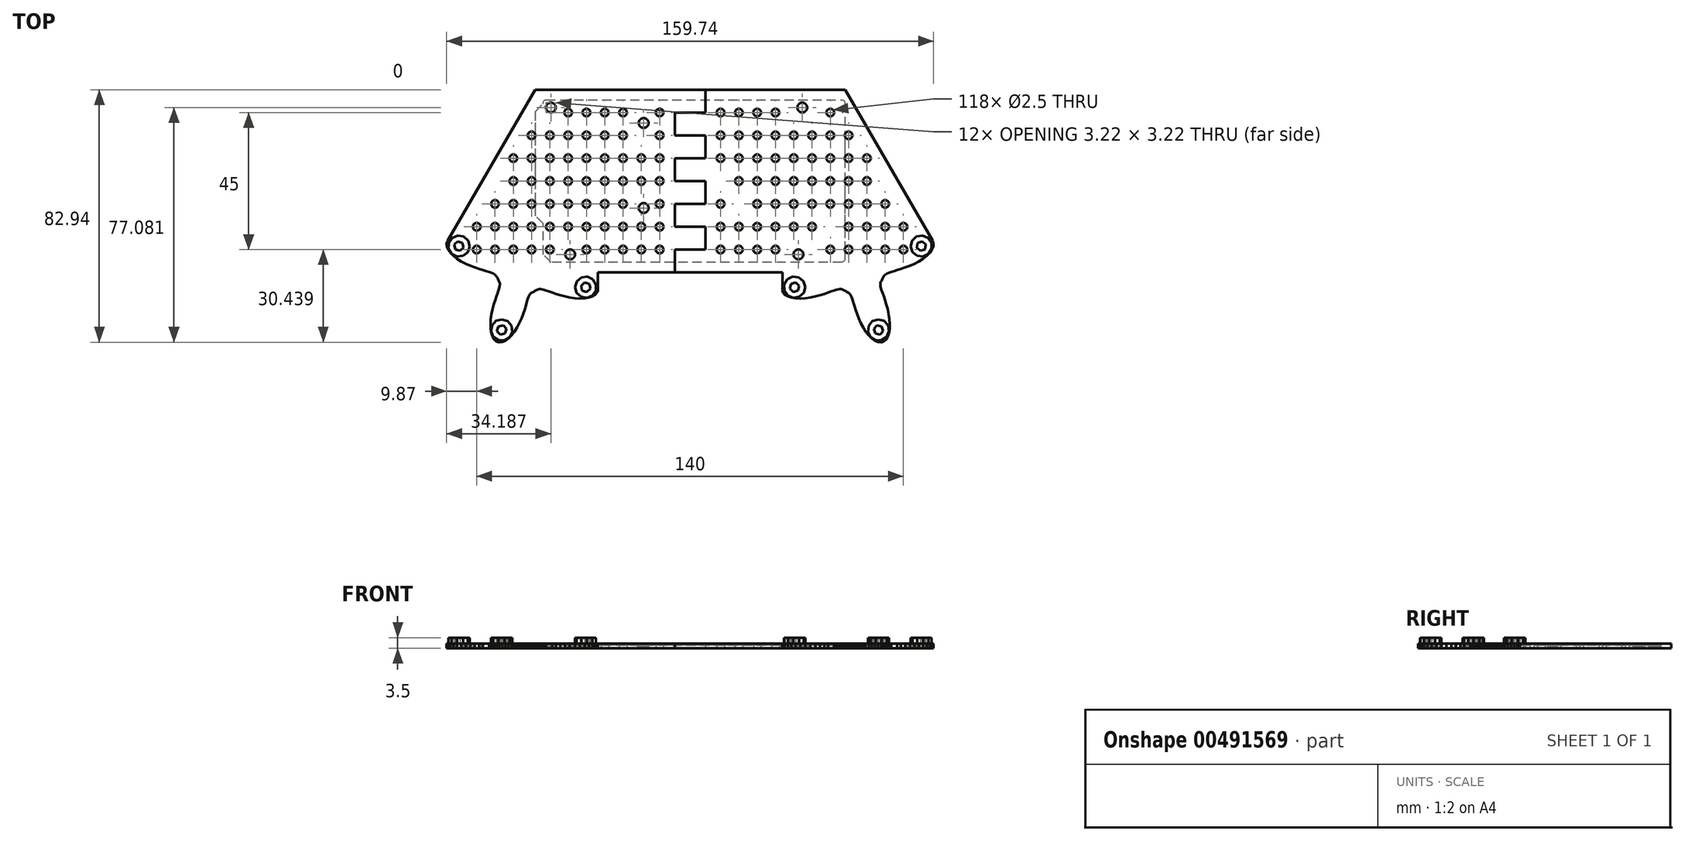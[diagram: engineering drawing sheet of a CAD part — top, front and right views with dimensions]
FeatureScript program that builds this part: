
annotation { "Feature Type Name" : "Feature", "Feature Type Description" : "" }
export const myFeature = defineFeature(function(context is Context, id is Id, definition is map)
    precondition{}
    {
        {
            var Q0;
            Q0=qCreatedBy(makeId("Top.planeOp"),FACE);
            var sketch = newSketch(context, id + "F0", { "sketchPlane" : qUnion([Q0])});
            skLineSegment(sketch, "E0", {"start": v(78.21, 11.15) * mm, "end": v(79.23, 12.84) * mm});
            skLineSegment(sketch, "E1", {"start": v(79.23, 12.84) * mm, "end": v(79.17, 14.81) * mm});
            skLineSegment(sketch, "E2", {"start": v(79.17, 14.81) * mm, "end": v(78.06, 16.44) * mm});
            skLineSegment(sketch, "E3", {"start": v(78.06, 16.44) * mm, "end": v(76.24, 17.2) * mm});
            skLineSegment(sketch, "E4", {"start": v(76.24, 17.2) * mm, "end": v(74.3, 16.87) * mm});
            skLineSegment(sketch, "E5", {"start": v(74.3, 16.87) * mm, "end": v(72.85, 15.54) * mm});
            skLineSegment(sketch, "E6", {"start": v(72.85, 15.54) * mm, "end": v(72.35, 13.63) * mm});
            skLineSegment(sketch, "E7", {"start": v(72.35, 13.63) * mm, "end": v(72.96, 11.76) * mm});
            skLineSegment(sketch, "E8", {"start": v(72.96, 11.76) * mm, "end": v(74.48, 10.5) * mm});
            skLineSegment(sketch, "E9", {"start": v(74.48, 10.5) * mm, "end": v(76.44, 10.28) * mm});
            skLineSegment(sketch, "E10", {"start": v(76.44, 10.28) * mm, "end": v(78.21, 11.15) * mm});
            skLineSegment(sketch, "E11", {"start": v(74.32, 13.24) * mm, "end": v(74.66, 14.8) * mm});
            skLineSegment(sketch, "E12", {"start": v(74.66, 14.8) * mm, "end": v(76.18, 15.3) * mm});
            skLineSegment(sketch, "E13", {"start": v(76.18, 15.3) * mm, "end": v(77.37, 14.23) * mm});
            skLineSegment(sketch, "E14", {"start": v(77.37, 14.23) * mm, "end": v(77.03, 12.66) * mm});
            skLineSegment(sketch, "E15", {"start": v(77.03, 12.66) * mm, "end": v(75.51, 12.17) * mm});
            skLineSegment(sketch, "E16", {"start": v(75.51, 12.17) * mm, "end": v(74.32, 13.24) * mm});
            skLineSegment(sketch, "E17", {"start": v(-74.48, 10.5) * mm, "end": v(-72.96, 11.76) * mm});
            skLineSegment(sketch, "E18", {"start": v(-72.96, 11.76) * mm, "end": v(-72.35, 13.63) * mm});
            skLineSegment(sketch, "E19", {"start": v(-72.35, 13.63) * mm, "end": v(-72.85, 15.54) * mm});
            skLineSegment(sketch, "E20", {"start": v(-72.85, 15.54) * mm, "end": v(-74.3, 16.87) * mm});
            skLineSegment(sketch, "E21", {"start": v(-74.3, 16.87) * mm, "end": v(-76.24, 17.2) * mm});
            skLineSegment(sketch, "E22", {"start": v(-76.24, 17.2) * mm, "end": v(-78.06, 16.44) * mm});
            skLineSegment(sketch, "E23", {"start": v(-78.06, 16.44) * mm, "end": v(-79.17, 14.81) * mm});
            skLineSegment(sketch, "E24", {"start": v(-79.17, 14.81) * mm, "end": v(-79.23, 12.84) * mm});
            skLineSegment(sketch, "E25", {"start": v(-79.23, 12.84) * mm, "end": v(-78.21, 11.15) * mm});
            skLineSegment(sketch, "E26", {"start": v(-78.21, 11.15) * mm, "end": v(-76.44, 10.28) * mm});
            skLineSegment(sketch, "E27", {"start": v(-76.44, 10.28) * mm, "end": v(-74.48, 10.5) * mm});
            skLineSegment(sketch, "E28", {"start": v(-77.03, 12.66) * mm, "end": v(-77.37, 14.23) * mm});
            skLineSegment(sketch, "E29", {"start": v(-77.37, 14.23) * mm, "end": v(-76.18, 15.3) * mm});
            skLineSegment(sketch, "E30", {"start": v(-76.18, 15.3) * mm, "end": v(-74.66, 14.8) * mm});
            skLineSegment(sketch, "E31", {"start": v(-74.66, 14.8) * mm, "end": v(-74.32, 13.24) * mm});
            skLineSegment(sketch, "E32", {"start": v(-74.32, 13.24) * mm, "end": v(-75.51, 12.17) * mm});
            skLineSegment(sketch, "E33", {"start": v(-75.51, 12.17) * mm, "end": v(-77.03, 12.66) * mm});
            skLineSegment(sketch, "E34", {"start": v(-32.03, -2.5) * mm, "end": v(-30.92, -0.87) * mm});
            skLineSegment(sketch, "E35", {"start": v(-30.92, -0.87) * mm, "end": v(-30.86, 1.1) * mm});
            skLineSegment(sketch, "E36", {"start": v(-30.86, 1.1) * mm, "end": v(-31.88, 2.8) * mm});
            skLineSegment(sketch, "E37", {"start": v(-31.88, 2.8) * mm, "end": v(-33.65, 3.67) * mm});
            skLineSegment(sketch, "E38", {"start": v(-33.65, 3.67) * mm, "end": v(-35.6, 3.44) * mm});
            skLineSegment(sketch, "E39", {"start": v(-35.6, 3.44) * mm, "end": v(-37.13, 2.2) * mm});
            skLineSegment(sketch, "E40", {"start": v(-37.13, 2.2) * mm, "end": v(-37.74, 0.32) * mm});
            skLineSegment(sketch, "E41", {"start": v(-37.74, 0.32) * mm, "end": v(-37.24, -1.6) * mm});
            skLineSegment(sketch, "E42", {"start": v(-37.24, -1.6) * mm, "end": v(-35.79, -2.92) * mm});
            skLineSegment(sketch, "E43", {"start": v(-35.79, -2.92) * mm, "end": v(-33.85, -3.26) * mm});
            skLineSegment(sketch, "E44", {"start": v(-33.85, -3.26) * mm, "end": v(-32.03, -2.5) * mm});
            skLineSegment(sketch, "E45", {"start": v(-35.43, -0.85) * mm, "end": v(-35.77, 0.71) * mm});
            skLineSegment(sketch, "E46", {"start": v(-35.77, 0.71) * mm, "end": v(-34.58, 1.78) * mm});
            skLineSegment(sketch, "E47", {"start": v(-34.58, 1.78) * mm, "end": v(-33.06, 1.29) * mm});
            skLineSegment(sketch, "E48", {"start": v(-33.06, 1.29) * mm, "end": v(-32.72, -0.28) * mm});
            skLineSegment(sketch, "E49", {"start": v(-32.72, -0.28) * mm, "end": v(-33.91, -1.35) * mm});
            skLineSegment(sketch, "E50", {"start": v(-33.91, -1.35) * mm, "end": v(-35.43, -0.85) * mm});
            skLineSegment(sketch, "E51", {"start": v(35.79, -2.92) * mm, "end": v(37.24, -1.6) * mm});
            skLineSegment(sketch, "E52", {"start": v(37.24, -1.6) * mm, "end": v(37.74, 0.32) * mm});
            skLineSegment(sketch, "E53", {"start": v(37.74, 0.32) * mm, "end": v(37.13, 2.2) * mm});
            skLineSegment(sketch, "E54", {"start": v(37.13, 2.2) * mm, "end": v(35.6, 3.44) * mm});
            skLineSegment(sketch, "E55", {"start": v(35.6, 3.44) * mm, "end": v(33.65, 3.67) * mm});
            skLineSegment(sketch, "E56", {"start": v(33.65, 3.67) * mm, "end": v(31.88, 2.8) * mm});
            skLineSegment(sketch, "E57", {"start": v(31.88, 2.8) * mm, "end": v(30.86, 1.1) * mm});
            skLineSegment(sketch, "E58", {"start": v(30.86, 1.1) * mm, "end": v(30.92, -0.87) * mm});
            skLineSegment(sketch, "E59", {"start": v(30.92, -0.87) * mm, "end": v(32.03, -2.5) * mm});
            skLineSegment(sketch, "E60", {"start": v(32.03, -2.5) * mm, "end": v(33.85, -3.26) * mm});
            skLineSegment(sketch, "E61", {"start": v(33.85, -3.26) * mm, "end": v(35.79, -2.92) * mm});
            skLineSegment(sketch, "E62", {"start": v(32.72, -0.28) * mm, "end": v(33.06, 1.29) * mm});
            skLineSegment(sketch, "E63", {"start": v(33.06, 1.29) * mm, "end": v(34.58, 1.78) * mm});
            skLineSegment(sketch, "E64", {"start": v(34.58, 1.78) * mm, "end": v(35.77, 0.71) * mm});
            skLineSegment(sketch, "E65", {"start": v(35.77, 0.71) * mm, "end": v(35.43, -0.85) * mm});
            skLineSegment(sketch, "E66", {"start": v(35.43, -0.85) * mm, "end": v(33.91, -1.35) * mm});
            skLineSegment(sketch, "E67", {"start": v(33.91, -1.35) * mm, "end": v(32.72, -0.28) * mm});
            skLineSegment(sketch, "E68", {"start": v(62.88, -17.15) * mm, "end": v(64.51, -16.04) * mm});
            skLineSegment(sketch, "E69", {"start": v(64.51, -16.04) * mm, "end": v(65.28, -14.22) * mm});
            skLineSegment(sketch, "E70", {"start": v(65.28, -14.22) * mm, "end": v(64.94, -12.28) * mm});
            skLineSegment(sketch, "E71", {"start": v(64.94, -12.28) * mm, "end": v(63.61, -10.83) * mm});
            skLineSegment(sketch, "E72", {"start": v(63.61, -10.83) * mm, "end": v(61.7, -10.33) * mm});
            skLineSegment(sketch, "E73", {"start": v(61.7, -10.33) * mm, "end": v(59.83, -10.94) * mm});
            skLineSegment(sketch, "E74", {"start": v(59.83, -10.94) * mm, "end": v(58.58, -12.46) * mm});
            skLineSegment(sketch, "E75", {"start": v(58.58, -12.46) * mm, "end": v(58.35, -14.42) * mm});
            skLineSegment(sketch, "E76", {"start": v(58.35, -14.42) * mm, "end": v(59.22, -16.2) * mm});
            skLineSegment(sketch, "E77", {"start": v(59.22, -16.2) * mm, "end": v(60.91, -17.2) * mm});
            skLineSegment(sketch, "E78", {"start": v(60.91, -17.2) * mm, "end": v(62.88, -17.15) * mm});
            skLineSegment(sketch, "E79", {"start": v(60.73, -15.01) * mm, "end": v(60.24, -13.5) * mm});
            skLineSegment(sketch, "E80", {"start": v(60.24, -13.5) * mm, "end": v(61.3, -12.3) * mm});
            skLineSegment(sketch, "E81", {"start": v(61.3, -12.3) * mm, "end": v(62.87, -12.64) * mm});
            skLineSegment(sketch, "E82", {"start": v(62.87, -12.64) * mm, "end": v(63.37, -14.16) * mm});
            skLineSegment(sketch, "E83", {"start": v(63.37, -14.16) * mm, "end": v(62.3, -15.35) * mm});
            skLineSegment(sketch, "E84", {"start": v(62.3, -15.35) * mm, "end": v(60.73, -15.01) * mm});
            skLineSegment(sketch, "E85", {"start": v(-59.22, -16.2) * mm, "end": v(-58.35, -14.42) * mm});
            skLineSegment(sketch, "E86", {"start": v(-58.35, -14.42) * mm, "end": v(-58.58, -12.46) * mm});
            skLineSegment(sketch, "E87", {"start": v(-58.58, -12.46) * mm, "end": v(-59.83, -10.94) * mm});
            skLineSegment(sketch, "E88", {"start": v(-59.83, -10.94) * mm, "end": v(-61.7, -10.33) * mm});
            skLineSegment(sketch, "E89", {"start": v(-61.7, -10.33) * mm, "end": v(-63.61, -10.83) * mm});
            skLineSegment(sketch, "E90", {"start": v(-63.61, -10.83) * mm, "end": v(-64.94, -12.28) * mm});
            skLineSegment(sketch, "E91", {"start": v(-64.94, -12.28) * mm, "end": v(-65.28, -14.22) * mm});
            skLineSegment(sketch, "E92", {"start": v(-65.28, -14.22) * mm, "end": v(-64.51, -16.04) * mm});
            skLineSegment(sketch, "E93", {"start": v(-64.51, -16.04) * mm, "end": v(-62.88, -17.15) * mm});
            skLineSegment(sketch, "E94", {"start": v(-62.88, -17.15) * mm, "end": v(-60.91, -17.2) * mm});
            skLineSegment(sketch, "E95", {"start": v(-60.91, -17.2) * mm, "end": v(-59.22, -16.2) * mm});
            skLineSegment(sketch, "E96", {"start": v(-63.37, -14.16) * mm, "end": v(-62.87, -12.64) * mm});
            skLineSegment(sketch, "E97", {"start": v(-62.87, -12.64) * mm, "end": v(-61.3, -12.3) * mm});
            skLineSegment(sketch, "E98", {"start": v(-61.3, -12.3) * mm, "end": v(-60.24, -13.5) * mm});
            skLineSegment(sketch, "E99", {"start": v(-60.24, -13.5) * mm, "end": v(-60.73, -15.01) * mm});
            skLineSegment(sketch, "E100", {"start": v(-60.73, -15.01) * mm, "end": v(-62.3, -15.35) * mm});
            skLineSegment(sketch, "E101", {"start": v(-62.3, -15.35) * mm, "end": v(-63.37, -14.16) * mm});
            skSolve(sketch);
        }
        {
            var Q0;
            Q0=qCreatedBy(makeId("Top.planeOp"),FACE);
            var sketch = newSketch(context, id + "F1", { "sketchPlane" : qUnion([Q0])});
            skLineSegment(sketch, "E102", {"start": v(63.5, -41.19) * mm, "end": v(64.23, -40.57) * mm});
            skLineSegment(sketch, "E103", {"start": v(64.23, -40.57) * mm, "end": v(64.8, -39.65) * mm});
            skLineSegment(sketch, "E104", {"start": v(64.8, -39.65) * mm, "end": v(65.22, -38.46) * mm});
            skLineSegment(sketch, "E105", {"start": v(65.22, -38.46) * mm, "end": v(65.45, -37.06) * mm});
            skLineSegment(sketch, "E106", {"start": v(65.45, -37.06) * mm, "end": v(65.5, -35.5) * mm});
            skLineSegment(sketch, "E107", {"start": v(65.5, -35.5) * mm, "end": v(65.4, -33.87) * mm});
            skLineSegment(sketch, "E108", {"start": v(65.4, -33.87) * mm, "end": v(65.15, -32.21) * mm});
            skLineSegment(sketch, "E109", {"start": v(65.15, -32.21) * mm, "end": v(64.81, -30.6) * mm});
            skLineSegment(sketch, "E110", {"start": v(64.81, -30.6) * mm, "end": v(64.4, -29.07) * mm});
            skLineSegment(sketch, "E111", {"start": v(64.4, -29.07) * mm, "end": v(63.97, -27.67) * mm});
            skLineSegment(sketch, "E112", {"start": v(63.97, -27.67) * mm, "end": v(63.55, -26.43) * mm});
            skLineSegment(sketch, "E113", {"start": v(63.55, -26.43) * mm, "end": v(63.16, -25.35) * mm});
            skLineSegment(sketch, "E114", {"start": v(63.16, -25.35) * mm, "end": v(62.84, -24.44) * mm});
            skLineSegment(sketch, "E115", {"start": v(62.84, -24.44) * mm, "end": v(62.6, -23.7) * mm});
            skLineSegment(sketch, "E116", {"start": v(62.6, -23.7) * mm, "end": v(62.46, -23.1) * mm});
            skLineSegment(sketch, "E117", {"start": v(62.46, -23.1) * mm, "end": v(62.4, -22.6) * mm});
            skLineSegment(sketch, "E118", {"start": v(62.4, -22.6) * mm, "end": v(62.42, -22.2) * mm});
            skLineSegment(sketch, "E119", {"start": v(62.42, -22.2) * mm, "end": v(62.5, -21.86) * mm});
            skLineSegment(sketch, "E120", {"start": v(62.5, -21.86) * mm, "end": v(62.62, -21.56) * mm});
            skLineSegment(sketch, "E121", {"start": v(62.62, -21.56) * mm, "end": v(62.77, -21.28) * mm});
            skLineSegment(sketch, "E122", {"start": v(62.77, -21.28) * mm, "end": v(62.92, -21) * mm});
            skLineSegment(sketch, "E123", {"start": v(62.92, -21) * mm, "end": v(63.06, -20.73) * mm});
            skLineSegment(sketch, "E124", {"start": v(63.06, -20.73) * mm, "end": v(63.2, -20.45) * mm});
            skLineSegment(sketch, "E125", {"start": v(63.2, -20.45) * mm, "end": v(63.34, -20.16) * mm});
            skLineSegment(sketch, "E126", {"start": v(63.34, -20.16) * mm, "end": v(63.48, -19.88) * mm});
            skLineSegment(sketch, "E127", {"start": v(63.48, -19.88) * mm, "end": v(63.65, -19.6) * mm});
            skLineSegment(sketch, "E128", {"start": v(63.65, -19.6) * mm, "end": v(63.87, -19.34) * mm});
            skLineSegment(sketch, "E129", {"start": v(63.87, -19.34) * mm, "end": v(64.19, -19.1) * mm});
            skLineSegment(sketch, "E130", {"start": v(64.19, -19.1) * mm, "end": v(64.62, -18.86) * mm});
            skLineSegment(sketch, "E131", {"start": v(64.62, -18.86) * mm, "end": v(65.2, -18.62) * mm});
            skLineSegment(sketch, "E132", {"start": v(65.2, -18.62) * mm, "end": v(65.94, -18.37) * mm});
            skLineSegment(sketch, "E133", {"start": v(65.94, -18.37) * mm, "end": v(66.86, -18.1) * mm});
            skLineSegment(sketch, "E134", {"start": v(66.86, -18.1) * mm, "end": v(67.95, -17.77) * mm});
            skLineSegment(sketch, "E135", {"start": v(67.95, -17.77) * mm, "end": v(69.21, -17.39) * mm});
            skLineSegment(sketch, "E136", {"start": v(69.21, -17.39) * mm, "end": v(70.6, -16.92) * mm});
            skLineSegment(sketch, "E137", {"start": v(70.6, -16.92) * mm, "end": v(72.07, -16.35) * mm});
            skLineSegment(sketch, "E138", {"start": v(72.07, -16.35) * mm, "end": v(73.58, -15.67) * mm});
            skLineSegment(sketch, "E139", {"start": v(73.58, -15.67) * mm, "end": v(75.06, -14.9) * mm});
            skLineSegment(sketch, "E140", {"start": v(75.06, -14.9) * mm, "end": v(76.45, -14.02) * mm});
            skLineSegment(sketch, "E141", {"start": v(76.45, -14.02) * mm, "end": v(77.67, -13.06) * mm});
            skLineSegment(sketch, "E142", {"start": v(77.67, -13.06) * mm, "end": v(78.67, -12.05) * mm});
            skLineSegment(sketch, "E143", {"start": v(78.67, -12.05) * mm, "end": v(79.4, -11.02) * mm});
            skLineSegment(sketch, "E144", {"start": v(79.4, -11.02) * mm, "end": v(79.8, -10.01) * mm});
            skLineSegment(sketch, "E145", {"start": v(79.8, -10.01) * mm, "end": v(79.87, -9.06) * mm});
            skLineSegment(sketch, "E146", {"start": v(79.87, -9.06) * mm, "end": v(79.59, -8.2) * mm});
            skLineSegment(sketch, "E147", {"start": v(79.59, -8.2) * mm, "end": v(79.56, -8.15) * mm});
            skLineSegment(sketch, "E148", {"start": v(79.56, -8.15) * mm, "end": v(50.85, 41.47) * mm});
            skLineSegment(sketch, "E149", {"start": v(50.85, 41.47) * mm, "end": v(-50.85, 41.47) * mm});
            skLineSegment(sketch, "E150", {"start": v(-50.85, 41.47) * mm, "end": v(-79.56, -8.15) * mm});
            skLineSegment(sketch, "E151", {"start": v(-79.56, -8.15) * mm, "end": v(-79.59, -8.2) * mm});
            skLineSegment(sketch, "E152", {"start": v(-79.59, -8.2) * mm, "end": v(-79.87, -9.06) * mm});
            skLineSegment(sketch, "E153", {"start": v(-79.87, -9.06) * mm, "end": v(-79.8, -10.01) * mm});
            skLineSegment(sketch, "E154", {"start": v(-79.8, -10.01) * mm, "end": v(-79.4, -11.02) * mm});
            skLineSegment(sketch, "E155", {"start": v(-79.4, -11.02) * mm, "end": v(-78.67, -12.05) * mm});
            skLineSegment(sketch, "E156", {"start": v(-78.67, -12.05) * mm, "end": v(-77.67, -13.06) * mm});
            skLineSegment(sketch, "E157", {"start": v(-77.67, -13.06) * mm, "end": v(-76.45, -14.02) * mm});
            skLineSegment(sketch, "E158", {"start": v(-76.45, -14.02) * mm, "end": v(-75.06, -14.9) * mm});
            skLineSegment(sketch, "E159", {"start": v(-75.06, -14.9) * mm, "end": v(-73.58, -15.67) * mm});
            skLineSegment(sketch, "E160", {"start": v(-73.58, -15.67) * mm, "end": v(-72.07, -16.35) * mm});
            skLineSegment(sketch, "E161", {"start": v(-72.07, -16.35) * mm, "end": v(-70.6, -16.92) * mm});
            skLineSegment(sketch, "E162", {"start": v(-70.6, -16.92) * mm, "end": v(-69.21, -17.39) * mm});
            skLineSegment(sketch, "E163", {"start": v(-69.21, -17.39) * mm, "end": v(-67.95, -17.77) * mm});
            skLineSegment(sketch, "E164", {"start": v(-67.95, -17.77) * mm, "end": v(-66.86, -18.1) * mm});
            skLineSegment(sketch, "E165", {"start": v(-66.86, -18.1) * mm, "end": v(-65.94, -18.37) * mm});
            skLineSegment(sketch, "E166", {"start": v(-65.94, -18.37) * mm, "end": v(-65.2, -18.62) * mm});
            skLineSegment(sketch, "E167", {"start": v(-65.2, -18.62) * mm, "end": v(-64.62, -18.86) * mm});
            skLineSegment(sketch, "E168", {"start": v(-64.62, -18.86) * mm, "end": v(-64.19, -19.1) * mm});
            skLineSegment(sketch, "E169", {"start": v(-64.19, -19.1) * mm, "end": v(-63.87, -19.34) * mm});
            skLineSegment(sketch, "E170", {"start": v(-63.87, -19.34) * mm, "end": v(-63.65, -19.6) * mm});
            skLineSegment(sketch, "E171", {"start": v(-63.65, -19.6) * mm, "end": v(-63.48, -19.88) * mm});
            skLineSegment(sketch, "E172", {"start": v(-63.48, -19.88) * mm, "end": v(-63.34, -20.16) * mm});
            skLineSegment(sketch, "E173", {"start": v(-63.34, -20.16) * mm, "end": v(-63.2, -20.45) * mm});
            skLineSegment(sketch, "E174", {"start": v(-63.2, -20.45) * mm, "end": v(-63.06, -20.73) * mm});
            skLineSegment(sketch, "E175", {"start": v(-63.06, -20.73) * mm, "end": v(-62.92, -21) * mm});
            skLineSegment(sketch, "E176", {"start": v(-62.92, -21) * mm, "end": v(-62.77, -21.28) * mm});
            skLineSegment(sketch, "E177", {"start": v(-62.77, -21.28) * mm, "end": v(-62.62, -21.56) * mm});
            skLineSegment(sketch, "E178", {"start": v(-62.62, -21.56) * mm, "end": v(-62.5, -21.86) * mm});
            skLineSegment(sketch, "E179", {"start": v(-62.5, -21.86) * mm, "end": v(-62.42, -22.2) * mm});
            skLineSegment(sketch, "E180", {"start": v(-62.42, -22.2) * mm, "end": v(-62.4, -22.6) * mm});
            skLineSegment(sketch, "E181", {"start": v(-62.4, -22.6) * mm, "end": v(-62.46, -23.1) * mm});
            skLineSegment(sketch, "E182", {"start": v(-62.46, -23.1) * mm, "end": v(-62.6, -23.7) * mm});
            skLineSegment(sketch, "E183", {"start": v(-62.6, -23.7) * mm, "end": v(-62.84, -24.44) * mm});
            skLineSegment(sketch, "E184", {"start": v(-62.84, -24.44) * mm, "end": v(-63.16, -25.35) * mm});
            skLineSegment(sketch, "E185", {"start": v(-63.16, -25.35) * mm, "end": v(-63.55, -26.43) * mm});
            skLineSegment(sketch, "E186", {"start": v(-63.55, -26.43) * mm, "end": v(-63.97, -27.67) * mm});
            skLineSegment(sketch, "E187", {"start": v(-63.97, -27.67) * mm, "end": v(-64.4, -29.07) * mm});
            skLineSegment(sketch, "E188", {"start": v(-64.4, -29.07) * mm, "end": v(-64.81, -30.6) * mm});
            skLineSegment(sketch, "E189", {"start": v(-64.81, -30.6) * mm, "end": v(-65.15, -32.21) * mm});
            skLineSegment(sketch, "E190", {"start": v(-65.15, -32.21) * mm, "end": v(-65.4, -33.87) * mm});
            skLineSegment(sketch, "E191", {"start": v(-65.4, -33.87) * mm, "end": v(-65.5, -35.5) * mm});
            skLineSegment(sketch, "E192", {"start": v(-65.5, -35.5) * mm, "end": v(-65.45, -37.06) * mm});
            skLineSegment(sketch, "E193", {"start": v(-65.45, -37.06) * mm, "end": v(-65.22, -38.46) * mm});
            skLineSegment(sketch, "E194", {"start": v(-65.22, -38.46) * mm, "end": v(-64.8, -39.65) * mm});
            skLineSegment(sketch, "E195", {"start": v(-64.8, -39.65) * mm, "end": v(-64.23, -40.57) * mm});
            skLineSegment(sketch, "E196", {"start": v(-64.23, -40.57) * mm, "end": v(-63.5, -41.19) * mm});
            skLineSegment(sketch, "E197", {"start": v(-63.5, -41.19) * mm, "end": v(-62.63, -41.47) * mm});
            skLineSegment(sketch, "E198", {"start": v(-62.63, -41.47) * mm, "end": v(-61.68, -41.4) * mm});
            skLineSegment(sketch, "E199", {"start": v(-61.68, -41.4) * mm, "end": v(-60.67, -41) * mm});
            skLineSegment(sketch, "E200", {"start": v(-60.67, -41) * mm, "end": v(-59.64, -40.27) * mm});
            skLineSegment(sketch, "E201", {"start": v(-59.64, -40.27) * mm, "end": v(-58.63, -39.27) * mm});
            skLineSegment(sketch, "E202", {"start": v(-58.63, -39.27) * mm, "end": v(-57.67, -38.05) * mm});
            skLineSegment(sketch, "E203", {"start": v(-57.67, -38.05) * mm, "end": v(-56.8, -36.66) * mm});
            skLineSegment(sketch, "E204", {"start": v(-56.8, -36.66) * mm, "end": v(-56.02, -35.18) * mm});
            skLineSegment(sketch, "E205", {"start": v(-56.02, -35.18) * mm, "end": v(-55.34, -33.67) * mm});
            skLineSegment(sketch, "E206", {"start": v(-55.34, -33.67) * mm, "end": v(-54.77, -32.2) * mm});
            skLineSegment(sketch, "E207", {"start": v(-54.77, -32.2) * mm, "end": v(-54.3, -30.81) * mm});
            skLineSegment(sketch, "E208", {"start": v(-54.3, -30.81) * mm, "end": v(-53.92, -29.55) * mm});
            skLineSegment(sketch, "E209", {"start": v(-53.92, -29.55) * mm, "end": v(-53.6, -28.46) * mm});
            skLineSegment(sketch, "E210", {"start": v(-53.6, -28.46) * mm, "end": v(-53.32, -27.54) * mm});
            skLineSegment(sketch, "E211", {"start": v(-53.32, -27.54) * mm, "end": v(-53.07, -26.8) * mm});
            skLineSegment(sketch, "E212", {"start": v(-53.07, -26.8) * mm, "end": v(-52.83, -26.22) * mm});
            skLineSegment(sketch, "E213", {"start": v(-52.83, -26.22) * mm, "end": v(-52.6, -25.79) * mm});
            skLineSegment(sketch, "E214", {"start": v(-52.6, -25.79) * mm, "end": v(-52.35, -25.47) * mm});
            skLineSegment(sketch, "E215", {"start": v(-52.35, -25.47) * mm, "end": v(-52.08, -25.25) * mm});
            skLineSegment(sketch, "E216", {"start": v(-52.08, -25.25) * mm, "end": v(-51.8, -25.08) * mm});
            skLineSegment(sketch, "E217", {"start": v(-51.8, -25.08) * mm, "end": v(-51.53, -24.94) * mm});
            skLineSegment(sketch, "E218", {"start": v(-51.53, -24.94) * mm, "end": v(-51.24, -24.8) * mm});
            skLineSegment(sketch, "E219", {"start": v(-51.24, -24.8) * mm, "end": v(-50.96, -24.66) * mm});
            skLineSegment(sketch, "E220", {"start": v(-50.96, -24.66) * mm, "end": v(-50.68, -24.52) * mm});
            skLineSegment(sketch, "E221", {"start": v(-50.68, -24.52) * mm, "end": v(-50.4, -24.37) * mm});
            skLineSegment(sketch, "E222", {"start": v(-50.4, -24.37) * mm, "end": v(-50.13, -24.22) * mm});
            skLineSegment(sketch, "E223", {"start": v(-50.13, -24.22) * mm, "end": v(-49.83, -24.1) * mm});
            skLineSegment(sketch, "E224", {"start": v(-49.83, -24.1) * mm, "end": v(-49.49, -24.02) * mm});
            skLineSegment(sketch, "E225", {"start": v(-49.49, -24.02) * mm, "end": v(-49.09, -24) * mm});
            skLineSegment(sketch, "E226", {"start": v(-49.09, -24) * mm, "end": v(-48.6, -24.06) * mm});
            skLineSegment(sketch, "E227", {"start": v(-48.6, -24.06) * mm, "end": v(-48, -24.2) * mm});
            skLineSegment(sketch, "E228", {"start": v(-48, -24.2) * mm, "end": v(-47.25, -24.44) * mm});
            skLineSegment(sketch, "E229", {"start": v(-47.25, -24.44) * mm, "end": v(-46.34, -24.76) * mm});
            skLineSegment(sketch, "E230", {"start": v(-46.34, -24.76) * mm, "end": v(-45.27, -25.15) * mm});
            skLineSegment(sketch, "E231", {"start": v(-45.27, -25.15) * mm, "end": v(-44.02, -25.57) * mm});
            skLineSegment(sketch, "E232", {"start": v(-44.02, -25.57) * mm, "end": v(-42.62, -26) * mm});
            skLineSegment(sketch, "E233", {"start": v(-42.62, -26) * mm, "end": v(-41.1, -26.41) * mm});
            skLineSegment(sketch, "E234", {"start": v(-41.1, -26.41) * mm, "end": v(-39.48, -26.76) * mm});
            skLineSegment(sketch, "E235", {"start": v(-39.48, -26.76) * mm, "end": v(-37.82, -27) * mm});
            skLineSegment(sketch, "E236", {"start": v(-37.82, -27) * mm, "end": v(-36.19, -27.1) * mm});
            skLineSegment(sketch, "E237", {"start": v(-36.19, -27.1) * mm, "end": v(-34.63, -27.05) * mm});
            skLineSegment(sketch, "E238", {"start": v(-34.63, -27.05) * mm, "end": v(-33.23, -26.82) * mm});
            skLineSegment(sketch, "E239", {"start": v(-33.23, -26.82) * mm, "end": v(-32.04, -26.4) * mm});
            skLineSegment(sketch, "E240", {"start": v(-32.04, -26.4) * mm, "end": v(-31.12, -25.83) * mm});
            skLineSegment(sketch, "E241", {"start": v(-31.12, -25.83) * mm, "end": v(-30.5, -25.1) * mm});
            skLineSegment(sketch, "E242", {"start": v(-30.5, -25.1) * mm, "end": v(-30.31, -24.51) * mm});
            skLineSegment(sketch, "E243", {"start": v(-30.31, -24.51) * mm, "end": v(-30.25, -24.53) * mm});
            skLineSegment(sketch, "E244", {"start": v(-30.25, -24.53) * mm, "end": v(-30.25, -24.32) * mm});
            skLineSegment(sketch, "E245", {"start": v(-30.25, -24.32) * mm, "end": v(-30.22, -24.23) * mm});
            skLineSegment(sketch, "E246", {"start": v(-30.22, -24.23) * mm, "end": v(-30.25, -23.82) * mm});
            skLineSegment(sketch, "E247", {"start": v(-30.25, -23.82) * mm, "end": v(-30.25, -18.53) * mm});
            skLineSegment(sketch, "E248", {"start": v(-30.25, -18.53) * mm, "end": v(30.25, -18.53) * mm});
            skLineSegment(sketch, "E249", {"start": v(30.25, -18.53) * mm, "end": v(30.25, -23.82) * mm});
            skLineSegment(sketch, "E250", {"start": v(30.25, -23.82) * mm, "end": v(30.22, -24.23) * mm});
            skLineSegment(sketch, "E251", {"start": v(30.22, -24.23) * mm, "end": v(30.25, -24.32) * mm});
            skLineSegment(sketch, "E252", {"start": v(30.25, -24.32) * mm, "end": v(30.25, -24.53) * mm});
            skLineSegment(sketch, "E253", {"start": v(30.25, -24.53) * mm, "end": v(30.31, -24.51) * mm});
            skLineSegment(sketch, "E254", {"start": v(30.31, -24.51) * mm, "end": v(30.5, -25.1) * mm});
            skLineSegment(sketch, "E255", {"start": v(30.5, -25.1) * mm, "end": v(31.12, -25.83) * mm});
            skLineSegment(sketch, "E256", {"start": v(31.12, -25.83) * mm, "end": v(32.04, -26.4) * mm});
            skLineSegment(sketch, "E257", {"start": v(32.04, -26.4) * mm, "end": v(33.23, -26.82) * mm});
            skLineSegment(sketch, "E258", {"start": v(33.23, -26.82) * mm, "end": v(34.63, -27.05) * mm});
            skLineSegment(sketch, "E259", {"start": v(34.63, -27.05) * mm, "end": v(36.19, -27.1) * mm});
            skLineSegment(sketch, "E260", {"start": v(36.19, -27.1) * mm, "end": v(37.82, -27) * mm});
            skLineSegment(sketch, "E261", {"start": v(37.82, -27) * mm, "end": v(39.48, -26.76) * mm});
            skLineSegment(sketch, "E262", {"start": v(39.48, -26.76) * mm, "end": v(41.1, -26.41) * mm});
            skLineSegment(sketch, "E263", {"start": v(41.1, -26.41) * mm, "end": v(42.62, -26) * mm});
            skLineSegment(sketch, "E264", {"start": v(42.62, -26) * mm, "end": v(44.02, -25.57) * mm});
            skLineSegment(sketch, "E265", {"start": v(44.02, -25.57) * mm, "end": v(45.27, -25.15) * mm});
            skLineSegment(sketch, "E266", {"start": v(45.27, -25.15) * mm, "end": v(46.34, -24.76) * mm});
            skLineSegment(sketch, "E267", {"start": v(46.34, -24.76) * mm, "end": v(47.25, -24.44) * mm});
            skLineSegment(sketch, "E268", {"start": v(47.25, -24.44) * mm, "end": v(48, -24.2) * mm});
            skLineSegment(sketch, "E269", {"start": v(48, -24.2) * mm, "end": v(48.6, -24.06) * mm});
            skLineSegment(sketch, "E270", {"start": v(48.6, -24.06) * mm, "end": v(49.09, -24) * mm});
            skLineSegment(sketch, "E271", {"start": v(49.09, -24) * mm, "end": v(49.49, -24.02) * mm});
            skLineSegment(sketch, "E272", {"start": v(49.49, -24.02) * mm, "end": v(49.83, -24.1) * mm});
            skLineSegment(sketch, "E273", {"start": v(49.83, -24.1) * mm, "end": v(50.13, -24.22) * mm});
            skLineSegment(sketch, "E274", {"start": v(50.13, -24.22) * mm, "end": v(50.4, -24.37) * mm});
            skLineSegment(sketch, "E275", {"start": v(50.4, -24.37) * mm, "end": v(50.68, -24.52) * mm});
            skLineSegment(sketch, "E276", {"start": v(50.68, -24.52) * mm, "end": v(50.96, -24.66) * mm});
            skLineSegment(sketch, "E277", {"start": v(50.96, -24.66) * mm, "end": v(51.24, -24.8) * mm});
            skLineSegment(sketch, "E278", {"start": v(51.24, -24.8) * mm, "end": v(51.53, -24.94) * mm});
            skLineSegment(sketch, "E279", {"start": v(51.53, -24.94) * mm, "end": v(51.8, -25.08) * mm});
            skLineSegment(sketch, "E280", {"start": v(51.8, -25.08) * mm, "end": v(52.08, -25.25) * mm});
            skLineSegment(sketch, "E281", {"start": v(52.08, -25.25) * mm, "end": v(52.35, -25.47) * mm});
            skLineSegment(sketch, "E282", {"start": v(52.35, -25.47) * mm, "end": v(52.6, -25.79) * mm});
            skLineSegment(sketch, "E283", {"start": v(52.6, -25.79) * mm, "end": v(52.83, -26.22) * mm});
            skLineSegment(sketch, "E284", {"start": v(52.83, -26.22) * mm, "end": v(53.07, -26.8) * mm});
            skLineSegment(sketch, "E285", {"start": v(53.07, -26.8) * mm, "end": v(53.32, -27.54) * mm});
            skLineSegment(sketch, "E286", {"start": v(53.32, -27.54) * mm, "end": v(53.6, -28.46) * mm});
            skLineSegment(sketch, "E287", {"start": v(53.6, -28.46) * mm, "end": v(53.92, -29.55) * mm});
            skLineSegment(sketch, "E288", {"start": v(53.92, -29.55) * mm, "end": v(54.3, -30.81) * mm});
            skLineSegment(sketch, "E289", {"start": v(54.3, -30.81) * mm, "end": v(54.77, -32.2) * mm});
            skLineSegment(sketch, "E290", {"start": v(54.77, -32.2) * mm, "end": v(55.34, -33.67) * mm});
            skLineSegment(sketch, "E291", {"start": v(55.34, -33.67) * mm, "end": v(56.02, -35.18) * mm});
            skLineSegment(sketch, "E292", {"start": v(56.02, -35.18) * mm, "end": v(56.8, -36.66) * mm});
            skLineSegment(sketch, "E293", {"start": v(56.8, -36.66) * mm, "end": v(57.67, -38.05) * mm});
            skLineSegment(sketch, "E294", {"start": v(57.67, -38.05) * mm, "end": v(58.63, -39.27) * mm});
            skLineSegment(sketch, "E295", {"start": v(58.63, -39.27) * mm, "end": v(59.64, -40.27) * mm});
            skLineSegment(sketch, "E296", {"start": v(59.64, -40.27) * mm, "end": v(60.67, -41) * mm});
            skLineSegment(sketch, "E297", {"start": v(60.67, -41) * mm, "end": v(61.68, -41.4) * mm});
            skLineSegment(sketch, "E298", {"start": v(61.68, -41.4) * mm, "end": v(62.63, -41.47) * mm});
            skLineSegment(sketch, "E299", {"start": v(62.63, -41.47) * mm, "end": v(63.5, -41.19) * mm});
            skLineSegment(sketch, "E300", {"start": v(74.32, -10.38) * mm, "end": v(74.66, -8.82) * mm});
            skLineSegment(sketch, "E301", {"start": v(74.66, -8.82) * mm, "end": v(76.18, -8.32) * mm});
            skLineSegment(sketch, "E302", {"start": v(76.18, -8.32) * mm, "end": v(77.37, -9.4) * mm});
            skLineSegment(sketch, "E303", {"start": v(77.37, -9.4) * mm, "end": v(77.03, -10.96) * mm});
            skLineSegment(sketch, "E304", {"start": v(77.03, -10.96) * mm, "end": v(75.51, -11.45) * mm});
            skLineSegment(sketch, "E305", {"start": v(75.51, -11.45) * mm, "end": v(74.32, -10.38) * mm});
            skLineSegment(sketch, "E306", {"start": v(-77.03, -10.96) * mm, "end": v(-77.37, -9.4) * mm});
            skLineSegment(sketch, "E307", {"start": v(-77.37, -9.4) * mm, "end": v(-76.18, -8.32) * mm});
            skLineSegment(sketch, "E308", {"start": v(-76.18, -8.32) * mm, "end": v(-74.66, -8.82) * mm});
            skLineSegment(sketch, "E309", {"start": v(-74.66, -8.82) * mm, "end": v(-74.32, -10.38) * mm});
            skLineSegment(sketch, "E310", {"start": v(-74.32, -10.38) * mm, "end": v(-75.51, -11.45) * mm});
            skLineSegment(sketch, "E311", {"start": v(-75.51, -11.45) * mm, "end": v(-77.03, -10.96) * mm});
            skLineSegment(sketch, "E312", {"start": v(32.72, -23.9) * mm, "end": v(33.06, -22.33) * mm});
            skLineSegment(sketch, "E313", {"start": v(33.06, -22.33) * mm, "end": v(34.58, -21.84) * mm});
            skLineSegment(sketch, "E314", {"start": v(34.58, -21.84) * mm, "end": v(35.77, -22.9) * mm});
            skLineSegment(sketch, "E315", {"start": v(35.77, -22.9) * mm, "end": v(35.43, -24.47) * mm});
            skLineSegment(sketch, "E316", {"start": v(35.43, -24.47) * mm, "end": v(33.91, -24.97) * mm});
            skLineSegment(sketch, "E317", {"start": v(33.91, -24.97) * mm, "end": v(32.72, -23.9) * mm});
            skLineSegment(sketch, "E318", {"start": v(-35.43, -24.47) * mm, "end": v(-35.77, -22.9) * mm});
            skLineSegment(sketch, "E319", {"start": v(-34.58, -21.84) * mm, "end": v(-33.06, -22.33) * mm});
            skLineSegment(sketch, "E320", {"start": v(-33.06, -22.33) * mm, "end": v(-32.72, -23.9) * mm});
            skLineSegment(sketch, "E321", {"start": v(-32.72, -23.9) * mm, "end": v(-33.91, -24.97) * mm});
            skLineSegment(sketch, "E322", {"start": v(-33.91, -24.97) * mm, "end": v(-35.43, -24.47) * mm});
            skLineSegment(sketch, "E323", {"start": v(-63.37, -37.78) * mm, "end": v(-62.87, -36.26) * mm});
            skLineSegment(sketch, "E324", {"start": v(-62.87, -36.26) * mm, "end": v(-61.3, -35.92) * mm});
            skLineSegment(sketch, "E325", {"start": v(-61.3, -35.92) * mm, "end": v(-60.24, -37.11) * mm});
            skLineSegment(sketch, "E326", {"start": v(-60.24, -37.11) * mm, "end": v(-60.73, -38.63) * mm});
            skLineSegment(sketch, "E327", {"start": v(-60.73, -38.63) * mm, "end": v(-62.3, -38.97) * mm});
            skLineSegment(sketch, "E328", {"start": v(-62.3, -38.97) * mm, "end": v(-63.37, -37.78) * mm});
            skLineSegment(sketch, "E329", {"start": v(60.73, -38.63) * mm, "end": v(60.24, -37.11) * mm});
            skLineSegment(sketch, "E330", {"start": v(60.24, -37.11) * mm, "end": v(61.3, -35.92) * mm});
            skLineSegment(sketch, "E331", {"start": v(61.3, -35.92) * mm, "end": v(62.87, -36.26) * mm});
            skLineSegment(sketch, "E332", {"start": v(62.87, -36.26) * mm, "end": v(63.37, -37.78) * mm});
            skLineSegment(sketch, "E333", {"start": v(63.37, -37.78) * mm, "end": v(62.3, -38.97) * mm});
            skLineSegment(sketch, "E334", {"start": v(62.3, -38.97) * mm, "end": v(60.73, -38.63) * mm});
            skLineSegment(sketch, "E335", {"start": v(0, 41.47) * mm, "end": v(10, 41.47) * mm, "construction": true});
            skPoint(sketch, "E336.orphan", {"position": v(-10, 41.47) * mm});
            skLineSegment(sketch, "E337", {"start": v(-35.77, -22.9) * mm, "end": v(-34.58, -21.84) * mm});
            skLineSegment(sketch, "E338", {"start": v(0, 41.47) * mm, "end": v(0, -18.53) * mm});
            skLineSegment(sketch, "E339", {"start": v(-10, 11.47) * mm, "end": v(-10, -3.53) * mm, "construction": true});
            skLineSegment(sketch, "E340", {"start": v(10, 11.47) * mm, "end": v(10, -3.53) * mm, "construction": true});
            skLineSegment(sketch, "E341", {"start": v(-10, 11.47) * mm, "end": v(0, 11.47) * mm, "construction": true});
            skLineSegment(sketch, "E342", {"start": v(-10, -3.53) * mm, "end": v(0, -3.53) * mm, "construction": true});
            skLineSegment(sketch, "E343", {"start": v(-10, 11.47) * mm, "end": v(-10, 26.47) * mm, "construction": true});
            skLineSegment(sketch, "E344", {"start": v(10, 11.47) * mm, "end": v(10, 26.47) * mm, "construction": true});
            skLineSegment(sketch, "E345", {"start": v(-10, 26.47) * mm, "end": v(0, 26.47) * mm, "construction": true});
            skPoint(sketch, "E346.orphan", {"position": v(-10, -18.53) * mm});
            skPoint(sketch, "E347.orphan", {"position": v(10, -18.53) * mm});
            skLineSegment(sketch, "E348", {"start": v(-10, 26.47) * mm, "end": v(-10, 41.47) * mm, "construction": true});
            skLineSegment(sketch, "E349", {"start": v(10, 26.47) * mm, "end": v(10, 41.47) * mm, "construction": true});
            skLineSegment(sketch, "E350", {"start": v(-10, -3.53) * mm, "end": v(-10, -18.53) * mm, "construction": true});
            skLineSegment(sketch, "E351", {"start": v(10, -3.53) * mm, "end": v(10, -18.53) * mm, "construction": true});
            skLineSegment(sketch, "E352", {"start": v(-10, 33.97) * mm, "end": v(0, 33.97) * mm, "construction": true});
            skLineSegment(sketch, "E353", {"start": v(-10, -11.03) * mm, "end": v(0, -11.03) * mm, "construction": true});
            skLineSegment(sketch, "E354", {"start": v(-10, 18.97) * mm, "end": v(0, 18.97) * mm, "construction": true});
            skLineSegment(sketch, "E355", {"start": v(-10, 3.97) * mm, "end": v(0, 3.97) * mm, "construction": true});
            skPoint(sketch, "E356.orphan", {"position": v(10, 33.97) * mm});
            skPoint(sketch, "E357.orphan", {"position": v(10, 18.97) * mm});
            skPoint(sketch, "E358.orphan", {"position": v(10, 3.97) * mm});
            skPoint(sketch, "E359.orphan", {"position": v(10, -11.03) * mm});
            skLineSegment(sketch, "E360.MirrorCS", {"start": v(10, 33.97) * mm, "end": v(0, 33.97) * mm, "construction": true});
            skLineSegment(sketch, "E361.MirrorCS", {"start": v(10, 26.47) * mm, "end": v(0, 26.47) * mm, "construction": true});
            skLineSegment(sketch, "E362.MirrorCS", {"start": v(10, 18.97) * mm, "end": v(0, 18.97) * mm, "construction": true});
            skLineSegment(sketch, "E363.MirrorCS", {"start": v(10, 11.47) * mm, "end": v(0, 11.47) * mm, "construction": true});
            skLineSegment(sketch, "E364.MirrorCS", {"start": v(10, 3.97) * mm, "end": v(0, 3.97) * mm, "construction": true});
            skLineSegment(sketch, "E365.MirrorCS", {"start": v(10, -3.53) * mm, "end": v(0, -3.53) * mm, "construction": true});
            skLineSegment(sketch, "E366.MirrorCS", {"start": v(10, -11.03) * mm, "end": v(0, -11.03) * mm, "construction": true});
            skLineSegment(sketch, "E367", {"start": v(-5, 33.97) * mm, "end": v(-5, 26.47) * mm});
            skLineSegment(sketch, "E368", {"start": v(5, 26.47) * mm, "end": v(5, 18.97) * mm});
            skLineSegment(sketch, "E369", {"start": v(-5, 18.97) * mm, "end": v(-5, 11.47) * mm});
            skLineSegment(sketch, "E370", {"start": v(5, 11.47) * mm, "end": v(5, 3.97) * mm});
            skLineSegment(sketch, "E371", {"start": v(-5, 3.97) * mm, "end": v(-5, -3.53) * mm});
            skLineSegment(sketch, "E372", {"start": v(5, -3.53) * mm, "end": v(5, -11.03) * mm});
            skLineSegment(sketch, "E373", {"start": v(-5, -11.03) * mm, "end": v(-5, -18.53) * mm});
            skLineSegment(sketch, "E374", {"start": v(5, 33.97) * mm, "end": v(5, 41.47) * mm});
            skLineSegment(sketch, "E375", {"start": v(5, 33.97) * mm, "end": v(-5, 33.97) * mm});
            skLineSegment(sketch, "E376", {"start": v(-5, 26.47) * mm, "end": v(5, 26.47) * mm});
            skLineSegment(sketch, "E377", {"start": v(5, 18.97) * mm, "end": v(-5, 18.97) * mm});
            skLineSegment(sketch, "E378", {"start": v(-5, 11.47) * mm, "end": v(5, 11.47) * mm});
            skLineSegment(sketch, "E379", {"start": v(5, 3.97) * mm, "end": v(-5, 3.97) * mm});
            skLineSegment(sketch, "E380", {"start": v(-5, -3.53) * mm, "end": v(5, -3.53) * mm});
            skLineSegment(sketch, "E381", {"start": v(5, -11.03) * mm, "end": v(-5, -11.03) * mm});
            skCircle(sketch, "E382", {"center": v(-10, -11.03) * mm, "radius": 1.25 * mm});
            skCircle(sketch, "E383", {"center": v(-10, -3.53) * mm, "radius": 1.25 * mm});
            skCircle(sketch, "E384", {"center": v(-10, 3.97) * mm, "radius": 1.25 * mm});
            skCircle(sketch, "E385", {"center": v(-10, 11.47) * mm, "radius": 1.25 * mm});
            skCircle(sketch, "E386", {"center": v(-10, 18.97) * mm, "radius": 1.25 * mm});
            skCircle(sketch, "E387", {"center": v(-10, 26.47) * mm, "radius": 1.25 * mm});
            skCircle(sketch, "E388", {"center": v(-10, 33.97) * mm, "radius": 1.25 * mm});
            skCircle(sketch, "E389.1.0.0", {"center": v(-16, -11.03) * mm, "radius": 1.25 * mm});
            skCircle(sketch, "E389.1.0.1", {"center": v(-16, -3.53) * mm, "radius": 1.25 * mm});
            skCircle(sketch, "E389.1.0.3", {"center": v(-16, 11.47) * mm, "radius": 1.25 * mm});
            skCircle(sketch, "E389.1.0.4", {"center": v(-16, 18.97) * mm, "radius": 1.25 * mm});
            skCircle(sketch, "E389.2.0.0", {"center": v(-22, -11.03) * mm, "radius": 1.25 * mm});
            skCircle(sketch, "E389.2.0.1", {"center": v(-22, -3.53) * mm, "radius": 1.25 * mm});
            skCircle(sketch, "E389.2.0.2", {"center": v(-22, 3.97) * mm, "radius": 1.25 * mm});
            skCircle(sketch, "E389.2.0.3", {"center": v(-22, 11.47) * mm, "radius": 1.25 * mm});
            skCircle(sketch, "E389.2.0.4", {"center": v(-22, 18.97) * mm, "radius": 1.25 * mm});
            skCircle(sketch, "E389.2.0.5", {"center": v(-22, 26.47) * mm, "radius": 1.25 * mm});
            skCircle(sketch, "E389.2.0.6", {"center": v(-22, 33.97) * mm, "radius": 1.25 * mm});
            skCircle(sketch, "E389.3.0.0", {"center": v(-28, -11.03) * mm, "radius": 1.25 * mm});
            skCircle(sketch, "E389.3.0.1", {"center": v(-28, -3.53) * mm, "radius": 1.25 * mm});
            skCircle(sketch, "E389.3.0.2", {"center": v(-28, 3.97) * mm, "radius": 1.25 * mm});
            skCircle(sketch, "E389.3.0.3", {"center": v(-28, 11.47) * mm, "radius": 1.25 * mm});
            skCircle(sketch, "E389.3.0.4", {"center": v(-28, 18.97) * mm, "radius": 1.25 * mm});
            skCircle(sketch, "E389.3.0.5", {"center": v(-28, 26.47) * mm, "radius": 1.25 * mm});
            skCircle(sketch, "E389.3.0.6", {"center": v(-28, 33.97) * mm, "radius": 1.25 * mm});
            skCircle(sketch, "E389.4.0.0", {"center": v(-34, -11.03) * mm, "radius": 1.25 * mm});
            skCircle(sketch, "E389.4.0.1", {"center": v(-34, -3.53) * mm, "radius": 1.25 * mm});
            skCircle(sketch, "E389.4.0.2", {"center": v(-34, 3.97) * mm, "radius": 1.25 * mm});
            skCircle(sketch, "E389.4.0.3", {"center": v(-34, 11.47) * mm, "radius": 1.25 * mm});
            skCircle(sketch, "E389.4.0.4", {"center": v(-34, 18.97) * mm, "radius": 1.25 * mm});
            skCircle(sketch, "E389.4.0.5", {"center": v(-34, 26.47) * mm, "radius": 1.25 * mm});
            skCircle(sketch, "E389.4.0.6", {"center": v(-34, 33.97) * mm, "radius": 1.25 * mm});
            skCircle(sketch, "E389.5.0.1", {"center": v(-40, -3.53) * mm, "radius": 1.25 * mm});
            skCircle(sketch, "E389.5.0.2", {"center": v(-40, 3.97) * mm, "radius": 1.25 * mm});
            skCircle(sketch, "E389.5.0.3", {"center": v(-40, 11.47) * mm, "radius": 1.25 * mm});
            skCircle(sketch, "E389.5.0.4", {"center": v(-40, 18.97) * mm, "radius": 1.25 * mm});
            skCircle(sketch, "E389.5.0.5", {"center": v(-40, 26.47) * mm, "radius": 1.25 * mm});
            skCircle(sketch, "E389.5.0.6", {"center": v(-40, 33.97) * mm, "radius": 1.25 * mm});
            skCircle(sketch, "E389.6.0.0", {"center": v(-46, -11.03) * mm, "radius": 1.25 * mm});
            skCircle(sketch, "E389.6.0.1", {"center": v(-46, -3.53) * mm, "radius": 1.25 * mm});
            skCircle(sketch, "E389.6.0.2", {"center": v(-46, 3.97) * mm, "radius": 1.25 * mm});
            skCircle(sketch, "E389.6.0.3", {"center": v(-46, 11.47) * mm, "radius": 1.25 * mm});
            skCircle(sketch, "E389.6.0.4", {"center": v(-46, 18.97) * mm, "radius": 1.25 * mm});
            skCircle(sketch, "E389.6.0.5", {"center": v(-46, 26.47) * mm, "radius": 1.25 * mm});
            skCircle(sketch, "E389.7.0.0", {"center": v(-52, -11.03) * mm, "radius": 1.25 * mm});
            skCircle(sketch, "E389.7.0.1", {"center": v(-52, -3.53) * mm, "radius": 1.25 * mm});
            skCircle(sketch, "E389.7.0.2", {"center": v(-52, 3.97) * mm, "radius": 1.25 * mm});
            skCircle(sketch, "E389.7.0.3", {"center": v(-52, 11.47) * mm, "radius": 1.25 * mm});
            skCircle(sketch, "E389.7.0.4", {"center": v(-52, 18.97) * mm, "radius": 1.25 * mm});
            skCircle(sketch, "E389.7.0.5", {"center": v(-52, 26.47) * mm, "radius": 1.25 * mm});
            skLineSegment(sketch, "E389.direction1", {"start": v(-10, -11.03) * mm, "end": v(-16, -11.03) * mm, "construction": true});
            skCircle(sketch, "E390.0.8.0", {"center": v(-58, -11.03) * mm, "radius": 1.25 * mm});
            skCircle(sketch, "E390.2.8.0", {"center": v(-58, -3.53) * mm, "radius": 1.25 * mm});
            skCircle(sketch, "E390.4.8.0", {"center": v(-58, 3.97) * mm, "radius": 1.25 * mm});
            skCircle(sketch, "E390.6.8.0", {"center": v(-58, 11.47) * mm, "radius": 1.25 * mm});
            skCircle(sketch, "E390.8.8.0", {"center": v(-58, 18.97) * mm, "radius": 1.25 * mm});
            skCircle(sketch, "E390.0.9.0", {"center": v(-64, -11.03) * mm, "radius": 1.25 * mm});
            skCircle(sketch, "E390.2.9.0", {"center": v(-64, -3.53) * mm, "radius": 1.25 * mm});
            skCircle(sketch, "E390.4.9.0", {"center": v(-64, 3.97) * mm, "radius": 1.25 * mm});
            skCircle(sketch, "E390.0.10.0", {"center": v(-70, -11.03) * mm, "radius": 1.25 * mm});
            skCircle(sketch, "E390.2.10.0", {"center": v(-70, -3.53) * mm, "radius": 1.25 * mm});
            skCircle(sketch, "E391.MirrorC", {"center": v(46, 33.97) * mm, "radius": 1.25 * mm});
            skCircle(sketch, "E392.MirrorC", {"center": v(28, 33.97) * mm, "radius": 1.25 * mm});
            skCircle(sketch, "E393.MirrorC", {"center": v(22, 33.97) * mm, "radius": 1.25 * mm});
            skCircle(sketch, "E394.MirrorC", {"center": v(16, 33.97) * mm, "radius": 1.25 * mm});
            skCircle(sketch, "E395.MirrorC", {"center": v(10, 33.97) * mm, "radius": 1.25 * mm});
            skCircle(sketch, "E396.MirrorC", {"center": v(52, 26.47) * mm, "radius": 1.25 * mm});
            skCircle(sketch, "E397.MirrorC", {"center": v(46, 26.47) * mm, "radius": 1.25 * mm});
            skCircle(sketch, "E398.MirrorC", {"center": v(40, 26.47) * mm, "radius": 1.25 * mm});
            skCircle(sketch, "E399.MirrorC", {"center": v(34, 26.47) * mm, "radius": 1.25 * mm});
            skCircle(sketch, "E400.MirrorC", {"center": v(28, 26.47) * mm, "radius": 1.25 * mm});
            skCircle(sketch, "E401.MirrorC", {"center": v(22, 26.47) * mm, "radius": 1.25 * mm});
            skCircle(sketch, "E402.MirrorC", {"center": v(16, 26.47) * mm, "radius": 1.25 * mm});
            skCircle(sketch, "E403.MirrorC", {"center": v(10, 26.47) * mm, "radius": 1.25 * mm});
            skCircle(sketch, "E404.MirrorC", {"center": v(58, 18.97) * mm, "radius": 1.25 * mm});
            skCircle(sketch, "E405.MirrorC", {"center": v(52, 18.97) * mm, "radius": 1.25 * mm});
            skCircle(sketch, "E406.MirrorC", {"center": v(46, 18.97) * mm, "radius": 1.25 * mm});
            skCircle(sketch, "E407.MirrorC", {"center": v(40, 18.97) * mm, "radius": 1.25 * mm});
            skCircle(sketch, "E408.MirrorC", {"center": v(34, 18.97) * mm, "radius": 1.25 * mm});
            skCircle(sketch, "E409.MirrorC", {"center": v(28, 18.97) * mm, "radius": 1.25 * mm});
            skCircle(sketch, "E410.MirrorC", {"center": v(22, 18.97) * mm, "radius": 1.25 * mm});
            skCircle(sketch, "E411.MirrorC", {"center": v(16, 18.97) * mm, "radius": 1.25 * mm});
            skCircle(sketch, "E412.MirrorC", {"center": v(10, 18.97) * mm, "radius": 1.25 * mm});
            skCircle(sketch, "E413.MirrorC", {"center": v(58, 11.47) * mm, "radius": 1.25 * mm});
            skCircle(sketch, "E414.MirrorC", {"center": v(52, 11.47) * mm, "radius": 1.25 * mm});
            skCircle(sketch, "E415.MirrorC", {"center": v(46, 11.47) * mm, "radius": 1.25 * mm});
            skCircle(sketch, "E416.MirrorC", {"center": v(40, 11.47) * mm, "radius": 1.25 * mm});
            skCircle(sketch, "E417.MirrorC", {"center": v(34, 11.47) * mm, "radius": 1.25 * mm});
            skCircle(sketch, "E418.MirrorC", {"center": v(28, 11.47) * mm, "radius": 1.25 * mm});
            skCircle(sketch, "E419.MirrorC", {"center": v(22, 11.47) * mm, "radius": 1.25 * mm});
            skCircle(sketch, "E420.MirrorC", {"center": v(16, 11.47) * mm, "radius": 1.25 * mm});
            skCircle(sketch, "E421.MirrorC", {"center": v(64, 3.97) * mm, "radius": 1.25 * mm});
            skCircle(sketch, "E422.MirrorC", {"center": v(58, 3.97) * mm, "radius": 1.25 * mm});
            skCircle(sketch, "E423.MirrorC", {"center": v(52, 3.97) * mm, "radius": 1.25 * mm});
            skCircle(sketch, "E424.MirrorC", {"center": v(46, 3.97) * mm, "radius": 1.25 * mm});
            skCircle(sketch, "E425.MirrorC", {"center": v(40, 3.97) * mm, "radius": 1.25 * mm});
            skCircle(sketch, "E426.MirrorC", {"center": v(34, 3.97) * mm, "radius": 1.25 * mm});
            skCircle(sketch, "E427.MirrorC", {"center": v(28, 3.97) * mm, "radius": 1.25 * mm});
            skCircle(sketch, "E428.MirrorC", {"center": v(22, 3.97) * mm, "radius": 1.25 * mm});
            skCircle(sketch, "E429.MirrorC", {"center": v(10, 3.97) * mm, "radius": 1.25 * mm});
            skCircle(sketch, "E430.MirrorC", {"center": v(70, -3.53) * mm, "radius": 1.25 * mm});
            skCircle(sketch, "E431.MirrorC", {"center": v(64, -3.53) * mm, "radius": 1.25 * mm});
            skCircle(sketch, "E432.MirrorC", {"center": v(58, -3.53) * mm, "radius": 1.25 * mm});
            skCircle(sketch, "E433.MirrorC", {"center": v(52, -3.53) * mm, "radius": 1.25 * mm});
            skCircle(sketch, "E434.MirrorC", {"center": v(40, -3.53) * mm, "radius": 1.25 * mm});
            skCircle(sketch, "E435.MirrorC", {"center": v(34, -3.53) * mm, "radius": 1.25 * mm});
            skCircle(sketch, "E436.MirrorC", {"center": v(28, -3.53) * mm, "radius": 1.25 * mm});
            skCircle(sketch, "E437.MirrorC", {"center": v(22, -3.53) * mm, "radius": 1.25 * mm});
            skCircle(sketch, "E438.MirrorC", {"center": v(16, -3.53) * mm, "radius": 1.25 * mm});
            skCircle(sketch, "E439.MirrorC", {"center": v(10, -3.53) * mm, "radius": 1.25 * mm});
            skCircle(sketch, "E440.MirrorC", {"center": v(70, -11.03) * mm, "radius": 1.25 * mm});
            skCircle(sketch, "E441.MirrorC", {"center": v(64, -11.03) * mm, "radius": 1.25 * mm});
            skCircle(sketch, "E442.MirrorC", {"center": v(58, -11.03) * mm, "radius": 1.25 * mm});
            skCircle(sketch, "E443.MirrorC", {"center": v(52, -11.03) * mm, "radius": 1.25 * mm});
            skCircle(sketch, "E444.MirrorC", {"center": v(46, -11.03) * mm, "radius": 1.25 * mm});
            skCircle(sketch, "E445.MirrorC", {"center": v(28, -11.03) * mm, "radius": 1.25 * mm});
            skCircle(sketch, "E446.MirrorC", {"center": v(22, -11.03) * mm, "radius": 1.25 * mm});
            skCircle(sketch, "E447.MirrorC", {"center": v(16, -11.03) * mm, "radius": 1.25 * mm});
            skCircle(sketch, "E448.MirrorC", {"center": v(10, -11.03) * mm, "radius": 1.25 * mm});
            skSolve(sketch);
        }
        {
            assignVariable(context, id + "F2", {"name" : "mainThickness", "anyValue" : 1.5});
        }
        {
            assignVariable(context, id + "F3", {"name" : "bossThickness", "anyValue" : 2});
        }
        {
            var Q0;
            Q0=makeQuery(id+"F1.imprint","IMPRINT",FACE,{"disambiguationData":[TD([[makeQuery(id+"F1.imprint","IMPRINT",EDGE,{"derivedFrom":sQuery(id+"F1.wireOp",EDGE,"E102")}),1.0]])]});
            var Q1;
            {var subQ5=sQuery(id+"F1.wireOp",EDGE,"E367");Q1=makeQuery(id+"F1.imprint","IMPRINT",FACE,{"disambiguationData":[TD([[makeQuery(id+"F1.imprint","IMPRINT",EDGE,{"derivedFrom":subQ5}),1.0]])]});}
            var Q2;
            {var subQ5=sQuery(id+"F1.wireOp",EDGE,"E369");Q2=makeQuery(id+"F1.imprint","IMPRINT",FACE,{"disambiguationData":[TD([[makeQuery(id+"F1.imprint","IMPRINT",EDGE,{"derivedFrom":subQ5}),1.0]])]});}
            var Q3;
            {var subQ5=sQuery(id+"F1.wireOp",EDGE,"E371");Q3=makeQuery(id+"F1.imprint","IMPRINT",FACE,{"disambiguationData":[TD([[makeQuery(id+"F1.imprint","IMPRINT",EDGE,{"derivedFrom":subQ5}),1.0]])]});}
            var Q4;
            {var subQ3=sQuery(id+"F1.wireOp",EDGE,"E373");Q4=makeQuery(id+"F1.imprint","IMPRINT",FACE,{"disambiguationData":[TD([[makeQuery(id+"F1.imprint","IMPRINT",EDGE,{"derivedFrom":subQ3}),1.0]])]});}
            extrude(context, id + "F4", {"entities" : qUnion([Q0, Q1, Q2, Q3, Q4]), "depth" : (getVariable(context, 'mainThickness')) * mm, "offsetDistance" : 25 * mm});
        }
        {
            var Q0;
            Q0=makeQuery(id+"F0.imprint","IMPRINT",FACE,{"disambiguationData":[TD([[makeQuery(id+"F0.imprint","IMPRINT",EDGE,{"derivedFrom":sQuery(id+"F0.wireOp",EDGE,"E0")}),1.0]])]});
            var Q1;
            Q1=makeQuery(id+"F0.imprint","IMPRINT",FACE,{"disambiguationData":[TD([[makeQuery(id+"F0.imprint","IMPRINT",EDGE,{"derivedFrom":sQuery(id+"F0.wireOp",EDGE,"E68")}),1.0]])]});
            var Q2;
            Q2=makeQuery(id+"F0.imprint","IMPRINT",FACE,{"disambiguationData":[TD([[makeQuery(id+"F0.imprint","IMPRINT",EDGE,{"derivedFrom":sQuery(id+"F0.wireOp",EDGE,"E51")}),1.0]])]});
            var Q3;
            Q3=makeQuery(id+"F0.imprint","IMPRINT",FACE,{"disambiguationData":[TD([[makeQuery(id+"F0.imprint","IMPRINT",EDGE,{"derivedFrom":sQuery(id+"F0.wireOp",EDGE,"E34")}),1.0]])]});
            var Q4;
            Q4=makeQuery(id+"F0.imprint","IMPRINT",FACE,{"disambiguationData":[TD([[makeQuery(id+"F0.imprint","IMPRINT",EDGE,{"derivedFrom":sQuery(id+"F0.wireOp",EDGE,"E85")}),1.0]])]});
            var Q5;
            Q5=makeQuery(id+"F0.imprint","IMPRINT",FACE,{"disambiguationData":[TD([[makeQuery(id+"F0.imprint","IMPRINT",EDGE,{"derivedFrom":sQuery(id+"F0.wireOp",EDGE,"E17")}),1.0]])]});
            extrude(context, id + "F5", {"entities" : qUnion([Q0, Q1, Q2, Q3, Q4, Q5]), "depth" : (getVariable(context, 'mainThickness') + getVariable(context, 'bossThickness')) * mm, "offsetDistance" : 25 * mm});
        }
        {
            var Q0;
            Q0=makeQuery(id+"F5.opExtrude","SWEPT_BODY",BODY,{"disambiguationData":[OSD([sQuery(id+"F0.wireOp",EDGE,"E17"),sQuery(id+"F0.wireOp",EDGE,"E18"),sQuery(id+"F0.wireOp",EDGE,"E19"),sQuery(id+"F0.wireOp",EDGE,"E20"),sQuery(id+"F0.wireOp",EDGE,"E21"),sQuery(id+"F0.wireOp",EDGE,"E22"),sQuery(id+"F0.wireOp",EDGE,"E23"),sQuery(id+"F0.wireOp",EDGE,"E24"),sQuery(id+"F0.wireOp",EDGE,"E25"),sQuery(id+"F0.wireOp",EDGE,"E26"),sQuery(id+"F0.wireOp",EDGE,"E27"),sQuery(id+"F0.wireOp",EDGE,"E28"),sQuery(id+"F0.wireOp",EDGE,"E29"),sQuery(id+"F0.wireOp",EDGE,"E30"),sQuery(id+"F0.wireOp",EDGE,"E31"),sQuery(id+"F0.wireOp",EDGE,"E32"),sQuery(id+"F0.wireOp",EDGE,"E33")])]});
            var Q1;
            Q1=makeQuery(id+"F5.opExtrude","SWEPT_BODY",BODY,{"disambiguationData":[OSD([sQuery(id+"F0.wireOp",EDGE,"E85"),sQuery(id+"F0.wireOp",EDGE,"E86"),sQuery(id+"F0.wireOp",EDGE,"E87"),sQuery(id+"F0.wireOp",EDGE,"E88"),sQuery(id+"F0.wireOp",EDGE,"E89"),sQuery(id+"F0.wireOp",EDGE,"E90"),sQuery(id+"F0.wireOp",EDGE,"E91"),sQuery(id+"F0.wireOp",EDGE,"E92"),sQuery(id+"F0.wireOp",EDGE,"E93"),sQuery(id+"F0.wireOp",EDGE,"E94"),sQuery(id+"F0.wireOp",EDGE,"E95"),sQuery(id+"F0.wireOp",EDGE,"E96"),sQuery(id+"F0.wireOp",EDGE,"E97"),sQuery(id+"F0.wireOp",EDGE,"E98"),sQuery(id+"F0.wireOp",EDGE,"E99"),sQuery(id+"F0.wireOp",EDGE,"E100"),sQuery(id+"F0.wireOp",EDGE,"E101")])]});
            var Q2;
            Q2=makeQuery(id+"F5.opExtrude","SWEPT_BODY",BODY,{"disambiguationData":[OSD([sQuery(id+"F0.wireOp",EDGE,"E34"),sQuery(id+"F0.wireOp",EDGE,"E35"),sQuery(id+"F0.wireOp",EDGE,"E36"),sQuery(id+"F0.wireOp",EDGE,"E37"),sQuery(id+"F0.wireOp",EDGE,"E38"),sQuery(id+"F0.wireOp",EDGE,"E39"),sQuery(id+"F0.wireOp",EDGE,"E40"),sQuery(id+"F0.wireOp",EDGE,"E41"),sQuery(id+"F0.wireOp",EDGE,"E42"),sQuery(id+"F0.wireOp",EDGE,"E43"),sQuery(id+"F0.wireOp",EDGE,"E44"),sQuery(id+"F0.wireOp",EDGE,"E45"),sQuery(id+"F0.wireOp",EDGE,"E46"),sQuery(id+"F0.wireOp",EDGE,"E47"),sQuery(id+"F0.wireOp",EDGE,"E48"),sQuery(id+"F0.wireOp",EDGE,"E49"),sQuery(id+"F0.wireOp",EDGE,"E50")])]});
            var Q3;
            Q3=makeQuery(id+"F5.opExtrude","SWEPT_BODY",BODY,{"disambiguationData":[OSD([sQuery(id+"F0.wireOp",EDGE,"E51"),sQuery(id+"F0.wireOp",EDGE,"E52"),sQuery(id+"F0.wireOp",EDGE,"E53"),sQuery(id+"F0.wireOp",EDGE,"E54"),sQuery(id+"F0.wireOp",EDGE,"E55"),sQuery(id+"F0.wireOp",EDGE,"E56"),sQuery(id+"F0.wireOp",EDGE,"E57"),sQuery(id+"F0.wireOp",EDGE,"E58"),sQuery(id+"F0.wireOp",EDGE,"E59"),sQuery(id+"F0.wireOp",EDGE,"E60"),sQuery(id+"F0.wireOp",EDGE,"E61"),sQuery(id+"F0.wireOp",EDGE,"E62"),sQuery(id+"F0.wireOp",EDGE,"E63"),sQuery(id+"F0.wireOp",EDGE,"E64"),sQuery(id+"F0.wireOp",EDGE,"E65"),sQuery(id+"F0.wireOp",EDGE,"E66"),sQuery(id+"F0.wireOp",EDGE,"E67")])]});
            var Q4;
            Q4=makeQuery(id+"F5.opExtrude","SWEPT_BODY",BODY,{"disambiguationData":[OSD([sQuery(id+"F0.wireOp",EDGE,"E68"),sQuery(id+"F0.wireOp",EDGE,"E69"),sQuery(id+"F0.wireOp",EDGE,"E70"),sQuery(id+"F0.wireOp",EDGE,"E71"),sQuery(id+"F0.wireOp",EDGE,"E72"),sQuery(id+"F0.wireOp",EDGE,"E73"),sQuery(id+"F0.wireOp",EDGE,"E74"),sQuery(id+"F0.wireOp",EDGE,"E75"),sQuery(id+"F0.wireOp",EDGE,"E76"),sQuery(id+"F0.wireOp",EDGE,"E77"),sQuery(id+"F0.wireOp",EDGE,"E78"),sQuery(id+"F0.wireOp",EDGE,"E79"),sQuery(id+"F0.wireOp",EDGE,"E80"),sQuery(id+"F0.wireOp",EDGE,"E81"),sQuery(id+"F0.wireOp",EDGE,"E82"),sQuery(id+"F0.wireOp",EDGE,"E83"),sQuery(id+"F0.wireOp",EDGE,"E84")])]});
            var Q5;
            Q5=makeQuery(id+"F5.opExtrude","SWEPT_BODY",BODY,{"disambiguationData":[OSD([sQuery(id+"F0.wireOp",EDGE,"E0"),sQuery(id+"F0.wireOp",EDGE,"E1"),sQuery(id+"F0.wireOp",EDGE,"E2"),sQuery(id+"F0.wireOp",EDGE,"E3"),sQuery(id+"F0.wireOp",EDGE,"E4"),sQuery(id+"F0.wireOp",EDGE,"E5"),sQuery(id+"F0.wireOp",EDGE,"E6"),sQuery(id+"F0.wireOp",EDGE,"E7"),sQuery(id+"F0.wireOp",EDGE,"E8"),sQuery(id+"F0.wireOp",EDGE,"E9"),sQuery(id+"F0.wireOp",EDGE,"E10"),sQuery(id+"F0.wireOp",EDGE,"E11"),sQuery(id+"F0.wireOp",EDGE,"E12"),sQuery(id+"F0.wireOp",EDGE,"E13"),sQuery(id+"F0.wireOp",EDGE,"E14"),sQuery(id+"F0.wireOp",EDGE,"E15"),sQuery(id+"F0.wireOp",EDGE,"E16")])]});
            transform(context, id + "F6", {"entities" : qUnion([Q0, Q1, Q2, Q3, Q4, Q5]), "transformType" : TransformType.TRANSLATION_3D, "dx" : 0 * mm, "dy" : -23.62 * mm, "dz" : 0 * mm, "makeCopy" : false});
        }
        {
            var Q0;
            Q0=qCreatedBy(makeId("Top.planeOp"),FACE);
            var sketch = newSketch(context, id + "F7", { "sketchPlane" : qUnion([Q0])});
            skLineSegment(sketch, "E449", {"start": v(-8.88, 16.84) * mm, "end": v(-8.93, 16.84) * mm});
            skLineSegment(sketch, "E450", {"start": v(-8.93, 16.84) * mm, "end": v(-8.99, 16.84) * mm});
            skLineSegment(sketch, "E451", {"start": v(-8.99, 16.84) * mm, "end": v(-9.04, 16.83) * mm});
            skLineSegment(sketch, "E452", {"start": v(-9.04, 16.83) * mm, "end": v(-9.1, 16.83) * mm});
            skLineSegment(sketch, "E453", {"start": v(-9.1, 16.83) * mm, "end": v(-9.15, 16.82) * mm});
            skLineSegment(sketch, "E454", {"start": v(-9.15, 16.82) * mm, "end": v(-9.2, 16.8) * mm});
            skLineSegment(sketch, "E455", {"start": v(-9.2, 16.8) * mm, "end": v(-9.26, 16.8) * mm});
            skLineSegment(sketch, "E456", {"start": v(-9.26, 16.8) * mm, "end": v(-9.32, 16.78) * mm});
            skLineSegment(sketch, "E457", {"start": v(-9.32, 16.78) * mm, "end": v(-9.37, 16.77) * mm});
            skLineSegment(sketch, "E458", {"start": v(-9.37, 16.77) * mm, "end": v(-9.42, 16.75) * mm});
            skLineSegment(sketch, "E459", {"start": v(-9.42, 16.75) * mm, "end": v(-9.47, 16.73) * mm});
            skLineSegment(sketch, "E460", {"start": v(-9.47, 16.73) * mm, "end": v(-9.53, 16.7) * mm});
            skLineSegment(sketch, "E461", {"start": v(-9.53, 16.7) * mm, "end": v(-9.58, 16.68) * mm});
            skLineSegment(sketch, "E462", {"start": v(-9.58, 16.68) * mm, "end": v(-9.63, 16.66) * mm});
            skLineSegment(sketch, "E463", {"start": v(-9.63, 16.66) * mm, "end": v(-9.67, 16.63) * mm});
            skLineSegment(sketch, "E464", {"start": v(-9.67, 16.63) * mm, "end": v(-9.72, 16.6) * mm});
            skLineSegment(sketch, "E465", {"start": v(-9.72, 16.6) * mm, "end": v(-9.77, 16.57) * mm});
            skLineSegment(sketch, "E466", {"start": v(-9.77, 16.57) * mm, "end": v(-9.82, 16.54) * mm});
            skLineSegment(sketch, "E467", {"start": v(-9.82, 16.54) * mm, "end": v(-9.86, 16.5) * mm});
            skLineSegment(sketch, "E468", {"start": v(-9.86, 16.5) * mm, "end": v(-9.9, 16.47) * mm});
            skLineSegment(sketch, "E469", {"start": v(-9.9, 16.47) * mm, "end": v(-9.95, 16.44) * mm});
            skLineSegment(sketch, "E470", {"start": v(-9.95, 16.44) * mm, "end": v(-9.99, 16.4) * mm});
            skLineSegment(sketch, "E471", {"start": v(-9.99, 16.4) * mm, "end": v(-10.03, 16.36) * mm});
            skLineSegment(sketch, "E472", {"start": v(-10.03, 16.36) * mm, "end": v(-10.06, 16.32) * mm});
            skLineSegment(sketch, "E473", {"start": v(-10.06, 16.32) * mm, "end": v(-10.1, 16.28) * mm});
            skLineSegment(sketch, "E474", {"start": v(-10.1, 16.28) * mm, "end": v(-10.14, 16.23) * mm});
            skLineSegment(sketch, "E475", {"start": v(-10.14, 16.23) * mm, "end": v(-10.17, 16.19) * mm});
            skLineSegment(sketch, "E476", {"start": v(-10.17, 16.19) * mm, "end": v(-10.2, 16.14) * mm});
            skLineSegment(sketch, "E477", {"start": v(-10.2, 16.14) * mm, "end": v(-10.23, 16.1) * mm});
            skLineSegment(sketch, "E478", {"start": v(-10.23, 16.1) * mm, "end": v(-10.26, 16.05) * mm});
            skLineSegment(sketch, "E479", {"start": v(-10.26, 16.05) * mm, "end": v(-10.3, 16) * mm});
            skLineSegment(sketch, "E480", {"start": v(-10.3, 16) * mm, "end": v(-10.32, 15.95) * mm});
            skLineSegment(sketch, "E481", {"start": v(-10.32, 15.95) * mm, "end": v(-10.34, 15.9) * mm});
            skLineSegment(sketch, "E482", {"start": v(-10.34, 15.9) * mm, "end": v(-10.36, 15.85) * mm});
            skLineSegment(sketch, "E483", {"start": v(-10.36, 15.85) * mm, "end": v(-10.38, 15.8) * mm});
            skLineSegment(sketch, "E484", {"start": v(-10.38, 15.8) * mm, "end": v(-10.4, 15.75) * mm});
            skLineSegment(sketch, "E485", {"start": v(-10.4, 15.75) * mm, "end": v(-10.42, 15.7) * mm});
            skLineSegment(sketch, "E486", {"start": v(-10.42, 15.7) * mm, "end": v(-10.43, 15.64) * mm});
            skLineSegment(sketch, "E487", {"start": v(-10.43, 15.64) * mm, "end": v(-10.45, 15.58) * mm});
            skLineSegment(sketch, "E488", {"start": v(-10.45, 15.58) * mm, "end": v(-10.46, 15.53) * mm});
            skLineSegment(sketch, "E489", {"start": v(-10.46, 15.53) * mm, "end": v(-10.47, 15.48) * mm});
            skLineSegment(sketch, "E490", {"start": v(-10.47, 15.48) * mm, "end": v(-10.47, 15.42) * mm});
            skLineSegment(sketch, "E491", {"start": v(-10.47, 15.42) * mm, "end": v(-10.48, 15.36) * mm});
            skLineSegment(sketch, "E492", {"start": v(-10.48, 15.36) * mm, "end": v(-10.48, 15.3) * mm});
            skLineSegment(sketch, "E493", {"start": v(-10.48, 15.3) * mm, "end": v(-10.48, 15.25) * mm});
            skLineSegment(sketch, "E494", {"start": v(-10.48, 15.25) * mm, "end": v(-10.48, 15.2) * mm});
            skLineSegment(sketch, "E495", {"start": v(-10.48, 15.2) * mm, "end": v(-10.48, 15.14) * mm});
            skLineSegment(sketch, "E496", {"start": v(-10.48, 15.14) * mm, "end": v(-10.48, 15.09) * mm});
            skLineSegment(sketch, "E497", {"start": v(-10.48, 15.09) * mm, "end": v(-10.47, 15.03) * mm});
            skLineSegment(sketch, "E498", {"start": v(-10.47, 15.03) * mm, "end": v(-10.46, 14.98) * mm});
            skLineSegment(sketch, "E499", {"start": v(-10.46, 14.98) * mm, "end": v(-10.45, 14.92) * mm});
            skLineSegment(sketch, "E500", {"start": v(-10.45, 14.92) * mm, "end": v(-10.44, 14.87) * mm});
            skLineSegment(sketch, "E501", {"start": v(-10.44, 14.87) * mm, "end": v(-10.43, 14.81) * mm});
            skLineSegment(sketch, "E502", {"start": v(-10.43, 14.81) * mm, "end": v(-10.41, 14.76) * mm});
            skLineSegment(sketch, "E503", {"start": v(-10.41, 14.76) * mm, "end": v(-10.4, 14.7) * mm});
            skLineSegment(sketch, "E504", {"start": v(-10.4, 14.7) * mm, "end": v(-10.38, 14.65) * mm});
            skLineSegment(sketch, "E505", {"start": v(-10.38, 14.65) * mm, "end": v(-10.35, 14.6) * mm});
            skLineSegment(sketch, "E506", {"start": v(-10.35, 14.6) * mm, "end": v(-10.33, 14.55) * mm});
            skLineSegment(sketch, "E507", {"start": v(-10.33, 14.55) * mm, "end": v(-10.3, 14.5) * mm});
            skLineSegment(sketch, "E508", {"start": v(-10.3, 14.5) * mm, "end": v(-10.28, 14.45) * mm});
            skLineSegment(sketch, "E509", {"start": v(-10.28, 14.45) * mm, "end": v(-10.25, 14.4) * mm});
            skLineSegment(sketch, "E510", {"start": v(-10.25, 14.4) * mm, "end": v(-10.22, 14.36) * mm});
            skLineSegment(sketch, "E511", {"start": v(-10.22, 14.36) * mm, "end": v(-10.2, 14.31) * mm});
            skLineSegment(sketch, "E512", {"start": v(-10.2, 14.31) * mm, "end": v(-10.16, 14.27) * mm});
            skLineSegment(sketch, "E513", {"start": v(-10.16, 14.27) * mm, "end": v(-10.13, 14.22) * mm});
            skLineSegment(sketch, "E514", {"start": v(-10.13, 14.22) * mm, "end": v(-10.09, 14.18) * mm});
            skLineSegment(sketch, "E515", {"start": v(-10.09, 14.18) * mm, "end": v(-10.05, 14.14) * mm});
            skLineSegment(sketch, "E516", {"start": v(-10.05, 14.14) * mm, "end": v(-10.01, 14.1) * mm});
            skLineSegment(sketch, "E517", {"start": v(-10.01, 14.1) * mm, "end": v(-9.97, 14.06) * mm});
            skLineSegment(sketch, "E518", {"start": v(-9.97, 14.06) * mm, "end": v(-9.93, 14.02) * mm});
            skLineSegment(sketch, "E519", {"start": v(-9.93, 14.02) * mm, "end": v(-9.89, 13.99) * mm});
            skLineSegment(sketch, "E520", {"start": v(-9.89, 13.99) * mm, "end": v(-9.85, 13.95) * mm});
            skLineSegment(sketch, "E521", {"start": v(-9.85, 13.95) * mm, "end": v(-9.8, 13.92) * mm});
            skLineSegment(sketch, "E522", {"start": v(-9.8, 13.92) * mm, "end": v(-9.75, 13.89) * mm});
            skLineSegment(sketch, "E523", {"start": v(-9.75, 13.89) * mm, "end": v(-9.7, 13.86) * mm});
            skLineSegment(sketch, "E524", {"start": v(-9.7, 13.86) * mm, "end": v(-9.66, 13.83) * mm});
            skLineSegment(sketch, "E525", {"start": v(-9.66, 13.83) * mm, "end": v(-9.6, 13.8) * mm});
            skLineSegment(sketch, "E526", {"start": v(-9.6, 13.8) * mm, "end": v(-9.56, 13.78) * mm});
            skLineSegment(sketch, "E527", {"start": v(-9.56, 13.78) * mm, "end": v(-9.5, 13.76) * mm});
            skLineSegment(sketch, "E528", {"start": v(-9.5, 13.76) * mm, "end": v(-9.46, 13.74) * mm});
            skLineSegment(sketch, "E529", {"start": v(-9.46, 13.74) * mm, "end": v(-9.4, 13.72) * mm});
            skLineSegment(sketch, "E530", {"start": v(-9.4, 13.72) * mm, "end": v(-9.35, 13.7) * mm});
            skLineSegment(sketch, "E531", {"start": v(-9.35, 13.7) * mm, "end": v(-9.3, 13.68) * mm});
            skLineSegment(sketch, "E532", {"start": v(-9.3, 13.68) * mm, "end": v(-9.24, 13.67) * mm});
            skLineSegment(sketch, "E533", {"start": v(-9.24, 13.67) * mm, "end": v(-9.2, 13.66) * mm});
            skLineSegment(sketch, "E534", {"start": v(-9.2, 13.66) * mm, "end": v(-9.14, 13.65) * mm});
            skLineSegment(sketch, "E535", {"start": v(-9.14, 13.65) * mm, "end": v(-9.08, 13.64) * mm});
            skLineSegment(sketch, "E536", {"start": v(-9.08, 13.64) * mm, "end": v(-9.02, 13.63) * mm});
            skLineSegment(sketch, "E537", {"start": v(-9.02, 13.63) * mm, "end": v(-8.97, 13.63) * mm});
            skLineSegment(sketch, "E538", {"start": v(-8.97, 13.63) * mm, "end": v(-8.91, 13.63) * mm});
            skLineSegment(sketch, "E539", {"start": v(-8.91, 13.63) * mm, "end": v(-8.86, 13.63) * mm});
            skLineSegment(sketch, "E540", {"start": v(-8.86, 13.63) * mm, "end": v(-8.8, 13.63) * mm});
            skLineSegment(sketch, "E541", {"start": v(-8.8, 13.63) * mm, "end": v(-8.75, 13.63) * mm});
            skLineSegment(sketch, "E542", {"start": v(-8.75, 13.63) * mm, "end": v(-8.7, 13.64) * mm});
            skLineSegment(sketch, "E543", {"start": v(-8.7, 13.64) * mm, "end": v(-8.64, 13.64) * mm});
            skLineSegment(sketch, "E544", {"start": v(-8.64, 13.64) * mm, "end": v(-8.58, 13.65) * mm});
            skLineSegment(sketch, "E545", {"start": v(-8.58, 13.65) * mm, "end": v(-8.53, 13.67) * mm});
            skLineSegment(sketch, "E546", {"start": v(-8.53, 13.67) * mm, "end": v(-8.47, 13.68) * mm});
            skLineSegment(sketch, "E547", {"start": v(-8.47, 13.68) * mm, "end": v(-8.42, 13.7) * mm});
            skLineSegment(sketch, "E548", {"start": v(-8.42, 13.7) * mm, "end": v(-8.37, 13.7) * mm});
            skLineSegment(sketch, "E549", {"start": v(-8.37, 13.7) * mm, "end": v(-8.31, 13.73) * mm});
            skLineSegment(sketch, "E550", {"start": v(-8.31, 13.73) * mm, "end": v(-8.26, 13.75) * mm});
            skLineSegment(sketch, "E551", {"start": v(-8.26, 13.75) * mm, "end": v(-8.2, 13.77) * mm});
            skLineSegment(sketch, "E552", {"start": v(-8.2, 13.77) * mm, "end": v(-8.16, 13.8) * mm});
            skLineSegment(sketch, "E553", {"start": v(-8.16, 13.8) * mm, "end": v(-8.11, 13.82) * mm});
            skLineSegment(sketch, "E554", {"start": v(-8.11, 13.82) * mm, "end": v(-8.06, 13.85) * mm});
            skLineSegment(sketch, "E555", {"start": v(-8.06, 13.85) * mm, "end": v(-8.01, 13.88) * mm});
            skLineSegment(sketch, "E556", {"start": v(-8.01, 13.88) * mm, "end": v(-7.97, 13.9) * mm});
            skLineSegment(sketch, "E557", {"start": v(-7.97, 13.9) * mm, "end": v(-7.92, 13.94) * mm});
            skLineSegment(sketch, "E558", {"start": v(-7.92, 13.94) * mm, "end": v(-7.88, 13.97) * mm});
            skLineSegment(sketch, "E559", {"start": v(-7.88, 13.97) * mm, "end": v(-7.83, 14) * mm});
            skLineSegment(sketch, "E560", {"start": v(-7.83, 14) * mm, "end": v(-7.8, 14.05) * mm});
            skLineSegment(sketch, "E561", {"start": v(-7.8, 14.05) * mm, "end": v(-7.75, 14.08) * mm});
            skLineSegment(sketch, "E562", {"start": v(-7.75, 14.08) * mm, "end": v(-7.71, 14.12) * mm});
            skLineSegment(sketch, "E563", {"start": v(-7.71, 14.12) * mm, "end": v(-7.68, 14.17) * mm});
            skLineSegment(sketch, "E564", {"start": v(-7.68, 14.17) * mm, "end": v(-7.64, 14.2) * mm});
            skLineSegment(sketch, "E565", {"start": v(-7.64, 14.2) * mm, "end": v(-7.6, 14.25) * mm});
            skLineSegment(sketch, "E566", {"start": v(-7.6, 14.25) * mm, "end": v(-7.57, 14.3) * mm});
            skLineSegment(sketch, "E567", {"start": v(-7.57, 14.3) * mm, "end": v(-7.54, 14.34) * mm});
            skLineSegment(sketch, "E568", {"start": v(-7.54, 14.34) * mm, "end": v(-7.5, 14.39) * mm});
            skLineSegment(sketch, "E569", {"start": v(-7.5, 14.39) * mm, "end": v(-7.48, 14.44) * mm});
            skLineSegment(sketch, "E570", {"start": v(-7.48, 14.44) * mm, "end": v(-7.45, 14.48) * mm});
            skLineSegment(sketch, "E571", {"start": v(-7.45, 14.48) * mm, "end": v(-7.43, 14.53) * mm});
            skLineSegment(sketch, "E572", {"start": v(-7.43, 14.53) * mm, "end": v(-7.4, 14.59) * mm});
            skLineSegment(sketch, "E573", {"start": v(-7.4, 14.59) * mm, "end": v(-7.38, 14.64) * mm});
            skLineSegment(sketch, "E574", {"start": v(-7.38, 14.64) * mm, "end": v(-7.36, 14.69) * mm});
            skLineSegment(sketch, "E575", {"start": v(-7.36, 14.69) * mm, "end": v(-7.35, 14.74) * mm});
            skLineSegment(sketch, "E576", {"start": v(-7.35, 14.74) * mm, "end": v(-7.33, 14.8) * mm});
            skLineSegment(sketch, "E577", {"start": v(-7.33, 14.8) * mm, "end": v(-7.32, 14.85) * mm});
            skLineSegment(sketch, "E578", {"start": v(-7.32, 14.85) * mm, "end": v(-7.3, 14.9) * mm});
            skLineSegment(sketch, "E579", {"start": v(-7.3, 14.9) * mm, "end": v(-7.3, 14.96) * mm});
            skLineSegment(sketch, "E580", {"start": v(-7.3, 14.96) * mm, "end": v(-7.28, 15.01) * mm});
            skLineSegment(sketch, "E581", {"start": v(-7.28, 15.01) * mm, "end": v(-7.28, 15.07) * mm});
            skLineSegment(sketch, "E582", {"start": v(-7.28, 15.07) * mm, "end": v(-7.27, 15.12) * mm});
            skLineSegment(sketch, "E583", {"start": v(-7.27, 15.12) * mm, "end": v(-7.27, 15.18) * mm});
            skLineSegment(sketch, "E584", {"start": v(-7.27, 15.18) * mm, "end": v(-7.27, 15.23) * mm});
            skLineSegment(sketch, "E585", {"start": v(-7.27, 15.23) * mm, "end": v(-7.27, 15.3) * mm});
            skLineSegment(sketch, "E586", {"start": v(-7.27, 15.3) * mm, "end": v(-7.27, 15.35) * mm});
            skLineSegment(sketch, "E587", {"start": v(-7.27, 15.35) * mm, "end": v(-7.28, 15.4) * mm});
            skLineSegment(sketch, "E588", {"start": v(-7.28, 15.4) * mm, "end": v(-7.28, 15.46) * mm});
            skLineSegment(sketch, "E589", {"start": v(-7.28, 15.46) * mm, "end": v(-7.3, 15.51) * mm});
            skLineSegment(sketch, "E590", {"start": v(-7.3, 15.51) * mm, "end": v(-7.3, 15.57) * mm});
            skLineSegment(sketch, "E591", {"start": v(-7.3, 15.57) * mm, "end": v(-7.32, 15.62) * mm});
            skLineSegment(sketch, "E592", {"start": v(-7.32, 15.62) * mm, "end": v(-7.33, 15.68) * mm});
            skLineSegment(sketch, "E593", {"start": v(-7.33, 15.68) * mm, "end": v(-7.35, 15.73) * mm});
            skLineSegment(sketch, "E594", {"start": v(-7.35, 15.73) * mm, "end": v(-7.37, 15.78) * mm});
            skLineSegment(sketch, "E595", {"start": v(-7.37, 15.78) * mm, "end": v(-7.39, 15.84) * mm});
            skLineSegment(sketch, "E596", {"start": v(-7.39, 15.84) * mm, "end": v(-7.4, 15.89) * mm});
            skLineSegment(sketch, "E597", {"start": v(-7.4, 15.89) * mm, "end": v(-7.43, 15.94) * mm});
            skLineSegment(sketch, "E598", {"start": v(-7.43, 15.94) * mm, "end": v(-7.46, 15.99) * mm});
            skLineSegment(sketch, "E599", {"start": v(-7.46, 15.99) * mm, "end": v(-7.48, 16.04) * mm});
            skLineSegment(sketch, "E600", {"start": v(-7.48, 16.04) * mm, "end": v(-7.51, 16.09) * mm});
            skLineSegment(sketch, "E601", {"start": v(-7.51, 16.09) * mm, "end": v(-7.54, 16.13) * mm});
            skLineSegment(sketch, "E602", {"start": v(-7.54, 16.13) * mm, "end": v(-7.58, 16.18) * mm});
            skLineSegment(sketch, "E603", {"start": v(-7.58, 16.18) * mm, "end": v(-7.6, 16.22) * mm});
            skLineSegment(sketch, "E604", {"start": v(-7.6, 16.22) * mm, "end": v(-7.64, 16.27) * mm});
            skLineSegment(sketch, "E605", {"start": v(-7.64, 16.27) * mm, "end": v(-7.68, 16.31) * mm});
            skLineSegment(sketch, "E606", {"start": v(-7.68, 16.31) * mm, "end": v(-7.72, 16.35) * mm});
            skLineSegment(sketch, "E607", {"start": v(-7.72, 16.35) * mm, "end": v(-7.76, 16.4) * mm});
            skLineSegment(sketch, "E608", {"start": v(-7.76, 16.4) * mm, "end": v(-7.8, 16.43) * mm});
            skLineSegment(sketch, "E609", {"start": v(-7.8, 16.43) * mm, "end": v(-7.84, 16.47) * mm});
            skLineSegment(sketch, "E610", {"start": v(-7.84, 16.47) * mm, "end": v(-7.89, 16.5) * mm});
            skLineSegment(sketch, "E611", {"start": v(-7.89, 16.5) * mm, "end": v(-7.93, 16.54) * mm});
            skLineSegment(sketch, "E612", {"start": v(-7.93, 16.54) * mm, "end": v(-7.98, 16.57) * mm});
            skLineSegment(sketch, "E613", {"start": v(-7.98, 16.57) * mm, "end": v(-8.02, 16.6) * mm});
            skLineSegment(sketch, "E614", {"start": v(-8.02, 16.6) * mm, "end": v(-8.07, 16.63) * mm});
            skLineSegment(sketch, "E615", {"start": v(-8.07, 16.63) * mm, "end": v(-8.12, 16.65) * mm});
            skLineSegment(sketch, "E616", {"start": v(-8.12, 16.65) * mm, "end": v(-8.17, 16.68) * mm});
            skLineSegment(sketch, "E617", {"start": v(-8.17, 16.68) * mm, "end": v(-8.22, 16.7) * mm});
            skLineSegment(sketch, "E618", {"start": v(-8.22, 16.7) * mm, "end": v(-8.27, 16.73) * mm});
            skLineSegment(sketch, "E619", {"start": v(-8.27, 16.73) * mm, "end": v(-8.33, 16.75) * mm});
            skLineSegment(sketch, "E620", {"start": v(-8.33, 16.75) * mm, "end": v(-8.38, 16.76) * mm});
            skLineSegment(sketch, "E621", {"start": v(-8.38, 16.76) * mm, "end": v(-8.43, 16.78) * mm});
            skLineSegment(sketch, "E622", {"start": v(-8.43, 16.78) * mm, "end": v(-8.49, 16.8) * mm});
            skLineSegment(sketch, "E623", {"start": v(-8.49, 16.8) * mm, "end": v(-8.54, 16.8) * mm});
            skLineSegment(sketch, "E624", {"start": v(-8.54, 16.8) * mm, "end": v(-8.6, 16.82) * mm});
            skLineSegment(sketch, "E625", {"start": v(-8.6, 16.82) * mm, "end": v(-8.65, 16.83) * mm});
            skLineSegment(sketch, "E626", {"start": v(-8.65, 16.83) * mm, "end": v(-8.7, 16.83) * mm});
            skLineSegment(sketch, "E627", {"start": v(-8.7, 16.83) * mm, "end": v(-8.76, 16.84) * mm});
            skLineSegment(sketch, "E628", {"start": v(-8.76, 16.84) * mm, "end": v(-8.82, 16.84) * mm});
            skLineSegment(sketch, "E629", {"start": v(-8.82, 16.84) * mm, "end": v(-8.88, 16.84) * mm});
            skLineSegment(sketch, "E630", {"start": v(-24.11, 40.96) * mm, "end": v(-24.17, 40.96) * mm});
            skLineSegment(sketch, "E631", {"start": v(-24.17, 40.96) * mm, "end": v(-24.22, 40.96) * mm});
            skLineSegment(sketch, "E632", {"start": v(-24.22, 40.96) * mm, "end": v(-24.28, 40.96) * mm});
            skLineSegment(sketch, "E633", {"start": v(-24.28, 40.96) * mm, "end": v(-24.33, 40.95) * mm});
            skLineSegment(sketch, "E634", {"start": v(-24.33, 40.95) * mm, "end": v(-24.39, 40.94) * mm});
            skLineSegment(sketch, "E635", {"start": v(-24.39, 40.94) * mm, "end": v(-24.44, 40.93) * mm});
            skLineSegment(sketch, "E636", {"start": v(-24.44, 40.93) * mm, "end": v(-24.5, 40.92) * mm});
            skLineSegment(sketch, "E637", {"start": v(-24.5, 40.92) * mm, "end": v(-24.55, 40.9) * mm});
            skLineSegment(sketch, "E638", {"start": v(-24.55, 40.9) * mm, "end": v(-24.6, 40.89) * mm});
            skLineSegment(sketch, "E639", {"start": v(-24.6, 40.89) * mm, "end": v(-24.66, 40.87) * mm});
            skLineSegment(sketch, "E640", {"start": v(-24.66, 40.87) * mm, "end": v(-24.7, 40.85) * mm});
            skLineSegment(sketch, "E641", {"start": v(-24.7, 40.85) * mm, "end": v(-24.76, 40.83) * mm});
            skLineSegment(sketch, "E642", {"start": v(-24.76, 40.83) * mm, "end": v(-24.81, 40.8) * mm});
            skLineSegment(sketch, "E643", {"start": v(-24.81, 40.8) * mm, "end": v(-24.86, 40.78) * mm});
            skLineSegment(sketch, "E644", {"start": v(-24.86, 40.78) * mm, "end": v(-24.9, 40.75) * mm});
            skLineSegment(sketch, "E645", {"start": v(-24.9, 40.75) * mm, "end": v(-24.96, 40.72) * mm});
            skLineSegment(sketch, "E646", {"start": v(-24.96, 40.72) * mm, "end": v(-25, 40.7) * mm});
            skLineSegment(sketch, "E647", {"start": v(-25, 40.7) * mm, "end": v(-25.05, 40.66) * mm});
            skLineSegment(sketch, "E648", {"start": v(-25.05, 40.66) * mm, "end": v(-25.1, 40.63) * mm});
            skLineSegment(sketch, "E649", {"start": v(-25.1, 40.63) * mm, "end": v(-25.14, 40.6) * mm});
            skLineSegment(sketch, "E650", {"start": v(-25.14, 40.6) * mm, "end": v(-25.18, 40.56) * mm});
            skLineSegment(sketch, "E651", {"start": v(-25.18, 40.56) * mm, "end": v(-25.22, 40.52) * mm});
            skLineSegment(sketch, "E652", {"start": v(-25.22, 40.52) * mm, "end": v(-25.26, 40.48) * mm});
            skLineSegment(sketch, "E653", {"start": v(-25.26, 40.48) * mm, "end": v(-25.3, 40.44) * mm});
            skLineSegment(sketch, "E654", {"start": v(-25.3, 40.44) * mm, "end": v(-25.34, 40.4) * mm});
            skLineSegment(sketch, "E655", {"start": v(-25.34, 40.4) * mm, "end": v(-25.37, 40.35) * mm});
            skLineSegment(sketch, "E656", {"start": v(-25.37, 40.35) * mm, "end": v(-25.4, 40.31) * mm});
            skLineSegment(sketch, "E657", {"start": v(-25.4, 40.31) * mm, "end": v(-25.44, 40.26) * mm});
            skLineSegment(sketch, "E658", {"start": v(-25.44, 40.26) * mm, "end": v(-25.47, 40.22) * mm});
            skLineSegment(sketch, "E659", {"start": v(-25.47, 40.22) * mm, "end": v(-25.5, 40.17) * mm});
            skLineSegment(sketch, "E660", {"start": v(-25.5, 40.17) * mm, "end": v(-25.52, 40.12) * mm});
            skLineSegment(sketch, "E661", {"start": v(-25.52, 40.12) * mm, "end": v(-25.55, 40.07) * mm});
            skLineSegment(sketch, "E662", {"start": v(-25.55, 40.07) * mm, "end": v(-25.57, 40.02) * mm});
            skLineSegment(sketch, "E663", {"start": v(-25.57, 40.02) * mm, "end": v(-25.6, 39.97) * mm});
            skLineSegment(sketch, "E664", {"start": v(-25.6, 39.97) * mm, "end": v(-25.62, 39.92) * mm});
            skLineSegment(sketch, "E665", {"start": v(-25.62, 39.92) * mm, "end": v(-25.64, 39.87) * mm});
            skLineSegment(sketch, "E666", {"start": v(-25.64, 39.87) * mm, "end": v(-25.65, 39.81) * mm});
            skLineSegment(sketch, "E667", {"start": v(-25.65, 39.81) * mm, "end": v(-25.67, 39.76) * mm});
            skLineSegment(sketch, "E668", {"start": v(-25.67, 39.76) * mm, "end": v(-25.68, 39.7) * mm});
            skLineSegment(sketch, "E669", {"start": v(-25.68, 39.7) * mm, "end": v(-25.7, 39.65) * mm});
            skLineSegment(sketch, "E670", {"start": v(-25.7, 39.65) * mm, "end": v(-25.7, 39.6) * mm});
            skLineSegment(sketch, "E671", {"start": v(-25.7, 39.6) * mm, "end": v(-25.7, 39.54) * mm});
            skLineSegment(sketch, "E672", {"start": v(-25.7, 39.54) * mm, "end": v(-25.71, 39.49) * mm});
            skLineSegment(sketch, "E673", {"start": v(-25.71, 39.49) * mm, "end": v(-25.72, 39.43) * mm});
            skLineSegment(sketch, "E674", {"start": v(-25.72, 39.43) * mm, "end": v(-25.72, 39.37) * mm});
            skLineSegment(sketch, "E675", {"start": v(-25.72, 39.37) * mm, "end": v(-25.72, 39.32) * mm});
            skLineSegment(sketch, "E676", {"start": v(-25.72, 39.32) * mm, "end": v(-25.72, 39.26) * mm});
            skLineSegment(sketch, "E677", {"start": v(-25.72, 39.26) * mm, "end": v(-25.71, 39.2) * mm});
            skLineSegment(sketch, "E678", {"start": v(-25.71, 39.2) * mm, "end": v(-25.7, 39.15) * mm});
            skLineSegment(sketch, "E679", {"start": v(-25.7, 39.15) * mm, "end": v(-25.7, 39.1) * mm});
            skLineSegment(sketch, "E680", {"start": v(-25.7, 39.1) * mm, "end": v(-25.69, 39.04) * mm});
            skLineSegment(sketch, "E681", {"start": v(-25.69, 39.04) * mm, "end": v(-25.68, 38.99) * mm});
            skLineSegment(sketch, "E682", {"start": v(-25.68, 38.99) * mm, "end": v(-25.66, 38.93) * mm});
            skLineSegment(sketch, "E683", {"start": v(-25.66, 38.93) * mm, "end": v(-25.65, 38.88) * mm});
            skLineSegment(sketch, "E684", {"start": v(-25.65, 38.88) * mm, "end": v(-25.63, 38.83) * mm});
            skLineSegment(sketch, "E685", {"start": v(-25.63, 38.83) * mm, "end": v(-25.61, 38.78) * mm});
            skLineSegment(sketch, "E686", {"start": v(-25.61, 38.78) * mm, "end": v(-25.59, 38.72) * mm});
            skLineSegment(sketch, "E687", {"start": v(-25.59, 38.72) * mm, "end": v(-25.57, 38.67) * mm});
            skLineSegment(sketch, "E688", {"start": v(-25.57, 38.67) * mm, "end": v(-25.54, 38.62) * mm});
            skLineSegment(sketch, "E689", {"start": v(-25.54, 38.62) * mm, "end": v(-25.52, 38.57) * mm});
            skLineSegment(sketch, "E690", {"start": v(-25.52, 38.57) * mm, "end": v(-25.49, 38.53) * mm});
            skLineSegment(sketch, "E691", {"start": v(-25.49, 38.53) * mm, "end": v(-25.46, 38.48) * mm});
            skLineSegment(sketch, "E692", {"start": v(-25.46, 38.48) * mm, "end": v(-25.43, 38.43) * mm});
            skLineSegment(sketch, "E693", {"start": v(-25.43, 38.43) * mm, "end": v(-25.4, 38.39) * mm});
            skLineSegment(sketch, "E694", {"start": v(-25.4, 38.39) * mm, "end": v(-25.36, 38.34) * mm});
            skLineSegment(sketch, "E695", {"start": v(-25.36, 38.34) * mm, "end": v(-25.32, 38.3) * mm});
            skLineSegment(sketch, "E696", {"start": v(-25.32, 38.3) * mm, "end": v(-25.29, 38.26) * mm});
            skLineSegment(sketch, "E697", {"start": v(-25.29, 38.26) * mm, "end": v(-25.25, 38.22) * mm});
            skLineSegment(sketch, "E698", {"start": v(-25.25, 38.22) * mm, "end": v(-25.2, 38.18) * mm});
            skLineSegment(sketch, "E699", {"start": v(-25.2, 38.18) * mm, "end": v(-25.17, 38.14) * mm});
            skLineSegment(sketch, "E700", {"start": v(-25.17, 38.14) * mm, "end": v(-25.12, 38.1) * mm});
            skLineSegment(sketch, "E701", {"start": v(-25.12, 38.1) * mm, "end": v(-25.08, 38.07) * mm});
            skLineSegment(sketch, "E702", {"start": v(-25.08, 38.07) * mm, "end": v(-25.03, 38.04) * mm});
            skLineSegment(sketch, "E703", {"start": v(-25.03, 38.04) * mm, "end": v(-24.99, 38) * mm});
            skLineSegment(sketch, "E704", {"start": v(-24.99, 38) * mm, "end": v(-24.94, 37.98) * mm});
            skLineSegment(sketch, "E705", {"start": v(-24.94, 37.98) * mm, "end": v(-24.9, 37.95) * mm});
            skLineSegment(sketch, "E706", {"start": v(-24.9, 37.95) * mm, "end": v(-24.84, 37.92) * mm});
            skLineSegment(sketch, "E707", {"start": v(-24.84, 37.92) * mm, "end": v(-24.8, 37.9) * mm});
            skLineSegment(sketch, "E708", {"start": v(-24.8, 37.9) * mm, "end": v(-24.74, 37.88) * mm});
            skLineSegment(sketch, "E709", {"start": v(-24.74, 37.88) * mm, "end": v(-24.7, 37.86) * mm});
            skLineSegment(sketch, "E710", {"start": v(-24.7, 37.86) * mm, "end": v(-24.64, 37.84) * mm});
            skLineSegment(sketch, "E711", {"start": v(-24.64, 37.84) * mm, "end": v(-24.59, 37.82) * mm});
            skLineSegment(sketch, "E712", {"start": v(-24.59, 37.82) * mm, "end": v(-24.53, 37.8) * mm});
            skLineSegment(sketch, "E713", {"start": v(-24.53, 37.8) * mm, "end": v(-24.48, 37.8) * mm});
            skLineSegment(sketch, "E714", {"start": v(-24.48, 37.8) * mm, "end": v(-24.42, 37.78) * mm});
            skLineSegment(sketch, "E715", {"start": v(-24.42, 37.78) * mm, "end": v(-24.37, 37.77) * mm});
            skLineSegment(sketch, "E716", {"start": v(-24.37, 37.77) * mm, "end": v(-24.31, 37.76) * mm});
            skLineSegment(sketch, "E717", {"start": v(-24.31, 37.76) * mm, "end": v(-24.26, 37.75) * mm});
            skLineSegment(sketch, "E718", {"start": v(-24.26, 37.75) * mm, "end": v(-24.2, 37.75) * mm});
            skLineSegment(sketch, "E719", {"start": v(-24.2, 37.75) * mm, "end": v(-24.15, 37.75) * mm});
            skLineSegment(sketch, "E720", {"start": v(-24.15, 37.75) * mm, "end": v(-24.1, 37.75) * mm});
            skLineSegment(sketch, "E721", {"start": v(-24.1, 37.75) * mm, "end": v(-24.04, 37.75) * mm});
            skLineSegment(sketch, "E722", {"start": v(-24.04, 37.75) * mm, "end": v(-23.98, 37.75) * mm});
            skLineSegment(sketch, "E723", {"start": v(-23.98, 37.75) * mm, "end": v(-23.93, 37.76) * mm});
            skLineSegment(sketch, "E724", {"start": v(-23.93, 37.76) * mm, "end": v(-23.87, 37.77) * mm});
            skLineSegment(sketch, "E725", {"start": v(-23.87, 37.77) * mm, "end": v(-23.82, 37.78) * mm});
            skLineSegment(sketch, "E726", {"start": v(-23.82, 37.78) * mm, "end": v(-23.76, 37.79) * mm});
            skLineSegment(sketch, "E727", {"start": v(-23.76, 37.79) * mm, "end": v(-23.7, 37.8) * mm});
            skLineSegment(sketch, "E728", {"start": v(-23.7, 37.8) * mm, "end": v(-23.65, 37.81) * mm});
            skLineSegment(sketch, "E729", {"start": v(-23.65, 37.81) * mm, "end": v(-23.6, 37.83) * mm});
            skLineSegment(sketch, "E730", {"start": v(-23.6, 37.83) * mm, "end": v(-23.55, 37.85) * mm});
            skLineSegment(sketch, "E731", {"start": v(-23.55, 37.85) * mm, "end": v(-23.5, 37.87) * mm});
            skLineSegment(sketch, "E732", {"start": v(-23.5, 37.87) * mm, "end": v(-23.44, 37.9) * mm});
            skLineSegment(sketch, "E733", {"start": v(-23.44, 37.9) * mm, "end": v(-23.4, 37.92) * mm});
            skLineSegment(sketch, "E734", {"start": v(-23.4, 37.92) * mm, "end": v(-23.34, 37.94) * mm});
            skLineSegment(sketch, "E735", {"start": v(-23.34, 37.94) * mm, "end": v(-23.3, 37.97) * mm});
            skLineSegment(sketch, "E736", {"start": v(-23.3, 37.97) * mm, "end": v(-23.25, 38) * mm});
            skLineSegment(sketch, "E737", {"start": v(-23.25, 38) * mm, "end": v(-23.2, 38.03) * mm});
            skLineSegment(sketch, "E738", {"start": v(-23.2, 38.03) * mm, "end": v(-23.16, 38.06) * mm});
            skLineSegment(sketch, "E739", {"start": v(-23.16, 38.06) * mm, "end": v(-23.11, 38.1) * mm});
            skLineSegment(sketch, "E740", {"start": v(-23.11, 38.1) * mm, "end": v(-23.07, 38.13) * mm});
            skLineSegment(sketch, "E741", {"start": v(-23.07, 38.13) * mm, "end": v(-23.03, 38.17) * mm});
            skLineSegment(sketch, "E742", {"start": v(-23.03, 38.17) * mm, "end": v(-22.99, 38.2) * mm});
            skLineSegment(sketch, "E743", {"start": v(-22.99, 38.2) * mm, "end": v(-22.95, 38.25) * mm});
            skLineSegment(sketch, "E744", {"start": v(-22.95, 38.25) * mm, "end": v(-22.91, 38.29) * mm});
            skLineSegment(sketch, "E745", {"start": v(-22.91, 38.29) * mm, "end": v(-22.87, 38.33) * mm});
            skLineSegment(sketch, "E746", {"start": v(-22.87, 38.33) * mm, "end": v(-22.84, 38.37) * mm});
            skLineSegment(sketch, "E747", {"start": v(-22.84, 38.37) * mm, "end": v(-22.8, 38.42) * mm});
            skLineSegment(sketch, "E748", {"start": v(-22.8, 38.42) * mm, "end": v(-22.77, 38.46) * mm});
            skLineSegment(sketch, "E749", {"start": v(-22.77, 38.46) * mm, "end": v(-22.74, 38.5) * mm});
            skLineSegment(sketch, "E750", {"start": v(-22.74, 38.5) * mm, "end": v(-22.72, 38.56) * mm});
            skLineSegment(sketch, "E751", {"start": v(-22.72, 38.56) * mm, "end": v(-22.69, 38.6) * mm});
            skLineSegment(sketch, "E752", {"start": v(-22.69, 38.6) * mm, "end": v(-22.66, 38.66) * mm});
            skLineSegment(sketch, "E753", {"start": v(-22.66, 38.66) * mm, "end": v(-22.64, 38.7) * mm});
            skLineSegment(sketch, "E754", {"start": v(-22.64, 38.7) * mm, "end": v(-22.62, 38.76) * mm});
            skLineSegment(sketch, "E755", {"start": v(-22.62, 38.76) * mm, "end": v(-22.6, 38.8) * mm});
            skLineSegment(sketch, "E756", {"start": v(-22.6, 38.8) * mm, "end": v(-22.58, 38.86) * mm});
            skLineSegment(sketch, "E757", {"start": v(-22.58, 38.86) * mm, "end": v(-22.56, 38.92) * mm});
            skLineSegment(sketch, "E758", {"start": v(-22.56, 38.92) * mm, "end": v(-22.55, 38.97) * mm});
            skLineSegment(sketch, "E759", {"start": v(-22.55, 38.97) * mm, "end": v(-22.54, 39.02) * mm});
            skLineSegment(sketch, "E760", {"start": v(-22.54, 39.02) * mm, "end": v(-22.53, 39.08) * mm});
            skLineSegment(sketch, "E761", {"start": v(-22.53, 39.08) * mm, "end": v(-22.52, 39.13) * mm});
            skLineSegment(sketch, "E762", {"start": v(-22.52, 39.13) * mm, "end": v(-22.51, 39.19) * mm});
            skLineSegment(sketch, "E763", {"start": v(-22.51, 39.19) * mm, "end": v(-22.5, 39.24) * mm});
            skLineSegment(sketch, "E764", {"start": v(-22.5, 39.24) * mm, "end": v(-22.5, 39.3) * mm});
            skLineSegment(sketch, "E765", {"start": v(-22.5, 39.3) * mm, "end": v(-22.5, 39.36) * mm});
            skLineSegment(sketch, "E766", {"start": v(-22.5, 39.36) * mm, "end": v(-22.5, 39.41) * mm});
            skLineSegment(sketch, "E767", {"start": v(-22.5, 39.41) * mm, "end": v(-22.5, 39.47) * mm});
            skLineSegment(sketch, "E768", {"start": v(-22.5, 39.47) * mm, "end": v(-22.51, 39.52) * mm});
            skLineSegment(sketch, "E769", {"start": v(-22.51, 39.52) * mm, "end": v(-22.52, 39.58) * mm});
            skLineSegment(sketch, "E770", {"start": v(-22.52, 39.58) * mm, "end": v(-22.53, 39.64) * mm});
            skLineSegment(sketch, "E771", {"start": v(-22.53, 39.64) * mm, "end": v(-22.54, 39.7) * mm});
            skLineSegment(sketch, "E772", {"start": v(-22.54, 39.7) * mm, "end": v(-22.55, 39.75) * mm});
            skLineSegment(sketch, "E773", {"start": v(-22.55, 39.75) * mm, "end": v(-22.57, 39.8) * mm});
            skLineSegment(sketch, "E774", {"start": v(-22.57, 39.8) * mm, "end": v(-22.58, 39.85) * mm});
            skLineSegment(sketch, "E775", {"start": v(-22.58, 39.85) * mm, "end": v(-22.6, 39.9) * mm});
            skLineSegment(sketch, "E776", {"start": v(-22.6, 39.9) * mm, "end": v(-22.62, 39.96) * mm});
            skLineSegment(sketch, "E777", {"start": v(-22.62, 39.96) * mm, "end": v(-22.64, 40.01) * mm});
            skLineSegment(sketch, "E778", {"start": v(-22.64, 40.01) * mm, "end": v(-22.67, 40.06) * mm});
            skLineSegment(sketch, "E779", {"start": v(-22.67, 40.06) * mm, "end": v(-22.7, 40.11) * mm});
            skLineSegment(sketch, "E780", {"start": v(-22.7, 40.11) * mm, "end": v(-22.72, 40.16) * mm});
            skLineSegment(sketch, "E781", {"start": v(-22.72, 40.16) * mm, "end": v(-22.75, 40.2) * mm});
            skLineSegment(sketch, "E782", {"start": v(-22.75, 40.2) * mm, "end": v(-22.78, 40.26) * mm});
            skLineSegment(sketch, "E783", {"start": v(-22.78, 40.26) * mm, "end": v(-22.8, 40.3) * mm});
            skLineSegment(sketch, "E784", {"start": v(-22.8, 40.3) * mm, "end": v(-22.84, 40.35) * mm});
            skLineSegment(sketch, "E785", {"start": v(-22.84, 40.35) * mm, "end": v(-22.88, 40.39) * mm});
            skLineSegment(sketch, "E786", {"start": v(-22.88, 40.39) * mm, "end": v(-22.92, 40.43) * mm});
            skLineSegment(sketch, "E787", {"start": v(-22.92, 40.43) * mm, "end": v(-22.95, 40.47) * mm});
            skLineSegment(sketch, "E788", {"start": v(-22.95, 40.47) * mm, "end": v(-23, 40.51) * mm});
            skLineSegment(sketch, "E789", {"start": v(-23, 40.51) * mm, "end": v(-23.03, 40.55) * mm});
            skLineSegment(sketch, "E790", {"start": v(-23.03, 40.55) * mm, "end": v(-23.08, 40.59) * mm});
            skLineSegment(sketch, "E791", {"start": v(-23.08, 40.59) * mm, "end": v(-23.12, 40.62) * mm});
            skLineSegment(sketch, "E792", {"start": v(-23.12, 40.62) * mm, "end": v(-23.17, 40.66) * mm});
            skLineSegment(sketch, "E793", {"start": v(-23.17, 40.66) * mm, "end": v(-23.21, 40.69) * mm});
            skLineSegment(sketch, "E794", {"start": v(-23.21, 40.69) * mm, "end": v(-23.26, 40.72) * mm});
            skLineSegment(sketch, "E795", {"start": v(-23.26, 40.72) * mm, "end": v(-23.3, 40.75) * mm});
            skLineSegment(sketch, "E796", {"start": v(-23.3, 40.75) * mm, "end": v(-23.36, 40.78) * mm});
            skLineSegment(sketch, "E797", {"start": v(-23.36, 40.78) * mm, "end": v(-23.4, 40.8) * mm});
            skLineSegment(sketch, "E798", {"start": v(-23.4, 40.8) * mm, "end": v(-23.46, 40.83) * mm});
            skLineSegment(sketch, "E799", {"start": v(-23.46, 40.83) * mm, "end": v(-23.5, 40.85) * mm});
            skLineSegment(sketch, "E800", {"start": v(-23.5, 40.85) * mm, "end": v(-23.56, 40.87) * mm});
            skLineSegment(sketch, "E801", {"start": v(-23.56, 40.87) * mm, "end": v(-23.61, 40.89) * mm});
            skLineSegment(sketch, "E802", {"start": v(-23.61, 40.89) * mm, "end": v(-23.67, 40.9) * mm});
            skLineSegment(sketch, "E803", {"start": v(-23.67, 40.9) * mm, "end": v(-23.72, 40.92) * mm});
            skLineSegment(sketch, "E804", {"start": v(-23.72, 40.92) * mm, "end": v(-23.78, 40.93) * mm});
            skLineSegment(sketch, "E805", {"start": v(-23.78, 40.93) * mm, "end": v(-23.83, 40.94) * mm});
            skLineSegment(sketch, "E806", {"start": v(-23.83, 40.94) * mm, "end": v(-23.89, 40.95) * mm});
            skLineSegment(sketch, "E807", {"start": v(-23.89, 40.95) * mm, "end": v(-23.94, 40.96) * mm});
            skLineSegment(sketch, "E808", {"start": v(-23.94, 40.96) * mm, "end": v(-24, 40.96) * mm});
            skLineSegment(sketch, "E809", {"start": v(-24, 40.96) * mm, "end": v(-24.05, 40.96) * mm});
            skLineSegment(sketch, "E810", {"start": v(-24.05, 40.96) * mm, "end": v(-24.11, 40.96) * mm});
            skLineSegment(sketch, "E811", {"start": v(24.11, 47.3) * mm, "end": v(24.06, 47.29) * mm});
            skLineSegment(sketch, "E812", {"start": v(24.06, 47.29) * mm, "end": v(24, 47.29) * mm});
            skLineSegment(sketch, "E813", {"start": v(24, 47.29) * mm, "end": v(23.94, 47.28) * mm});
            skLineSegment(sketch, "E814", {"start": v(23.94, 47.28) * mm, "end": v(23.89, 47.28) * mm});
            skLineSegment(sketch, "E815", {"start": v(23.89, 47.28) * mm, "end": v(23.83, 47.27) * mm});
            skLineSegment(sketch, "E816", {"start": v(23.83, 47.27) * mm, "end": v(23.78, 47.26) * mm});
            skLineSegment(sketch, "E817", {"start": v(23.78, 47.26) * mm, "end": v(23.72, 47.24) * mm});
            skLineSegment(sketch, "E818", {"start": v(23.72, 47.24) * mm, "end": v(23.67, 47.23) * mm});
            skLineSegment(sketch, "E819", {"start": v(23.67, 47.23) * mm, "end": v(23.62, 47.21) * mm});
            skLineSegment(sketch, "E820", {"start": v(23.62, 47.21) * mm, "end": v(23.56, 47.2) * mm});
            skLineSegment(sketch, "E821", {"start": v(23.56, 47.2) * mm, "end": v(23.51, 47.18) * mm});
            skLineSegment(sketch, "E822", {"start": v(23.51, 47.18) * mm, "end": v(23.46, 47.15) * mm});
            skLineSegment(sketch, "E823", {"start": v(23.46, 47.15) * mm, "end": v(23.41, 47.13) * mm});
            skLineSegment(sketch, "E824", {"start": v(23.41, 47.13) * mm, "end": v(23.36, 47.1) * mm});
            skLineSegment(sketch, "E825", {"start": v(23.36, 47.1) * mm, "end": v(23.31, 47.08) * mm});
            skLineSegment(sketch, "E826", {"start": v(23.31, 47.08) * mm, "end": v(23.26, 47.05) * mm});
            skLineSegment(sketch, "E827", {"start": v(23.26, 47.05) * mm, "end": v(23.22, 47.02) * mm});
            skLineSegment(sketch, "E828", {"start": v(23.22, 47.02) * mm, "end": v(23.17, 46.99) * mm});
            skLineSegment(sketch, "E829", {"start": v(23.17, 46.99) * mm, "end": v(23.13, 46.95) * mm});
            skLineSegment(sketch, "E830", {"start": v(23.13, 46.95) * mm, "end": v(23.08, 46.92) * mm});
            skLineSegment(sketch, "E831", {"start": v(23.08, 46.92) * mm, "end": v(23.04, 46.88) * mm});
            skLineSegment(sketch, "E832", {"start": v(23.04, 46.88) * mm, "end": v(23, 46.85) * mm});
            skLineSegment(sketch, "E833", {"start": v(23, 46.85) * mm, "end": v(22.96, 46.8) * mm});
            skLineSegment(sketch, "E834", {"start": v(22.96, 46.8) * mm, "end": v(22.92, 46.77) * mm});
            skLineSegment(sketch, "E835", {"start": v(22.92, 46.77) * mm, "end": v(22.89, 46.72) * mm});
            skLineSegment(sketch, "E836", {"start": v(22.89, 46.72) * mm, "end": v(22.85, 46.68) * mm});
            skLineSegment(sketch, "E837", {"start": v(22.85, 46.68) * mm, "end": v(22.82, 46.64) * mm});
            skLineSegment(sketch, "E838", {"start": v(22.82, 46.64) * mm, "end": v(22.78, 46.6) * mm});
            skLineSegment(sketch, "E839", {"start": v(22.78, 46.6) * mm, "end": v(22.75, 46.54) * mm});
            skLineSegment(sketch, "E840", {"start": v(22.75, 46.54) * mm, "end": v(22.72, 46.5) * mm});
            skLineSegment(sketch, "E841", {"start": v(22.72, 46.5) * mm, "end": v(22.7, 46.45) * mm});
            skLineSegment(sketch, "E842", {"start": v(22.7, 46.45) * mm, "end": v(22.67, 46.4) * mm});
            skLineSegment(sketch, "E843", {"start": v(22.67, 46.4) * mm, "end": v(22.65, 46.35) * mm});
            skLineSegment(sketch, "E844", {"start": v(22.65, 46.35) * mm, "end": v(22.63, 46.3) * mm});
            skLineSegment(sketch, "E845", {"start": v(22.63, 46.3) * mm, "end": v(22.6, 46.25) * mm});
            skLineSegment(sketch, "E846", {"start": v(22.6, 46.25) * mm, "end": v(22.59, 46.2) * mm});
            skLineSegment(sketch, "E847", {"start": v(22.59, 46.2) * mm, "end": v(22.57, 46.14) * mm});
            skLineSegment(sketch, "E848", {"start": v(22.57, 46.14) * mm, "end": v(22.55, 46.09) * mm});
            skLineSegment(sketch, "E849", {"start": v(22.55, 46.09) * mm, "end": v(22.54, 46.03) * mm});
            skLineSegment(sketch, "E850", {"start": v(22.54, 46.03) * mm, "end": v(22.53, 45.98) * mm});
            skLineSegment(sketch, "E851", {"start": v(22.53, 45.98) * mm, "end": v(22.52, 45.92) * mm});
            skLineSegment(sketch, "E852", {"start": v(22.52, 45.92) * mm, "end": v(22.51, 45.87) * mm});
            skLineSegment(sketch, "E853", {"start": v(22.51, 45.87) * mm, "end": v(22.5, 45.81) * mm});
            skLineSegment(sketch, "E854", {"start": v(22.5, 45.81) * mm, "end": v(22.5, 45.76) * mm});
            skLineSegment(sketch, "E855", {"start": v(22.5, 45.76) * mm, "end": v(22.5, 45.7) * mm});
            skLineSegment(sketch, "E856", {"start": v(22.5, 45.7) * mm, "end": v(22.5, 45.65) * mm});
            skLineSegment(sketch, "E857", {"start": v(22.5, 45.65) * mm, "end": v(22.5, 45.59) * mm});
            skLineSegment(sketch, "E858", {"start": v(22.5, 45.59) * mm, "end": v(22.5, 45.53) * mm});
            skLineSegment(sketch, "E859", {"start": v(22.5, 45.53) * mm, "end": v(22.52, 45.48) * mm});
            skLineSegment(sketch, "E860", {"start": v(22.52, 45.48) * mm, "end": v(22.52, 45.42) * mm});
            skLineSegment(sketch, "E861", {"start": v(22.52, 45.42) * mm, "end": v(22.53, 45.37) * mm});
            skLineSegment(sketch, "E862", {"start": v(22.53, 45.37) * mm, "end": v(22.55, 45.31) * mm});
            skLineSegment(sketch, "E863", {"start": v(22.55, 45.31) * mm, "end": v(22.56, 45.26) * mm});
            skLineSegment(sketch, "E864", {"start": v(22.56, 45.26) * mm, "end": v(22.57, 45.2) * mm});
            skLineSegment(sketch, "E865", {"start": v(22.57, 45.2) * mm, "end": v(22.6, 45.15) * mm});
            skLineSegment(sketch, "E866", {"start": v(22.6, 45.15) * mm, "end": v(22.61, 45.1) * mm});
            skLineSegment(sketch, "E867", {"start": v(22.61, 45.1) * mm, "end": v(22.63, 45.05) * mm});
            skLineSegment(sketch, "E868", {"start": v(22.63, 45.05) * mm, "end": v(22.66, 45) * mm});
            skLineSegment(sketch, "E869", {"start": v(22.66, 45) * mm, "end": v(22.68, 44.95) * mm});
            skLineSegment(sketch, "E870", {"start": v(22.68, 44.95) * mm, "end": v(22.7, 44.9) * mm});
            skLineSegment(sketch, "E871", {"start": v(22.7, 44.9) * mm, "end": v(22.73, 44.85) * mm});
            skLineSegment(sketch, "E872", {"start": v(22.73, 44.85) * mm, "end": v(22.76, 44.8) * mm});
            skLineSegment(sketch, "E873", {"start": v(22.76, 44.8) * mm, "end": v(22.8, 44.76) * mm});
            skLineSegment(sketch, "E874", {"start": v(22.8, 44.76) * mm, "end": v(22.83, 44.71) * mm});
            skLineSegment(sketch, "E875", {"start": v(22.83, 44.71) * mm, "end": v(22.86, 44.67) * mm});
            skLineSegment(sketch, "E876", {"start": v(22.86, 44.67) * mm, "end": v(22.9, 44.63) * mm});
            skLineSegment(sketch, "E877", {"start": v(22.9, 44.63) * mm, "end": v(22.94, 44.59) * mm});
            skLineSegment(sketch, "E878", {"start": v(22.94, 44.59) * mm, "end": v(22.97, 44.55) * mm});
            skLineSegment(sketch, "E879", {"start": v(22.97, 44.55) * mm, "end": v(23.01, 44.5) * mm});
            skLineSegment(sketch, "E880", {"start": v(23.01, 44.5) * mm, "end": v(23.06, 44.47) * mm});
            skLineSegment(sketch, "E881", {"start": v(23.06, 44.47) * mm, "end": v(23.1, 44.43) * mm});
            skLineSegment(sketch, "E882", {"start": v(23.1, 44.43) * mm, "end": v(23.14, 44.4) * mm});
            skLineSegment(sketch, "E883", {"start": v(23.14, 44.4) * mm, "end": v(23.19, 44.37) * mm});
            skLineSegment(sketch, "E884", {"start": v(23.19, 44.37) * mm, "end": v(23.23, 44.34) * mm});
            skLineSegment(sketch, "E885", {"start": v(23.23, 44.34) * mm, "end": v(23.28, 44.3) * mm});
            skLineSegment(sketch, "E886", {"start": v(23.28, 44.3) * mm, "end": v(23.33, 44.28) * mm});
            skLineSegment(sketch, "E887", {"start": v(23.33, 44.28) * mm, "end": v(23.38, 44.25) * mm});
            skLineSegment(sketch, "E888", {"start": v(23.38, 44.25) * mm, "end": v(23.43, 44.23) * mm});
            skLineSegment(sketch, "E889", {"start": v(23.43, 44.23) * mm, "end": v(23.48, 44.2) * mm});
            skLineSegment(sketch, "E890", {"start": v(23.48, 44.2) * mm, "end": v(23.53, 44.18) * mm});
            skLineSegment(sketch, "E891", {"start": v(23.53, 44.18) * mm, "end": v(23.58, 44.16) * mm});
            skLineSegment(sketch, "E892", {"start": v(23.58, 44.16) * mm, "end": v(23.64, 44.15) * mm});
            skLineSegment(sketch, "E893", {"start": v(23.64, 44.15) * mm, "end": v(23.69, 44.13) * mm});
            skLineSegment(sketch, "E894", {"start": v(23.69, 44.13) * mm, "end": v(23.74, 44.12) * mm});
            skLineSegment(sketch, "E895", {"start": v(23.74, 44.12) * mm, "end": v(23.8, 44.1) * mm});
            skLineSegment(sketch, "E896", {"start": v(23.8, 44.1) * mm, "end": v(23.85, 44.1) * mm});
            skLineSegment(sketch, "E897", {"start": v(23.85, 44.1) * mm, "end": v(23.9, 44.09) * mm});
            skLineSegment(sketch, "E898", {"start": v(23.9, 44.09) * mm, "end": v(23.96, 44.08) * mm});
            skLineSegment(sketch, "E899", {"start": v(23.96, 44.08) * mm, "end": v(24.02, 44.08) * mm});
            skLineSegment(sketch, "E900", {"start": v(24.02, 44.08) * mm, "end": v(24.07, 44.08) * mm});
            skLineSegment(sketch, "E901", {"start": v(24.07, 44.08) * mm, "end": v(24.13, 44.07) * mm});
            skLineSegment(sketch, "E902", {"start": v(24.13, 44.07) * mm, "end": v(24.19, 44.08) * mm});
            skLineSegment(sketch, "E903", {"start": v(24.19, 44.08) * mm, "end": v(24.24, 44.08) * mm});
            skLineSegment(sketch, "E904", {"start": v(24.24, 44.08) * mm, "end": v(24.3, 44.09) * mm});
            skLineSegment(sketch, "E905", {"start": v(24.3, 44.09) * mm, "end": v(24.35, 44.1) * mm});
            skLineSegment(sketch, "E906", {"start": v(24.35, 44.1) * mm, "end": v(24.4, 44.1) * mm});
            skLineSegment(sketch, "E907", {"start": v(24.4, 44.1) * mm, "end": v(24.46, 44.11) * mm});
            skLineSegment(sketch, "E908", {"start": v(24.46, 44.11) * mm, "end": v(24.52, 44.13) * mm});
            skLineSegment(sketch, "E909", {"start": v(24.52, 44.13) * mm, "end": v(24.57, 44.14) * mm});
            skLineSegment(sketch, "E910", {"start": v(24.57, 44.14) * mm, "end": v(24.62, 44.16) * mm});
            skLineSegment(sketch, "E911", {"start": v(24.62, 44.16) * mm, "end": v(24.67, 44.18) * mm});
            skLineSegment(sketch, "E912", {"start": v(24.67, 44.18) * mm, "end": v(24.73, 44.2) * mm});
            skLineSegment(sketch, "E913", {"start": v(24.73, 44.2) * mm, "end": v(24.78, 44.22) * mm});
            skLineSegment(sketch, "E914", {"start": v(24.78, 44.22) * mm, "end": v(24.83, 44.24) * mm});
            skLineSegment(sketch, "E915", {"start": v(24.83, 44.24) * mm, "end": v(24.88, 44.27) * mm});
            skLineSegment(sketch, "E916", {"start": v(24.88, 44.27) * mm, "end": v(24.93, 44.3) * mm});
            skLineSegment(sketch, "E917", {"start": v(24.93, 44.3) * mm, "end": v(24.97, 44.33) * mm});
            skLineSegment(sketch, "E918", {"start": v(24.97, 44.33) * mm, "end": v(25.02, 44.36) * mm});
            skLineSegment(sketch, "E919", {"start": v(25.02, 44.36) * mm, "end": v(25.07, 44.39) * mm});
            skLineSegment(sketch, "E920", {"start": v(25.07, 44.39) * mm, "end": v(25.1, 44.42) * mm});
            skLineSegment(sketch, "E921", {"start": v(25.1, 44.42) * mm, "end": v(25.15, 44.46) * mm});
            skLineSegment(sketch, "E922", {"start": v(25.15, 44.46) * mm, "end": v(25.2, 44.5) * mm});
            skLineSegment(sketch, "E923", {"start": v(25.2, 44.5) * mm, "end": v(25.23, 44.53) * mm});
            skLineSegment(sketch, "E924", {"start": v(25.23, 44.53) * mm, "end": v(25.27, 44.57) * mm});
            skLineSegment(sketch, "E925", {"start": v(25.27, 44.57) * mm, "end": v(25.31, 44.61) * mm});
            skLineSegment(sketch, "E926", {"start": v(25.31, 44.61) * mm, "end": v(25.35, 44.66) * mm});
            skLineSegment(sketch, "E927", {"start": v(25.35, 44.66) * mm, "end": v(25.38, 44.7) * mm});
            skLineSegment(sketch, "E928", {"start": v(25.38, 44.7) * mm, "end": v(25.42, 44.74) * mm});
            skLineSegment(sketch, "E929", {"start": v(25.42, 44.74) * mm, "end": v(25.45, 44.79) * mm});
            skLineSegment(sketch, "E930", {"start": v(25.45, 44.79) * mm, "end": v(25.48, 44.84) * mm});
            skLineSegment(sketch, "E931", {"start": v(25.48, 44.84) * mm, "end": v(25.5, 44.88) * mm});
            skLineSegment(sketch, "E932", {"start": v(25.5, 44.88) * mm, "end": v(25.53, 44.93) * mm});
            skLineSegment(sketch, "E933", {"start": v(25.53, 44.93) * mm, "end": v(25.56, 44.98) * mm});
            skLineSegment(sketch, "E934", {"start": v(25.56, 44.98) * mm, "end": v(25.58, 45.03) * mm});
            skLineSegment(sketch, "E935", {"start": v(25.58, 45.03) * mm, "end": v(25.6, 45.08) * mm});
            skLineSegment(sketch, "E936", {"start": v(25.6, 45.08) * mm, "end": v(25.62, 45.14) * mm});
            skLineSegment(sketch, "E937", {"start": v(25.62, 45.14) * mm, "end": v(25.64, 45.19) * mm});
            skLineSegment(sketch, "E938", {"start": v(25.64, 45.19) * mm, "end": v(25.66, 45.24) * mm});
            skLineSegment(sketch, "E939", {"start": v(25.66, 45.24) * mm, "end": v(25.67, 45.3) * mm});
            skLineSegment(sketch, "E940", {"start": v(25.67, 45.3) * mm, "end": v(25.68, 45.35) * mm});
            skLineSegment(sketch, "E941", {"start": v(25.68, 45.35) * mm, "end": v(25.7, 45.4) * mm});
            skLineSegment(sketch, "E942", {"start": v(25.7, 45.4) * mm, "end": v(25.7, 45.46) * mm});
            skLineSegment(sketch, "E943", {"start": v(25.7, 45.46) * mm, "end": v(25.71, 45.52) * mm});
            skLineSegment(sketch, "E944", {"start": v(25.71, 45.52) * mm, "end": v(25.72, 45.57) * mm});
            skLineSegment(sketch, "E945", {"start": v(25.72, 45.57) * mm, "end": v(25.72, 45.63) * mm});
            skLineSegment(sketch, "E946", {"start": v(25.72, 45.63) * mm, "end": v(25.72, 45.68) * mm});
            skLineSegment(sketch, "E947", {"start": v(25.72, 45.68) * mm, "end": v(25.72, 45.74) * mm});
            skLineSegment(sketch, "E948", {"start": v(25.72, 45.74) * mm, "end": v(25.72, 45.8) * mm});
            skLineSegment(sketch, "E949", {"start": v(25.72, 45.8) * mm, "end": v(25.71, 45.85) * mm});
            skLineSegment(sketch, "E950", {"start": v(25.71, 45.85) * mm, "end": v(25.7, 45.9) * mm});
            skLineSegment(sketch, "E951", {"start": v(25.7, 45.9) * mm, "end": v(25.7, 45.96) * mm});
            skLineSegment(sketch, "E952", {"start": v(25.7, 45.96) * mm, "end": v(25.68, 46.02) * mm});
            skLineSegment(sketch, "E953", {"start": v(25.68, 46.02) * mm, "end": v(25.67, 46.07) * mm});
            skLineSegment(sketch, "E954", {"start": v(25.67, 46.07) * mm, "end": v(25.66, 46.13) * mm});
            skLineSegment(sketch, "E955", {"start": v(25.66, 46.13) * mm, "end": v(25.64, 46.18) * mm});
            skLineSegment(sketch, "E956", {"start": v(25.64, 46.18) * mm, "end": v(25.62, 46.23) * mm});
            skLineSegment(sketch, "E957", {"start": v(25.62, 46.23) * mm, "end": v(25.6, 46.29) * mm});
            skLineSegment(sketch, "E958", {"start": v(25.6, 46.29) * mm, "end": v(25.58, 46.34) * mm});
            skLineSegment(sketch, "E959", {"start": v(25.58, 46.34) * mm, "end": v(25.56, 46.39) * mm});
            skLineSegment(sketch, "E960", {"start": v(25.56, 46.39) * mm, "end": v(25.53, 46.44) * mm});
            skLineSegment(sketch, "E961", {"start": v(25.53, 46.44) * mm, "end": v(25.5, 46.49) * mm});
            skLineSegment(sketch, "E962", {"start": v(25.5, 46.49) * mm, "end": v(25.47, 46.53) * mm});
            skLineSegment(sketch, "E963", {"start": v(25.47, 46.53) * mm, "end": v(25.44, 46.58) * mm});
            skLineSegment(sketch, "E964", {"start": v(25.44, 46.58) * mm, "end": v(25.41, 46.63) * mm});
            skLineSegment(sketch, "E965", {"start": v(25.41, 46.63) * mm, "end": v(25.38, 46.67) * mm});
            skLineSegment(sketch, "E966", {"start": v(25.38, 46.67) * mm, "end": v(25.34, 46.72) * mm});
            skLineSegment(sketch, "E967", {"start": v(25.34, 46.72) * mm, "end": v(25.3, 46.76) * mm});
            skLineSegment(sketch, "E968", {"start": v(25.3, 46.76) * mm, "end": v(25.27, 46.8) * mm});
            skLineSegment(sketch, "E969", {"start": v(25.27, 46.8) * mm, "end": v(25.23, 46.84) * mm});
            skLineSegment(sketch, "E970", {"start": v(25.23, 46.84) * mm, "end": v(25.19, 46.88) * mm});
            skLineSegment(sketch, "E971", {"start": v(25.19, 46.88) * mm, "end": v(25.14, 46.91) * mm});
            skLineSegment(sketch, "E972", {"start": v(25.14, 46.91) * mm, "end": v(25.1, 46.95) * mm});
            skLineSegment(sketch, "E973", {"start": v(25.1, 46.95) * mm, "end": v(25.06, 46.98) * mm});
            skLineSegment(sketch, "E974", {"start": v(25.06, 46.98) * mm, "end": v(25.01, 47.02) * mm});
            skLineSegment(sketch, "E975", {"start": v(25.01, 47.02) * mm, "end": v(24.96, 47.05) * mm});
            skLineSegment(sketch, "E976", {"start": v(24.96, 47.05) * mm, "end": v(24.91, 47.08) * mm});
            skLineSegment(sketch, "E977", {"start": v(24.91, 47.08) * mm, "end": v(24.87, 47.1) * mm});
            skLineSegment(sketch, "E978", {"start": v(24.87, 47.1) * mm, "end": v(24.82, 47.13) * mm});
            skLineSegment(sketch, "E979", {"start": v(24.82, 47.13) * mm, "end": v(24.76, 47.15) * mm});
            skLineSegment(sketch, "E980", {"start": v(24.76, 47.15) * mm, "end": v(24.71, 47.17) * mm});
            skLineSegment(sketch, "E981", {"start": v(24.71, 47.17) * mm, "end": v(24.66, 47.2) * mm});
            skLineSegment(sketch, "E982", {"start": v(24.66, 47.2) * mm, "end": v(24.6, 47.21) * mm});
            skLineSegment(sketch, "E983", {"start": v(24.6, 47.21) * mm, "end": v(24.55, 47.23) * mm});
            skLineSegment(sketch, "E984", {"start": v(24.55, 47.23) * mm, "end": v(24.5, 47.24) * mm});
            skLineSegment(sketch, "E985", {"start": v(24.5, 47.24) * mm, "end": v(24.45, 47.26) * mm});
            skLineSegment(sketch, "E986", {"start": v(24.45, 47.26) * mm, "end": v(24.4, 47.27) * mm});
            skLineSegment(sketch, "E987", {"start": v(24.4, 47.27) * mm, "end": v(24.33, 47.28) * mm});
            skLineSegment(sketch, "E988", {"start": v(24.33, 47.28) * mm, "end": v(24.28, 47.28) * mm});
            skLineSegment(sketch, "E989", {"start": v(24.28, 47.28) * mm, "end": v(24.22, 47.29) * mm});
            skLineSegment(sketch, "E990", {"start": v(24.22, 47.29) * mm, "end": v(24.17, 47.29) * mm});
            skLineSegment(sketch, "E991", {"start": v(24.17, 47.29) * mm, "end": v(24.11, 47.3) * mm});
            skLineSegment(sketch, "E992", {"start": v(24.11, -35.19) * mm, "end": v(24.06, -35.19) * mm});
            skLineSegment(sketch, "E993", {"start": v(24.06, -35.19) * mm, "end": v(24, -35.2) * mm});
            skLineSegment(sketch, "E994", {"start": v(24, -35.2) * mm, "end": v(23.94, -35.2) * mm});
            skLineSegment(sketch, "E995", {"start": v(23.94, -35.2) * mm, "end": v(23.89, -35.2) * mm});
            skLineSegment(sketch, "E996", {"start": v(23.89, -35.2) * mm, "end": v(23.83, -35.21) * mm});
            skLineSegment(sketch, "E997", {"start": v(23.83, -35.21) * mm, "end": v(23.78, -35.22) * mm});
            skLineSegment(sketch, "E998", {"start": v(23.78, -35.22) * mm, "end": v(23.72, -35.23) * mm});
            skLineSegment(sketch, "E999", {"start": v(23.72, -35.23) * mm, "end": v(23.67, -35.25) * mm});
            skLineSegment(sketch, "E1000", {"start": v(23.67, -35.25) * mm, "end": v(23.62, -35.27) * mm});
            skLineSegment(sketch, "E1001", {"start": v(23.62, -35.27) * mm, "end": v(23.56, -35.28) * mm});
            skLineSegment(sketch, "E1002", {"start": v(23.56, -35.28) * mm, "end": v(23.51, -35.3) * mm});
            skLineSegment(sketch, "E1003", {"start": v(23.51, -35.3) * mm, "end": v(23.46, -35.32) * mm});
            skLineSegment(sketch, "E1004", {"start": v(23.46, -35.32) * mm, "end": v(23.41, -35.35) * mm});
            skLineSegment(sketch, "E1005", {"start": v(23.41, -35.35) * mm, "end": v(23.36, -35.37) * mm});
            skLineSegment(sketch, "E1006", {"start": v(23.36, -35.37) * mm, "end": v(23.31, -35.4) * mm});
            skLineSegment(sketch, "E1007", {"start": v(23.31, -35.4) * mm, "end": v(23.26, -35.43) * mm});
            skLineSegment(sketch, "E1008", {"start": v(23.26, -35.43) * mm, "end": v(23.22, -35.46) * mm});
            skLineSegment(sketch, "E1009", {"start": v(23.22, -35.46) * mm, "end": v(23.17, -35.5) * mm});
            skLineSegment(sketch, "E1010", {"start": v(23.17, -35.5) * mm, "end": v(23.13, -35.52) * mm});
            skLineSegment(sketch, "E1011", {"start": v(23.13, -35.52) * mm, "end": v(23.08, -35.56) * mm});
            skLineSegment(sketch, "E1012", {"start": v(23.08, -35.56) * mm, "end": v(23.04, -35.6) * mm});
            skLineSegment(sketch, "E1013", {"start": v(23.04, -35.6) * mm, "end": v(23, -35.63) * mm});
            skLineSegment(sketch, "E1014", {"start": v(23, -35.63) * mm, "end": v(22.96, -35.67) * mm});
            skLineSegment(sketch, "E1015", {"start": v(22.96, -35.67) * mm, "end": v(22.92, -35.71) * mm});
            skLineSegment(sketch, "E1016", {"start": v(22.92, -35.71) * mm, "end": v(22.89, -35.75) * mm});
            skLineSegment(sketch, "E1017", {"start": v(22.89, -35.75) * mm, "end": v(22.85, -35.8) * mm});
            skLineSegment(sketch, "E1018", {"start": v(22.85, -35.8) * mm, "end": v(22.82, -35.84) * mm});
            skLineSegment(sketch, "E1019", {"start": v(22.82, -35.84) * mm, "end": v(22.78, -35.89) * mm});
            skLineSegment(sketch, "E1020", {"start": v(22.78, -35.89) * mm, "end": v(22.75, -35.93) * mm});
            skLineSegment(sketch, "E1021", {"start": v(22.75, -35.93) * mm, "end": v(22.72, -35.98) * mm});
            skLineSegment(sketch, "E1022", {"start": v(22.72, -35.98) * mm, "end": v(22.7, -36.03) * mm});
            skLineSegment(sketch, "E1023", {"start": v(22.7, -36.03) * mm, "end": v(22.67, -36.08) * mm});
            skLineSegment(sketch, "E1024", {"start": v(22.67, -36.08) * mm, "end": v(22.65, -36.13) * mm});
            skLineSegment(sketch, "E1025", {"start": v(22.65, -36.13) * mm, "end": v(22.63, -36.18) * mm});
            skLineSegment(sketch, "E1026", {"start": v(22.63, -36.18) * mm, "end": v(22.6, -36.23) * mm});
            skLineSegment(sketch, "E1027", {"start": v(22.6, -36.23) * mm, "end": v(22.59, -36.28) * mm});
            skLineSegment(sketch, "E1028", {"start": v(22.59, -36.28) * mm, "end": v(22.57, -36.34) * mm});
            skLineSegment(sketch, "E1029", {"start": v(22.57, -36.34) * mm, "end": v(22.55, -36.4) * mm});
            skLineSegment(sketch, "E1030", {"start": v(22.55, -36.4) * mm, "end": v(22.54, -36.45) * mm});
            skLineSegment(sketch, "E1031", {"start": v(22.54, -36.45) * mm, "end": v(22.53, -36.5) * mm});
            skLineSegment(sketch, "E1032", {"start": v(22.53, -36.5) * mm, "end": v(22.52, -36.56) * mm});
            skLineSegment(sketch, "E1033", {"start": v(22.52, -36.56) * mm, "end": v(22.51, -36.61) * mm});
            skLineSegment(sketch, "E1034", {"start": v(22.51, -36.61) * mm, "end": v(22.5, -36.67) * mm});
            skLineSegment(sketch, "E1035", {"start": v(22.5, -36.67) * mm, "end": v(22.5, -36.72) * mm});
            skLineSegment(sketch, "E1036", {"start": v(22.5, -36.72) * mm, "end": v(22.5, -36.78) * mm});
            skLineSegment(sketch, "E1037", {"start": v(22.5, -36.78) * mm, "end": v(22.5, -36.83) * mm});
            skLineSegment(sketch, "E1038", {"start": v(22.5, -36.83) * mm, "end": v(22.5, -36.89) * mm});
            skLineSegment(sketch, "E1039", {"start": v(22.5, -36.89) * mm, "end": v(22.5, -36.94) * mm});
            skLineSegment(sketch, "E1040", {"start": v(22.5, -36.94) * mm, "end": v(22.52, -37) * mm});
            skLineSegment(sketch, "E1041", {"start": v(22.52, -37) * mm, "end": v(22.52, -37.05) * mm});
            skLineSegment(sketch, "E1042", {"start": v(22.52, -37.05) * mm, "end": v(22.53, -37.1) * mm});
            skLineSegment(sketch, "E1043", {"start": v(22.53, -37.1) * mm, "end": v(22.55, -37.16) * mm});
            skLineSegment(sketch, "E1044", {"start": v(22.55, -37.16) * mm, "end": v(22.56, -37.22) * mm});
            skLineSegment(sketch, "E1045", {"start": v(22.56, -37.22) * mm, "end": v(22.57, -37.27) * mm});
            skLineSegment(sketch, "E1046", {"start": v(22.57, -37.27) * mm, "end": v(22.6, -37.32) * mm});
            skLineSegment(sketch, "E1047", {"start": v(22.6, -37.32) * mm, "end": v(22.61, -37.38) * mm});
            skLineSegment(sketch, "E1048", {"start": v(22.61, -37.38) * mm, "end": v(22.63, -37.43) * mm});
            skLineSegment(sketch, "E1049", {"start": v(22.63, -37.43) * mm, "end": v(22.66, -37.48) * mm});
            skLineSegment(sketch, "E1050", {"start": v(22.66, -37.48) * mm, "end": v(22.68, -37.53) * mm});
            skLineSegment(sketch, "E1051", {"start": v(22.68, -37.53) * mm, "end": v(22.7, -37.58) * mm});
            skLineSegment(sketch, "E1052", {"start": v(22.7, -37.58) * mm, "end": v(22.73, -37.63) * mm});
            skLineSegment(sketch, "E1053", {"start": v(22.73, -37.63) * mm, "end": v(22.76, -37.67) * mm});
            skLineSegment(sketch, "E1054", {"start": v(22.76, -37.67) * mm, "end": v(22.8, -37.72) * mm});
            skLineSegment(sketch, "E1055", {"start": v(22.8, -37.72) * mm, "end": v(22.83, -37.76) * mm});
            skLineSegment(sketch, "E1056", {"start": v(22.83, -37.76) * mm, "end": v(22.86, -37.8) * mm});
            skLineSegment(sketch, "E1057", {"start": v(22.86, -37.8) * mm, "end": v(22.9, -37.85) * mm});
            skLineSegment(sketch, "E1058", {"start": v(22.9, -37.85) * mm, "end": v(22.94, -37.9) * mm});
            skLineSegment(sketch, "E1059", {"start": v(22.94, -37.9) * mm, "end": v(22.97, -37.93) * mm});
            skLineSegment(sketch, "E1060", {"start": v(22.97, -37.93) * mm, "end": v(23.01, -37.97) * mm});
            skLineSegment(sketch, "E1061", {"start": v(23.01, -37.97) * mm, "end": v(23.06, -38) * mm});
            skLineSegment(sketch, "E1062", {"start": v(23.06, -38) * mm, "end": v(23.1, -38.04) * mm});
            skLineSegment(sketch, "E1063", {"start": v(23.1, -38.04) * mm, "end": v(23.14, -38.08) * mm});
            skLineSegment(sketch, "E1064", {"start": v(23.14, -38.08) * mm, "end": v(23.19, -38.11) * mm});
            skLineSegment(sketch, "E1065", {"start": v(23.19, -38.11) * mm, "end": v(23.23, -38.14) * mm});
            skLineSegment(sketch, "E1066", {"start": v(23.23, -38.14) * mm, "end": v(23.28, -38.17) * mm});
            skLineSegment(sketch, "E1067", {"start": v(23.28, -38.17) * mm, "end": v(23.33, -38.2) * mm});
            skLineSegment(sketch, "E1068", {"start": v(23.33, -38.2) * mm, "end": v(23.38, -38.23) * mm});
            skLineSegment(sketch, "E1069", {"start": v(23.38, -38.23) * mm, "end": v(23.43, -38.25) * mm});
            skLineSegment(sketch, "E1070", {"start": v(23.43, -38.25) * mm, "end": v(23.48, -38.27) * mm});
            skLineSegment(sketch, "E1071", {"start": v(23.48, -38.27) * mm, "end": v(23.53, -38.3) * mm});
            skLineSegment(sketch, "E1072", {"start": v(23.53, -38.3) * mm, "end": v(23.58, -38.31) * mm});
            skLineSegment(sketch, "E1073", {"start": v(23.58, -38.31) * mm, "end": v(23.64, -38.33) * mm});
            skLineSegment(sketch, "E1074", {"start": v(23.64, -38.33) * mm, "end": v(23.69, -38.35) * mm});
            skLineSegment(sketch, "E1075", {"start": v(23.69, -38.35) * mm, "end": v(23.74, -38.36) * mm});
            skLineSegment(sketch, "E1076", {"start": v(23.74, -38.36) * mm, "end": v(23.8, -38.37) * mm});
            skLineSegment(sketch, "E1077", {"start": v(23.8, -38.37) * mm, "end": v(23.85, -38.38) * mm});
            skLineSegment(sketch, "E1078", {"start": v(23.85, -38.38) * mm, "end": v(23.9, -38.4) * mm});
            skLineSegment(sketch, "E1079", {"start": v(23.9, -38.4) * mm, "end": v(23.96, -38.4) * mm});
            skLineSegment(sketch, "E1080", {"start": v(23.96, -38.4) * mm, "end": v(24.02, -38.4) * mm});
            skLineSegment(sketch, "E1081", {"start": v(24.02, -38.4) * mm, "end": v(24.07, -38.4) * mm});
            skLineSegment(sketch, "E1082", {"start": v(24.07, -38.4) * mm, "end": v(24.13, -38.4) * mm});
            skLineSegment(sketch, "E1083", {"start": v(24.13, -38.4) * mm, "end": v(24.19, -38.4) * mm});
            skLineSegment(sketch, "E1084", {"start": v(24.19, -38.4) * mm, "end": v(24.24, -38.4) * mm});
            skLineSegment(sketch, "E1085", {"start": v(24.24, -38.4) * mm, "end": v(24.3, -38.4) * mm});
            skLineSegment(sketch, "E1086", {"start": v(24.3, -38.4) * mm, "end": v(24.35, -38.39) * mm});
            skLineSegment(sketch, "E1087", {"start": v(24.35, -38.39) * mm, "end": v(24.4, -38.38) * mm});
            skLineSegment(sketch, "E1088", {"start": v(24.4, -38.38) * mm, "end": v(24.46, -38.37) * mm});
            skLineSegment(sketch, "E1089", {"start": v(24.46, -38.37) * mm, "end": v(24.52, -38.35) * mm});
            skLineSegment(sketch, "E1090", {"start": v(24.52, -38.35) * mm, "end": v(24.57, -38.34) * mm});
            skLineSegment(sketch, "E1091", {"start": v(24.57, -38.34) * mm, "end": v(24.62, -38.32) * mm});
            skLineSegment(sketch, "E1092", {"start": v(24.62, -38.32) * mm, "end": v(24.67, -38.3) * mm});
            skLineSegment(sketch, "E1093", {"start": v(24.67, -38.3) * mm, "end": v(24.73, -38.28) * mm});
            skLineSegment(sketch, "E1094", {"start": v(24.73, -38.28) * mm, "end": v(24.78, -38.26) * mm});
            skLineSegment(sketch, "E1095", {"start": v(24.78, -38.26) * mm, "end": v(24.83, -38.24) * mm});
            skLineSegment(sketch, "E1096", {"start": v(24.83, -38.24) * mm, "end": v(24.88, -38.2) * mm});
            skLineSegment(sketch, "E1097", {"start": v(24.88, -38.2) * mm, "end": v(24.93, -38.18) * mm});
            skLineSegment(sketch, "E1098", {"start": v(24.93, -38.18) * mm, "end": v(24.97, -38.15) * mm});
            skLineSegment(sketch, "E1099", {"start": v(24.97, -38.15) * mm, "end": v(25.02, -38.12) * mm});
            skLineSegment(sketch, "E1100", {"start": v(25.02, -38.12) * mm, "end": v(25.07, -38.1) * mm});
            skLineSegment(sketch, "E1101", {"start": v(25.07, -38.1) * mm, "end": v(25.1, -38.06) * mm});
            skLineSegment(sketch, "E1102", {"start": v(25.1, -38.06) * mm, "end": v(25.15, -38.02) * mm});
            skLineSegment(sketch, "E1103", {"start": v(25.15, -38.02) * mm, "end": v(25.2, -37.98) * mm});
            skLineSegment(sketch, "E1104", {"start": v(25.2, -37.98) * mm, "end": v(25.23, -37.95) * mm});
            skLineSegment(sketch, "E1105", {"start": v(25.23, -37.95) * mm, "end": v(25.27, -37.9) * mm});
            skLineSegment(sketch, "E1106", {"start": v(25.27, -37.9) * mm, "end": v(25.31, -37.87) * mm});
            skLineSegment(sketch, "E1107", {"start": v(25.31, -37.87) * mm, "end": v(25.35, -37.82) * mm});
            skLineSegment(sketch, "E1108", {"start": v(25.35, -37.82) * mm, "end": v(25.38, -37.78) * mm});
            skLineSegment(sketch, "E1109", {"start": v(25.38, -37.78) * mm, "end": v(25.42, -37.74) * mm});
            skLineSegment(sketch, "E1110", {"start": v(25.42, -37.74) * mm, "end": v(25.45, -37.69) * mm});
            skLineSegment(sketch, "E1111", {"start": v(25.45, -37.69) * mm, "end": v(25.48, -37.64) * mm});
            skLineSegment(sketch, "E1112", {"start": v(25.48, -37.64) * mm, "end": v(25.5, -37.6) * mm});
            skLineSegment(sketch, "E1113", {"start": v(25.5, -37.6) * mm, "end": v(25.53, -37.55) * mm});
            skLineSegment(sketch, "E1114", {"start": v(25.53, -37.55) * mm, "end": v(25.56, -37.5) * mm});
            skLineSegment(sketch, "E1115", {"start": v(25.56, -37.5) * mm, "end": v(25.58, -37.45) * mm});
            skLineSegment(sketch, "E1116", {"start": v(25.58, -37.45) * mm, "end": v(25.6, -37.4) * mm});
            skLineSegment(sketch, "E1117", {"start": v(25.6, -37.4) * mm, "end": v(25.62, -37.34) * mm});
            skLineSegment(sketch, "E1118", {"start": v(25.62, -37.34) * mm, "end": v(25.64, -37.29) * mm});
            skLineSegment(sketch, "E1119", {"start": v(25.64, -37.29) * mm, "end": v(25.66, -37.24) * mm});
            skLineSegment(sketch, "E1120", {"start": v(25.66, -37.24) * mm, "end": v(25.67, -37.18) * mm});
            skLineSegment(sketch, "E1121", {"start": v(25.67, -37.18) * mm, "end": v(25.68, -37.13) * mm});
            skLineSegment(sketch, "E1122", {"start": v(25.68, -37.13) * mm, "end": v(25.7, -37.07) * mm});
            skLineSegment(sketch, "E1123", {"start": v(25.7, -37.07) * mm, "end": v(25.7, -37.02) * mm});
            skLineSegment(sketch, "E1124", {"start": v(25.7, -37.02) * mm, "end": v(25.71, -36.96) * mm});
            skLineSegment(sketch, "E1125", {"start": v(25.71, -36.96) * mm, "end": v(25.72, -36.9) * mm});
            skLineSegment(sketch, "E1126", {"start": v(25.72, -36.9) * mm, "end": v(25.72, -36.85) * mm});
            skLineSegment(sketch, "E1127", {"start": v(25.72, -36.85) * mm, "end": v(25.72, -36.8) * mm});
            skLineSegment(sketch, "E1128", {"start": v(25.72, -36.8) * mm, "end": v(25.72, -36.74) * mm});
            skLineSegment(sketch, "E1129", {"start": v(25.72, -36.74) * mm, "end": v(25.72, -36.68) * mm});
            skLineSegment(sketch, "E1130", {"start": v(25.72, -36.68) * mm, "end": v(25.71, -36.63) * mm});
            skLineSegment(sketch, "E1131", {"start": v(25.71, -36.63) * mm, "end": v(25.7, -36.57) * mm});
            skLineSegment(sketch, "E1132", {"start": v(25.7, -36.57) * mm, "end": v(25.7, -36.52) * mm});
            skLineSegment(sketch, "E1133", {"start": v(25.7, -36.52) * mm, "end": v(25.68, -36.46) * mm});
            skLineSegment(sketch, "E1134", {"start": v(25.68, -36.46) * mm, "end": v(25.67, -36.4) * mm});
            skLineSegment(sketch, "E1135", {"start": v(25.67, -36.4) * mm, "end": v(25.66, -36.35) * mm});
            skLineSegment(sketch, "E1136", {"start": v(25.66, -36.35) * mm, "end": v(25.64, -36.3) * mm});
            skLineSegment(sketch, "E1137", {"start": v(25.64, -36.3) * mm, "end": v(25.62, -36.25) * mm});
            skLineSegment(sketch, "E1138", {"start": v(25.62, -36.25) * mm, "end": v(25.6, -36.2) * mm});
            skLineSegment(sketch, "E1139", {"start": v(25.6, -36.2) * mm, "end": v(25.58, -36.14) * mm});
            skLineSegment(sketch, "E1140", {"start": v(25.58, -36.14) * mm, "end": v(25.56, -36.1) * mm});
            skLineSegment(sketch, "E1141", {"start": v(25.56, -36.1) * mm, "end": v(25.53, -36.04) * mm});
            skLineSegment(sketch, "E1142", {"start": v(25.53, -36.04) * mm, "end": v(25.5, -36) * mm});
            skLineSegment(sketch, "E1143", {"start": v(25.5, -36) * mm, "end": v(25.47, -35.94) * mm});
            skLineSegment(sketch, "E1144", {"start": v(25.47, -35.94) * mm, "end": v(25.44, -35.9) * mm});
            skLineSegment(sketch, "E1145", {"start": v(25.44, -35.9) * mm, "end": v(25.41, -35.85) * mm});
            skLineSegment(sketch, "E1146", {"start": v(25.41, -35.85) * mm, "end": v(25.38, -35.8) * mm});
            skLineSegment(sketch, "E1147", {"start": v(25.38, -35.8) * mm, "end": v(25.34, -35.76) * mm});
            skLineSegment(sketch, "E1148", {"start": v(25.34, -35.76) * mm, "end": v(25.3, -35.72) * mm});
            skLineSegment(sketch, "E1149", {"start": v(25.3, -35.72) * mm, "end": v(25.27, -35.68) * mm});
            skLineSegment(sketch, "E1150", {"start": v(25.27, -35.68) * mm, "end": v(25.23, -35.64) * mm});
            skLineSegment(sketch, "E1151", {"start": v(25.23, -35.64) * mm, "end": v(25.19, -35.6) * mm});
            skLineSegment(sketch, "E1152", {"start": v(25.19, -35.6) * mm, "end": v(25.14, -35.56) * mm});
            skLineSegment(sketch, "E1153", {"start": v(25.14, -35.56) * mm, "end": v(25.1, -35.53) * mm});
            skLineSegment(sketch, "E1154", {"start": v(25.1, -35.53) * mm, "end": v(25.06, -35.5) * mm});
            skLineSegment(sketch, "E1155", {"start": v(25.06, -35.5) * mm, "end": v(25.01, -35.46) * mm});
            skLineSegment(sketch, "E1156", {"start": v(25.01, -35.46) * mm, "end": v(24.96, -35.43) * mm});
            skLineSegment(sketch, "E1157", {"start": v(24.96, -35.43) * mm, "end": v(24.91, -35.4) * mm});
            skLineSegment(sketch, "E1158", {"start": v(24.91, -35.4) * mm, "end": v(24.87, -35.38) * mm});
            skLineSegment(sketch, "E1159", {"start": v(24.87, -35.38) * mm, "end": v(24.82, -35.35) * mm});
            skLineSegment(sketch, "E1160", {"start": v(24.82, -35.35) * mm, "end": v(24.76, -35.33) * mm});
            skLineSegment(sketch, "E1161", {"start": v(24.76, -35.33) * mm, "end": v(24.71, -35.3) * mm});
            skLineSegment(sketch, "E1162", {"start": v(24.71, -35.3) * mm, "end": v(24.66, -35.28) * mm});
            skLineSegment(sketch, "E1163", {"start": v(24.66, -35.28) * mm, "end": v(24.6, -35.27) * mm});
            skLineSegment(sketch, "E1164", {"start": v(24.6, -35.27) * mm, "end": v(24.55, -35.25) * mm});
            skLineSegment(sketch, "E1165", {"start": v(24.55, -35.25) * mm, "end": v(24.5, -35.24) * mm});
            skLineSegment(sketch, "E1166", {"start": v(24.5, -35.24) * mm, "end": v(24.45, -35.22) * mm});
            skLineSegment(sketch, "E1167", {"start": v(24.45, -35.22) * mm, "end": v(24.4, -35.21) * mm});
            skLineSegment(sketch, "E1168", {"start": v(24.4, -35.21) * mm, "end": v(24.33, -35.2) * mm});
            skLineSegment(sketch, "E1169", {"start": v(24.33, -35.2) * mm, "end": v(24.28, -35.2) * mm});
            skLineSegment(sketch, "E1170", {"start": v(24.28, -35.2) * mm, "end": v(24.22, -35.2) * mm});
            skLineSegment(sketch, "E1171", {"start": v(24.22, -35.2) * mm, "end": v(24.17, -35.19) * mm});
            skLineSegment(sketch, "E1172", {"start": v(24.17, -35.19) * mm, "end": v(24.11, -35.19) * mm});
            skLineSegment(sketch, "E1173", {"start": v(-24.11, -33.92) * mm, "end": v(-24.17, -33.92) * mm});
            skLineSegment(sketch, "E1174", {"start": v(-24.17, -33.92) * mm, "end": v(-24.22, -33.92) * mm});
            skLineSegment(sketch, "E1175", {"start": v(-24.22, -33.92) * mm, "end": v(-24.28, -33.93) * mm});
            skLineSegment(sketch, "E1176", {"start": v(-24.28, -33.93) * mm, "end": v(-24.33, -33.93) * mm});
            skLineSegment(sketch, "E1177", {"start": v(-24.33, -33.93) * mm, "end": v(-24.39, -33.94) * mm});
            skLineSegment(sketch, "E1178", {"start": v(-24.39, -33.94) * mm, "end": v(-24.44, -33.95) * mm});
            skLineSegment(sketch, "E1179", {"start": v(-24.44, -33.95) * mm, "end": v(-24.5, -33.97) * mm});
            skLineSegment(sketch, "E1180", {"start": v(-24.5, -33.97) * mm, "end": v(-24.55, -33.98) * mm});
            skLineSegment(sketch, "E1181", {"start": v(-24.55, -33.98) * mm, "end": v(-24.6, -34) * mm});
            skLineSegment(sketch, "E1182", {"start": v(-24.6, -34) * mm, "end": v(-24.66, -34.01) * mm});
            skLineSegment(sketch, "E1183", {"start": v(-24.66, -34.01) * mm, "end": v(-24.7, -34.03) * mm});
            skLineSegment(sketch, "E1184", {"start": v(-24.7, -34.03) * mm, "end": v(-24.76, -34.06) * mm});
            skLineSegment(sketch, "E1185", {"start": v(-24.76, -34.06) * mm, "end": v(-24.81, -34.08) * mm});
            skLineSegment(sketch, "E1186", {"start": v(-24.81, -34.08) * mm, "end": v(-24.86, -34.1) * mm});
            skLineSegment(sketch, "E1187", {"start": v(-24.86, -34.1) * mm, "end": v(-24.9, -34.13) * mm});
            skLineSegment(sketch, "E1188", {"start": v(-24.9, -34.13) * mm, "end": v(-24.96, -34.16) * mm});
            skLineSegment(sketch, "E1189", {"start": v(-24.96, -34.16) * mm, "end": v(-25, -34.19) * mm});
            skLineSegment(sketch, "E1190", {"start": v(-25, -34.19) * mm, "end": v(-25.05, -34.22) * mm});
            skLineSegment(sketch, "E1191", {"start": v(-25.05, -34.22) * mm, "end": v(-25.1, -34.25) * mm});
            skLineSegment(sketch, "E1192", {"start": v(-25.1, -34.25) * mm, "end": v(-25.14, -34.29) * mm});
            skLineSegment(sketch, "E1193", {"start": v(-25.14, -34.29) * mm, "end": v(-25.18, -34.33) * mm});
            skLineSegment(sketch, "E1194", {"start": v(-25.18, -34.33) * mm, "end": v(-25.22, -34.36) * mm});
            skLineSegment(sketch, "E1195", {"start": v(-25.22, -34.36) * mm, "end": v(-25.26, -34.4) * mm});
            skLineSegment(sketch, "E1196", {"start": v(-25.26, -34.4) * mm, "end": v(-25.3, -34.44) * mm});
            skLineSegment(sketch, "E1197", {"start": v(-25.3, -34.44) * mm, "end": v(-25.34, -34.48) * mm});
            skLineSegment(sketch, "E1198", {"start": v(-25.34, -34.48) * mm, "end": v(-25.37, -34.53) * mm});
            skLineSegment(sketch, "E1199", {"start": v(-25.37, -34.53) * mm, "end": v(-25.4, -34.57) * mm});
            skLineSegment(sketch, "E1200", {"start": v(-25.4, -34.57) * mm, "end": v(-25.44, -34.62) * mm});
            skLineSegment(sketch, "E1201", {"start": v(-25.44, -34.62) * mm, "end": v(-25.47, -34.66) * mm});
            skLineSegment(sketch, "E1202", {"start": v(-25.47, -34.66) * mm, "end": v(-25.5, -34.71) * mm});
            skLineSegment(sketch, "E1203", {"start": v(-25.5, -34.71) * mm, "end": v(-25.52, -34.76) * mm});
            skLineSegment(sketch, "E1204", {"start": v(-25.52, -34.76) * mm, "end": v(-25.55, -34.8) * mm});
            skLineSegment(sketch, "E1205", {"start": v(-25.55, -34.8) * mm, "end": v(-25.57, -34.86) * mm});
            skLineSegment(sketch, "E1206", {"start": v(-25.57, -34.86) * mm, "end": v(-25.6, -34.91) * mm});
            skLineSegment(sketch, "E1207", {"start": v(-25.6, -34.91) * mm, "end": v(-25.62, -34.96) * mm});
            skLineSegment(sketch, "E1208", {"start": v(-25.62, -34.96) * mm, "end": v(-25.64, -35.02) * mm});
            skLineSegment(sketch, "E1209", {"start": v(-25.64, -35.02) * mm, "end": v(-25.65, -35.07) * mm});
            skLineSegment(sketch, "E1210", {"start": v(-25.65, -35.07) * mm, "end": v(-25.67, -35.12) * mm});
            skLineSegment(sketch, "E1211", {"start": v(-25.67, -35.12) * mm, "end": v(-25.68, -35.18) * mm});
            skLineSegment(sketch, "E1212", {"start": v(-25.68, -35.18) * mm, "end": v(-25.7, -35.23) * mm});
            skLineSegment(sketch, "E1213", {"start": v(-25.7, -35.23) * mm, "end": v(-25.7, -35.29) * mm});
            skLineSegment(sketch, "E1214", {"start": v(-25.7, -35.29) * mm, "end": v(-25.7, -35.34) * mm});
            skLineSegment(sketch, "E1215", {"start": v(-25.7, -35.34) * mm, "end": v(-25.71, -35.4) * mm});
            skLineSegment(sketch, "E1216", {"start": v(-25.71, -35.4) * mm, "end": v(-25.72, -35.45) * mm});
            skLineSegment(sketch, "E1217", {"start": v(-25.72, -35.45) * mm, "end": v(-25.72, -35.5) * mm});
            skLineSegment(sketch, "E1218", {"start": v(-25.72, -35.5) * mm, "end": v(-25.72, -35.56) * mm});
            skLineSegment(sketch, "E1219", {"start": v(-25.72, -35.56) * mm, "end": v(-25.72, -35.62) * mm});
            skLineSegment(sketch, "E1220", {"start": v(-25.72, -35.62) * mm, "end": v(-25.71, -35.67) * mm});
            skLineSegment(sketch, "E1221", {"start": v(-25.71, -35.67) * mm, "end": v(-25.7, -35.73) * mm});
            skLineSegment(sketch, "E1222", {"start": v(-25.7, -35.73) * mm, "end": v(-25.7, -35.79) * mm});
            skLineSegment(sketch, "E1223", {"start": v(-25.7, -35.79) * mm, "end": v(-25.69, -35.84) * mm});
            skLineSegment(sketch, "E1224", {"start": v(-25.69, -35.84) * mm, "end": v(-25.68, -35.9) * mm});
            skLineSegment(sketch, "E1225", {"start": v(-25.68, -35.9) * mm, "end": v(-25.66, -35.95) * mm});
            skLineSegment(sketch, "E1226", {"start": v(-25.66, -35.95) * mm, "end": v(-25.65, -36) * mm});
            skLineSegment(sketch, "E1227", {"start": v(-25.65, -36) * mm, "end": v(-25.63, -36.05) * mm});
            skLineSegment(sketch, "E1228", {"start": v(-25.63, -36.05) * mm, "end": v(-25.61, -36.1) * mm});
            skLineSegment(sketch, "E1229", {"start": v(-25.61, -36.1) * mm, "end": v(-25.59, -36.16) * mm});
            skLineSegment(sketch, "E1230", {"start": v(-25.59, -36.16) * mm, "end": v(-25.57, -36.2) * mm});
            skLineSegment(sketch, "E1231", {"start": v(-25.57, -36.2) * mm, "end": v(-25.54, -36.26) * mm});
            skLineSegment(sketch, "E1232", {"start": v(-25.54, -36.26) * mm, "end": v(-25.52, -36.3) * mm});
            skLineSegment(sketch, "E1233", {"start": v(-25.52, -36.3) * mm, "end": v(-25.49, -36.36) * mm});
            skLineSegment(sketch, "E1234", {"start": v(-25.49, -36.36) * mm, "end": v(-25.46, -36.4) * mm});
            skLineSegment(sketch, "E1235", {"start": v(-25.46, -36.4) * mm, "end": v(-25.43, -36.45) * mm});
            skLineSegment(sketch, "E1236", {"start": v(-25.43, -36.45) * mm, "end": v(-25.4, -36.5) * mm});
            skLineSegment(sketch, "E1237", {"start": v(-25.4, -36.5) * mm, "end": v(-25.36, -36.54) * mm});
            skLineSegment(sketch, "E1238", {"start": v(-25.36, -36.54) * mm, "end": v(-25.32, -36.58) * mm});
            skLineSegment(sketch, "E1239", {"start": v(-25.32, -36.58) * mm, "end": v(-25.29, -36.62) * mm});
            skLineSegment(sketch, "E1240", {"start": v(-25.29, -36.62) * mm, "end": v(-25.25, -36.66) * mm});
            skLineSegment(sketch, "E1241", {"start": v(-25.25, -36.66) * mm, "end": v(-25.2, -36.7) * mm});
            skLineSegment(sketch, "E1242", {"start": v(-25.2, -36.7) * mm, "end": v(-25.17, -36.74) * mm});
            skLineSegment(sketch, "E1243", {"start": v(-25.17, -36.74) * mm, "end": v(-25.12, -36.78) * mm});
            skLineSegment(sketch, "E1244", {"start": v(-25.12, -36.78) * mm, "end": v(-25.08, -36.8) * mm});
            skLineSegment(sketch, "E1245", {"start": v(-25.08, -36.8) * mm, "end": v(-25.03, -36.84) * mm});
            skLineSegment(sketch, "E1246", {"start": v(-25.03, -36.84) * mm, "end": v(-24.99, -36.87) * mm});
            skLineSegment(sketch, "E1247", {"start": v(-24.99, -36.87) * mm, "end": v(-24.94, -36.9) * mm});
            skLineSegment(sketch, "E1248", {"start": v(-24.94, -36.9) * mm, "end": v(-24.9, -36.93) * mm});
            skLineSegment(sketch, "E1249", {"start": v(-24.9, -36.93) * mm, "end": v(-24.84, -36.96) * mm});
            skLineSegment(sketch, "E1250", {"start": v(-24.84, -36.96) * mm, "end": v(-24.8, -36.98) * mm});
            skLineSegment(sketch, "E1251", {"start": v(-24.8, -36.98) * mm, "end": v(-24.74, -37) * mm});
            skLineSegment(sketch, "E1252", {"start": v(-24.74, -37) * mm, "end": v(-24.7, -37.03) * mm});
            skLineSegment(sketch, "E1253", {"start": v(-24.7, -37.03) * mm, "end": v(-24.64, -37.05) * mm});
            skLineSegment(sketch, "E1254", {"start": v(-24.64, -37.05) * mm, "end": v(-24.59, -37.06) * mm});
            skLineSegment(sketch, "E1255", {"start": v(-24.59, -37.06) * mm, "end": v(-24.53, -37.08) * mm});
            skLineSegment(sketch, "E1256", {"start": v(-24.53, -37.08) * mm, "end": v(-24.48, -37.1) * mm});
            skLineSegment(sketch, "E1257", {"start": v(-24.48, -37.1) * mm, "end": v(-24.42, -37.1) * mm});
            skLineSegment(sketch, "E1258", {"start": v(-24.42, -37.1) * mm, "end": v(-24.37, -37.11) * mm});
            skLineSegment(sketch, "E1259", {"start": v(-24.37, -37.11) * mm, "end": v(-24.31, -37.12) * mm});
            skLineSegment(sketch, "E1260", {"start": v(-24.31, -37.12) * mm, "end": v(-24.26, -37.13) * mm});
            skLineSegment(sketch, "E1261", {"start": v(-24.26, -37.13) * mm, "end": v(-24.2, -37.13) * mm});
            skLineSegment(sketch, "E1262", {"start": v(-24.2, -37.13) * mm, "end": v(-24.15, -37.13) * mm});
            skLineSegment(sketch, "E1263", {"start": v(-24.15, -37.13) * mm, "end": v(-24.1, -37.13) * mm});
            skLineSegment(sketch, "E1264", {"start": v(-24.1, -37.13) * mm, "end": v(-24.04, -37.13) * mm});
            skLineSegment(sketch, "E1265", {"start": v(-24.04, -37.13) * mm, "end": v(-23.98, -37.13) * mm});
            skLineSegment(sketch, "E1266", {"start": v(-23.98, -37.13) * mm, "end": v(-23.93, -37.12) * mm});
            skLineSegment(sketch, "E1267", {"start": v(-23.93, -37.12) * mm, "end": v(-23.87, -37.12) * mm});
            skLineSegment(sketch, "E1268", {"start": v(-23.87, -37.12) * mm, "end": v(-23.82, -37.1) * mm});
            skLineSegment(sketch, "E1269", {"start": v(-23.82, -37.1) * mm, "end": v(-23.76, -37.1) * mm});
            skLineSegment(sketch, "E1270", {"start": v(-23.76, -37.1) * mm, "end": v(-23.7, -37.08) * mm});
            skLineSegment(sketch, "E1271", {"start": v(-23.7, -37.08) * mm, "end": v(-23.65, -37.07) * mm});
            skLineSegment(sketch, "E1272", {"start": v(-23.65, -37.07) * mm, "end": v(-23.6, -37.05) * mm});
            skLineSegment(sketch, "E1273", {"start": v(-23.6, -37.05) * mm, "end": v(-23.55, -37.03) * mm});
            skLineSegment(sketch, "E1274", {"start": v(-23.55, -37.03) * mm, "end": v(-23.5, -37.01) * mm});
            skLineSegment(sketch, "E1275", {"start": v(-23.5, -37.01) * mm, "end": v(-23.44, -36.99) * mm});
            skLineSegment(sketch, "E1276", {"start": v(-23.44, -36.99) * mm, "end": v(-23.4, -36.97) * mm});
            skLineSegment(sketch, "E1277", {"start": v(-23.4, -36.97) * mm, "end": v(-23.34, -36.94) * mm});
            skLineSegment(sketch, "E1278", {"start": v(-23.34, -36.94) * mm, "end": v(-23.3, -36.91) * mm});
            skLineSegment(sketch, "E1279", {"start": v(-23.3, -36.91) * mm, "end": v(-23.25, -36.88) * mm});
            skLineSegment(sketch, "E1280", {"start": v(-23.25, -36.88) * mm, "end": v(-23.2, -36.85) * mm});
            skLineSegment(sketch, "E1281", {"start": v(-23.2, -36.85) * mm, "end": v(-23.16, -36.82) * mm});
            skLineSegment(sketch, "E1282", {"start": v(-23.16, -36.82) * mm, "end": v(-23.11, -36.79) * mm});
            skLineSegment(sketch, "E1283", {"start": v(-23.11, -36.79) * mm, "end": v(-23.07, -36.75) * mm});
            skLineSegment(sketch, "E1284", {"start": v(-23.07, -36.75) * mm, "end": v(-23.03, -36.71) * mm});
            skLineSegment(sketch, "E1285", {"start": v(-23.03, -36.71) * mm, "end": v(-22.99, -36.68) * mm});
            skLineSegment(sketch, "E1286", {"start": v(-22.99, -36.68) * mm, "end": v(-22.95, -36.64) * mm});
            skLineSegment(sketch, "E1287", {"start": v(-22.95, -36.64) * mm, "end": v(-22.91, -36.6) * mm});
            skLineSegment(sketch, "E1288", {"start": v(-22.91, -36.6) * mm, "end": v(-22.87, -36.55) * mm});
            skLineSegment(sketch, "E1289", {"start": v(-22.87, -36.55) * mm, "end": v(-22.84, -36.51) * mm});
            skLineSegment(sketch, "E1290", {"start": v(-22.84, -36.51) * mm, "end": v(-22.8, -36.47) * mm});
            skLineSegment(sketch, "E1291", {"start": v(-22.8, -36.47) * mm, "end": v(-22.77, -36.42) * mm});
            skLineSegment(sketch, "E1292", {"start": v(-22.77, -36.42) * mm, "end": v(-22.74, -36.37) * mm});
            skLineSegment(sketch, "E1293", {"start": v(-22.74, -36.37) * mm, "end": v(-22.72, -36.32) * mm});
            skLineSegment(sketch, "E1294", {"start": v(-22.72, -36.32) * mm, "end": v(-22.69, -36.28) * mm});
            skLineSegment(sketch, "E1295", {"start": v(-22.69, -36.28) * mm, "end": v(-22.66, -36.23) * mm});
            skLineSegment(sketch, "E1296", {"start": v(-22.66, -36.23) * mm, "end": v(-22.64, -36.18) * mm});
            skLineSegment(sketch, "E1297", {"start": v(-22.64, -36.18) * mm, "end": v(-22.62, -36.12) * mm});
            skLineSegment(sketch, "E1298", {"start": v(-22.62, -36.12) * mm, "end": v(-22.6, -36.07) * mm});
            skLineSegment(sketch, "E1299", {"start": v(-22.6, -36.07) * mm, "end": v(-22.58, -36.02) * mm});
            skLineSegment(sketch, "E1300", {"start": v(-22.58, -36.02) * mm, "end": v(-22.56, -35.97) * mm});
            skLineSegment(sketch, "E1301", {"start": v(-22.56, -35.97) * mm, "end": v(-22.55, -35.91) * mm});
            skLineSegment(sketch, "E1302", {"start": v(-22.55, -35.91) * mm, "end": v(-22.54, -35.86) * mm});
            skLineSegment(sketch, "E1303", {"start": v(-22.54, -35.86) * mm, "end": v(-22.53, -35.8) * mm});
            skLineSegment(sketch, "E1304", {"start": v(-22.53, -35.8) * mm, "end": v(-22.52, -35.75) * mm});
            skLineSegment(sketch, "E1305", {"start": v(-22.52, -35.75) * mm, "end": v(-22.51, -35.7) * mm});
            skLineSegment(sketch, "E1306", {"start": v(-22.51, -35.7) * mm, "end": v(-22.5, -35.64) * mm});
            skLineSegment(sketch, "E1307", {"start": v(-22.5, -35.64) * mm, "end": v(-22.5, -35.58) * mm});
            skLineSegment(sketch, "E1308", {"start": v(-22.5, -35.58) * mm, "end": v(-22.5, -35.53) * mm});
            skLineSegment(sketch, "E1309", {"start": v(-22.5, -35.53) * mm, "end": v(-22.5, -35.47) * mm});
            skLineSegment(sketch, "E1310", {"start": v(-22.5, -35.47) * mm, "end": v(-22.5, -35.41) * mm});
            skLineSegment(sketch, "E1311", {"start": v(-22.5, -35.41) * mm, "end": v(-22.51, -35.36) * mm});
            skLineSegment(sketch, "E1312", {"start": v(-22.51, -35.36) * mm, "end": v(-22.52, -35.3) * mm});
            skLineSegment(sketch, "E1313", {"start": v(-22.52, -35.3) * mm, "end": v(-22.53, -35.25) * mm});
            skLineSegment(sketch, "E1314", {"start": v(-22.53, -35.25) * mm, "end": v(-22.54, -35.2) * mm});
            skLineSegment(sketch, "E1315", {"start": v(-22.54, -35.2) * mm, "end": v(-22.55, -35.14) * mm});
            skLineSegment(sketch, "E1316", {"start": v(-22.55, -35.14) * mm, "end": v(-22.57, -35.08) * mm});
            skLineSegment(sketch, "E1317", {"start": v(-22.57, -35.08) * mm, "end": v(-22.58, -35.03) * mm});
            skLineSegment(sketch, "E1318", {"start": v(-22.58, -35.03) * mm, "end": v(-22.6, -34.98) * mm});
            skLineSegment(sketch, "E1319", {"start": v(-22.6, -34.98) * mm, "end": v(-22.62, -34.92) * mm});
            skLineSegment(sketch, "E1320", {"start": v(-22.62, -34.92) * mm, "end": v(-22.64, -34.87) * mm});
            skLineSegment(sketch, "E1321", {"start": v(-22.64, -34.87) * mm, "end": v(-22.67, -34.82) * mm});
            skLineSegment(sketch, "E1322", {"start": v(-22.67, -34.82) * mm, "end": v(-22.7, -34.77) * mm});
            skLineSegment(sketch, "E1323", {"start": v(-22.7, -34.77) * mm, "end": v(-22.72, -34.72) * mm});
            skLineSegment(sketch, "E1324", {"start": v(-22.72, -34.72) * mm, "end": v(-22.75, -34.67) * mm});
            skLineSegment(sketch, "E1325", {"start": v(-22.75, -34.67) * mm, "end": v(-22.78, -34.63) * mm});
            skLineSegment(sketch, "E1326", {"start": v(-22.78, -34.63) * mm, "end": v(-22.8, -34.58) * mm});
            skLineSegment(sketch, "E1327", {"start": v(-22.8, -34.58) * mm, "end": v(-22.84, -34.54) * mm});
            skLineSegment(sketch, "E1328", {"start": v(-22.84, -34.54) * mm, "end": v(-22.88, -34.5) * mm});
            skLineSegment(sketch, "E1329", {"start": v(-22.88, -34.5) * mm, "end": v(-22.92, -34.45) * mm});
            skLineSegment(sketch, "E1330", {"start": v(-22.92, -34.45) * mm, "end": v(-22.95, -34.4) * mm});
            skLineSegment(sketch, "E1331", {"start": v(-22.95, -34.4) * mm, "end": v(-23, -34.37) * mm});
            skLineSegment(sketch, "E1332", {"start": v(-23, -34.37) * mm, "end": v(-23.03, -34.33) * mm});
            skLineSegment(sketch, "E1333", {"start": v(-23.03, -34.33) * mm, "end": v(-23.08, -34.3) * mm});
            skLineSegment(sketch, "E1334", {"start": v(-23.08, -34.3) * mm, "end": v(-23.12, -34.26) * mm});
            skLineSegment(sketch, "E1335", {"start": v(-23.12, -34.26) * mm, "end": v(-23.17, -34.23) * mm});
            skLineSegment(sketch, "E1336", {"start": v(-23.17, -34.23) * mm, "end": v(-23.21, -34.2) * mm});
            skLineSegment(sketch, "E1337", {"start": v(-23.21, -34.2) * mm, "end": v(-23.26, -34.16) * mm});
            skLineSegment(sketch, "E1338", {"start": v(-23.26, -34.16) * mm, "end": v(-23.3, -34.13) * mm});
            skLineSegment(sketch, "E1339", {"start": v(-23.3, -34.13) * mm, "end": v(-23.36, -34.1) * mm});
            skLineSegment(sketch, "E1340", {"start": v(-23.36, -34.1) * mm, "end": v(-23.4, -34.08) * mm});
            skLineSegment(sketch, "E1341", {"start": v(-23.4, -34.08) * mm, "end": v(-23.46, -34.06) * mm});
            skLineSegment(sketch, "E1342", {"start": v(-23.46, -34.06) * mm, "end": v(-23.5, -34.04) * mm});
            skLineSegment(sketch, "E1343", {"start": v(-23.5, -34.04) * mm, "end": v(-23.56, -34.02) * mm});
            skLineSegment(sketch, "E1344", {"start": v(-23.56, -34.02) * mm, "end": v(-23.61, -34) * mm});
            skLineSegment(sketch, "E1345", {"start": v(-23.61, -34) * mm, "end": v(-23.67, -33.98) * mm});
            skLineSegment(sketch, "E1346", {"start": v(-23.67, -33.98) * mm, "end": v(-23.72, -33.97) * mm});
            skLineSegment(sketch, "E1347", {"start": v(-23.72, -33.97) * mm, "end": v(-23.78, -33.95) * mm});
            skLineSegment(sketch, "E1348", {"start": v(-23.78, -33.95) * mm, "end": v(-23.83, -33.94) * mm});
            skLineSegment(sketch, "E1349", {"start": v(-23.83, -33.94) * mm, "end": v(-23.89, -33.93) * mm});
            skLineSegment(sketch, "E1350", {"start": v(-23.89, -33.93) * mm, "end": v(-23.94, -33.93) * mm});
            skLineSegment(sketch, "E1351", {"start": v(-23.94, -33.93) * mm, "end": v(-24, -33.92) * mm});
            skLineSegment(sketch, "E1352", {"start": v(-24, -33.92) * mm, "end": v(-24.05, -33.92) * mm});
            skLineSegment(sketch, "E1353", {"start": v(-24.05, -33.92) * mm, "end": v(-24.11, -33.92) * mm});
            skLineSegment(sketch, "E1354", {"start": v(-26.65, 45.68) * mm, "end": v(-24.11, 48.22) * mm});
            skLineSegment(sketch, "E1355", {"start": v(-24.11, 48.22) * mm, "end": v(-13.95, 48.22) * mm});
            skLineSegment(sketch, "E1356", {"start": v(-13.95, 48.22) * mm, "end": v(-11.42, 50.76) * mm});
            skLineSegment(sketch, "E1357", {"start": v(-11.42, 50.76) * mm, "end": v(22.84, 50.76) * mm});
            skLineSegment(sketch, "E1358", {"start": v(22.84, 50.76) * mm, "end": v(25.38, 48.22) * mm});
            skLineSegment(sketch, "E1359", {"start": v(25.38, 48.22) * mm, "end": v(25.66, 48.22) * mm});
            skLineSegment(sketch, "E1360", {"start": v(25.66, 48.22) * mm, "end": v(25.9, 48.2) * mm});
            skLineSegment(sketch, "E1361", {"start": v(25.9, 48.2) * mm, "end": v(26.14, 48.1) * mm});
            skLineSegment(sketch, "E1362", {"start": v(26.14, 48.1) * mm, "end": v(26.35, 47.95) * mm});
            skLineSegment(sketch, "E1363", {"start": v(26.35, 47.95) * mm, "end": v(26.52, 47.74) * mm});
            skLineSegment(sketch, "E1364", {"start": v(26.52, 47.74) * mm, "end": v(26.6, 47.48) * mm});
            skLineSegment(sketch, "E1365", {"start": v(26.6, 47.48) * mm, "end": v(26.65, 47.23) * mm});
            skLineSegment(sketch, "E1366", {"start": v(26.65, 47.23) * mm, "end": v(26.65, -49.77) * mm});
            skLineSegment(sketch, "E1367", {"start": v(26.65, -49.77) * mm, "end": v(26.6, -50.02) * mm});
            skLineSegment(sketch, "E1368", {"start": v(26.6, -50.02) * mm, "end": v(26.52, -50.25) * mm});
            skLineSegment(sketch, "E1369", {"start": v(26.52, -50.25) * mm, "end": v(26.35, -50.46) * mm});
            skLineSegment(sketch, "E1370", {"start": v(26.35, -50.46) * mm, "end": v(26.14, -50.63) * mm});
            skLineSegment(sketch, "E1371", {"start": v(26.14, -50.63) * mm, "end": v(25.9, -50.72) * mm});
            skLineSegment(sketch, "E1372", {"start": v(25.9, -50.72) * mm, "end": v(25.66, -50.76) * mm});
            skLineSegment(sketch, "E1373", {"start": v(25.66, -50.76) * mm, "end": v(-25.63, -50.76) * mm});
            skLineSegment(sketch, "E1374", {"start": v(-25.63, -50.76) * mm, "end": v(-25.9, -50.72) * mm});
            skLineSegment(sketch, "E1375", {"start": v(-25.9, -50.72) * mm, "end": v(-26.14, -50.63) * mm});
            skLineSegment(sketch, "E1376", {"start": v(-26.14, -50.63) * mm, "end": v(-26.35, -50.46) * mm});
            skLineSegment(sketch, "E1377", {"start": v(-26.35, -50.46) * mm, "end": v(-26.5, -50.25) * mm});
            skLineSegment(sketch, "E1378", {"start": v(-26.5, -50.25) * mm, "end": v(-26.6, -50.02) * mm});
            skLineSegment(sketch, "E1379", {"start": v(-26.6, -50.02) * mm, "end": v(-26.65, -49.77) * mm});
            skLineSegment(sketch, "E1380", {"start": v(-26.65, -49.77) * mm, "end": v(-26.65, 45.68) * mm});
            skLineSegment(sketch, "E1381", {"start": v(19.03, 16.84) * mm, "end": v(18.98, 16.84) * mm});
            skLineSegment(sketch, "E1382", {"start": v(18.98, 16.84) * mm, "end": v(18.92, 16.84) * mm});
            skLineSegment(sketch, "E1383", {"start": v(18.92, 16.84) * mm, "end": v(18.87, 16.83) * mm});
            skLineSegment(sketch, "E1384", {"start": v(18.87, 16.83) * mm, "end": v(18.81, 16.83) * mm});
            skLineSegment(sketch, "E1385", {"start": v(18.81, 16.83) * mm, "end": v(18.76, 16.82) * mm});
            skLineSegment(sketch, "E1386", {"start": v(18.76, 16.82) * mm, "end": v(18.7, 16.8) * mm});
            skLineSegment(sketch, "E1387", {"start": v(18.7, 16.8) * mm, "end": v(18.65, 16.8) * mm});
            skLineSegment(sketch, "E1388", {"start": v(18.65, 16.8) * mm, "end": v(18.6, 16.78) * mm});
            skLineSegment(sketch, "E1389", {"start": v(18.6, 16.78) * mm, "end": v(18.54, 16.77) * mm});
            skLineSegment(sketch, "E1390", {"start": v(18.54, 16.77) * mm, "end": v(18.49, 16.75) * mm});
            skLineSegment(sketch, "E1391", {"start": v(18.49, 16.75) * mm, "end": v(18.43, 16.73) * mm});
            skLineSegment(sketch, "E1392", {"start": v(18.43, 16.73) * mm, "end": v(18.38, 16.7) * mm});
            skLineSegment(sketch, "E1393", {"start": v(18.38, 16.7) * mm, "end": v(18.33, 16.68) * mm});
            skLineSegment(sketch, "E1394", {"start": v(18.33, 16.68) * mm, "end": v(18.28, 16.66) * mm});
            skLineSegment(sketch, "E1395", {"start": v(18.28, 16.66) * mm, "end": v(18.23, 16.63) * mm});
            skLineSegment(sketch, "E1396", {"start": v(18.23, 16.63) * mm, "end": v(18.19, 16.6) * mm});
            skLineSegment(sketch, "E1397", {"start": v(18.19, 16.6) * mm, "end": v(18.14, 16.57) * mm});
            skLineSegment(sketch, "E1398", {"start": v(18.14, 16.57) * mm, "end": v(18.1, 16.54) * mm});
            skLineSegment(sketch, "E1399", {"start": v(18.1, 16.54) * mm, "end": v(18.05, 16.5) * mm});
            skLineSegment(sketch, "E1400", {"start": v(18.05, 16.5) * mm, "end": v(18, 16.47) * mm});
            skLineSegment(sketch, "E1401", {"start": v(18, 16.47) * mm, "end": v(17.96, 16.44) * mm});
            skLineSegment(sketch, "E1402", {"start": v(17.96, 16.44) * mm, "end": v(17.92, 16.4) * mm});
            skLineSegment(sketch, "E1403", {"start": v(17.92, 16.4) * mm, "end": v(17.88, 16.36) * mm});
            skLineSegment(sketch, "E1404", {"start": v(17.88, 16.36) * mm, "end": v(17.84, 16.32) * mm});
            skLineSegment(sketch, "E1405", {"start": v(17.84, 16.32) * mm, "end": v(17.8, 16.28) * mm});
            skLineSegment(sketch, "E1406", {"start": v(17.8, 16.28) * mm, "end": v(17.77, 16.23) * mm});
            skLineSegment(sketch, "E1407", {"start": v(17.77, 16.23) * mm, "end": v(17.74, 16.19) * mm});
            skLineSegment(sketch, "E1408", {"start": v(17.74, 16.19) * mm, "end": v(17.7, 16.14) * mm});
            skLineSegment(sketch, "E1409", {"start": v(17.7, 16.14) * mm, "end": v(17.68, 16.1) * mm});
            skLineSegment(sketch, "E1410", {"start": v(17.68, 16.1) * mm, "end": v(17.65, 16.05) * mm});
            skLineSegment(sketch, "E1411", {"start": v(17.65, 16.05) * mm, "end": v(17.62, 16) * mm});
            skLineSegment(sketch, "E1412", {"start": v(17.62, 16) * mm, "end": v(17.6, 15.95) * mm});
            skLineSegment(sketch, "E1413", {"start": v(17.6, 15.95) * mm, "end": v(17.57, 15.9) * mm});
            skLineSegment(sketch, "E1414", {"start": v(17.57, 15.9) * mm, "end": v(17.55, 15.85) * mm});
            skLineSegment(sketch, "E1415", {"start": v(17.55, 15.85) * mm, "end": v(17.53, 15.8) * mm});
            skLineSegment(sketch, "E1416", {"start": v(17.53, 15.8) * mm, "end": v(17.5, 15.75) * mm});
            skLineSegment(sketch, "E1417", {"start": v(17.5, 15.75) * mm, "end": v(17.5, 15.7) * mm});
            skLineSegment(sketch, "E1418", {"start": v(17.5, 15.7) * mm, "end": v(17.48, 15.64) * mm});
            skLineSegment(sketch, "E1419", {"start": v(17.48, 15.64) * mm, "end": v(17.46, 15.58) * mm});
            skLineSegment(sketch, "E1420", {"start": v(17.46, 15.58) * mm, "end": v(17.45, 15.53) * mm});
            skLineSegment(sketch, "E1421", {"start": v(17.45, 15.53) * mm, "end": v(17.44, 15.48) * mm});
            skLineSegment(sketch, "E1422", {"start": v(17.44, 15.48) * mm, "end": v(17.44, 15.42) * mm});
            skLineSegment(sketch, "E1423", {"start": v(17.44, 15.42) * mm, "end": v(17.43, 15.36) * mm});
            skLineSegment(sketch, "E1424", {"start": v(17.43, 15.36) * mm, "end": v(17.43, 15.3) * mm});
            skLineSegment(sketch, "E1425", {"start": v(17.43, 15.3) * mm, "end": v(17.42, 15.25) * mm});
            skLineSegment(sketch, "E1426", {"start": v(17.42, 15.25) * mm, "end": v(17.43, 15.2) * mm});
            skLineSegment(sketch, "E1427", {"start": v(17.43, 15.2) * mm, "end": v(17.43, 15.14) * mm});
            skLineSegment(sketch, "E1428", {"start": v(17.43, 15.14) * mm, "end": v(17.43, 15.09) * mm});
            skLineSegment(sketch, "E1429", {"start": v(17.43, 15.09) * mm, "end": v(17.44, 15.03) * mm});
            skLineSegment(sketch, "E1430", {"start": v(17.44, 15.03) * mm, "end": v(17.45, 14.98) * mm});
            skLineSegment(sketch, "E1431", {"start": v(17.45, 14.98) * mm, "end": v(17.46, 14.92) * mm});
            skLineSegment(sketch, "E1432", {"start": v(17.46, 14.92) * mm, "end": v(17.47, 14.87) * mm});
            skLineSegment(sketch, "E1433", {"start": v(17.47, 14.87) * mm, "end": v(17.48, 14.81) * mm});
            skLineSegment(sketch, "E1434", {"start": v(17.48, 14.81) * mm, "end": v(17.5, 14.76) * mm});
            skLineSegment(sketch, "E1435", {"start": v(17.5, 14.76) * mm, "end": v(17.51, 14.7) * mm});
            skLineSegment(sketch, "E1436", {"start": v(17.51, 14.7) * mm, "end": v(17.53, 14.65) * mm});
            skLineSegment(sketch, "E1437", {"start": v(17.53, 14.65) * mm, "end": v(17.55, 14.6) * mm});
            skLineSegment(sketch, "E1438", {"start": v(17.55, 14.6) * mm, "end": v(17.58, 14.55) * mm});
            skLineSegment(sketch, "E1439", {"start": v(17.58, 14.55) * mm, "end": v(17.6, 14.5) * mm});
            skLineSegment(sketch, "E1440", {"start": v(17.6, 14.5) * mm, "end": v(17.63, 14.45) * mm});
            skLineSegment(sketch, "E1441", {"start": v(17.63, 14.45) * mm, "end": v(17.66, 14.4) * mm});
            skLineSegment(sketch, "E1442", {"start": v(17.66, 14.4) * mm, "end": v(17.69, 14.36) * mm});
            skLineSegment(sketch, "E1443", {"start": v(17.69, 14.36) * mm, "end": v(17.72, 14.31) * mm});
            skLineSegment(sketch, "E1444", {"start": v(17.72, 14.31) * mm, "end": v(17.75, 14.27) * mm});
            skLineSegment(sketch, "E1445", {"start": v(17.75, 14.27) * mm, "end": v(17.78, 14.22) * mm});
            skLineSegment(sketch, "E1446", {"start": v(17.78, 14.22) * mm, "end": v(17.82, 14.18) * mm});
            skLineSegment(sketch, "E1447", {"start": v(17.82, 14.18) * mm, "end": v(17.86, 14.14) * mm});
            skLineSegment(sketch, "E1448", {"start": v(17.86, 14.14) * mm, "end": v(17.9, 14.1) * mm});
            skLineSegment(sketch, "E1449", {"start": v(17.9, 14.1) * mm, "end": v(17.94, 14.06) * mm});
            skLineSegment(sketch, "E1450", {"start": v(17.94, 14.06) * mm, "end": v(17.98, 14.02) * mm});
            skLineSegment(sketch, "E1451", {"start": v(17.98, 14.02) * mm, "end": v(18.02, 13.99) * mm});
            skLineSegment(sketch, "E1452", {"start": v(18.02, 13.99) * mm, "end": v(18.06, 13.95) * mm});
            skLineSegment(sketch, "E1453", {"start": v(18.06, 13.95) * mm, "end": v(18.1, 13.92) * mm});
            skLineSegment(sketch, "E1454", {"start": v(18.1, 13.92) * mm, "end": v(18.15, 13.89) * mm});
            skLineSegment(sketch, "E1455", {"start": v(18.15, 13.89) * mm, "end": v(18.2, 13.86) * mm});
            skLineSegment(sketch, "E1456", {"start": v(18.2, 13.86) * mm, "end": v(18.25, 13.83) * mm});
            skLineSegment(sketch, "E1457", {"start": v(18.25, 13.83) * mm, "end": v(18.3, 13.8) * mm});
            skLineSegment(sketch, "E1458", {"start": v(18.3, 13.8) * mm, "end": v(18.35, 13.78) * mm});
            skLineSegment(sketch, "E1459", {"start": v(18.35, 13.78) * mm, "end": v(18.4, 13.76) * mm});
            skLineSegment(sketch, "E1460", {"start": v(18.4, 13.76) * mm, "end": v(18.45, 13.74) * mm});
            skLineSegment(sketch, "E1461", {"start": v(18.45, 13.74) * mm, "end": v(18.5, 13.72) * mm});
            skLineSegment(sketch, "E1462", {"start": v(18.5, 13.72) * mm, "end": v(18.56, 13.7) * mm});
            skLineSegment(sketch, "E1463", {"start": v(18.56, 13.7) * mm, "end": v(18.61, 13.68) * mm});
            skLineSegment(sketch, "E1464", {"start": v(18.61, 13.68) * mm, "end": v(18.66, 13.67) * mm});
            skLineSegment(sketch, "E1465", {"start": v(18.66, 13.67) * mm, "end": v(18.72, 13.66) * mm});
            skLineSegment(sketch, "E1466", {"start": v(18.72, 13.66) * mm, "end": v(18.77, 13.65) * mm});
            skLineSegment(sketch, "E1467", {"start": v(18.77, 13.65) * mm, "end": v(18.83, 13.64) * mm});
            skLineSegment(sketch, "E1468", {"start": v(18.83, 13.64) * mm, "end": v(18.88, 13.63) * mm});
            skLineSegment(sketch, "E1469", {"start": v(18.88, 13.63) * mm, "end": v(18.94, 13.63) * mm});
            skLineSegment(sketch, "E1470", {"start": v(18.94, 13.63) * mm, "end": v(19, 13.63) * mm});
            skLineSegment(sketch, "E1471", {"start": v(19, 13.63) * mm, "end": v(19.05, 13.63) * mm});
            skLineSegment(sketch, "E1472", {"start": v(19.05, 13.63) * mm, "end": v(19.1, 13.63) * mm});
            skLineSegment(sketch, "E1473", {"start": v(19.1, 13.63) * mm, "end": v(19.16, 13.63) * mm});
            skLineSegment(sketch, "E1474", {"start": v(19.16, 13.63) * mm, "end": v(19.22, 13.64) * mm});
            skLineSegment(sketch, "E1475", {"start": v(19.22, 13.64) * mm, "end": v(19.27, 13.64) * mm});
            skLineSegment(sketch, "E1476", {"start": v(19.27, 13.64) * mm, "end": v(19.33, 13.65) * mm});
            skLineSegment(sketch, "E1477", {"start": v(19.33, 13.65) * mm, "end": v(19.38, 13.67) * mm});
            skLineSegment(sketch, "E1478", {"start": v(19.38, 13.67) * mm, "end": v(19.44, 13.68) * mm});
            skLineSegment(sketch, "E1479", {"start": v(19.44, 13.68) * mm, "end": v(19.5, 13.7) * mm});
            skLineSegment(sketch, "E1480", {"start": v(19.5, 13.7) * mm, "end": v(19.54, 13.7) * mm});
            skLineSegment(sketch, "E1481", {"start": v(19.54, 13.7) * mm, "end": v(19.6, 13.73) * mm});
            skLineSegment(sketch, "E1482", {"start": v(19.6, 13.73) * mm, "end": v(19.65, 13.75) * mm});
            skLineSegment(sketch, "E1483", {"start": v(19.65, 13.75) * mm, "end": v(19.7, 13.77) * mm});
            skLineSegment(sketch, "E1484", {"start": v(19.7, 13.77) * mm, "end": v(19.75, 13.8) * mm});
            skLineSegment(sketch, "E1485", {"start": v(19.75, 13.8) * mm, "end": v(19.8, 13.82) * mm});
            skLineSegment(sketch, "E1486", {"start": v(19.8, 13.82) * mm, "end": v(19.85, 13.85) * mm});
            skLineSegment(sketch, "E1487", {"start": v(19.85, 13.85) * mm, "end": v(19.9, 13.88) * mm});
            skLineSegment(sketch, "E1488", {"start": v(19.9, 13.88) * mm, "end": v(19.94, 13.9) * mm});
            skLineSegment(sketch, "E1489", {"start": v(19.94, 13.9) * mm, "end": v(19.99, 13.94) * mm});
            skLineSegment(sketch, "E1490", {"start": v(19.99, 13.94) * mm, "end": v(20.03, 13.97) * mm});
            skLineSegment(sketch, "E1491", {"start": v(20.03, 13.97) * mm, "end": v(20.07, 14) * mm});
            skLineSegment(sketch, "E1492", {"start": v(20.07, 14) * mm, "end": v(20.12, 14.05) * mm});
            skLineSegment(sketch, "E1493", {"start": v(20.12, 14.05) * mm, "end": v(20.16, 14.08) * mm});
            skLineSegment(sketch, "E1494", {"start": v(20.16, 14.08) * mm, "end": v(20.2, 14.12) * mm});
            skLineSegment(sketch, "E1495", {"start": v(20.2, 14.12) * mm, "end": v(20.23, 14.17) * mm});
            skLineSegment(sketch, "E1496", {"start": v(20.23, 14.17) * mm, "end": v(20.27, 14.2) * mm});
            skLineSegment(sketch, "E1497", {"start": v(20.27, 14.2) * mm, "end": v(20.3, 14.25) * mm});
            skLineSegment(sketch, "E1498", {"start": v(20.3, 14.25) * mm, "end": v(20.34, 14.3) * mm});
            skLineSegment(sketch, "E1499", {"start": v(20.34, 14.3) * mm, "end": v(20.37, 14.34) * mm});
            skLineSegment(sketch, "E1500", {"start": v(20.37, 14.34) * mm, "end": v(20.4, 14.39) * mm});
            skLineSegment(sketch, "E1501", {"start": v(20.4, 14.39) * mm, "end": v(20.43, 14.44) * mm});
            skLineSegment(sketch, "E1502", {"start": v(20.43, 14.44) * mm, "end": v(20.46, 14.48) * mm});
            skLineSegment(sketch, "E1503", {"start": v(20.46, 14.48) * mm, "end": v(20.48, 14.53) * mm});
            skLineSegment(sketch, "E1504", {"start": v(20.48, 14.53) * mm, "end": v(20.5, 14.59) * mm});
            skLineSegment(sketch, "E1505", {"start": v(20.5, 14.59) * mm, "end": v(20.53, 14.64) * mm});
            skLineSegment(sketch, "E1506", {"start": v(20.53, 14.64) * mm, "end": v(20.55, 14.69) * mm});
            skLineSegment(sketch, "E1507", {"start": v(20.55, 14.69) * mm, "end": v(20.56, 14.74) * mm});
            skLineSegment(sketch, "E1508", {"start": v(20.56, 14.74) * mm, "end": v(20.58, 14.8) * mm});
            skLineSegment(sketch, "E1509", {"start": v(20.58, 14.8) * mm, "end": v(20.6, 14.85) * mm});
            skLineSegment(sketch, "E1510", {"start": v(20.6, 14.85) * mm, "end": v(20.6, 14.9) * mm});
            skLineSegment(sketch, "E1511", {"start": v(20.6, 14.9) * mm, "end": v(20.62, 14.96) * mm});
            skLineSegment(sketch, "E1512", {"start": v(20.62, 14.96) * mm, "end": v(20.63, 15.01) * mm});
            skLineSegment(sketch, "E1513", {"start": v(20.63, 15.01) * mm, "end": v(20.63, 15.07) * mm});
            skLineSegment(sketch, "E1514", {"start": v(20.63, 15.07) * mm, "end": v(20.64, 15.12) * mm});
            skLineSegment(sketch, "E1515", {"start": v(20.64, 15.12) * mm, "end": v(20.64, 15.18) * mm});
            skLineSegment(sketch, "E1516", {"start": v(20.64, 15.18) * mm, "end": v(20.64, 15.23) * mm});
            skLineSegment(sketch, "E1517", {"start": v(20.64, 15.23) * mm, "end": v(20.64, 15.3) * mm});
            skLineSegment(sketch, "E1518", {"start": v(20.64, 15.3) * mm, "end": v(20.64, 15.35) * mm});
            skLineSegment(sketch, "E1519", {"start": v(20.64, 15.35) * mm, "end": v(20.63, 15.4) * mm});
            skLineSegment(sketch, "E1520", {"start": v(20.63, 15.4) * mm, "end": v(20.63, 15.46) * mm});
            skLineSegment(sketch, "E1521", {"start": v(20.63, 15.46) * mm, "end": v(20.62, 15.51) * mm});
            skLineSegment(sketch, "E1522", {"start": v(20.62, 15.51) * mm, "end": v(20.6, 15.57) * mm});
            skLineSegment(sketch, "E1523", {"start": v(20.6, 15.57) * mm, "end": v(20.6, 15.62) * mm});
            skLineSegment(sketch, "E1524", {"start": v(20.6, 15.62) * mm, "end": v(20.58, 15.68) * mm});
            skLineSegment(sketch, "E1525", {"start": v(20.58, 15.68) * mm, "end": v(20.56, 15.73) * mm});
            skLineSegment(sketch, "E1526", {"start": v(20.56, 15.73) * mm, "end": v(20.54, 15.78) * mm});
            skLineSegment(sketch, "E1527", {"start": v(20.54, 15.78) * mm, "end": v(20.52, 15.84) * mm});
            skLineSegment(sketch, "E1528", {"start": v(20.52, 15.84) * mm, "end": v(20.5, 15.89) * mm});
            skLineSegment(sketch, "E1529", {"start": v(20.5, 15.89) * mm, "end": v(20.48, 15.94) * mm});
            skLineSegment(sketch, "E1530", {"start": v(20.48, 15.94) * mm, "end": v(20.45, 15.99) * mm});
            skLineSegment(sketch, "E1531", {"start": v(20.45, 15.99) * mm, "end": v(20.43, 16.04) * mm});
            skLineSegment(sketch, "E1532", {"start": v(20.43, 16.04) * mm, "end": v(20.4, 16.09) * mm});
            skLineSegment(sketch, "E1533", {"start": v(20.4, 16.09) * mm, "end": v(20.37, 16.13) * mm});
            skLineSegment(sketch, "E1534", {"start": v(20.37, 16.13) * mm, "end": v(20.33, 16.18) * mm});
            skLineSegment(sketch, "E1535", {"start": v(20.33, 16.18) * mm, "end": v(20.3, 16.22) * mm});
            skLineSegment(sketch, "E1536", {"start": v(20.3, 16.22) * mm, "end": v(20.26, 16.27) * mm});
            skLineSegment(sketch, "E1537", {"start": v(20.26, 16.27) * mm, "end": v(20.23, 16.31) * mm});
            skLineSegment(sketch, "E1538", {"start": v(20.23, 16.31) * mm, "end": v(20.19, 16.35) * mm});
            skLineSegment(sketch, "E1539", {"start": v(20.19, 16.35) * mm, "end": v(20.15, 16.4) * mm});
            skLineSegment(sketch, "E1540", {"start": v(20.15, 16.4) * mm, "end": v(20.1, 16.43) * mm});
            skLineSegment(sketch, "E1541", {"start": v(20.1, 16.43) * mm, "end": v(20.07, 16.47) * mm});
            skLineSegment(sketch, "E1542", {"start": v(20.07, 16.47) * mm, "end": v(20.02, 16.5) * mm});
            skLineSegment(sketch, "E1543", {"start": v(20.02, 16.5) * mm, "end": v(19.98, 16.54) * mm});
            skLineSegment(sketch, "E1544", {"start": v(19.98, 16.54) * mm, "end": v(19.93, 16.57) * mm});
            skLineSegment(sketch, "E1545", {"start": v(19.93, 16.57) * mm, "end": v(19.88, 16.6) * mm});
            skLineSegment(sketch, "E1546", {"start": v(19.88, 16.6) * mm, "end": v(19.84, 16.63) * mm});
            skLineSegment(sketch, "E1547", {"start": v(19.84, 16.63) * mm, "end": v(19.79, 16.65) * mm});
            skLineSegment(sketch, "E1548", {"start": v(19.79, 16.65) * mm, "end": v(19.74, 16.68) * mm});
            skLineSegment(sketch, "E1549", {"start": v(19.74, 16.68) * mm, "end": v(19.69, 16.7) * mm});
            skLineSegment(sketch, "E1550", {"start": v(19.69, 16.7) * mm, "end": v(19.64, 16.73) * mm});
            skLineSegment(sketch, "E1551", {"start": v(19.64, 16.73) * mm, "end": v(19.58, 16.75) * mm});
            skLineSegment(sketch, "E1552", {"start": v(19.58, 16.75) * mm, "end": v(19.53, 16.76) * mm});
            skLineSegment(sketch, "E1553", {"start": v(19.53, 16.76) * mm, "end": v(19.48, 16.78) * mm});
            skLineSegment(sketch, "E1554", {"start": v(19.48, 16.78) * mm, "end": v(19.42, 16.8) * mm});
            skLineSegment(sketch, "E1555", {"start": v(19.42, 16.8) * mm, "end": v(19.37, 16.8) * mm});
            skLineSegment(sketch, "E1556", {"start": v(19.37, 16.8) * mm, "end": v(19.31, 16.82) * mm});
            skLineSegment(sketch, "E1557", {"start": v(19.31, 16.82) * mm, "end": v(19.26, 16.83) * mm});
            skLineSegment(sketch, "E1558", {"start": v(19.26, 16.83) * mm, "end": v(19.2, 16.83) * mm});
            skLineSegment(sketch, "E1559", {"start": v(19.2, 16.83) * mm, "end": v(19.14, 16.84) * mm});
            skLineSegment(sketch, "E1560", {"start": v(19.14, 16.84) * mm, "end": v(19.09, 16.84) * mm});
            skLineSegment(sketch, "E1561", {"start": v(19.09, 16.84) * mm, "end": v(19.03, 16.84) * mm});
            skLineSegment(sketch, "E1562", {"start": v(0.01, -50.76) * mm, "end": v(0.01, 50.76) * mm});
            skLineSegment(sketch, "E1563", {"start": v(0.01, 0) * mm, "end": v(-26.65, 0) * mm});
            skLineSegment(sketch, "E1564", {"start": v(0.01, 0) * mm, "end": v(26.65, 0) * mm});
            skSolve(sketch);
        }
        {
            var Q0;
            Q0=makeQuery(id+"F7.imprint","IMPRINT",FACE,{"disambiguationData":[TD([[makeQuery(id+"F7.imprint","IMPRINT",EDGE,{"derivedFrom":sQuery(id+"F7.wireOp",EDGE,"E449")}),-1.0]])]});
            var Q1;
            Q1=makeQuery(id+"F7.imprint","IMPRINT",FACE,{"disambiguationData":[TD([[makeQuery(id+"F7.imprint","IMPRINT",EDGE,{"derivedFrom":sQuery(id+"F7.wireOp",EDGE,"E811")}),-1.0]])]});
            var Q2;
            Q2=makeQuery(id+"F7.imprint","IMPRINT",FACE,{"disambiguationData":[TD([[makeQuery(id+"F7.imprint","IMPRINT",EDGE,{"derivedFrom":sQuery(id+"F7.wireOp",EDGE,"E1173")}),-1.0]])]});
            var Q3;
            Q3=makeQuery(id+"F7.imprint","IMPRINT",FACE,{"disambiguationData":[TD([[makeQuery(id+"F7.imprint","IMPRINT",EDGE,{"derivedFrom":sQuery(id+"F7.wireOp",EDGE,"E992")}),-1.0]])]});
            extrude(context, id + "F8", {"entities" : qUnion([Q0, Q1, Q2, Q3]), "depth" : 1 * mm, "offsetDistance" : 25 * mm});
        }
        {
            var Q0;
            {var subQ14=sQuery(id+"F1.wireOp",EDGE,"E150");Q0=makeQuery(id+"F1.imprint","IMPRINT",FACE,{"disambiguationData":[TD([[makeQuery(id+"F1.imprint","IMPRINT",EDGE,{"derivedFrom":subQ14}),1.0]])]});}
            var Q1;
            {var subQ3=sQuery(id+"F1.wireOp",EDGE,"E374");Q1=makeQuery(id+"F1.imprint","IMPRINT",FACE,{"disambiguationData":[TD([[makeQuery(id+"F1.imprint","IMPRINT",EDGE,{"derivedFrom":subQ3}),1.0]])]});}
            var Q2;
            {var subQ5=sQuery(id+"F1.wireOp",EDGE,"E368");Q2=makeQuery(id+"F1.imprint","IMPRINT",FACE,{"disambiguationData":[TD([[makeQuery(id+"F1.imprint","IMPRINT",EDGE,{"derivedFrom":subQ5}),-1.0]])]});}
            var Q3;
            {var subQ5=sQuery(id+"F1.wireOp",EDGE,"E370");Q3=makeQuery(id+"F1.imprint","IMPRINT",FACE,{"disambiguationData":[TD([[makeQuery(id+"F1.imprint","IMPRINT",EDGE,{"derivedFrom":subQ5}),-1.0]])]});}
            var Q4;
            {var subQ5=sQuery(id+"F1.wireOp",EDGE,"E372");Q4=makeQuery(id+"F1.imprint","IMPRINT",FACE,{"disambiguationData":[TD([[makeQuery(id+"F1.imprint","IMPRINT",EDGE,{"derivedFrom":subQ5}),-1.0]])]});}
            extrude(context, id + "F9", {"entities" : qUnion([Q0, Q1, Q2, Q3, Q4]), "depth" : (getVariable(context, 'mainThickness')) * mm, "offsetDistance" : 25 * mm});
        }
        {
            var Q0;
            Q0=qCreatedBy(makeId("Right.planeOp"),FACE);
            var sketch = newSketch(context, id + "F10", { "sketchPlane" : qUnion([Q0])});
            skLineSegment(sketch, "E1565", {"start": v(0, 0) * mm, "end": v(0, 22.67) * mm, "construction": true});
            skSolve(sketch);
        }
        {
            var Q0;
            Q0=makeQuery(id+"F8.opExtrude","SWEPT_BODY",BODY,{"disambiguationData":[OSD([sQuery(id+"F7.wireOp",EDGE,"E449"),sQuery(id+"F7.wireOp",EDGE,"E450"),sQuery(id+"F7.wireOp",EDGE,"E451"),sQuery(id+"F7.wireOp",EDGE,"E452"),sQuery(id+"F7.wireOp",EDGE,"E453"),sQuery(id+"F7.wireOp",EDGE,"E454"),sQuery(id+"F7.wireOp",EDGE,"E455"),sQuery(id+"F7.wireOp",EDGE,"E456"),sQuery(id+"F7.wireOp",EDGE,"E457"),sQuery(id+"F7.wireOp",EDGE,"E458"),sQuery(id+"F7.wireOp",EDGE,"E459"),sQuery(id+"F7.wireOp",EDGE,"E460"),sQuery(id+"F7.wireOp",EDGE,"E461"),sQuery(id+"F7.wireOp",EDGE,"E462"),sQuery(id+"F7.wireOp",EDGE,"E463"),sQuery(id+"F7.wireOp",EDGE,"E464"),sQuery(id+"F7.wireOp",EDGE,"E465"),sQuery(id+"F7.wireOp",EDGE,"E466"),sQuery(id+"F7.wireOp",EDGE,"E467"),sQuery(id+"F7.wireOp",EDGE,"E468"),sQuery(id+"F7.wireOp",EDGE,"E469"),sQuery(id+"F7.wireOp",EDGE,"E470"),sQuery(id+"F7.wireOp",EDGE,"E471"),sQuery(id+"F7.wireOp",EDGE,"E472"),sQuery(id+"F7.wireOp",EDGE,"E473"),sQuery(id+"F7.wireOp",EDGE,"E474"),sQuery(id+"F7.wireOp",EDGE,"E475"),sQuery(id+"F7.wireOp",EDGE,"E476"),sQuery(id+"F7.wireOp",EDGE,"E477"),sQuery(id+"F7.wireOp",EDGE,"E478"),sQuery(id+"F7.wireOp",EDGE,"E479"),sQuery(id+"F7.wireOp",EDGE,"E480"),sQuery(id+"F7.wireOp",EDGE,"E481"),sQuery(id+"F7.wireOp",EDGE,"E482"),sQuery(id+"F7.wireOp",EDGE,"E483"),sQuery(id+"F7.wireOp",EDGE,"E484"),sQuery(id+"F7.wireOp",EDGE,"E485"),sQuery(id+"F7.wireOp",EDGE,"E486"),sQuery(id+"F7.wireOp",EDGE,"E487"),sQuery(id+"F7.wireOp",EDGE,"E488"),sQuery(id+"F7.wireOp",EDGE,"E489"),sQuery(id+"F7.wireOp",EDGE,"E490"),sQuery(id+"F7.wireOp",EDGE,"E491"),sQuery(id+"F7.wireOp",EDGE,"E492"),sQuery(id+"F7.wireOp",EDGE,"E493"),sQuery(id+"F7.wireOp",EDGE,"E494"),sQuery(id+"F7.wireOp",EDGE,"E495"),sQuery(id+"F7.wireOp",EDGE,"E496"),sQuery(id+"F7.wireOp",EDGE,"E497"),sQuery(id+"F7.wireOp",EDGE,"E498"),sQuery(id+"F7.wireOp",EDGE,"E499"),sQuery(id+"F7.wireOp",EDGE,"E500"),sQuery(id+"F7.wireOp",EDGE,"E501"),sQuery(id+"F7.wireOp",EDGE,"E502"),sQuery(id+"F7.wireOp",EDGE,"E503"),sQuery(id+"F7.wireOp",EDGE,"E504"),sQuery(id+"F7.wireOp",EDGE,"E505"),sQuery(id+"F7.wireOp",EDGE,"E506"),sQuery(id+"F7.wireOp",EDGE,"E507"),sQuery(id+"F7.wireOp",EDGE,"E508"),sQuery(id+"F7.wireOp",EDGE,"E509"),sQuery(id+"F7.wireOp",EDGE,"E510"),sQuery(id+"F7.wireOp",EDGE,"E511"),sQuery(id+"F7.wireOp",EDGE,"E512"),sQuery(id+"F7.wireOp",EDGE,"E513"),sQuery(id+"F7.wireOp",EDGE,"E514"),sQuery(id+"F7.wireOp",EDGE,"E515"),sQuery(id+"F7.wireOp",EDGE,"E516"),sQuery(id+"F7.wireOp",EDGE,"E517"),sQuery(id+"F7.wireOp",EDGE,"E518"),sQuery(id+"F7.wireOp",EDGE,"E519"),sQuery(id+"F7.wireOp",EDGE,"E520"),sQuery(id+"F7.wireOp",EDGE,"E521"),sQuery(id+"F7.wireOp",EDGE,"E522"),sQuery(id+"F7.wireOp",EDGE,"E523"),sQuery(id+"F7.wireOp",EDGE,"E524"),sQuery(id+"F7.wireOp",EDGE,"E525"),sQuery(id+"F7.wireOp",EDGE,"E526"),sQuery(id+"F7.wireOp",EDGE,"E527"),sQuery(id+"F7.wireOp",EDGE,"E528"),sQuery(id+"F7.wireOp",EDGE,"E529"),sQuery(id+"F7.wireOp",EDGE,"E530"),sQuery(id+"F7.wireOp",EDGE,"E531"),sQuery(id+"F7.wireOp",EDGE,"E532"),sQuery(id+"F7.wireOp",EDGE,"E533"),sQuery(id+"F7.wireOp",EDGE,"E534"),sQuery(id+"F7.wireOp",EDGE,"E535"),sQuery(id+"F7.wireOp",EDGE,"E536"),sQuery(id+"F7.wireOp",EDGE,"E537"),sQuery(id+"F7.wireOp",EDGE,"E538"),sQuery(id+"F7.wireOp",EDGE,"E539"),sQuery(id+"F7.wireOp",EDGE,"E540"),sQuery(id+"F7.wireOp",EDGE,"E541"),sQuery(id+"F7.wireOp",EDGE,"E542"),sQuery(id+"F7.wireOp",EDGE,"E543"),sQuery(id+"F7.wireOp",EDGE,"E544"),sQuery(id+"F7.wireOp",EDGE,"E545"),sQuery(id+"F7.wireOp",EDGE,"E546"),sQuery(id+"F7.wireOp",EDGE,"E547"),sQuery(id+"F7.wireOp",EDGE,"E548"),sQuery(id+"F7.wireOp",EDGE,"E549"),sQuery(id+"F7.wireOp",EDGE,"E550"),sQuery(id+"F7.wireOp",EDGE,"E551"),sQuery(id+"F7.wireOp",EDGE,"E552"),sQuery(id+"F7.wireOp",EDGE,"E553"),sQuery(id+"F7.wireOp",EDGE,"E554"),sQuery(id+"F7.wireOp",EDGE,"E555"),sQuery(id+"F7.wireOp",EDGE,"E556"),sQuery(id+"F7.wireOp",EDGE,"E557"),sQuery(id+"F7.wireOp",EDGE,"E558"),sQuery(id+"F7.wireOp",EDGE,"E559"),sQuery(id+"F7.wireOp",EDGE,"E560"),sQuery(id+"F7.wireOp",EDGE,"E561"),sQuery(id+"F7.wireOp",EDGE,"E562"),sQuery(id+"F7.wireOp",EDGE,"E563"),sQuery(id+"F7.wireOp",EDGE,"E564"),sQuery(id+"F7.wireOp",EDGE,"E565"),sQuery(id+"F7.wireOp",EDGE,"E566"),sQuery(id+"F7.wireOp",EDGE,"E567"),sQuery(id+"F7.wireOp",EDGE,"E568"),sQuery(id+"F7.wireOp",EDGE,"E569"),sQuery(id+"F7.wireOp",EDGE,"E570"),sQuery(id+"F7.wireOp",EDGE,"E571"),sQuery(id+"F7.wireOp",EDGE,"E572"),sQuery(id+"F7.wireOp",EDGE,"E573"),sQuery(id+"F7.wireOp",EDGE,"E574"),sQuery(id+"F7.wireOp",EDGE,"E575"),sQuery(id+"F7.wireOp",EDGE,"E576"),sQuery(id+"F7.wireOp",EDGE,"E577"),sQuery(id+"F7.wireOp",EDGE,"E578"),sQuery(id+"F7.wireOp",EDGE,"E579"),sQuery(id+"F7.wireOp",EDGE,"E580"),sQuery(id+"F7.wireOp",EDGE,"E581"),sQuery(id+"F7.wireOp",EDGE,"E582"),sQuery(id+"F7.wireOp",EDGE,"E583"),sQuery(id+"F7.wireOp",EDGE,"E584"),sQuery(id+"F7.wireOp",EDGE,"E585"),sQuery(id+"F7.wireOp",EDGE,"E586"),sQuery(id+"F7.wireOp",EDGE,"E587"),sQuery(id+"F7.wireOp",EDGE,"E588"),sQuery(id+"F7.wireOp",EDGE,"E589"),sQuery(id+"F7.wireOp",EDGE,"E590"),sQuery(id+"F7.wireOp",EDGE,"E591"),sQuery(id+"F7.wireOp",EDGE,"E592"),sQuery(id+"F7.wireOp",EDGE,"E593"),sQuery(id+"F7.wireOp",EDGE,"E594"),sQuery(id+"F7.wireOp",EDGE,"E595"),sQuery(id+"F7.wireOp",EDGE,"E596"),sQuery(id+"F7.wireOp",EDGE,"E597"),sQuery(id+"F7.wireOp",EDGE,"E598"),sQuery(id+"F7.wireOp",EDGE,"E599"),sQuery(id+"F7.wireOp",EDGE,"E600"),sQuery(id+"F7.wireOp",EDGE,"E601"),sQuery(id+"F7.wireOp",EDGE,"E602"),sQuery(id+"F7.wireOp",EDGE,"E603"),sQuery(id+"F7.wireOp",EDGE,"E604"),sQuery(id+"F7.wireOp",EDGE,"E605"),sQuery(id+"F7.wireOp",EDGE,"E606"),sQuery(id+"F7.wireOp",EDGE,"E607"),sQuery(id+"F7.wireOp",EDGE,"E608"),sQuery(id+"F7.wireOp",EDGE,"E609"),sQuery(id+"F7.wireOp",EDGE,"E610"),sQuery(id+"F7.wireOp",EDGE,"E611"),sQuery(id+"F7.wireOp",EDGE,"E612"),sQuery(id+"F7.wireOp",EDGE,"E613"),sQuery(id+"F7.wireOp",EDGE,"E614"),sQuery(id+"F7.wireOp",EDGE,"E615"),sQuery(id+"F7.wireOp",EDGE,"E616"),sQuery(id+"F7.wireOp",EDGE,"E617"),sQuery(id+"F7.wireOp",EDGE,"E618"),sQuery(id+"F7.wireOp",EDGE,"E619"),sQuery(id+"F7.wireOp",EDGE,"E620"),sQuery(id+"F7.wireOp",EDGE,"E621"),sQuery(id+"F7.wireOp",EDGE,"E622"),sQuery(id+"F7.wireOp",EDGE,"E623"),sQuery(id+"F7.wireOp",EDGE,"E624"),sQuery(id+"F7.wireOp",EDGE,"E625"),sQuery(id+"F7.wireOp",EDGE,"E626"),sQuery(id+"F7.wireOp",EDGE,"E627"),sQuery(id+"F7.wireOp",EDGE,"E628"),sQuery(id+"F7.wireOp",EDGE,"E629"),sQuery(id+"F7.wireOp",EDGE,"E630"),sQuery(id+"F7.wireOp",EDGE,"E631"),sQuery(id+"F7.wireOp",EDGE,"E632"),sQuery(id+"F7.wireOp",EDGE,"E633"),sQuery(id+"F7.wireOp",EDGE,"E634"),sQuery(id+"F7.wireOp",EDGE,"E635"),sQuery(id+"F7.wireOp",EDGE,"E636"),sQuery(id+"F7.wireOp",EDGE,"E637"),sQuery(id+"F7.wireOp",EDGE,"E638"),sQuery(id+"F7.wireOp",EDGE,"E639"),sQuery(id+"F7.wireOp",EDGE,"E640"),sQuery(id+"F7.wireOp",EDGE,"E641"),sQuery(id+"F7.wireOp",EDGE,"E642"),sQuery(id+"F7.wireOp",EDGE,"E643"),sQuery(id+"F7.wireOp",EDGE,"E644"),sQuery(id+"F7.wireOp",EDGE,"E645"),sQuery(id+"F7.wireOp",EDGE,"E646"),sQuery(id+"F7.wireOp",EDGE,"E647"),sQuery(id+"F7.wireOp",EDGE,"E648"),sQuery(id+"F7.wireOp",EDGE,"E649"),sQuery(id+"F7.wireOp",EDGE,"E650"),sQuery(id+"F7.wireOp",EDGE,"E651"),sQuery(id+"F7.wireOp",EDGE,"E652"),sQuery(id+"F7.wireOp",EDGE,"E653"),sQuery(id+"F7.wireOp",EDGE,"E654"),sQuery(id+"F7.wireOp",EDGE,"E655"),sQuery(id+"F7.wireOp",EDGE,"E656"),sQuery(id+"F7.wireOp",EDGE,"E657"),sQuery(id+"F7.wireOp",EDGE,"E658"),sQuery(id+"F7.wireOp",EDGE,"E659"),sQuery(id+"F7.wireOp",EDGE,"E660"),sQuery(id+"F7.wireOp",EDGE,"E661"),sQuery(id+"F7.wireOp",EDGE,"E662"),sQuery(id+"F7.wireOp",EDGE,"E663"),sQuery(id+"F7.wireOp",EDGE,"E664"),sQuery(id+"F7.wireOp",EDGE,"E665"),sQuery(id+"F7.wireOp",EDGE,"E666"),sQuery(id+"F7.wireOp",EDGE,"E667"),sQuery(id+"F7.wireOp",EDGE,"E668"),sQuery(id+"F7.wireOp",EDGE,"E669"),sQuery(id+"F7.wireOp",EDGE,"E670"),sQuery(id+"F7.wireOp",EDGE,"E671"),sQuery(id+"F7.wireOp",EDGE,"E672"),sQuery(id+"F7.wireOp",EDGE,"E673"),sQuery(id+"F7.wireOp",EDGE,"E674"),sQuery(id+"F7.wireOp",EDGE,"E675"),sQuery(id+"F7.wireOp",EDGE,"E676"),sQuery(id+"F7.wireOp",EDGE,"E677"),sQuery(id+"F7.wireOp",EDGE,"E678"),sQuery(id+"F7.wireOp",EDGE,"E679"),sQuery(id+"F7.wireOp",EDGE,"E680"),sQuery(id+"F7.wireOp",EDGE,"E681"),sQuery(id+"F7.wireOp",EDGE,"E682"),sQuery(id+"F7.wireOp",EDGE,"E683"),sQuery(id+"F7.wireOp",EDGE,"E684"),sQuery(id+"F7.wireOp",EDGE,"E685"),sQuery(id+"F7.wireOp",EDGE,"E686"),sQuery(id+"F7.wireOp",EDGE,"E687"),sQuery(id+"F7.wireOp",EDGE,"E688"),sQuery(id+"F7.wireOp",EDGE,"E689"),sQuery(id+"F7.wireOp",EDGE,"E690"),sQuery(id+"F7.wireOp",EDGE,"E691"),sQuery(id+"F7.wireOp",EDGE,"E692"),sQuery(id+"F7.wireOp",EDGE,"E693"),sQuery(id+"F7.wireOp",EDGE,"E694"),sQuery(id+"F7.wireOp",EDGE,"E695"),sQuery(id+"F7.wireOp",EDGE,"E696"),sQuery(id+"F7.wireOp",EDGE,"E697"),sQuery(id+"F7.wireOp",EDGE,"E698"),sQuery(id+"F7.wireOp",EDGE,"E699"),sQuery(id+"F7.wireOp",EDGE,"E700"),sQuery(id+"F7.wireOp",EDGE,"E701"),sQuery(id+"F7.wireOp",EDGE,"E702"),sQuery(id+"F7.wireOp",EDGE,"E703"),sQuery(id+"F7.wireOp",EDGE,"E704"),sQuery(id+"F7.wireOp",EDGE,"E705"),sQuery(id+"F7.wireOp",EDGE,"E706"),sQuery(id+"F7.wireOp",EDGE,"E707"),sQuery(id+"F7.wireOp",EDGE,"E708"),sQuery(id+"F7.wireOp",EDGE,"E709"),sQuery(id+"F7.wireOp",EDGE,"E710"),sQuery(id+"F7.wireOp",EDGE,"E711"),sQuery(id+"F7.wireOp",EDGE,"E712"),sQuery(id+"F7.wireOp",EDGE,"E713"),sQuery(id+"F7.wireOp",EDGE,"E714"),sQuery(id+"F7.wireOp",EDGE,"E715"),sQuery(id+"F7.wireOp",EDGE,"E716"),sQuery(id+"F7.wireOp",EDGE,"E717"),sQuery(id+"F7.wireOp",EDGE,"E718"),sQuery(id+"F7.wireOp",EDGE,"E719"),sQuery(id+"F7.wireOp",EDGE,"E720"),sQuery(id+"F7.wireOp",EDGE,"E721"),sQuery(id+"F7.wireOp",EDGE,"E722"),sQuery(id+"F7.wireOp",EDGE,"E723"),sQuery(id+"F7.wireOp",EDGE,"E724"),sQuery(id+"F7.wireOp",EDGE,"E725"),sQuery(id+"F7.wireOp",EDGE,"E726"),sQuery(id+"F7.wireOp",EDGE,"E727"),sQuery(id+"F7.wireOp",EDGE,"E728"),sQuery(id+"F7.wireOp",EDGE,"E729"),sQuery(id+"F7.wireOp",EDGE,"E730"),sQuery(id+"F7.wireOp",EDGE,"E731"),sQuery(id+"F7.wireOp",EDGE,"E732"),sQuery(id+"F7.wireOp",EDGE,"E733"),sQuery(id+"F7.wireOp",EDGE,"E734"),sQuery(id+"F7.wireOp",EDGE,"E735"),sQuery(id+"F7.wireOp",EDGE,"E736"),sQuery(id+"F7.wireOp",EDGE,"E737"),sQuery(id+"F7.wireOp",EDGE,"E738"),sQuery(id+"F7.wireOp",EDGE,"E739"),sQuery(id+"F7.wireOp",EDGE,"E740"),sQuery(id+"F7.wireOp",EDGE,"E741"),sQuery(id+"F7.wireOp",EDGE,"E742"),sQuery(id+"F7.wireOp",EDGE,"E743"),sQuery(id+"F7.wireOp",EDGE,"E744"),sQuery(id+"F7.wireOp",EDGE,"E745"),sQuery(id+"F7.wireOp",EDGE,"E746"),sQuery(id+"F7.wireOp",EDGE,"E747"),sQuery(id+"F7.wireOp",EDGE,"E748"),sQuery(id+"F7.wireOp",EDGE,"E749"),sQuery(id+"F7.wireOp",EDGE,"E750"),sQuery(id+"F7.wireOp",EDGE,"E751"),sQuery(id+"F7.wireOp",EDGE,"E752"),sQuery(id+"F7.wireOp",EDGE,"E753"),sQuery(id+"F7.wireOp",EDGE,"E754"),sQuery(id+"F7.wireOp",EDGE,"E755"),sQuery(id+"F7.wireOp",EDGE,"E756"),sQuery(id+"F7.wireOp",EDGE,"E757"),sQuery(id+"F7.wireOp",EDGE,"E758"),sQuery(id+"F7.wireOp",EDGE,"E759"),sQuery(id+"F7.wireOp",EDGE,"E760"),sQuery(id+"F7.wireOp",EDGE,"E761"),sQuery(id+"F7.wireOp",EDGE,"E762"),sQuery(id+"F7.wireOp",EDGE,"E763"),sQuery(id+"F7.wireOp",EDGE,"E764"),sQuery(id+"F7.wireOp",EDGE,"E765"),sQuery(id+"F7.wireOp",EDGE,"E766"),sQuery(id+"F7.wireOp",EDGE,"E767"),sQuery(id+"F7.wireOp",EDGE,"E768"),sQuery(id+"F7.wireOp",EDGE,"E769"),sQuery(id+"F7.wireOp",EDGE,"E770"),sQuery(id+"F7.wireOp",EDGE,"E771"),sQuery(id+"F7.wireOp",EDGE,"E772"),sQuery(id+"F7.wireOp",EDGE,"E773"),sQuery(id+"F7.wireOp",EDGE,"E774"),sQuery(id+"F7.wireOp",EDGE,"E775"),sQuery(id+"F7.wireOp",EDGE,"E776"),sQuery(id+"F7.wireOp",EDGE,"E777"),sQuery(id+"F7.wireOp",EDGE,"E778"),sQuery(id+"F7.wireOp",EDGE,"E779"),sQuery(id+"F7.wireOp",EDGE,"E780"),sQuery(id+"F7.wireOp",EDGE,"E781"),sQuery(id+"F7.wireOp",EDGE,"E782"),sQuery(id+"F7.wireOp",EDGE,"E783"),sQuery(id+"F7.wireOp",EDGE,"E784"),sQuery(id+"F7.wireOp",EDGE,"E785"),sQuery(id+"F7.wireOp",EDGE,"E786"),sQuery(id+"F7.wireOp",EDGE,"E787"),sQuery(id+"F7.wireOp",EDGE,"E788"),sQuery(id+"F7.wireOp",EDGE,"E789"),sQuery(id+"F7.wireOp",EDGE,"E790"),sQuery(id+"F7.wireOp",EDGE,"E791"),sQuery(id+"F7.wireOp",EDGE,"E792"),sQuery(id+"F7.wireOp",EDGE,"E793"),sQuery(id+"F7.wireOp",EDGE,"E794"),sQuery(id+"F7.wireOp",EDGE,"E795"),sQuery(id+"F7.wireOp",EDGE,"E796"),sQuery(id+"F7.wireOp",EDGE,"E797"),sQuery(id+"F7.wireOp",EDGE,"E798"),sQuery(id+"F7.wireOp",EDGE,"E799"),sQuery(id+"F7.wireOp",EDGE,"E800"),sQuery(id+"F7.wireOp",EDGE,"E801"),sQuery(id+"F7.wireOp",EDGE,"E802"),sQuery(id+"F7.wireOp",EDGE,"E803"),sQuery(id+"F7.wireOp",EDGE,"E804"),sQuery(id+"F7.wireOp",EDGE,"E805"),sQuery(id+"F7.wireOp",EDGE,"E806"),sQuery(id+"F7.wireOp",EDGE,"E807"),sQuery(id+"F7.wireOp",EDGE,"E808"),sQuery(id+"F7.wireOp",EDGE,"E809"),sQuery(id+"F7.wireOp",EDGE,"E810"),sQuery(id+"F7.wireOp",EDGE,"E811"),sQuery(id+"F7.wireOp",EDGE,"E812"),sQuery(id+"F7.wireOp",EDGE,"E813"),sQuery(id+"F7.wireOp",EDGE,"E814"),sQuery(id+"F7.wireOp",EDGE,"E815"),sQuery(id+"F7.wireOp",EDGE,"E816"),sQuery(id+"F7.wireOp",EDGE,"E817"),sQuery(id+"F7.wireOp",EDGE,"E818"),sQuery(id+"F7.wireOp",EDGE,"E819"),sQuery(id+"F7.wireOp",EDGE,"E820"),sQuery(id+"F7.wireOp",EDGE,"E821"),sQuery(id+"F7.wireOp",EDGE,"E822"),sQuery(id+"F7.wireOp",EDGE,"E823"),sQuery(id+"F7.wireOp",EDGE,"E824"),sQuery(id+"F7.wireOp",EDGE,"E825"),sQuery(id+"F7.wireOp",EDGE,"E826"),sQuery(id+"F7.wireOp",EDGE,"E827"),sQuery(id+"F7.wireOp",EDGE,"E828"),sQuery(id+"F7.wireOp",EDGE,"E829"),sQuery(id+"F7.wireOp",EDGE,"E830"),sQuery(id+"F7.wireOp",EDGE,"E831"),sQuery(id+"F7.wireOp",EDGE,"E832"),sQuery(id+"F7.wireOp",EDGE,"E833"),sQuery(id+"F7.wireOp",EDGE,"E834"),sQuery(id+"F7.wireOp",EDGE,"E835"),sQuery(id+"F7.wireOp",EDGE,"E836"),sQuery(id+"F7.wireOp",EDGE,"E837"),sQuery(id+"F7.wireOp",EDGE,"E838"),sQuery(id+"F7.wireOp",EDGE,"E839"),sQuery(id+"F7.wireOp",EDGE,"E840"),sQuery(id+"F7.wireOp",EDGE,"E841"),sQuery(id+"F7.wireOp",EDGE,"E842"),sQuery(id+"F7.wireOp",EDGE,"E843"),sQuery(id+"F7.wireOp",EDGE,"E844"),sQuery(id+"F7.wireOp",EDGE,"E845"),sQuery(id+"F7.wireOp",EDGE,"E846"),sQuery(id+"F7.wireOp",EDGE,"E847"),sQuery(id+"F7.wireOp",EDGE,"E848"),sQuery(id+"F7.wireOp",EDGE,"E849"),sQuery(id+"F7.wireOp",EDGE,"E850"),sQuery(id+"F7.wireOp",EDGE,"E851"),sQuery(id+"F7.wireOp",EDGE,"E852"),sQuery(id+"F7.wireOp",EDGE,"E853"),sQuery(id+"F7.wireOp",EDGE,"E854"),sQuery(id+"F7.wireOp",EDGE,"E855"),sQuery(id+"F7.wireOp",EDGE,"E856"),sQuery(id+"F7.wireOp",EDGE,"E857"),sQuery(id+"F7.wireOp",EDGE,"E858"),sQuery(id+"F7.wireOp",EDGE,"E859"),sQuery(id+"F7.wireOp",EDGE,"E860"),sQuery(id+"F7.wireOp",EDGE,"E861"),sQuery(id+"F7.wireOp",EDGE,"E862"),sQuery(id+"F7.wireOp",EDGE,"E863"),sQuery(id+"F7.wireOp",EDGE,"E864"),sQuery(id+"F7.wireOp",EDGE,"E865"),sQuery(id+"F7.wireOp",EDGE,"E866"),sQuery(id+"F7.wireOp",EDGE,"E867"),sQuery(id+"F7.wireOp",EDGE,"E868"),sQuery(id+"F7.wireOp",EDGE,"E869"),sQuery(id+"F7.wireOp",EDGE,"E870"),sQuery(id+"F7.wireOp",EDGE,"E871"),sQuery(id+"F7.wireOp",EDGE,"E872"),sQuery(id+"F7.wireOp",EDGE,"E873"),sQuery(id+"F7.wireOp",EDGE,"E874"),sQuery(id+"F7.wireOp",EDGE,"E875"),sQuery(id+"F7.wireOp",EDGE,"E876"),sQuery(id+"F7.wireOp",EDGE,"E877"),sQuery(id+"F7.wireOp",EDGE,"E878"),sQuery(id+"F7.wireOp",EDGE,"E879"),sQuery(id+"F7.wireOp",EDGE,"E880"),sQuery(id+"F7.wireOp",EDGE,"E881"),sQuery(id+"F7.wireOp",EDGE,"E882"),sQuery(id+"F7.wireOp",EDGE,"E883"),sQuery(id+"F7.wireOp",EDGE,"E884"),sQuery(id+"F7.wireOp",EDGE,"E885"),sQuery(id+"F7.wireOp",EDGE,"E886"),sQuery(id+"F7.wireOp",EDGE,"E887"),sQuery(id+"F7.wireOp",EDGE,"E888"),sQuery(id+"F7.wireOp",EDGE,"E889"),sQuery(id+"F7.wireOp",EDGE,"E890"),sQuery(id+"F7.wireOp",EDGE,"E891"),sQuery(id+"F7.wireOp",EDGE,"E892"),sQuery(id+"F7.wireOp",EDGE,"E893"),sQuery(id+"F7.wireOp",EDGE,"E894"),sQuery(id+"F7.wireOp",EDGE,"E895"),sQuery(id+"F7.wireOp",EDGE,"E896"),sQuery(id+"F7.wireOp",EDGE,"E897"),sQuery(id+"F7.wireOp",EDGE,"E898"),sQuery(id+"F7.wireOp",EDGE,"E899"),sQuery(id+"F7.wireOp",EDGE,"E900"),sQuery(id+"F7.wireOp",EDGE,"E901"),sQuery(id+"F7.wireOp",EDGE,"E902"),sQuery(id+"F7.wireOp",EDGE,"E903"),sQuery(id+"F7.wireOp",EDGE,"E904"),sQuery(id+"F7.wireOp",EDGE,"E905"),sQuery(id+"F7.wireOp",EDGE,"E906"),sQuery(id+"F7.wireOp",EDGE,"E907"),sQuery(id+"F7.wireOp",EDGE,"E908"),sQuery(id+"F7.wireOp",EDGE,"E909"),sQuery(id+"F7.wireOp",EDGE,"E910"),sQuery(id+"F7.wireOp",EDGE,"E911"),sQuery(id+"F7.wireOp",EDGE,"E912"),sQuery(id+"F7.wireOp",EDGE,"E913"),sQuery(id+"F7.wireOp",EDGE,"E914"),sQuery(id+"F7.wireOp",EDGE,"E915"),sQuery(id+"F7.wireOp",EDGE,"E916"),sQuery(id+"F7.wireOp",EDGE,"E917"),sQuery(id+"F7.wireOp",EDGE,"E918"),sQuery(id+"F7.wireOp",EDGE,"E919"),sQuery(id+"F7.wireOp",EDGE,"E920"),sQuery(id+"F7.wireOp",EDGE,"E921"),sQuery(id+"F7.wireOp",EDGE,"E922"),sQuery(id+"F7.wireOp",EDGE,"E923"),sQuery(id+"F7.wireOp",EDGE,"E924"),sQuery(id+"F7.wireOp",EDGE,"E925"),sQuery(id+"F7.wireOp",EDGE,"E926"),sQuery(id+"F7.wireOp",EDGE,"E927"),sQuery(id+"F7.wireOp",EDGE,"E928"),sQuery(id+"F7.wireOp",EDGE,"E929"),sQuery(id+"F7.wireOp",EDGE,"E930"),sQuery(id+"F7.wireOp",EDGE,"E931"),sQuery(id+"F7.wireOp",EDGE,"E932"),sQuery(id+"F7.wireOp",EDGE,"E933"),sQuery(id+"F7.wireOp",EDGE,"E934"),sQuery(id+"F7.wireOp",EDGE,"E935"),sQuery(id+"F7.wireOp",EDGE,"E936"),sQuery(id+"F7.wireOp",EDGE,"E937"),sQuery(id+"F7.wireOp",EDGE,"E938"),sQuery(id+"F7.wireOp",EDGE,"E939"),sQuery(id+"F7.wireOp",EDGE,"E940"),sQuery(id+"F7.wireOp",EDGE,"E941"),sQuery(id+"F7.wireOp",EDGE,"E942"),sQuery(id+"F7.wireOp",EDGE,"E943"),sQuery(id+"F7.wireOp",EDGE,"E944"),sQuery(id+"F7.wireOp",EDGE,"E945"),sQuery(id+"F7.wireOp",EDGE,"E946"),sQuery(id+"F7.wireOp",EDGE,"E947"),sQuery(id+"F7.wireOp",EDGE,"E948"),sQuery(id+"F7.wireOp",EDGE,"E949"),sQuery(id+"F7.wireOp",EDGE,"E950"),sQuery(id+"F7.wireOp",EDGE,"E951"),sQuery(id+"F7.wireOp",EDGE,"E952"),sQuery(id+"F7.wireOp",EDGE,"E953"),sQuery(id+"F7.wireOp",EDGE,"E954"),sQuery(id+"F7.wireOp",EDGE,"E955"),sQuery(id+"F7.wireOp",EDGE,"E956"),sQuery(id+"F7.wireOp",EDGE,"E957"),sQuery(id+"F7.wireOp",EDGE,"E958"),sQuery(id+"F7.wireOp",EDGE,"E959"),sQuery(id+"F7.wireOp",EDGE,"E960"),sQuery(id+"F7.wireOp",EDGE,"E961"),sQuery(id+"F7.wireOp",EDGE,"E962"),sQuery(id+"F7.wireOp",EDGE,"E963"),sQuery(id+"F7.wireOp",EDGE,"E964"),sQuery(id+"F7.wireOp",EDGE,"E965"),sQuery(id+"F7.wireOp",EDGE,"E966"),sQuery(id+"F7.wireOp",EDGE,"E967"),sQuery(id+"F7.wireOp",EDGE,"E968"),sQuery(id+"F7.wireOp",EDGE,"E969"),sQuery(id+"F7.wireOp",EDGE,"E970"),sQuery(id+"F7.wireOp",EDGE,"E971"),sQuery(id+"F7.wireOp",EDGE,"E972"),sQuery(id+"F7.wireOp",EDGE,"E973"),sQuery(id+"F7.wireOp",EDGE,"E974"),sQuery(id+"F7.wireOp",EDGE,"E975"),sQuery(id+"F7.wireOp",EDGE,"E976"),sQuery(id+"F7.wireOp",EDGE,"E977"),sQuery(id+"F7.wireOp",EDGE,"E978"),sQuery(id+"F7.wireOp",EDGE,"E979"),sQuery(id+"F7.wireOp",EDGE,"E980"),sQuery(id+"F7.wireOp",EDGE,"E981"),sQuery(id+"F7.wireOp",EDGE,"E982"),sQuery(id+"F7.wireOp",EDGE,"E983"),sQuery(id+"F7.wireOp",EDGE,"E984"),sQuery(id+"F7.wireOp",EDGE,"E985"),sQuery(id+"F7.wireOp",EDGE,"E986"),sQuery(id+"F7.wireOp",EDGE,"E987"),sQuery(id+"F7.wireOp",EDGE,"E988"),sQuery(id+"F7.wireOp",EDGE,"E989"),sQuery(id+"F7.wireOp",EDGE,"E990"),sQuery(id+"F7.wireOp",EDGE,"E991"),sQuery(id+"F7.wireOp",EDGE,"E992"),sQuery(id+"F7.wireOp",EDGE,"E993"),sQuery(id+"F7.wireOp",EDGE,"E994"),sQuery(id+"F7.wireOp",EDGE,"E995"),sQuery(id+"F7.wireOp",EDGE,"E996"),sQuery(id+"F7.wireOp",EDGE,"E997"),sQuery(id+"F7.wireOp",EDGE,"E998"),sQuery(id+"F7.wireOp",EDGE,"E999"),sQuery(id+"F7.wireOp",EDGE,"E1000"),sQuery(id+"F7.wireOp",EDGE,"E1001"),sQuery(id+"F7.wireOp",EDGE,"E1002"),sQuery(id+"F7.wireOp",EDGE,"E1003"),sQuery(id+"F7.wireOp",EDGE,"E1004"),sQuery(id+"F7.wireOp",EDGE,"E1005"),sQuery(id+"F7.wireOp",EDGE,"E1006"),sQuery(id+"F7.wireOp",EDGE,"E1007"),sQuery(id+"F7.wireOp",EDGE,"E1008"),sQuery(id+"F7.wireOp",EDGE,"E1009"),sQuery(id+"F7.wireOp",EDGE,"E1010"),sQuery(id+"F7.wireOp",EDGE,"E1011"),sQuery(id+"F7.wireOp",EDGE,"E1012"),sQuery(id+"F7.wireOp",EDGE,"E1013"),sQuery(id+"F7.wireOp",EDGE,"E1014"),sQuery(id+"F7.wireOp",EDGE,"E1015"),sQuery(id+"F7.wireOp",EDGE,"E1016"),sQuery(id+"F7.wireOp",EDGE,"E1017"),sQuery(id+"F7.wireOp",EDGE,"E1018"),sQuery(id+"F7.wireOp",EDGE,"E1019"),sQuery(id+"F7.wireOp",EDGE,"E1020"),sQuery(id+"F7.wireOp",EDGE,"E1021"),sQuery(id+"F7.wireOp",EDGE,"E1022"),sQuery(id+"F7.wireOp",EDGE,"E1023"),sQuery(id+"F7.wireOp",EDGE,"E1024"),sQuery(id+"F7.wireOp",EDGE,"E1025"),sQuery(id+"F7.wireOp",EDGE,"E1026"),sQuery(id+"F7.wireOp",EDGE,"E1027"),sQuery(id+"F7.wireOp",EDGE,"E1028"),sQuery(id+"F7.wireOp",EDGE,"E1029"),sQuery(id+"F7.wireOp",EDGE,"E1030"),sQuery(id+"F7.wireOp",EDGE,"E1031"),sQuery(id+"F7.wireOp",EDGE,"E1032"),sQuery(id+"F7.wireOp",EDGE,"E1033"),sQuery(id+"F7.wireOp",EDGE,"E1034"),sQuery(id+"F7.wireOp",EDGE,"E1035"),sQuery(id+"F7.wireOp",EDGE,"E1036"),sQuery(id+"F7.wireOp",EDGE,"E1037"),sQuery(id+"F7.wireOp",EDGE,"E1038"),sQuery(id+"F7.wireOp",EDGE,"E1039"),sQuery(id+"F7.wireOp",EDGE,"E1040"),sQuery(id+"F7.wireOp",EDGE,"E1041"),sQuery(id+"F7.wireOp",EDGE,"E1042"),sQuery(id+"F7.wireOp",EDGE,"E1043"),sQuery(id+"F7.wireOp",EDGE,"E1044"),sQuery(id+"F7.wireOp",EDGE,"E1045"),sQuery(id+"F7.wireOp",EDGE,"E1046"),sQuery(id+"F7.wireOp",EDGE,"E1047"),sQuery(id+"F7.wireOp",EDGE,"E1048"),sQuery(id+"F7.wireOp",EDGE,"E1049"),sQuery(id+"F7.wireOp",EDGE,"E1050"),sQuery(id+"F7.wireOp",EDGE,"E1051"),sQuery(id+"F7.wireOp",EDGE,"E1052"),sQuery(id+"F7.wireOp",EDGE,"E1053"),sQuery(id+"F7.wireOp",EDGE,"E1054"),sQuery(id+"F7.wireOp",EDGE,"E1055"),sQuery(id+"F7.wireOp",EDGE,"E1056"),sQuery(id+"F7.wireOp",EDGE,"E1057"),sQuery(id+"F7.wireOp",EDGE,"E1058"),sQuery(id+"F7.wireOp",EDGE,"E1059"),sQuery(id+"F7.wireOp",EDGE,"E1060"),sQuery(id+"F7.wireOp",EDGE,"E1061"),sQuery(id+"F7.wireOp",EDGE,"E1062"),sQuery(id+"F7.wireOp",EDGE,"E1063"),sQuery(id+"F7.wireOp",EDGE,"E1064"),sQuery(id+"F7.wireOp",EDGE,"E1065"),sQuery(id+"F7.wireOp",EDGE,"E1066"),sQuery(id+"F7.wireOp",EDGE,"E1067"),sQuery(id+"F7.wireOp",EDGE,"E1068"),sQuery(id+"F7.wireOp",EDGE,"E1069"),sQuery(id+"F7.wireOp",EDGE,"E1070"),sQuery(id+"F7.wireOp",EDGE,"E1071"),sQuery(id+"F7.wireOp",EDGE,"E1072"),sQuery(id+"F7.wireOp",EDGE,"E1073"),sQuery(id+"F7.wireOp",EDGE,"E1074"),sQuery(id+"F7.wireOp",EDGE,"E1075"),sQuery(id+"F7.wireOp",EDGE,"E1076"),sQuery(id+"F7.wireOp",EDGE,"E1077"),sQuery(id+"F7.wireOp",EDGE,"E1078"),sQuery(id+"F7.wireOp",EDGE,"E1079"),sQuery(id+"F7.wireOp",EDGE,"E1080"),sQuery(id+"F7.wireOp",EDGE,"E1081"),sQuery(id+"F7.wireOp",EDGE,"E1082"),sQuery(id+"F7.wireOp",EDGE,"E1083"),sQuery(id+"F7.wireOp",EDGE,"E1084"),sQuery(id+"F7.wireOp",EDGE,"E1085"),sQuery(id+"F7.wireOp",EDGE,"E1086"),sQuery(id+"F7.wireOp",EDGE,"E1087"),sQuery(id+"F7.wireOp",EDGE,"E1088"),sQuery(id+"F7.wireOp",EDGE,"E1089"),sQuery(id+"F7.wireOp",EDGE,"E1090"),sQuery(id+"F7.wireOp",EDGE,"E1091"),sQuery(id+"F7.wireOp",EDGE,"E1092"),sQuery(id+"F7.wireOp",EDGE,"E1093"),sQuery(id+"F7.wireOp",EDGE,"E1094"),sQuery(id+"F7.wireOp",EDGE,"E1095"),sQuery(id+"F7.wireOp",EDGE,"E1096"),sQuery(id+"F7.wireOp",EDGE,"E1097"),sQuery(id+"F7.wireOp",EDGE,"E1098"),sQuery(id+"F7.wireOp",EDGE,"E1099"),sQuery(id+"F7.wireOp",EDGE,"E1100"),sQuery(id+"F7.wireOp",EDGE,"E1101"),sQuery(id+"F7.wireOp",EDGE,"E1102"),sQuery(id+"F7.wireOp",EDGE,"E1103"),sQuery(id+"F7.wireOp",EDGE,"E1104"),sQuery(id+"F7.wireOp",EDGE,"E1105"),sQuery(id+"F7.wireOp",EDGE,"E1106"),sQuery(id+"F7.wireOp",EDGE,"E1107"),sQuery(id+"F7.wireOp",EDGE,"E1108"),sQuery(id+"F7.wireOp",EDGE,"E1109"),sQuery(id+"F7.wireOp",EDGE,"E1110"),sQuery(id+"F7.wireOp",EDGE,"E1111"),sQuery(id+"F7.wireOp",EDGE,"E1112"),sQuery(id+"F7.wireOp",EDGE,"E1113"),sQuery(id+"F7.wireOp",EDGE,"E1114"),sQuery(id+"F7.wireOp",EDGE,"E1115"),sQuery(id+"F7.wireOp",EDGE,"E1116"),sQuery(id+"F7.wireOp",EDGE,"E1117"),sQuery(id+"F7.wireOp",EDGE,"E1118"),sQuery(id+"F7.wireOp",EDGE,"E1119"),sQuery(id+"F7.wireOp",EDGE,"E1120"),sQuery(id+"F7.wireOp",EDGE,"E1121"),sQuery(id+"F7.wireOp",EDGE,"E1122"),sQuery(id+"F7.wireOp",EDGE,"E1123"),sQuery(id+"F7.wireOp",EDGE,"E1124"),sQuery(id+"F7.wireOp",EDGE,"E1125"),sQuery(id+"F7.wireOp",EDGE,"E1126"),sQuery(id+"F7.wireOp",EDGE,"E1127"),sQuery(id+"F7.wireOp",EDGE,"E1128"),sQuery(id+"F7.wireOp",EDGE,"E1129"),sQuery(id+"F7.wireOp",EDGE,"E1130"),sQuery(id+"F7.wireOp",EDGE,"E1131"),sQuery(id+"F7.wireOp",EDGE,"E1132"),sQuery(id+"F7.wireOp",EDGE,"E1133"),sQuery(id+"F7.wireOp",EDGE,"E1134"),sQuery(id+"F7.wireOp",EDGE,"E1135"),sQuery(id+"F7.wireOp",EDGE,"E1136"),sQuery(id+"F7.wireOp",EDGE,"E1137"),sQuery(id+"F7.wireOp",EDGE,"E1138"),sQuery(id+"F7.wireOp",EDGE,"E1139"),sQuery(id+"F7.wireOp",EDGE,"E1140"),sQuery(id+"F7.wireOp",EDGE,"E1141"),sQuery(id+"F7.wireOp",EDGE,"E1142"),sQuery(id+"F7.wireOp",EDGE,"E1143"),sQuery(id+"F7.wireOp",EDGE,"E1144"),sQuery(id+"F7.wireOp",EDGE,"E1145"),sQuery(id+"F7.wireOp",EDGE,"E1146"),sQuery(id+"F7.wireOp",EDGE,"E1147"),sQuery(id+"F7.wireOp",EDGE,"E1148"),sQuery(id+"F7.wireOp",EDGE,"E1149"),sQuery(id+"F7.wireOp",EDGE,"E1150"),sQuery(id+"F7.wireOp",EDGE,"E1151"),sQuery(id+"F7.wireOp",EDGE,"E1152"),sQuery(id+"F7.wireOp",EDGE,"E1153"),sQuery(id+"F7.wireOp",EDGE,"E1154"),sQuery(id+"F7.wireOp",EDGE,"E1155"),sQuery(id+"F7.wireOp",EDGE,"E1156"),sQuery(id+"F7.wireOp",EDGE,"E1157"),sQuery(id+"F7.wireOp",EDGE,"E1158"),sQuery(id+"F7.wireOp",EDGE,"E1159"),sQuery(id+"F7.wireOp",EDGE,"E1160"),sQuery(id+"F7.wireOp",EDGE,"E1161"),sQuery(id+"F7.wireOp",EDGE,"E1162"),sQuery(id+"F7.wireOp",EDGE,"E1163"),sQuery(id+"F7.wireOp",EDGE,"E1164"),sQuery(id+"F7.wireOp",EDGE,"E1165"),sQuery(id+"F7.wireOp",EDGE,"E1166"),sQuery(id+"F7.wireOp",EDGE,"E1167"),sQuery(id+"F7.wireOp",EDGE,"E1168"),sQuery(id+"F7.wireOp",EDGE,"E1169"),sQuery(id+"F7.wireOp",EDGE,"E1170"),sQuery(id+"F7.wireOp",EDGE,"E1171"),sQuery(id+"F7.wireOp",EDGE,"E1172"),sQuery(id+"F7.wireOp",EDGE,"E1173"),sQuery(id+"F7.wireOp",EDGE,"E1174"),sQuery(id+"F7.wireOp",EDGE,"E1175"),sQuery(id+"F7.wireOp",EDGE,"E1176"),sQuery(id+"F7.wireOp",EDGE,"E1177"),sQuery(id+"F7.wireOp",EDGE,"E1178"),sQuery(id+"F7.wireOp",EDGE,"E1179"),sQuery(id+"F7.wireOp",EDGE,"E1180"),sQuery(id+"F7.wireOp",EDGE,"E1181"),sQuery(id+"F7.wireOp",EDGE,"E1182"),sQuery(id+"F7.wireOp",EDGE,"E1183"),sQuery(id+"F7.wireOp",EDGE,"E1184"),sQuery(id+"F7.wireOp",EDGE,"E1185"),sQuery(id+"F7.wireOp",EDGE,"E1186"),sQuery(id+"F7.wireOp",EDGE,"E1187"),sQuery(id+"F7.wireOp",EDGE,"E1188"),sQuery(id+"F7.wireOp",EDGE,"E1189"),sQuery(id+"F7.wireOp",EDGE,"E1190"),sQuery(id+"F7.wireOp",EDGE,"E1191"),sQuery(id+"F7.wireOp",EDGE,"E1192"),sQuery(id+"F7.wireOp",EDGE,"E1193"),sQuery(id+"F7.wireOp",EDGE,"E1194"),sQuery(id+"F7.wireOp",EDGE,"E1195"),sQuery(id+"F7.wireOp",EDGE,"E1196"),sQuery(id+"F7.wireOp",EDGE,"E1197"),sQuery(id+"F7.wireOp",EDGE,"E1198"),sQuery(id+"F7.wireOp",EDGE,"E1199"),sQuery(id+"F7.wireOp",EDGE,"E1200"),sQuery(id+"F7.wireOp",EDGE,"E1201"),sQuery(id+"F7.wireOp",EDGE,"E1202"),sQuery(id+"F7.wireOp",EDGE,"E1203"),sQuery(id+"F7.wireOp",EDGE,"E1204"),sQuery(id+"F7.wireOp",EDGE,"E1205"),sQuery(id+"F7.wireOp",EDGE,"E1206"),sQuery(id+"F7.wireOp",EDGE,"E1207"),sQuery(id+"F7.wireOp",EDGE,"E1208"),sQuery(id+"F7.wireOp",EDGE,"E1209"),sQuery(id+"F7.wireOp",EDGE,"E1210"),sQuery(id+"F7.wireOp",EDGE,"E1211"),sQuery(id+"F7.wireOp",EDGE,"E1212"),sQuery(id+"F7.wireOp",EDGE,"E1213"),sQuery(id+"F7.wireOp",EDGE,"E1214"),sQuery(id+"F7.wireOp",EDGE,"E1215"),sQuery(id+"F7.wireOp",EDGE,"E1216"),sQuery(id+"F7.wireOp",EDGE,"E1217"),sQuery(id+"F7.wireOp",EDGE,"E1218"),sQuery(id+"F7.wireOp",EDGE,"E1219"),sQuery(id+"F7.wireOp",EDGE,"E1220"),sQuery(id+"F7.wireOp",EDGE,"E1221"),sQuery(id+"F7.wireOp",EDGE,"E1222"),sQuery(id+"F7.wireOp",EDGE,"E1223"),sQuery(id+"F7.wireOp",EDGE,"E1224"),sQuery(id+"F7.wireOp",EDGE,"E1225"),sQuery(id+"F7.wireOp",EDGE,"E1226"),sQuery(id+"F7.wireOp",EDGE,"E1227"),sQuery(id+"F7.wireOp",EDGE,"E1228"),sQuery(id+"F7.wireOp",EDGE,"E1229"),sQuery(id+"F7.wireOp",EDGE,"E1230"),sQuery(id+"F7.wireOp",EDGE,"E1231"),sQuery(id+"F7.wireOp",EDGE,"E1232"),sQuery(id+"F7.wireOp",EDGE,"E1233"),sQuery(id+"F7.wireOp",EDGE,"E1234"),sQuery(id+"F7.wireOp",EDGE,"E1235"),sQuery(id+"F7.wireOp",EDGE,"E1236"),sQuery(id+"F7.wireOp",EDGE,"E1237"),sQuery(id+"F7.wireOp",EDGE,"E1238"),sQuery(id+"F7.wireOp",EDGE,"E1239"),sQuery(id+"F7.wireOp",EDGE,"E1240"),sQuery(id+"F7.wireOp",EDGE,"E1241"),sQuery(id+"F7.wireOp",EDGE,"E1242"),sQuery(id+"F7.wireOp",EDGE,"E1243"),sQuery(id+"F7.wireOp",EDGE,"E1244"),sQuery(id+"F7.wireOp",EDGE,"E1245"),sQuery(id+"F7.wireOp",EDGE,"E1246"),sQuery(id+"F7.wireOp",EDGE,"E1247"),sQuery(id+"F7.wireOp",EDGE,"E1248"),sQuery(id+"F7.wireOp",EDGE,"E1249"),sQuery(id+"F7.wireOp",EDGE,"E1250"),sQuery(id+"F7.wireOp",EDGE,"E1251"),sQuery(id+"F7.wireOp",EDGE,"E1252"),sQuery(id+"F7.wireOp",EDGE,"E1253"),sQuery(id+"F7.wireOp",EDGE,"E1254"),sQuery(id+"F7.wireOp",EDGE,"E1255"),sQuery(id+"F7.wireOp",EDGE,"E1256"),sQuery(id+"F7.wireOp",EDGE,"E1257"),sQuery(id+"F7.wireOp",EDGE,"E1258"),sQuery(id+"F7.wireOp",EDGE,"E1259"),sQuery(id+"F7.wireOp",EDGE,"E1260"),sQuery(id+"F7.wireOp",EDGE,"E1261"),sQuery(id+"F7.wireOp",EDGE,"E1262"),sQuery(id+"F7.wireOp",EDGE,"E1263"),sQuery(id+"F7.wireOp",EDGE,"E1264"),sQuery(id+"F7.wireOp",EDGE,"E1265"),sQuery(id+"F7.wireOp",EDGE,"E1266"),sQuery(id+"F7.wireOp",EDGE,"E1267"),sQuery(id+"F7.wireOp",EDGE,"E1268"),sQuery(id+"F7.wireOp",EDGE,"E1269"),sQuery(id+"F7.wireOp",EDGE,"E1270"),sQuery(id+"F7.wireOp",EDGE,"E1271"),sQuery(id+"F7.wireOp",EDGE,"E1272"),sQuery(id+"F7.wireOp",EDGE,"E1273"),sQuery(id+"F7.wireOp",EDGE,"E1274"),sQuery(id+"F7.wireOp",EDGE,"E1275"),sQuery(id+"F7.wireOp",EDGE,"E1276"),sQuery(id+"F7.wireOp",EDGE,"E1277"),sQuery(id+"F7.wireOp",EDGE,"E1278"),sQuery(id+"F7.wireOp",EDGE,"E1279"),sQuery(id+"F7.wireOp",EDGE,"E1280"),sQuery(id+"F7.wireOp",EDGE,"E1281"),sQuery(id+"F7.wireOp",EDGE,"E1282"),sQuery(id+"F7.wireOp",EDGE,"E1283"),sQuery(id+"F7.wireOp",EDGE,"E1284"),sQuery(id+"F7.wireOp",EDGE,"E1285"),sQuery(id+"F7.wireOp",EDGE,"E1286"),sQuery(id+"F7.wireOp",EDGE,"E1287"),sQuery(id+"F7.wireOp",EDGE,"E1288"),sQuery(id+"F7.wireOp",EDGE,"E1289"),sQuery(id+"F7.wireOp",EDGE,"E1290"),sQuery(id+"F7.wireOp",EDGE,"E1291"),sQuery(id+"F7.wireOp",EDGE,"E1292"),sQuery(id+"F7.wireOp",EDGE,"E1293"),sQuery(id+"F7.wireOp",EDGE,"E1294"),sQuery(id+"F7.wireOp",EDGE,"E1295"),sQuery(id+"F7.wireOp",EDGE,"E1296"),sQuery(id+"F7.wireOp",EDGE,"E1297"),sQuery(id+"F7.wireOp",EDGE,"E1298"),sQuery(id+"F7.wireOp",EDGE,"E1299"),sQuery(id+"F7.wireOp",EDGE,"E1300"),sQuery(id+"F7.wireOp",EDGE,"E1301"),sQuery(id+"F7.wireOp",EDGE,"E1302"),sQuery(id+"F7.wireOp",EDGE,"E1303"),sQuery(id+"F7.wireOp",EDGE,"E1304"),sQuery(id+"F7.wireOp",EDGE,"E1305"),sQuery(id+"F7.wireOp",EDGE,"E1306"),sQuery(id+"F7.wireOp",EDGE,"E1307"),sQuery(id+"F7.wireOp",EDGE,"E1308"),sQuery(id+"F7.wireOp",EDGE,"E1309"),sQuery(id+"F7.wireOp",EDGE,"E1310"),sQuery(id+"F7.wireOp",EDGE,"E1311"),sQuery(id+"F7.wireOp",EDGE,"E1312"),sQuery(id+"F7.wireOp",EDGE,"E1313"),sQuery(id+"F7.wireOp",EDGE,"E1314"),sQuery(id+"F7.wireOp",EDGE,"E1315"),sQuery(id+"F7.wireOp",EDGE,"E1316"),sQuery(id+"F7.wireOp",EDGE,"E1317"),sQuery(id+"F7.wireOp",EDGE,"E1318"),sQuery(id+"F7.wireOp",EDGE,"E1319"),sQuery(id+"F7.wireOp",EDGE,"E1320"),sQuery(id+"F7.wireOp",EDGE,"E1321"),sQuery(id+"F7.wireOp",EDGE,"E1322"),sQuery(id+"F7.wireOp",EDGE,"E1323"),sQuery(id+"F7.wireOp",EDGE,"E1324"),sQuery(id+"F7.wireOp",EDGE,"E1325"),sQuery(id+"F7.wireOp",EDGE,"E1326"),sQuery(id+"F7.wireOp",EDGE,"E1327"),sQuery(id+"F7.wireOp",EDGE,"E1328"),sQuery(id+"F7.wireOp",EDGE,"E1329"),sQuery(id+"F7.wireOp",EDGE,"E1330"),sQuery(id+"F7.wireOp",EDGE,"E1331"),sQuery(id+"F7.wireOp",EDGE,"E1332"),sQuery(id+"F7.wireOp",EDGE,"E1333"),sQuery(id+"F7.wireOp",EDGE,"E1334"),sQuery(id+"F7.wireOp",EDGE,"E1335"),sQuery(id+"F7.wireOp",EDGE,"E1336"),sQuery(id+"F7.wireOp",EDGE,"E1337"),sQuery(id+"F7.wireOp",EDGE,"E1338"),sQuery(id+"F7.wireOp",EDGE,"E1339"),sQuery(id+"F7.wireOp",EDGE,"E1340"),sQuery(id+"F7.wireOp",EDGE,"E1341"),sQuery(id+"F7.wireOp",EDGE,"E1342"),sQuery(id+"F7.wireOp",EDGE,"E1343"),sQuery(id+"F7.wireOp",EDGE,"E1344"),sQuery(id+"F7.wireOp",EDGE,"E1345"),sQuery(id+"F7.wireOp",EDGE,"E1346"),sQuery(id+"F7.wireOp",EDGE,"E1347"),sQuery(id+"F7.wireOp",EDGE,"E1348"),sQuery(id+"F7.wireOp",EDGE,"E1349"),sQuery(id+"F7.wireOp",EDGE,"E1350"),sQuery(id+"F7.wireOp",EDGE,"E1351"),sQuery(id+"F7.wireOp",EDGE,"E1352"),sQuery(id+"F7.wireOp",EDGE,"E1353"),sQuery(id+"F7.wireOp",EDGE,"E1354"),sQuery(id+"F7.wireOp",EDGE,"E1355"),sQuery(id+"F7.wireOp",EDGE,"E1356"),sQuery(id+"F7.wireOp",EDGE,"E1357"),sQuery(id+"F7.wireOp",EDGE,"E1358"),sQuery(id+"F7.wireOp",EDGE,"E1359"),sQuery(id+"F7.wireOp",EDGE,"E1360"),sQuery(id+"F7.wireOp",EDGE,"E1361"),sQuery(id+"F7.wireOp",EDGE,"E1362"),sQuery(id+"F7.wireOp",EDGE,"E1363"),sQuery(id+"F7.wireOp",EDGE,"E1364"),sQuery(id+"F7.wireOp",EDGE,"E1365"),sQuery(id+"F7.wireOp",EDGE,"E1366"),sQuery(id+"F7.wireOp",EDGE,"E1367"),sQuery(id+"F7.wireOp",EDGE,"E1368"),sQuery(id+"F7.wireOp",EDGE,"E1369"),sQuery(id+"F7.wireOp",EDGE,"E1370"),sQuery(id+"F7.wireOp",EDGE,"E1371"),sQuery(id+"F7.wireOp",EDGE,"E1372"),sQuery(id+"F7.wireOp",EDGE,"E1373"),sQuery(id+"F7.wireOp",EDGE,"E1374"),sQuery(id+"F7.wireOp",EDGE,"E1375"),sQuery(id+"F7.wireOp",EDGE,"E1376"),sQuery(id+"F7.wireOp",EDGE,"E1377"),sQuery(id+"F7.wireOp",EDGE,"E1378"),sQuery(id+"F7.wireOp",EDGE,"E1379"),sQuery(id+"F7.wireOp",EDGE,"E1380"),sQuery(id+"F7.wireOp",EDGE,"E1381"),sQuery(id+"F7.wireOp",EDGE,"E1382"),sQuery(id+"F7.wireOp",EDGE,"E1383"),sQuery(id+"F7.wireOp",EDGE,"E1384"),sQuery(id+"F7.wireOp",EDGE,"E1385"),sQuery(id+"F7.wireOp",EDGE,"E1386"),sQuery(id+"F7.wireOp",EDGE,"E1387"),sQuery(id+"F7.wireOp",EDGE,"E1388"),sQuery(id+"F7.wireOp",EDGE,"E1389"),sQuery(id+"F7.wireOp",EDGE,"E1390"),sQuery(id+"F7.wireOp",EDGE,"E1391"),sQuery(id+"F7.wireOp",EDGE,"E1392"),sQuery(id+"F7.wireOp",EDGE,"E1393"),sQuery(id+"F7.wireOp",EDGE,"E1394"),sQuery(id+"F7.wireOp",EDGE,"E1395"),sQuery(id+"F7.wireOp",EDGE,"E1396"),sQuery(id+"F7.wireOp",EDGE,"E1397"),sQuery(id+"F7.wireOp",EDGE,"E1398"),sQuery(id+"F7.wireOp",EDGE,"E1399"),sQuery(id+"F7.wireOp",EDGE,"E1400"),sQuery(id+"F7.wireOp",EDGE,"E1401"),sQuery(id+"F7.wireOp",EDGE,"E1402"),sQuery(id+"F7.wireOp",EDGE,"E1403"),sQuery(id+"F7.wireOp",EDGE,"E1404"),sQuery(id+"F7.wireOp",EDGE,"E1405"),sQuery(id+"F7.wireOp",EDGE,"E1406"),sQuery(id+"F7.wireOp",EDGE,"E1407"),sQuery(id+"F7.wireOp",EDGE,"E1408"),sQuery(id+"F7.wireOp",EDGE,"E1409"),sQuery(id+"F7.wireOp",EDGE,"E1410"),sQuery(id+"F7.wireOp",EDGE,"E1411"),sQuery(id+"F7.wireOp",EDGE,"E1412"),sQuery(id+"F7.wireOp",EDGE,"E1413"),sQuery(id+"F7.wireOp",EDGE,"E1414"),sQuery(id+"F7.wireOp",EDGE,"E1415"),sQuery(id+"F7.wireOp",EDGE,"E1416"),sQuery(id+"F7.wireOp",EDGE,"E1417"),sQuery(id+"F7.wireOp",EDGE,"E1418"),sQuery(id+"F7.wireOp",EDGE,"E1419"),sQuery(id+"F7.wireOp",EDGE,"E1420"),sQuery(id+"F7.wireOp",EDGE,"E1421"),sQuery(id+"F7.wireOp",EDGE,"E1422"),sQuery(id+"F7.wireOp",EDGE,"E1423"),sQuery(id+"F7.wireOp",EDGE,"E1424"),sQuery(id+"F7.wireOp",EDGE,"E1425"),sQuery(id+"F7.wireOp",EDGE,"E1426"),sQuery(id+"F7.wireOp",EDGE,"E1427"),sQuery(id+"F7.wireOp",EDGE,"E1428"),sQuery(id+"F7.wireOp",EDGE,"E1429"),sQuery(id+"F7.wireOp",EDGE,"E1430"),sQuery(id+"F7.wireOp",EDGE,"E1431"),sQuery(id+"F7.wireOp",EDGE,"E1432"),sQuery(id+"F7.wireOp",EDGE,"E1433"),sQuery(id+"F7.wireOp",EDGE,"E1434"),sQuery(id+"F7.wireOp",EDGE,"E1435"),sQuery(id+"F7.wireOp",EDGE,"E1436"),sQuery(id+"F7.wireOp",EDGE,"E1437"),sQuery(id+"F7.wireOp",EDGE,"E1438"),sQuery(id+"F7.wireOp",EDGE,"E1439"),sQuery(id+"F7.wireOp",EDGE,"E1440"),sQuery(id+"F7.wireOp",EDGE,"E1441"),sQuery(id+"F7.wireOp",EDGE,"E1442"),sQuery(id+"F7.wireOp",EDGE,"E1443"),sQuery(id+"F7.wireOp",EDGE,"E1444"),sQuery(id+"F7.wireOp",EDGE,"E1445"),sQuery(id+"F7.wireOp",EDGE,"E1446"),sQuery(id+"F7.wireOp",EDGE,"E1447"),sQuery(id+"F7.wireOp",EDGE,"E1448"),sQuery(id+"F7.wireOp",EDGE,"E1449"),sQuery(id+"F7.wireOp",EDGE,"E1450"),sQuery(id+"F7.wireOp",EDGE,"E1451"),sQuery(id+"F7.wireOp",EDGE,"E1452"),sQuery(id+"F7.wireOp",EDGE,"E1453"),sQuery(id+"F7.wireOp",EDGE,"E1454"),sQuery(id+"F7.wireOp",EDGE,"E1455"),sQuery(id+"F7.wireOp",EDGE,"E1456"),sQuery(id+"F7.wireOp",EDGE,"E1457"),sQuery(id+"F7.wireOp",EDGE,"E1458"),sQuery(id+"F7.wireOp",EDGE,"E1459"),sQuery(id+"F7.wireOp",EDGE,"E1460"),sQuery(id+"F7.wireOp",EDGE,"E1461"),sQuery(id+"F7.wireOp",EDGE,"E1462"),sQuery(id+"F7.wireOp",EDGE,"E1463"),sQuery(id+"F7.wireOp",EDGE,"E1464"),sQuery(id+"F7.wireOp",EDGE,"E1465"),sQuery(id+"F7.wireOp",EDGE,"E1466"),sQuery(id+"F7.wireOp",EDGE,"E1467"),sQuery(id+"F7.wireOp",EDGE,"E1468"),sQuery(id+"F7.wireOp",EDGE,"E1469"),sQuery(id+"F7.wireOp",EDGE,"E1470"),sQuery(id+"F7.wireOp",EDGE,"E1471"),sQuery(id+"F7.wireOp",EDGE,"E1472"),sQuery(id+"F7.wireOp",EDGE,"E1473"),sQuery(id+"F7.wireOp",EDGE,"E1474"),sQuery(id+"F7.wireOp",EDGE,"E1475"),sQuery(id+"F7.wireOp",EDGE,"E1476"),sQuery(id+"F7.wireOp",EDGE,"E1477"),sQuery(id+"F7.wireOp",EDGE,"E1478"),sQuery(id+"F7.wireOp",EDGE,"E1479"),sQuery(id+"F7.wireOp",EDGE,"E1480"),sQuery(id+"F7.wireOp",EDGE,"E1481"),sQuery(id+"F7.wireOp",EDGE,"E1482"),sQuery(id+"F7.wireOp",EDGE,"E1483"),sQuery(id+"F7.wireOp",EDGE,"E1484"),sQuery(id+"F7.wireOp",EDGE,"E1485"),sQuery(id+"F7.wireOp",EDGE,"E1486"),sQuery(id+"F7.wireOp",EDGE,"E1487"),sQuery(id+"F7.wireOp",EDGE,"E1488"),sQuery(id+"F7.wireOp",EDGE,"E1489"),sQuery(id+"F7.wireOp",EDGE,"E1490"),sQuery(id+"F7.wireOp",EDGE,"E1491"),sQuery(id+"F7.wireOp",EDGE,"E1492"),sQuery(id+"F7.wireOp",EDGE,"E1493"),sQuery(id+"F7.wireOp",EDGE,"E1494"),sQuery(id+"F7.wireOp",EDGE,"E1495"),sQuery(id+"F7.wireOp",EDGE,"E1496"),sQuery(id+"F7.wireOp",EDGE,"E1497"),sQuery(id+"F7.wireOp",EDGE,"E1498"),sQuery(id+"F7.wireOp",EDGE,"E1499"),sQuery(id+"F7.wireOp",EDGE,"E1500"),sQuery(id+"F7.wireOp",EDGE,"E1501"),sQuery(id+"F7.wireOp",EDGE,"E1502"),sQuery(id+"F7.wireOp",EDGE,"E1503"),sQuery(id+"F7.wireOp",EDGE,"E1504"),sQuery(id+"F7.wireOp",EDGE,"E1505"),sQuery(id+"F7.wireOp",EDGE,"E1506"),sQuery(id+"F7.wireOp",EDGE,"E1507"),sQuery(id+"F7.wireOp",EDGE,"E1508"),sQuery(id+"F7.wireOp",EDGE,"E1509"),sQuery(id+"F7.wireOp",EDGE,"E1510"),sQuery(id+"F7.wireOp",EDGE,"E1511"),sQuery(id+"F7.wireOp",EDGE,"E1512"),sQuery(id+"F7.wireOp",EDGE,"E1513"),sQuery(id+"F7.wireOp",EDGE,"E1514"),sQuery(id+"F7.wireOp",EDGE,"E1515"),sQuery(id+"F7.wireOp",EDGE,"E1516"),sQuery(id+"F7.wireOp",EDGE,"E1517"),sQuery(id+"F7.wireOp",EDGE,"E1518"),sQuery(id+"F7.wireOp",EDGE,"E1519"),sQuery(id+"F7.wireOp",EDGE,"E1520"),sQuery(id+"F7.wireOp",EDGE,"E1521"),sQuery(id+"F7.wireOp",EDGE,"E1522"),sQuery(id+"F7.wireOp",EDGE,"E1523"),sQuery(id+"F7.wireOp",EDGE,"E1524"),sQuery(id+"F7.wireOp",EDGE,"E1525"),sQuery(id+"F7.wireOp",EDGE,"E1526"),sQuery(id+"F7.wireOp",EDGE,"E1527"),sQuery(id+"F7.wireOp",EDGE,"E1528"),sQuery(id+"F7.wireOp",EDGE,"E1529"),sQuery(id+"F7.wireOp",EDGE,"E1530"),sQuery(id+"F7.wireOp",EDGE,"E1531"),sQuery(id+"F7.wireOp",EDGE,"E1532"),sQuery(id+"F7.wireOp",EDGE,"E1533"),sQuery(id+"F7.wireOp",EDGE,"E1534"),sQuery(id+"F7.wireOp",EDGE,"E1535"),sQuery(id+"F7.wireOp",EDGE,"E1536"),sQuery(id+"F7.wireOp",EDGE,"E1537"),sQuery(id+"F7.wireOp",EDGE,"E1538"),sQuery(id+"F7.wireOp",EDGE,"E1539"),sQuery(id+"F7.wireOp",EDGE,"E1540"),sQuery(id+"F7.wireOp",EDGE,"E1541"),sQuery(id+"F7.wireOp",EDGE,"E1542"),sQuery(id+"F7.wireOp",EDGE,"E1543"),sQuery(id+"F7.wireOp",EDGE,"E1544"),sQuery(id+"F7.wireOp",EDGE,"E1545"),sQuery(id+"F7.wireOp",EDGE,"E1546"),sQuery(id+"F7.wireOp",EDGE,"E1547"),sQuery(id+"F7.wireOp",EDGE,"E1548"),sQuery(id+"F7.wireOp",EDGE,"E1549"),sQuery(id+"F7.wireOp",EDGE,"E1550"),sQuery(id+"F7.wireOp",EDGE,"E1551"),sQuery(id+"F7.wireOp",EDGE,"E1552"),sQuery(id+"F7.wireOp",EDGE,"E1553"),sQuery(id+"F7.wireOp",EDGE,"E1554"),sQuery(id+"F7.wireOp",EDGE,"E1555"),sQuery(id+"F7.wireOp",EDGE,"E1556"),sQuery(id+"F7.wireOp",EDGE,"E1557"),sQuery(id+"F7.wireOp",EDGE,"E1558"),sQuery(id+"F7.wireOp",EDGE,"E1559"),sQuery(id+"F7.wireOp",EDGE,"E1560"),sQuery(id+"F7.wireOp",EDGE,"E1561")])]});
            var Q1;
            Q1=sQuery(id+"F10.wireOp",EDGE,"E1565");
            transform(context, id + "F11", {"entities" : qUnion([Q0]), "transformType" : TransformType.ROTATION, "transformAxis" : qUnion([Q1]), "angle" : 90 * degree, "makeCopy" : false});
        }
        {
            var Q0;
            Q0=makeQuery(id+"F8.opExtrude","SWEPT_BODY",BODY,{"disambiguationData":[OSD([sQuery(id+"F7.wireOp",EDGE,"E449"),sQuery(id+"F7.wireOp",EDGE,"E450"),sQuery(id+"F7.wireOp",EDGE,"E451"),sQuery(id+"F7.wireOp",EDGE,"E452"),sQuery(id+"F7.wireOp",EDGE,"E453"),sQuery(id+"F7.wireOp",EDGE,"E454"),sQuery(id+"F7.wireOp",EDGE,"E455"),sQuery(id+"F7.wireOp",EDGE,"E456"),sQuery(id+"F7.wireOp",EDGE,"E457"),sQuery(id+"F7.wireOp",EDGE,"E458"),sQuery(id+"F7.wireOp",EDGE,"E459"),sQuery(id+"F7.wireOp",EDGE,"E460"),sQuery(id+"F7.wireOp",EDGE,"E461"),sQuery(id+"F7.wireOp",EDGE,"E462"),sQuery(id+"F7.wireOp",EDGE,"E463"),sQuery(id+"F7.wireOp",EDGE,"E464"),sQuery(id+"F7.wireOp",EDGE,"E465"),sQuery(id+"F7.wireOp",EDGE,"E466"),sQuery(id+"F7.wireOp",EDGE,"E467"),sQuery(id+"F7.wireOp",EDGE,"E468"),sQuery(id+"F7.wireOp",EDGE,"E469"),sQuery(id+"F7.wireOp",EDGE,"E470"),sQuery(id+"F7.wireOp",EDGE,"E471"),sQuery(id+"F7.wireOp",EDGE,"E472"),sQuery(id+"F7.wireOp",EDGE,"E473"),sQuery(id+"F7.wireOp",EDGE,"E474"),sQuery(id+"F7.wireOp",EDGE,"E475"),sQuery(id+"F7.wireOp",EDGE,"E476"),sQuery(id+"F7.wireOp",EDGE,"E477"),sQuery(id+"F7.wireOp",EDGE,"E478"),sQuery(id+"F7.wireOp",EDGE,"E479"),sQuery(id+"F7.wireOp",EDGE,"E480"),sQuery(id+"F7.wireOp",EDGE,"E481"),sQuery(id+"F7.wireOp",EDGE,"E482"),sQuery(id+"F7.wireOp",EDGE,"E483"),sQuery(id+"F7.wireOp",EDGE,"E484"),sQuery(id+"F7.wireOp",EDGE,"E485"),sQuery(id+"F7.wireOp",EDGE,"E486"),sQuery(id+"F7.wireOp",EDGE,"E487"),sQuery(id+"F7.wireOp",EDGE,"E488"),sQuery(id+"F7.wireOp",EDGE,"E489"),sQuery(id+"F7.wireOp",EDGE,"E490"),sQuery(id+"F7.wireOp",EDGE,"E491"),sQuery(id+"F7.wireOp",EDGE,"E492"),sQuery(id+"F7.wireOp",EDGE,"E493"),sQuery(id+"F7.wireOp",EDGE,"E494"),sQuery(id+"F7.wireOp",EDGE,"E495"),sQuery(id+"F7.wireOp",EDGE,"E496"),sQuery(id+"F7.wireOp",EDGE,"E497"),sQuery(id+"F7.wireOp",EDGE,"E498"),sQuery(id+"F7.wireOp",EDGE,"E499"),sQuery(id+"F7.wireOp",EDGE,"E500"),sQuery(id+"F7.wireOp",EDGE,"E501"),sQuery(id+"F7.wireOp",EDGE,"E502"),sQuery(id+"F7.wireOp",EDGE,"E503"),sQuery(id+"F7.wireOp",EDGE,"E504"),sQuery(id+"F7.wireOp",EDGE,"E505"),sQuery(id+"F7.wireOp",EDGE,"E506"),sQuery(id+"F7.wireOp",EDGE,"E507"),sQuery(id+"F7.wireOp",EDGE,"E508"),sQuery(id+"F7.wireOp",EDGE,"E509"),sQuery(id+"F7.wireOp",EDGE,"E510"),sQuery(id+"F7.wireOp",EDGE,"E511"),sQuery(id+"F7.wireOp",EDGE,"E512"),sQuery(id+"F7.wireOp",EDGE,"E513"),sQuery(id+"F7.wireOp",EDGE,"E514"),sQuery(id+"F7.wireOp",EDGE,"E515"),sQuery(id+"F7.wireOp",EDGE,"E516"),sQuery(id+"F7.wireOp",EDGE,"E517"),sQuery(id+"F7.wireOp",EDGE,"E518"),sQuery(id+"F7.wireOp",EDGE,"E519"),sQuery(id+"F7.wireOp",EDGE,"E520"),sQuery(id+"F7.wireOp",EDGE,"E521"),sQuery(id+"F7.wireOp",EDGE,"E522"),sQuery(id+"F7.wireOp",EDGE,"E523"),sQuery(id+"F7.wireOp",EDGE,"E524"),sQuery(id+"F7.wireOp",EDGE,"E525"),sQuery(id+"F7.wireOp",EDGE,"E526"),sQuery(id+"F7.wireOp",EDGE,"E527"),sQuery(id+"F7.wireOp",EDGE,"E528"),sQuery(id+"F7.wireOp",EDGE,"E529"),sQuery(id+"F7.wireOp",EDGE,"E530"),sQuery(id+"F7.wireOp",EDGE,"E531"),sQuery(id+"F7.wireOp",EDGE,"E532"),sQuery(id+"F7.wireOp",EDGE,"E533"),sQuery(id+"F7.wireOp",EDGE,"E534"),sQuery(id+"F7.wireOp",EDGE,"E535"),sQuery(id+"F7.wireOp",EDGE,"E536"),sQuery(id+"F7.wireOp",EDGE,"E537"),sQuery(id+"F7.wireOp",EDGE,"E538"),sQuery(id+"F7.wireOp",EDGE,"E539"),sQuery(id+"F7.wireOp",EDGE,"E540"),sQuery(id+"F7.wireOp",EDGE,"E541"),sQuery(id+"F7.wireOp",EDGE,"E542"),sQuery(id+"F7.wireOp",EDGE,"E543"),sQuery(id+"F7.wireOp",EDGE,"E544"),sQuery(id+"F7.wireOp",EDGE,"E545"),sQuery(id+"F7.wireOp",EDGE,"E546"),sQuery(id+"F7.wireOp",EDGE,"E547"),sQuery(id+"F7.wireOp",EDGE,"E548"),sQuery(id+"F7.wireOp",EDGE,"E549"),sQuery(id+"F7.wireOp",EDGE,"E550"),sQuery(id+"F7.wireOp",EDGE,"E551"),sQuery(id+"F7.wireOp",EDGE,"E552"),sQuery(id+"F7.wireOp",EDGE,"E553"),sQuery(id+"F7.wireOp",EDGE,"E554"),sQuery(id+"F7.wireOp",EDGE,"E555"),sQuery(id+"F7.wireOp",EDGE,"E556"),sQuery(id+"F7.wireOp",EDGE,"E557"),sQuery(id+"F7.wireOp",EDGE,"E558"),sQuery(id+"F7.wireOp",EDGE,"E559"),sQuery(id+"F7.wireOp",EDGE,"E560"),sQuery(id+"F7.wireOp",EDGE,"E561"),sQuery(id+"F7.wireOp",EDGE,"E562"),sQuery(id+"F7.wireOp",EDGE,"E563"),sQuery(id+"F7.wireOp",EDGE,"E564"),sQuery(id+"F7.wireOp",EDGE,"E565"),sQuery(id+"F7.wireOp",EDGE,"E566"),sQuery(id+"F7.wireOp",EDGE,"E567"),sQuery(id+"F7.wireOp",EDGE,"E568"),sQuery(id+"F7.wireOp",EDGE,"E569"),sQuery(id+"F7.wireOp",EDGE,"E570"),sQuery(id+"F7.wireOp",EDGE,"E571"),sQuery(id+"F7.wireOp",EDGE,"E572"),sQuery(id+"F7.wireOp",EDGE,"E573"),sQuery(id+"F7.wireOp",EDGE,"E574"),sQuery(id+"F7.wireOp",EDGE,"E575"),sQuery(id+"F7.wireOp",EDGE,"E576"),sQuery(id+"F7.wireOp",EDGE,"E577"),sQuery(id+"F7.wireOp",EDGE,"E578"),sQuery(id+"F7.wireOp",EDGE,"E579"),sQuery(id+"F7.wireOp",EDGE,"E580"),sQuery(id+"F7.wireOp",EDGE,"E581"),sQuery(id+"F7.wireOp",EDGE,"E582"),sQuery(id+"F7.wireOp",EDGE,"E583"),sQuery(id+"F7.wireOp",EDGE,"E584"),sQuery(id+"F7.wireOp",EDGE,"E585"),sQuery(id+"F7.wireOp",EDGE,"E586"),sQuery(id+"F7.wireOp",EDGE,"E587"),sQuery(id+"F7.wireOp",EDGE,"E588"),sQuery(id+"F7.wireOp",EDGE,"E589"),sQuery(id+"F7.wireOp",EDGE,"E590"),sQuery(id+"F7.wireOp",EDGE,"E591"),sQuery(id+"F7.wireOp",EDGE,"E592"),sQuery(id+"F7.wireOp",EDGE,"E593"),sQuery(id+"F7.wireOp",EDGE,"E594"),sQuery(id+"F7.wireOp",EDGE,"E595"),sQuery(id+"F7.wireOp",EDGE,"E596"),sQuery(id+"F7.wireOp",EDGE,"E597"),sQuery(id+"F7.wireOp",EDGE,"E598"),sQuery(id+"F7.wireOp",EDGE,"E599"),sQuery(id+"F7.wireOp",EDGE,"E600"),sQuery(id+"F7.wireOp",EDGE,"E601"),sQuery(id+"F7.wireOp",EDGE,"E602"),sQuery(id+"F7.wireOp",EDGE,"E603"),sQuery(id+"F7.wireOp",EDGE,"E604"),sQuery(id+"F7.wireOp",EDGE,"E605"),sQuery(id+"F7.wireOp",EDGE,"E606"),sQuery(id+"F7.wireOp",EDGE,"E607"),sQuery(id+"F7.wireOp",EDGE,"E608"),sQuery(id+"F7.wireOp",EDGE,"E609"),sQuery(id+"F7.wireOp",EDGE,"E610"),sQuery(id+"F7.wireOp",EDGE,"E611"),sQuery(id+"F7.wireOp",EDGE,"E612"),sQuery(id+"F7.wireOp",EDGE,"E613"),sQuery(id+"F7.wireOp",EDGE,"E614"),sQuery(id+"F7.wireOp",EDGE,"E615"),sQuery(id+"F7.wireOp",EDGE,"E616"),sQuery(id+"F7.wireOp",EDGE,"E617"),sQuery(id+"F7.wireOp",EDGE,"E618"),sQuery(id+"F7.wireOp",EDGE,"E619"),sQuery(id+"F7.wireOp",EDGE,"E620"),sQuery(id+"F7.wireOp",EDGE,"E621"),sQuery(id+"F7.wireOp",EDGE,"E622"),sQuery(id+"F7.wireOp",EDGE,"E623"),sQuery(id+"F7.wireOp",EDGE,"E624"),sQuery(id+"F7.wireOp",EDGE,"E625"),sQuery(id+"F7.wireOp",EDGE,"E626"),sQuery(id+"F7.wireOp",EDGE,"E627"),sQuery(id+"F7.wireOp",EDGE,"E628"),sQuery(id+"F7.wireOp",EDGE,"E629"),sQuery(id+"F7.wireOp",EDGE,"E630"),sQuery(id+"F7.wireOp",EDGE,"E631"),sQuery(id+"F7.wireOp",EDGE,"E632"),sQuery(id+"F7.wireOp",EDGE,"E633"),sQuery(id+"F7.wireOp",EDGE,"E634"),sQuery(id+"F7.wireOp",EDGE,"E635"),sQuery(id+"F7.wireOp",EDGE,"E636"),sQuery(id+"F7.wireOp",EDGE,"E637"),sQuery(id+"F7.wireOp",EDGE,"E638"),sQuery(id+"F7.wireOp",EDGE,"E639"),sQuery(id+"F7.wireOp",EDGE,"E640"),sQuery(id+"F7.wireOp",EDGE,"E641"),sQuery(id+"F7.wireOp",EDGE,"E642"),sQuery(id+"F7.wireOp",EDGE,"E643"),sQuery(id+"F7.wireOp",EDGE,"E644"),sQuery(id+"F7.wireOp",EDGE,"E645"),sQuery(id+"F7.wireOp",EDGE,"E646"),sQuery(id+"F7.wireOp",EDGE,"E647"),sQuery(id+"F7.wireOp",EDGE,"E648"),sQuery(id+"F7.wireOp",EDGE,"E649"),sQuery(id+"F7.wireOp",EDGE,"E650"),sQuery(id+"F7.wireOp",EDGE,"E651"),sQuery(id+"F7.wireOp",EDGE,"E652"),sQuery(id+"F7.wireOp",EDGE,"E653"),sQuery(id+"F7.wireOp",EDGE,"E654"),sQuery(id+"F7.wireOp",EDGE,"E655"),sQuery(id+"F7.wireOp",EDGE,"E656"),sQuery(id+"F7.wireOp",EDGE,"E657"),sQuery(id+"F7.wireOp",EDGE,"E658"),sQuery(id+"F7.wireOp",EDGE,"E659"),sQuery(id+"F7.wireOp",EDGE,"E660"),sQuery(id+"F7.wireOp",EDGE,"E661"),sQuery(id+"F7.wireOp",EDGE,"E662"),sQuery(id+"F7.wireOp",EDGE,"E663"),sQuery(id+"F7.wireOp",EDGE,"E664"),sQuery(id+"F7.wireOp",EDGE,"E665"),sQuery(id+"F7.wireOp",EDGE,"E666"),sQuery(id+"F7.wireOp",EDGE,"E667"),sQuery(id+"F7.wireOp",EDGE,"E668"),sQuery(id+"F7.wireOp",EDGE,"E669"),sQuery(id+"F7.wireOp",EDGE,"E670"),sQuery(id+"F7.wireOp",EDGE,"E671"),sQuery(id+"F7.wireOp",EDGE,"E672"),sQuery(id+"F7.wireOp",EDGE,"E673"),sQuery(id+"F7.wireOp",EDGE,"E674"),sQuery(id+"F7.wireOp",EDGE,"E675"),sQuery(id+"F7.wireOp",EDGE,"E676"),sQuery(id+"F7.wireOp",EDGE,"E677"),sQuery(id+"F7.wireOp",EDGE,"E678"),sQuery(id+"F7.wireOp",EDGE,"E679"),sQuery(id+"F7.wireOp",EDGE,"E680"),sQuery(id+"F7.wireOp",EDGE,"E681"),sQuery(id+"F7.wireOp",EDGE,"E682"),sQuery(id+"F7.wireOp",EDGE,"E683"),sQuery(id+"F7.wireOp",EDGE,"E684"),sQuery(id+"F7.wireOp",EDGE,"E685"),sQuery(id+"F7.wireOp",EDGE,"E686"),sQuery(id+"F7.wireOp",EDGE,"E687"),sQuery(id+"F7.wireOp",EDGE,"E688"),sQuery(id+"F7.wireOp",EDGE,"E689"),sQuery(id+"F7.wireOp",EDGE,"E690"),sQuery(id+"F7.wireOp",EDGE,"E691"),sQuery(id+"F7.wireOp",EDGE,"E692"),sQuery(id+"F7.wireOp",EDGE,"E693"),sQuery(id+"F7.wireOp",EDGE,"E694"),sQuery(id+"F7.wireOp",EDGE,"E695"),sQuery(id+"F7.wireOp",EDGE,"E696"),sQuery(id+"F7.wireOp",EDGE,"E697"),sQuery(id+"F7.wireOp",EDGE,"E698"),sQuery(id+"F7.wireOp",EDGE,"E699"),sQuery(id+"F7.wireOp",EDGE,"E700"),sQuery(id+"F7.wireOp",EDGE,"E701"),sQuery(id+"F7.wireOp",EDGE,"E702"),sQuery(id+"F7.wireOp",EDGE,"E703"),sQuery(id+"F7.wireOp",EDGE,"E704"),sQuery(id+"F7.wireOp",EDGE,"E705"),sQuery(id+"F7.wireOp",EDGE,"E706"),sQuery(id+"F7.wireOp",EDGE,"E707"),sQuery(id+"F7.wireOp",EDGE,"E708"),sQuery(id+"F7.wireOp",EDGE,"E709"),sQuery(id+"F7.wireOp",EDGE,"E710"),sQuery(id+"F7.wireOp",EDGE,"E711"),sQuery(id+"F7.wireOp",EDGE,"E712"),sQuery(id+"F7.wireOp",EDGE,"E713"),sQuery(id+"F7.wireOp",EDGE,"E714"),sQuery(id+"F7.wireOp",EDGE,"E715"),sQuery(id+"F7.wireOp",EDGE,"E716"),sQuery(id+"F7.wireOp",EDGE,"E717"),sQuery(id+"F7.wireOp",EDGE,"E718"),sQuery(id+"F7.wireOp",EDGE,"E719"),sQuery(id+"F7.wireOp",EDGE,"E720"),sQuery(id+"F7.wireOp",EDGE,"E721"),sQuery(id+"F7.wireOp",EDGE,"E722"),sQuery(id+"F7.wireOp",EDGE,"E723"),sQuery(id+"F7.wireOp",EDGE,"E724"),sQuery(id+"F7.wireOp",EDGE,"E725"),sQuery(id+"F7.wireOp",EDGE,"E726"),sQuery(id+"F7.wireOp",EDGE,"E727"),sQuery(id+"F7.wireOp",EDGE,"E728"),sQuery(id+"F7.wireOp",EDGE,"E729"),sQuery(id+"F7.wireOp",EDGE,"E730"),sQuery(id+"F7.wireOp",EDGE,"E731"),sQuery(id+"F7.wireOp",EDGE,"E732"),sQuery(id+"F7.wireOp",EDGE,"E733"),sQuery(id+"F7.wireOp",EDGE,"E734"),sQuery(id+"F7.wireOp",EDGE,"E735"),sQuery(id+"F7.wireOp",EDGE,"E736"),sQuery(id+"F7.wireOp",EDGE,"E737"),sQuery(id+"F7.wireOp",EDGE,"E738"),sQuery(id+"F7.wireOp",EDGE,"E739"),sQuery(id+"F7.wireOp",EDGE,"E740"),sQuery(id+"F7.wireOp",EDGE,"E741"),sQuery(id+"F7.wireOp",EDGE,"E742"),sQuery(id+"F7.wireOp",EDGE,"E743"),sQuery(id+"F7.wireOp",EDGE,"E744"),sQuery(id+"F7.wireOp",EDGE,"E745"),sQuery(id+"F7.wireOp",EDGE,"E746"),sQuery(id+"F7.wireOp",EDGE,"E747"),sQuery(id+"F7.wireOp",EDGE,"E748"),sQuery(id+"F7.wireOp",EDGE,"E749"),sQuery(id+"F7.wireOp",EDGE,"E750"),sQuery(id+"F7.wireOp",EDGE,"E751"),sQuery(id+"F7.wireOp",EDGE,"E752"),sQuery(id+"F7.wireOp",EDGE,"E753"),sQuery(id+"F7.wireOp",EDGE,"E754"),sQuery(id+"F7.wireOp",EDGE,"E755"),sQuery(id+"F7.wireOp",EDGE,"E756"),sQuery(id+"F7.wireOp",EDGE,"E757"),sQuery(id+"F7.wireOp",EDGE,"E758"),sQuery(id+"F7.wireOp",EDGE,"E759"),sQuery(id+"F7.wireOp",EDGE,"E760"),sQuery(id+"F7.wireOp",EDGE,"E761"),sQuery(id+"F7.wireOp",EDGE,"E762"),sQuery(id+"F7.wireOp",EDGE,"E763"),sQuery(id+"F7.wireOp",EDGE,"E764"),sQuery(id+"F7.wireOp",EDGE,"E765"),sQuery(id+"F7.wireOp",EDGE,"E766"),sQuery(id+"F7.wireOp",EDGE,"E767"),sQuery(id+"F7.wireOp",EDGE,"E768"),sQuery(id+"F7.wireOp",EDGE,"E769"),sQuery(id+"F7.wireOp",EDGE,"E770"),sQuery(id+"F7.wireOp",EDGE,"E771"),sQuery(id+"F7.wireOp",EDGE,"E772"),sQuery(id+"F7.wireOp",EDGE,"E773"),sQuery(id+"F7.wireOp",EDGE,"E774"),sQuery(id+"F7.wireOp",EDGE,"E775"),sQuery(id+"F7.wireOp",EDGE,"E776"),sQuery(id+"F7.wireOp",EDGE,"E777"),sQuery(id+"F7.wireOp",EDGE,"E778"),sQuery(id+"F7.wireOp",EDGE,"E779"),sQuery(id+"F7.wireOp",EDGE,"E780"),sQuery(id+"F7.wireOp",EDGE,"E781"),sQuery(id+"F7.wireOp",EDGE,"E782"),sQuery(id+"F7.wireOp",EDGE,"E783"),sQuery(id+"F7.wireOp",EDGE,"E784"),sQuery(id+"F7.wireOp",EDGE,"E785"),sQuery(id+"F7.wireOp",EDGE,"E786"),sQuery(id+"F7.wireOp",EDGE,"E787"),sQuery(id+"F7.wireOp",EDGE,"E788"),sQuery(id+"F7.wireOp",EDGE,"E789"),sQuery(id+"F7.wireOp",EDGE,"E790"),sQuery(id+"F7.wireOp",EDGE,"E791"),sQuery(id+"F7.wireOp",EDGE,"E792"),sQuery(id+"F7.wireOp",EDGE,"E793"),sQuery(id+"F7.wireOp",EDGE,"E794"),sQuery(id+"F7.wireOp",EDGE,"E795"),sQuery(id+"F7.wireOp",EDGE,"E796"),sQuery(id+"F7.wireOp",EDGE,"E797"),sQuery(id+"F7.wireOp",EDGE,"E798"),sQuery(id+"F7.wireOp",EDGE,"E799"),sQuery(id+"F7.wireOp",EDGE,"E800"),sQuery(id+"F7.wireOp",EDGE,"E801"),sQuery(id+"F7.wireOp",EDGE,"E802"),sQuery(id+"F7.wireOp",EDGE,"E803"),sQuery(id+"F7.wireOp",EDGE,"E804"),sQuery(id+"F7.wireOp",EDGE,"E805"),sQuery(id+"F7.wireOp",EDGE,"E806"),sQuery(id+"F7.wireOp",EDGE,"E807"),sQuery(id+"F7.wireOp",EDGE,"E808"),sQuery(id+"F7.wireOp",EDGE,"E809"),sQuery(id+"F7.wireOp",EDGE,"E810"),sQuery(id+"F7.wireOp",EDGE,"E811"),sQuery(id+"F7.wireOp",EDGE,"E812"),sQuery(id+"F7.wireOp",EDGE,"E813"),sQuery(id+"F7.wireOp",EDGE,"E814"),sQuery(id+"F7.wireOp",EDGE,"E815"),sQuery(id+"F7.wireOp",EDGE,"E816"),sQuery(id+"F7.wireOp",EDGE,"E817"),sQuery(id+"F7.wireOp",EDGE,"E818"),sQuery(id+"F7.wireOp",EDGE,"E819"),sQuery(id+"F7.wireOp",EDGE,"E820"),sQuery(id+"F7.wireOp",EDGE,"E821"),sQuery(id+"F7.wireOp",EDGE,"E822"),sQuery(id+"F7.wireOp",EDGE,"E823"),sQuery(id+"F7.wireOp",EDGE,"E824"),sQuery(id+"F7.wireOp",EDGE,"E825"),sQuery(id+"F7.wireOp",EDGE,"E826"),sQuery(id+"F7.wireOp",EDGE,"E827"),sQuery(id+"F7.wireOp",EDGE,"E828"),sQuery(id+"F7.wireOp",EDGE,"E829"),sQuery(id+"F7.wireOp",EDGE,"E830"),sQuery(id+"F7.wireOp",EDGE,"E831"),sQuery(id+"F7.wireOp",EDGE,"E832"),sQuery(id+"F7.wireOp",EDGE,"E833"),sQuery(id+"F7.wireOp",EDGE,"E834"),sQuery(id+"F7.wireOp",EDGE,"E835"),sQuery(id+"F7.wireOp",EDGE,"E836"),sQuery(id+"F7.wireOp",EDGE,"E837"),sQuery(id+"F7.wireOp",EDGE,"E838"),sQuery(id+"F7.wireOp",EDGE,"E839"),sQuery(id+"F7.wireOp",EDGE,"E840"),sQuery(id+"F7.wireOp",EDGE,"E841"),sQuery(id+"F7.wireOp",EDGE,"E842"),sQuery(id+"F7.wireOp",EDGE,"E843"),sQuery(id+"F7.wireOp",EDGE,"E844"),sQuery(id+"F7.wireOp",EDGE,"E845"),sQuery(id+"F7.wireOp",EDGE,"E846"),sQuery(id+"F7.wireOp",EDGE,"E847"),sQuery(id+"F7.wireOp",EDGE,"E848"),sQuery(id+"F7.wireOp",EDGE,"E849"),sQuery(id+"F7.wireOp",EDGE,"E850"),sQuery(id+"F7.wireOp",EDGE,"E851"),sQuery(id+"F7.wireOp",EDGE,"E852"),sQuery(id+"F7.wireOp",EDGE,"E853"),sQuery(id+"F7.wireOp",EDGE,"E854"),sQuery(id+"F7.wireOp",EDGE,"E855"),sQuery(id+"F7.wireOp",EDGE,"E856"),sQuery(id+"F7.wireOp",EDGE,"E857"),sQuery(id+"F7.wireOp",EDGE,"E858"),sQuery(id+"F7.wireOp",EDGE,"E859"),sQuery(id+"F7.wireOp",EDGE,"E860"),sQuery(id+"F7.wireOp",EDGE,"E861"),sQuery(id+"F7.wireOp",EDGE,"E862"),sQuery(id+"F7.wireOp",EDGE,"E863"),sQuery(id+"F7.wireOp",EDGE,"E864"),sQuery(id+"F7.wireOp",EDGE,"E865"),sQuery(id+"F7.wireOp",EDGE,"E866"),sQuery(id+"F7.wireOp",EDGE,"E867"),sQuery(id+"F7.wireOp",EDGE,"E868"),sQuery(id+"F7.wireOp",EDGE,"E869"),sQuery(id+"F7.wireOp",EDGE,"E870"),sQuery(id+"F7.wireOp",EDGE,"E871"),sQuery(id+"F7.wireOp",EDGE,"E872"),sQuery(id+"F7.wireOp",EDGE,"E873"),sQuery(id+"F7.wireOp",EDGE,"E874"),sQuery(id+"F7.wireOp",EDGE,"E875"),sQuery(id+"F7.wireOp",EDGE,"E876"),sQuery(id+"F7.wireOp",EDGE,"E877"),sQuery(id+"F7.wireOp",EDGE,"E878"),sQuery(id+"F7.wireOp",EDGE,"E879"),sQuery(id+"F7.wireOp",EDGE,"E880"),sQuery(id+"F7.wireOp",EDGE,"E881"),sQuery(id+"F7.wireOp",EDGE,"E882"),sQuery(id+"F7.wireOp",EDGE,"E883"),sQuery(id+"F7.wireOp",EDGE,"E884"),sQuery(id+"F7.wireOp",EDGE,"E885"),sQuery(id+"F7.wireOp",EDGE,"E886"),sQuery(id+"F7.wireOp",EDGE,"E887"),sQuery(id+"F7.wireOp",EDGE,"E888"),sQuery(id+"F7.wireOp",EDGE,"E889"),sQuery(id+"F7.wireOp",EDGE,"E890"),sQuery(id+"F7.wireOp",EDGE,"E891"),sQuery(id+"F7.wireOp",EDGE,"E892"),sQuery(id+"F7.wireOp",EDGE,"E893"),sQuery(id+"F7.wireOp",EDGE,"E894"),sQuery(id+"F7.wireOp",EDGE,"E895"),sQuery(id+"F7.wireOp",EDGE,"E896"),sQuery(id+"F7.wireOp",EDGE,"E897"),sQuery(id+"F7.wireOp",EDGE,"E898"),sQuery(id+"F7.wireOp",EDGE,"E899"),sQuery(id+"F7.wireOp",EDGE,"E900"),sQuery(id+"F7.wireOp",EDGE,"E901"),sQuery(id+"F7.wireOp",EDGE,"E902"),sQuery(id+"F7.wireOp",EDGE,"E903"),sQuery(id+"F7.wireOp",EDGE,"E904"),sQuery(id+"F7.wireOp",EDGE,"E905"),sQuery(id+"F7.wireOp",EDGE,"E906"),sQuery(id+"F7.wireOp",EDGE,"E907"),sQuery(id+"F7.wireOp",EDGE,"E908"),sQuery(id+"F7.wireOp",EDGE,"E909"),sQuery(id+"F7.wireOp",EDGE,"E910"),sQuery(id+"F7.wireOp",EDGE,"E911"),sQuery(id+"F7.wireOp",EDGE,"E912"),sQuery(id+"F7.wireOp",EDGE,"E913"),sQuery(id+"F7.wireOp",EDGE,"E914"),sQuery(id+"F7.wireOp",EDGE,"E915"),sQuery(id+"F7.wireOp",EDGE,"E916"),sQuery(id+"F7.wireOp",EDGE,"E917"),sQuery(id+"F7.wireOp",EDGE,"E918"),sQuery(id+"F7.wireOp",EDGE,"E919"),sQuery(id+"F7.wireOp",EDGE,"E920"),sQuery(id+"F7.wireOp",EDGE,"E921"),sQuery(id+"F7.wireOp",EDGE,"E922"),sQuery(id+"F7.wireOp",EDGE,"E923"),sQuery(id+"F7.wireOp",EDGE,"E924"),sQuery(id+"F7.wireOp",EDGE,"E925"),sQuery(id+"F7.wireOp",EDGE,"E926"),sQuery(id+"F7.wireOp",EDGE,"E927"),sQuery(id+"F7.wireOp",EDGE,"E928"),sQuery(id+"F7.wireOp",EDGE,"E929"),sQuery(id+"F7.wireOp",EDGE,"E930"),sQuery(id+"F7.wireOp",EDGE,"E931"),sQuery(id+"F7.wireOp",EDGE,"E932"),sQuery(id+"F7.wireOp",EDGE,"E933"),sQuery(id+"F7.wireOp",EDGE,"E934"),sQuery(id+"F7.wireOp",EDGE,"E935"),sQuery(id+"F7.wireOp",EDGE,"E936"),sQuery(id+"F7.wireOp",EDGE,"E937"),sQuery(id+"F7.wireOp",EDGE,"E938"),sQuery(id+"F7.wireOp",EDGE,"E939"),sQuery(id+"F7.wireOp",EDGE,"E940"),sQuery(id+"F7.wireOp",EDGE,"E941"),sQuery(id+"F7.wireOp",EDGE,"E942"),sQuery(id+"F7.wireOp",EDGE,"E943"),sQuery(id+"F7.wireOp",EDGE,"E944"),sQuery(id+"F7.wireOp",EDGE,"E945"),sQuery(id+"F7.wireOp",EDGE,"E946"),sQuery(id+"F7.wireOp",EDGE,"E947"),sQuery(id+"F7.wireOp",EDGE,"E948"),sQuery(id+"F7.wireOp",EDGE,"E949"),sQuery(id+"F7.wireOp",EDGE,"E950"),sQuery(id+"F7.wireOp",EDGE,"E951"),sQuery(id+"F7.wireOp",EDGE,"E952"),sQuery(id+"F7.wireOp",EDGE,"E953"),sQuery(id+"F7.wireOp",EDGE,"E954"),sQuery(id+"F7.wireOp",EDGE,"E955"),sQuery(id+"F7.wireOp",EDGE,"E956"),sQuery(id+"F7.wireOp",EDGE,"E957"),sQuery(id+"F7.wireOp",EDGE,"E958"),sQuery(id+"F7.wireOp",EDGE,"E959"),sQuery(id+"F7.wireOp",EDGE,"E960"),sQuery(id+"F7.wireOp",EDGE,"E961"),sQuery(id+"F7.wireOp",EDGE,"E962"),sQuery(id+"F7.wireOp",EDGE,"E963"),sQuery(id+"F7.wireOp",EDGE,"E964"),sQuery(id+"F7.wireOp",EDGE,"E965"),sQuery(id+"F7.wireOp",EDGE,"E966"),sQuery(id+"F7.wireOp",EDGE,"E967"),sQuery(id+"F7.wireOp",EDGE,"E968"),sQuery(id+"F7.wireOp",EDGE,"E969"),sQuery(id+"F7.wireOp",EDGE,"E970"),sQuery(id+"F7.wireOp",EDGE,"E971"),sQuery(id+"F7.wireOp",EDGE,"E972"),sQuery(id+"F7.wireOp",EDGE,"E973"),sQuery(id+"F7.wireOp",EDGE,"E974"),sQuery(id+"F7.wireOp",EDGE,"E975"),sQuery(id+"F7.wireOp",EDGE,"E976"),sQuery(id+"F7.wireOp",EDGE,"E977"),sQuery(id+"F7.wireOp",EDGE,"E978"),sQuery(id+"F7.wireOp",EDGE,"E979"),sQuery(id+"F7.wireOp",EDGE,"E980"),sQuery(id+"F7.wireOp",EDGE,"E981"),sQuery(id+"F7.wireOp",EDGE,"E982"),sQuery(id+"F7.wireOp",EDGE,"E983"),sQuery(id+"F7.wireOp",EDGE,"E984"),sQuery(id+"F7.wireOp",EDGE,"E985"),sQuery(id+"F7.wireOp",EDGE,"E986"),sQuery(id+"F7.wireOp",EDGE,"E987"),sQuery(id+"F7.wireOp",EDGE,"E988"),sQuery(id+"F7.wireOp",EDGE,"E989"),sQuery(id+"F7.wireOp",EDGE,"E990"),sQuery(id+"F7.wireOp",EDGE,"E991"),sQuery(id+"F7.wireOp",EDGE,"E992"),sQuery(id+"F7.wireOp",EDGE,"E993"),sQuery(id+"F7.wireOp",EDGE,"E994"),sQuery(id+"F7.wireOp",EDGE,"E995"),sQuery(id+"F7.wireOp",EDGE,"E996"),sQuery(id+"F7.wireOp",EDGE,"E997"),sQuery(id+"F7.wireOp",EDGE,"E998"),sQuery(id+"F7.wireOp",EDGE,"E999"),sQuery(id+"F7.wireOp",EDGE,"E1000"),sQuery(id+"F7.wireOp",EDGE,"E1001"),sQuery(id+"F7.wireOp",EDGE,"E1002"),sQuery(id+"F7.wireOp",EDGE,"E1003"),sQuery(id+"F7.wireOp",EDGE,"E1004"),sQuery(id+"F7.wireOp",EDGE,"E1005"),sQuery(id+"F7.wireOp",EDGE,"E1006"),sQuery(id+"F7.wireOp",EDGE,"E1007"),sQuery(id+"F7.wireOp",EDGE,"E1008"),sQuery(id+"F7.wireOp",EDGE,"E1009"),sQuery(id+"F7.wireOp",EDGE,"E1010"),sQuery(id+"F7.wireOp",EDGE,"E1011"),sQuery(id+"F7.wireOp",EDGE,"E1012"),sQuery(id+"F7.wireOp",EDGE,"E1013"),sQuery(id+"F7.wireOp",EDGE,"E1014"),sQuery(id+"F7.wireOp",EDGE,"E1015"),sQuery(id+"F7.wireOp",EDGE,"E1016"),sQuery(id+"F7.wireOp",EDGE,"E1017"),sQuery(id+"F7.wireOp",EDGE,"E1018"),sQuery(id+"F7.wireOp",EDGE,"E1019"),sQuery(id+"F7.wireOp",EDGE,"E1020"),sQuery(id+"F7.wireOp",EDGE,"E1021"),sQuery(id+"F7.wireOp",EDGE,"E1022"),sQuery(id+"F7.wireOp",EDGE,"E1023"),sQuery(id+"F7.wireOp",EDGE,"E1024"),sQuery(id+"F7.wireOp",EDGE,"E1025"),sQuery(id+"F7.wireOp",EDGE,"E1026"),sQuery(id+"F7.wireOp",EDGE,"E1027"),sQuery(id+"F7.wireOp",EDGE,"E1028"),sQuery(id+"F7.wireOp",EDGE,"E1029"),sQuery(id+"F7.wireOp",EDGE,"E1030"),sQuery(id+"F7.wireOp",EDGE,"E1031"),sQuery(id+"F7.wireOp",EDGE,"E1032"),sQuery(id+"F7.wireOp",EDGE,"E1033"),sQuery(id+"F7.wireOp",EDGE,"E1034"),sQuery(id+"F7.wireOp",EDGE,"E1035"),sQuery(id+"F7.wireOp",EDGE,"E1036"),sQuery(id+"F7.wireOp",EDGE,"E1037"),sQuery(id+"F7.wireOp",EDGE,"E1038"),sQuery(id+"F7.wireOp",EDGE,"E1039"),sQuery(id+"F7.wireOp",EDGE,"E1040"),sQuery(id+"F7.wireOp",EDGE,"E1041"),sQuery(id+"F7.wireOp",EDGE,"E1042"),sQuery(id+"F7.wireOp",EDGE,"E1043"),sQuery(id+"F7.wireOp",EDGE,"E1044"),sQuery(id+"F7.wireOp",EDGE,"E1045"),sQuery(id+"F7.wireOp",EDGE,"E1046"),sQuery(id+"F7.wireOp",EDGE,"E1047"),sQuery(id+"F7.wireOp",EDGE,"E1048"),sQuery(id+"F7.wireOp",EDGE,"E1049"),sQuery(id+"F7.wireOp",EDGE,"E1050"),sQuery(id+"F7.wireOp",EDGE,"E1051"),sQuery(id+"F7.wireOp",EDGE,"E1052"),sQuery(id+"F7.wireOp",EDGE,"E1053"),sQuery(id+"F7.wireOp",EDGE,"E1054"),sQuery(id+"F7.wireOp",EDGE,"E1055"),sQuery(id+"F7.wireOp",EDGE,"E1056"),sQuery(id+"F7.wireOp",EDGE,"E1057"),sQuery(id+"F7.wireOp",EDGE,"E1058"),sQuery(id+"F7.wireOp",EDGE,"E1059"),sQuery(id+"F7.wireOp",EDGE,"E1060"),sQuery(id+"F7.wireOp",EDGE,"E1061"),sQuery(id+"F7.wireOp",EDGE,"E1062"),sQuery(id+"F7.wireOp",EDGE,"E1063"),sQuery(id+"F7.wireOp",EDGE,"E1064"),sQuery(id+"F7.wireOp",EDGE,"E1065"),sQuery(id+"F7.wireOp",EDGE,"E1066"),sQuery(id+"F7.wireOp",EDGE,"E1067"),sQuery(id+"F7.wireOp",EDGE,"E1068"),sQuery(id+"F7.wireOp",EDGE,"E1069"),sQuery(id+"F7.wireOp",EDGE,"E1070"),sQuery(id+"F7.wireOp",EDGE,"E1071"),sQuery(id+"F7.wireOp",EDGE,"E1072"),sQuery(id+"F7.wireOp",EDGE,"E1073"),sQuery(id+"F7.wireOp",EDGE,"E1074"),sQuery(id+"F7.wireOp",EDGE,"E1075"),sQuery(id+"F7.wireOp",EDGE,"E1076"),sQuery(id+"F7.wireOp",EDGE,"E1077"),sQuery(id+"F7.wireOp",EDGE,"E1078"),sQuery(id+"F7.wireOp",EDGE,"E1079"),sQuery(id+"F7.wireOp",EDGE,"E1080"),sQuery(id+"F7.wireOp",EDGE,"E1081"),sQuery(id+"F7.wireOp",EDGE,"E1082"),sQuery(id+"F7.wireOp",EDGE,"E1083"),sQuery(id+"F7.wireOp",EDGE,"E1084"),sQuery(id+"F7.wireOp",EDGE,"E1085"),sQuery(id+"F7.wireOp",EDGE,"E1086"),sQuery(id+"F7.wireOp",EDGE,"E1087"),sQuery(id+"F7.wireOp",EDGE,"E1088"),sQuery(id+"F7.wireOp",EDGE,"E1089"),sQuery(id+"F7.wireOp",EDGE,"E1090"),sQuery(id+"F7.wireOp",EDGE,"E1091"),sQuery(id+"F7.wireOp",EDGE,"E1092"),sQuery(id+"F7.wireOp",EDGE,"E1093"),sQuery(id+"F7.wireOp",EDGE,"E1094"),sQuery(id+"F7.wireOp",EDGE,"E1095"),sQuery(id+"F7.wireOp",EDGE,"E1096"),sQuery(id+"F7.wireOp",EDGE,"E1097"),sQuery(id+"F7.wireOp",EDGE,"E1098"),sQuery(id+"F7.wireOp",EDGE,"E1099"),sQuery(id+"F7.wireOp",EDGE,"E1100"),sQuery(id+"F7.wireOp",EDGE,"E1101"),sQuery(id+"F7.wireOp",EDGE,"E1102"),sQuery(id+"F7.wireOp",EDGE,"E1103"),sQuery(id+"F7.wireOp",EDGE,"E1104"),sQuery(id+"F7.wireOp",EDGE,"E1105"),sQuery(id+"F7.wireOp",EDGE,"E1106"),sQuery(id+"F7.wireOp",EDGE,"E1107"),sQuery(id+"F7.wireOp",EDGE,"E1108"),sQuery(id+"F7.wireOp",EDGE,"E1109"),sQuery(id+"F7.wireOp",EDGE,"E1110"),sQuery(id+"F7.wireOp",EDGE,"E1111"),sQuery(id+"F7.wireOp",EDGE,"E1112"),sQuery(id+"F7.wireOp",EDGE,"E1113"),sQuery(id+"F7.wireOp",EDGE,"E1114"),sQuery(id+"F7.wireOp",EDGE,"E1115"),sQuery(id+"F7.wireOp",EDGE,"E1116"),sQuery(id+"F7.wireOp",EDGE,"E1117"),sQuery(id+"F7.wireOp",EDGE,"E1118"),sQuery(id+"F7.wireOp",EDGE,"E1119"),sQuery(id+"F7.wireOp",EDGE,"E1120"),sQuery(id+"F7.wireOp",EDGE,"E1121"),sQuery(id+"F7.wireOp",EDGE,"E1122"),sQuery(id+"F7.wireOp",EDGE,"E1123"),sQuery(id+"F7.wireOp",EDGE,"E1124"),sQuery(id+"F7.wireOp",EDGE,"E1125"),sQuery(id+"F7.wireOp",EDGE,"E1126"),sQuery(id+"F7.wireOp",EDGE,"E1127"),sQuery(id+"F7.wireOp",EDGE,"E1128"),sQuery(id+"F7.wireOp",EDGE,"E1129"),sQuery(id+"F7.wireOp",EDGE,"E1130"),sQuery(id+"F7.wireOp",EDGE,"E1131"),sQuery(id+"F7.wireOp",EDGE,"E1132"),sQuery(id+"F7.wireOp",EDGE,"E1133"),sQuery(id+"F7.wireOp",EDGE,"E1134"),sQuery(id+"F7.wireOp",EDGE,"E1135"),sQuery(id+"F7.wireOp",EDGE,"E1136"),sQuery(id+"F7.wireOp",EDGE,"E1137"),sQuery(id+"F7.wireOp",EDGE,"E1138"),sQuery(id+"F7.wireOp",EDGE,"E1139"),sQuery(id+"F7.wireOp",EDGE,"E1140"),sQuery(id+"F7.wireOp",EDGE,"E1141"),sQuery(id+"F7.wireOp",EDGE,"E1142"),sQuery(id+"F7.wireOp",EDGE,"E1143"),sQuery(id+"F7.wireOp",EDGE,"E1144"),sQuery(id+"F7.wireOp",EDGE,"E1145"),sQuery(id+"F7.wireOp",EDGE,"E1146"),sQuery(id+"F7.wireOp",EDGE,"E1147"),sQuery(id+"F7.wireOp",EDGE,"E1148"),sQuery(id+"F7.wireOp",EDGE,"E1149"),sQuery(id+"F7.wireOp",EDGE,"E1150"),sQuery(id+"F7.wireOp",EDGE,"E1151"),sQuery(id+"F7.wireOp",EDGE,"E1152"),sQuery(id+"F7.wireOp",EDGE,"E1153"),sQuery(id+"F7.wireOp",EDGE,"E1154"),sQuery(id+"F7.wireOp",EDGE,"E1155"),sQuery(id+"F7.wireOp",EDGE,"E1156"),sQuery(id+"F7.wireOp",EDGE,"E1157"),sQuery(id+"F7.wireOp",EDGE,"E1158"),sQuery(id+"F7.wireOp",EDGE,"E1159"),sQuery(id+"F7.wireOp",EDGE,"E1160"),sQuery(id+"F7.wireOp",EDGE,"E1161"),sQuery(id+"F7.wireOp",EDGE,"E1162"),sQuery(id+"F7.wireOp",EDGE,"E1163"),sQuery(id+"F7.wireOp",EDGE,"E1164"),sQuery(id+"F7.wireOp",EDGE,"E1165"),sQuery(id+"F7.wireOp",EDGE,"E1166"),sQuery(id+"F7.wireOp",EDGE,"E1167"),sQuery(id+"F7.wireOp",EDGE,"E1168"),sQuery(id+"F7.wireOp",EDGE,"E1169"),sQuery(id+"F7.wireOp",EDGE,"E1170"),sQuery(id+"F7.wireOp",EDGE,"E1171"),sQuery(id+"F7.wireOp",EDGE,"E1172"),sQuery(id+"F7.wireOp",EDGE,"E1173"),sQuery(id+"F7.wireOp",EDGE,"E1174"),sQuery(id+"F7.wireOp",EDGE,"E1175"),sQuery(id+"F7.wireOp",EDGE,"E1176"),sQuery(id+"F7.wireOp",EDGE,"E1177"),sQuery(id+"F7.wireOp",EDGE,"E1178"),sQuery(id+"F7.wireOp",EDGE,"E1179"),sQuery(id+"F7.wireOp",EDGE,"E1180"),sQuery(id+"F7.wireOp",EDGE,"E1181"),sQuery(id+"F7.wireOp",EDGE,"E1182"),sQuery(id+"F7.wireOp",EDGE,"E1183"),sQuery(id+"F7.wireOp",EDGE,"E1184"),sQuery(id+"F7.wireOp",EDGE,"E1185"),sQuery(id+"F7.wireOp",EDGE,"E1186"),sQuery(id+"F7.wireOp",EDGE,"E1187"),sQuery(id+"F7.wireOp",EDGE,"E1188"),sQuery(id+"F7.wireOp",EDGE,"E1189"),sQuery(id+"F7.wireOp",EDGE,"E1190"),sQuery(id+"F7.wireOp",EDGE,"E1191"),sQuery(id+"F7.wireOp",EDGE,"E1192"),sQuery(id+"F7.wireOp",EDGE,"E1193"),sQuery(id+"F7.wireOp",EDGE,"E1194"),sQuery(id+"F7.wireOp",EDGE,"E1195"),sQuery(id+"F7.wireOp",EDGE,"E1196"),sQuery(id+"F7.wireOp",EDGE,"E1197"),sQuery(id+"F7.wireOp",EDGE,"E1198"),sQuery(id+"F7.wireOp",EDGE,"E1199"),sQuery(id+"F7.wireOp",EDGE,"E1200"),sQuery(id+"F7.wireOp",EDGE,"E1201"),sQuery(id+"F7.wireOp",EDGE,"E1202"),sQuery(id+"F7.wireOp",EDGE,"E1203"),sQuery(id+"F7.wireOp",EDGE,"E1204"),sQuery(id+"F7.wireOp",EDGE,"E1205"),sQuery(id+"F7.wireOp",EDGE,"E1206"),sQuery(id+"F7.wireOp",EDGE,"E1207"),sQuery(id+"F7.wireOp",EDGE,"E1208"),sQuery(id+"F7.wireOp",EDGE,"E1209"),sQuery(id+"F7.wireOp",EDGE,"E1210"),sQuery(id+"F7.wireOp",EDGE,"E1211"),sQuery(id+"F7.wireOp",EDGE,"E1212"),sQuery(id+"F7.wireOp",EDGE,"E1213"),sQuery(id+"F7.wireOp",EDGE,"E1214"),sQuery(id+"F7.wireOp",EDGE,"E1215"),sQuery(id+"F7.wireOp",EDGE,"E1216"),sQuery(id+"F7.wireOp",EDGE,"E1217"),sQuery(id+"F7.wireOp",EDGE,"E1218"),sQuery(id+"F7.wireOp",EDGE,"E1219"),sQuery(id+"F7.wireOp",EDGE,"E1220"),sQuery(id+"F7.wireOp",EDGE,"E1221"),sQuery(id+"F7.wireOp",EDGE,"E1222"),sQuery(id+"F7.wireOp",EDGE,"E1223"),sQuery(id+"F7.wireOp",EDGE,"E1224"),sQuery(id+"F7.wireOp",EDGE,"E1225"),sQuery(id+"F7.wireOp",EDGE,"E1226"),sQuery(id+"F7.wireOp",EDGE,"E1227"),sQuery(id+"F7.wireOp",EDGE,"E1228"),sQuery(id+"F7.wireOp",EDGE,"E1229"),sQuery(id+"F7.wireOp",EDGE,"E1230"),sQuery(id+"F7.wireOp",EDGE,"E1231"),sQuery(id+"F7.wireOp",EDGE,"E1232"),sQuery(id+"F7.wireOp",EDGE,"E1233"),sQuery(id+"F7.wireOp",EDGE,"E1234"),sQuery(id+"F7.wireOp",EDGE,"E1235"),sQuery(id+"F7.wireOp",EDGE,"E1236"),sQuery(id+"F7.wireOp",EDGE,"E1237"),sQuery(id+"F7.wireOp",EDGE,"E1238"),sQuery(id+"F7.wireOp",EDGE,"E1239"),sQuery(id+"F7.wireOp",EDGE,"E1240"),sQuery(id+"F7.wireOp",EDGE,"E1241"),sQuery(id+"F7.wireOp",EDGE,"E1242"),sQuery(id+"F7.wireOp",EDGE,"E1243"),sQuery(id+"F7.wireOp",EDGE,"E1244"),sQuery(id+"F7.wireOp",EDGE,"E1245"),sQuery(id+"F7.wireOp",EDGE,"E1246"),sQuery(id+"F7.wireOp",EDGE,"E1247"),sQuery(id+"F7.wireOp",EDGE,"E1248"),sQuery(id+"F7.wireOp",EDGE,"E1249"),sQuery(id+"F7.wireOp",EDGE,"E1250"),sQuery(id+"F7.wireOp",EDGE,"E1251"),sQuery(id+"F7.wireOp",EDGE,"E1252"),sQuery(id+"F7.wireOp",EDGE,"E1253"),sQuery(id+"F7.wireOp",EDGE,"E1254"),sQuery(id+"F7.wireOp",EDGE,"E1255"),sQuery(id+"F7.wireOp",EDGE,"E1256"),sQuery(id+"F7.wireOp",EDGE,"E1257"),sQuery(id+"F7.wireOp",EDGE,"E1258"),sQuery(id+"F7.wireOp",EDGE,"E1259"),sQuery(id+"F7.wireOp",EDGE,"E1260"),sQuery(id+"F7.wireOp",EDGE,"E1261"),sQuery(id+"F7.wireOp",EDGE,"E1262"),sQuery(id+"F7.wireOp",EDGE,"E1263"),sQuery(id+"F7.wireOp",EDGE,"E1264"),sQuery(id+"F7.wireOp",EDGE,"E1265"),sQuery(id+"F7.wireOp",EDGE,"E1266"),sQuery(id+"F7.wireOp",EDGE,"E1267"),sQuery(id+"F7.wireOp",EDGE,"E1268"),sQuery(id+"F7.wireOp",EDGE,"E1269"),sQuery(id+"F7.wireOp",EDGE,"E1270"),sQuery(id+"F7.wireOp",EDGE,"E1271"),sQuery(id+"F7.wireOp",EDGE,"E1272"),sQuery(id+"F7.wireOp",EDGE,"E1273"),sQuery(id+"F7.wireOp",EDGE,"E1274"),sQuery(id+"F7.wireOp",EDGE,"E1275"),sQuery(id+"F7.wireOp",EDGE,"E1276"),sQuery(id+"F7.wireOp",EDGE,"E1277"),sQuery(id+"F7.wireOp",EDGE,"E1278"),sQuery(id+"F7.wireOp",EDGE,"E1279"),sQuery(id+"F7.wireOp",EDGE,"E1280"),sQuery(id+"F7.wireOp",EDGE,"E1281"),sQuery(id+"F7.wireOp",EDGE,"E1282"),sQuery(id+"F7.wireOp",EDGE,"E1283"),sQuery(id+"F7.wireOp",EDGE,"E1284"),sQuery(id+"F7.wireOp",EDGE,"E1285"),sQuery(id+"F7.wireOp",EDGE,"E1286"),sQuery(id+"F7.wireOp",EDGE,"E1287"),sQuery(id+"F7.wireOp",EDGE,"E1288"),sQuery(id+"F7.wireOp",EDGE,"E1289"),sQuery(id+"F7.wireOp",EDGE,"E1290"),sQuery(id+"F7.wireOp",EDGE,"E1291"),sQuery(id+"F7.wireOp",EDGE,"E1292"),sQuery(id+"F7.wireOp",EDGE,"E1293"),sQuery(id+"F7.wireOp",EDGE,"E1294"),sQuery(id+"F7.wireOp",EDGE,"E1295"),sQuery(id+"F7.wireOp",EDGE,"E1296"),sQuery(id+"F7.wireOp",EDGE,"E1297"),sQuery(id+"F7.wireOp",EDGE,"E1298"),sQuery(id+"F7.wireOp",EDGE,"E1299"),sQuery(id+"F7.wireOp",EDGE,"E1300"),sQuery(id+"F7.wireOp",EDGE,"E1301"),sQuery(id+"F7.wireOp",EDGE,"E1302"),sQuery(id+"F7.wireOp",EDGE,"E1303"),sQuery(id+"F7.wireOp",EDGE,"E1304"),sQuery(id+"F7.wireOp",EDGE,"E1305"),sQuery(id+"F7.wireOp",EDGE,"E1306"),sQuery(id+"F7.wireOp",EDGE,"E1307"),sQuery(id+"F7.wireOp",EDGE,"E1308"),sQuery(id+"F7.wireOp",EDGE,"E1309"),sQuery(id+"F7.wireOp",EDGE,"E1310"),sQuery(id+"F7.wireOp",EDGE,"E1311"),sQuery(id+"F7.wireOp",EDGE,"E1312"),sQuery(id+"F7.wireOp",EDGE,"E1313"),sQuery(id+"F7.wireOp",EDGE,"E1314"),sQuery(id+"F7.wireOp",EDGE,"E1315"),sQuery(id+"F7.wireOp",EDGE,"E1316"),sQuery(id+"F7.wireOp",EDGE,"E1317"),sQuery(id+"F7.wireOp",EDGE,"E1318"),sQuery(id+"F7.wireOp",EDGE,"E1319"),sQuery(id+"F7.wireOp",EDGE,"E1320"),sQuery(id+"F7.wireOp",EDGE,"E1321"),sQuery(id+"F7.wireOp",EDGE,"E1322"),sQuery(id+"F7.wireOp",EDGE,"E1323"),sQuery(id+"F7.wireOp",EDGE,"E1324"),sQuery(id+"F7.wireOp",EDGE,"E1325"),sQuery(id+"F7.wireOp",EDGE,"E1326"),sQuery(id+"F7.wireOp",EDGE,"E1327"),sQuery(id+"F7.wireOp",EDGE,"E1328"),sQuery(id+"F7.wireOp",EDGE,"E1329"),sQuery(id+"F7.wireOp",EDGE,"E1330"),sQuery(id+"F7.wireOp",EDGE,"E1331"),sQuery(id+"F7.wireOp",EDGE,"E1332"),sQuery(id+"F7.wireOp",EDGE,"E1333"),sQuery(id+"F7.wireOp",EDGE,"E1334"),sQuery(id+"F7.wireOp",EDGE,"E1335"),sQuery(id+"F7.wireOp",EDGE,"E1336"),sQuery(id+"F7.wireOp",EDGE,"E1337"),sQuery(id+"F7.wireOp",EDGE,"E1338"),sQuery(id+"F7.wireOp",EDGE,"E1339"),sQuery(id+"F7.wireOp",EDGE,"E1340"),sQuery(id+"F7.wireOp",EDGE,"E1341"),sQuery(id+"F7.wireOp",EDGE,"E1342"),sQuery(id+"F7.wireOp",EDGE,"E1343"),sQuery(id+"F7.wireOp",EDGE,"E1344"),sQuery(id+"F7.wireOp",EDGE,"E1345"),sQuery(id+"F7.wireOp",EDGE,"E1346"),sQuery(id+"F7.wireOp",EDGE,"E1347"),sQuery(id+"F7.wireOp",EDGE,"E1348"),sQuery(id+"F7.wireOp",EDGE,"E1349"),sQuery(id+"F7.wireOp",EDGE,"E1350"),sQuery(id+"F7.wireOp",EDGE,"E1351"),sQuery(id+"F7.wireOp",EDGE,"E1352"),sQuery(id+"F7.wireOp",EDGE,"E1353"),sQuery(id+"F7.wireOp",EDGE,"E1354"),sQuery(id+"F7.wireOp",EDGE,"E1355"),sQuery(id+"F7.wireOp",EDGE,"E1356"),sQuery(id+"F7.wireOp",EDGE,"E1357"),sQuery(id+"F7.wireOp",EDGE,"E1358"),sQuery(id+"F7.wireOp",EDGE,"E1359"),sQuery(id+"F7.wireOp",EDGE,"E1360"),sQuery(id+"F7.wireOp",EDGE,"E1361"),sQuery(id+"F7.wireOp",EDGE,"E1362"),sQuery(id+"F7.wireOp",EDGE,"E1363"),sQuery(id+"F7.wireOp",EDGE,"E1364"),sQuery(id+"F7.wireOp",EDGE,"E1365"),sQuery(id+"F7.wireOp",EDGE,"E1366"),sQuery(id+"F7.wireOp",EDGE,"E1367"),sQuery(id+"F7.wireOp",EDGE,"E1368"),sQuery(id+"F7.wireOp",EDGE,"E1369"),sQuery(id+"F7.wireOp",EDGE,"E1370"),sQuery(id+"F7.wireOp",EDGE,"E1371"),sQuery(id+"F7.wireOp",EDGE,"E1372"),sQuery(id+"F7.wireOp",EDGE,"E1373"),sQuery(id+"F7.wireOp",EDGE,"E1374"),sQuery(id+"F7.wireOp",EDGE,"E1375"),sQuery(id+"F7.wireOp",EDGE,"E1376"),sQuery(id+"F7.wireOp",EDGE,"E1377"),sQuery(id+"F7.wireOp",EDGE,"E1378"),sQuery(id+"F7.wireOp",EDGE,"E1379"),sQuery(id+"F7.wireOp",EDGE,"E1380"),sQuery(id+"F7.wireOp",EDGE,"E1381"),sQuery(id+"F7.wireOp",EDGE,"E1382"),sQuery(id+"F7.wireOp",EDGE,"E1383"),sQuery(id+"F7.wireOp",EDGE,"E1384"),sQuery(id+"F7.wireOp",EDGE,"E1385"),sQuery(id+"F7.wireOp",EDGE,"E1386"),sQuery(id+"F7.wireOp",EDGE,"E1387"),sQuery(id+"F7.wireOp",EDGE,"E1388"),sQuery(id+"F7.wireOp",EDGE,"E1389"),sQuery(id+"F7.wireOp",EDGE,"E1390"),sQuery(id+"F7.wireOp",EDGE,"E1391"),sQuery(id+"F7.wireOp",EDGE,"E1392"),sQuery(id+"F7.wireOp",EDGE,"E1393"),sQuery(id+"F7.wireOp",EDGE,"E1394"),sQuery(id+"F7.wireOp",EDGE,"E1395"),sQuery(id+"F7.wireOp",EDGE,"E1396"),sQuery(id+"F7.wireOp",EDGE,"E1397"),sQuery(id+"F7.wireOp",EDGE,"E1398"),sQuery(id+"F7.wireOp",EDGE,"E1399"),sQuery(id+"F7.wireOp",EDGE,"E1400"),sQuery(id+"F7.wireOp",EDGE,"E1401"),sQuery(id+"F7.wireOp",EDGE,"E1402"),sQuery(id+"F7.wireOp",EDGE,"E1403"),sQuery(id+"F7.wireOp",EDGE,"E1404"),sQuery(id+"F7.wireOp",EDGE,"E1405"),sQuery(id+"F7.wireOp",EDGE,"E1406"),sQuery(id+"F7.wireOp",EDGE,"E1407"),sQuery(id+"F7.wireOp",EDGE,"E1408"),sQuery(id+"F7.wireOp",EDGE,"E1409"),sQuery(id+"F7.wireOp",EDGE,"E1410"),sQuery(id+"F7.wireOp",EDGE,"E1411"),sQuery(id+"F7.wireOp",EDGE,"E1412"),sQuery(id+"F7.wireOp",EDGE,"E1413"),sQuery(id+"F7.wireOp",EDGE,"E1414"),sQuery(id+"F7.wireOp",EDGE,"E1415"),sQuery(id+"F7.wireOp",EDGE,"E1416"),sQuery(id+"F7.wireOp",EDGE,"E1417"),sQuery(id+"F7.wireOp",EDGE,"E1418"),sQuery(id+"F7.wireOp",EDGE,"E1419"),sQuery(id+"F7.wireOp",EDGE,"E1420"),sQuery(id+"F7.wireOp",EDGE,"E1421"),sQuery(id+"F7.wireOp",EDGE,"E1422"),sQuery(id+"F7.wireOp",EDGE,"E1423"),sQuery(id+"F7.wireOp",EDGE,"E1424"),sQuery(id+"F7.wireOp",EDGE,"E1425"),sQuery(id+"F7.wireOp",EDGE,"E1426"),sQuery(id+"F7.wireOp",EDGE,"E1427"),sQuery(id+"F7.wireOp",EDGE,"E1428"),sQuery(id+"F7.wireOp",EDGE,"E1429"),sQuery(id+"F7.wireOp",EDGE,"E1430"),sQuery(id+"F7.wireOp",EDGE,"E1431"),sQuery(id+"F7.wireOp",EDGE,"E1432"),sQuery(id+"F7.wireOp",EDGE,"E1433"),sQuery(id+"F7.wireOp",EDGE,"E1434"),sQuery(id+"F7.wireOp",EDGE,"E1435"),sQuery(id+"F7.wireOp",EDGE,"E1436"),sQuery(id+"F7.wireOp",EDGE,"E1437"),sQuery(id+"F7.wireOp",EDGE,"E1438"),sQuery(id+"F7.wireOp",EDGE,"E1439"),sQuery(id+"F7.wireOp",EDGE,"E1440"),sQuery(id+"F7.wireOp",EDGE,"E1441"),sQuery(id+"F7.wireOp",EDGE,"E1442"),sQuery(id+"F7.wireOp",EDGE,"E1443"),sQuery(id+"F7.wireOp",EDGE,"E1444"),sQuery(id+"F7.wireOp",EDGE,"E1445"),sQuery(id+"F7.wireOp",EDGE,"E1446"),sQuery(id+"F7.wireOp",EDGE,"E1447"),sQuery(id+"F7.wireOp",EDGE,"E1448"),sQuery(id+"F7.wireOp",EDGE,"E1449"),sQuery(id+"F7.wireOp",EDGE,"E1450"),sQuery(id+"F7.wireOp",EDGE,"E1451"),sQuery(id+"F7.wireOp",EDGE,"E1452"),sQuery(id+"F7.wireOp",EDGE,"E1453"),sQuery(id+"F7.wireOp",EDGE,"E1454"),sQuery(id+"F7.wireOp",EDGE,"E1455"),sQuery(id+"F7.wireOp",EDGE,"E1456"),sQuery(id+"F7.wireOp",EDGE,"E1457"),sQuery(id+"F7.wireOp",EDGE,"E1458"),sQuery(id+"F7.wireOp",EDGE,"E1459"),sQuery(id+"F7.wireOp",EDGE,"E1460"),sQuery(id+"F7.wireOp",EDGE,"E1461"),sQuery(id+"F7.wireOp",EDGE,"E1462"),sQuery(id+"F7.wireOp",EDGE,"E1463"),sQuery(id+"F7.wireOp",EDGE,"E1464"),sQuery(id+"F7.wireOp",EDGE,"E1465"),sQuery(id+"F7.wireOp",EDGE,"E1466"),sQuery(id+"F7.wireOp",EDGE,"E1467"),sQuery(id+"F7.wireOp",EDGE,"E1468"),sQuery(id+"F7.wireOp",EDGE,"E1469"),sQuery(id+"F7.wireOp",EDGE,"E1470"),sQuery(id+"F7.wireOp",EDGE,"E1471"),sQuery(id+"F7.wireOp",EDGE,"E1472"),sQuery(id+"F7.wireOp",EDGE,"E1473"),sQuery(id+"F7.wireOp",EDGE,"E1474"),sQuery(id+"F7.wireOp",EDGE,"E1475"),sQuery(id+"F7.wireOp",EDGE,"E1476"),sQuery(id+"F7.wireOp",EDGE,"E1477"),sQuery(id+"F7.wireOp",EDGE,"E1478"),sQuery(id+"F7.wireOp",EDGE,"E1479"),sQuery(id+"F7.wireOp",EDGE,"E1480"),sQuery(id+"F7.wireOp",EDGE,"E1481"),sQuery(id+"F7.wireOp",EDGE,"E1482"),sQuery(id+"F7.wireOp",EDGE,"E1483"),sQuery(id+"F7.wireOp",EDGE,"E1484"),sQuery(id+"F7.wireOp",EDGE,"E1485"),sQuery(id+"F7.wireOp",EDGE,"E1486"),sQuery(id+"F7.wireOp",EDGE,"E1487"),sQuery(id+"F7.wireOp",EDGE,"E1488"),sQuery(id+"F7.wireOp",EDGE,"E1489"),sQuery(id+"F7.wireOp",EDGE,"E1490"),sQuery(id+"F7.wireOp",EDGE,"E1491"),sQuery(id+"F7.wireOp",EDGE,"E1492"),sQuery(id+"F7.wireOp",EDGE,"E1493"),sQuery(id+"F7.wireOp",EDGE,"E1494"),sQuery(id+"F7.wireOp",EDGE,"E1495"),sQuery(id+"F7.wireOp",EDGE,"E1496"),sQuery(id+"F7.wireOp",EDGE,"E1497"),sQuery(id+"F7.wireOp",EDGE,"E1498"),sQuery(id+"F7.wireOp",EDGE,"E1499"),sQuery(id+"F7.wireOp",EDGE,"E1500"),sQuery(id+"F7.wireOp",EDGE,"E1501"),sQuery(id+"F7.wireOp",EDGE,"E1502"),sQuery(id+"F7.wireOp",EDGE,"E1503"),sQuery(id+"F7.wireOp",EDGE,"E1504"),sQuery(id+"F7.wireOp",EDGE,"E1505"),sQuery(id+"F7.wireOp",EDGE,"E1506"),sQuery(id+"F7.wireOp",EDGE,"E1507"),sQuery(id+"F7.wireOp",EDGE,"E1508"),sQuery(id+"F7.wireOp",EDGE,"E1509"),sQuery(id+"F7.wireOp",EDGE,"E1510"),sQuery(id+"F7.wireOp",EDGE,"E1511"),sQuery(id+"F7.wireOp",EDGE,"E1512"),sQuery(id+"F7.wireOp",EDGE,"E1513"),sQuery(id+"F7.wireOp",EDGE,"E1514"),sQuery(id+"F7.wireOp",EDGE,"E1515"),sQuery(id+"F7.wireOp",EDGE,"E1516"),sQuery(id+"F7.wireOp",EDGE,"E1517"),sQuery(id+"F7.wireOp",EDGE,"E1518"),sQuery(id+"F7.wireOp",EDGE,"E1519"),sQuery(id+"F7.wireOp",EDGE,"E1520"),sQuery(id+"F7.wireOp",EDGE,"E1521"),sQuery(id+"F7.wireOp",EDGE,"E1522"),sQuery(id+"F7.wireOp",EDGE,"E1523"),sQuery(id+"F7.wireOp",EDGE,"E1524"),sQuery(id+"F7.wireOp",EDGE,"E1525"),sQuery(id+"F7.wireOp",EDGE,"E1526"),sQuery(id+"F7.wireOp",EDGE,"E1527"),sQuery(id+"F7.wireOp",EDGE,"E1528"),sQuery(id+"F7.wireOp",EDGE,"E1529"),sQuery(id+"F7.wireOp",EDGE,"E1530"),sQuery(id+"F7.wireOp",EDGE,"E1531"),sQuery(id+"F7.wireOp",EDGE,"E1532"),sQuery(id+"F7.wireOp",EDGE,"E1533"),sQuery(id+"F7.wireOp",EDGE,"E1534"),sQuery(id+"F7.wireOp",EDGE,"E1535"),sQuery(id+"F7.wireOp",EDGE,"E1536"),sQuery(id+"F7.wireOp",EDGE,"E1537"),sQuery(id+"F7.wireOp",EDGE,"E1538"),sQuery(id+"F7.wireOp",EDGE,"E1539"),sQuery(id+"F7.wireOp",EDGE,"E1540"),sQuery(id+"F7.wireOp",EDGE,"E1541"),sQuery(id+"F7.wireOp",EDGE,"E1542"),sQuery(id+"F7.wireOp",EDGE,"E1543"),sQuery(id+"F7.wireOp",EDGE,"E1544"),sQuery(id+"F7.wireOp",EDGE,"E1545"),sQuery(id+"F7.wireOp",EDGE,"E1546"),sQuery(id+"F7.wireOp",EDGE,"E1547"),sQuery(id+"F7.wireOp",EDGE,"E1548"),sQuery(id+"F7.wireOp",EDGE,"E1549"),sQuery(id+"F7.wireOp",EDGE,"E1550"),sQuery(id+"F7.wireOp",EDGE,"E1551"),sQuery(id+"F7.wireOp",EDGE,"E1552"),sQuery(id+"F7.wireOp",EDGE,"E1553"),sQuery(id+"F7.wireOp",EDGE,"E1554"),sQuery(id+"F7.wireOp",EDGE,"E1555"),sQuery(id+"F7.wireOp",EDGE,"E1556"),sQuery(id+"F7.wireOp",EDGE,"E1557"),sQuery(id+"F7.wireOp",EDGE,"E1558"),sQuery(id+"F7.wireOp",EDGE,"E1559"),sQuery(id+"F7.wireOp",EDGE,"E1560"),sQuery(id+"F7.wireOp",EDGE,"E1561")])]});
            var Q1;
            Q1=makeQuery(id+"F8.opExtrude","CAP_EDGE",EDGE,{"disambiguationData":[OSD([sQuery(id+"F7.wireOp",EDGE,"E1373")])],"isStart":true});
            transform(context, id + "F12", {"entities" : qUnion([Q0]), "transformType" : TransformType.TRANSLATION_DISTANCE, "transformDirection" : qUnion([Q1]), "distance" : 11.5 * mm, "oppositeDirection" : true, "makeCopy" : false});
        }
        {
            var Q0;
            Q0=makeQuery(id+"F8.opExtrude","CAP_FACE",FACE,{"disambiguationData":[OSD([sQuery(id+"F7.wireOp",EDGE,"E449"),sQuery(id+"F7.wireOp",EDGE,"E450"),sQuery(id+"F7.wireOp",EDGE,"E451"),sQuery(id+"F7.wireOp",EDGE,"E452"),sQuery(id+"F7.wireOp",EDGE,"E453"),sQuery(id+"F7.wireOp",EDGE,"E454"),sQuery(id+"F7.wireOp",EDGE,"E455"),sQuery(id+"F7.wireOp",EDGE,"E456"),sQuery(id+"F7.wireOp",EDGE,"E457"),sQuery(id+"F7.wireOp",EDGE,"E458"),sQuery(id+"F7.wireOp",EDGE,"E459"),sQuery(id+"F7.wireOp",EDGE,"E460"),sQuery(id+"F7.wireOp",EDGE,"E461"),sQuery(id+"F7.wireOp",EDGE,"E462"),sQuery(id+"F7.wireOp",EDGE,"E463"),sQuery(id+"F7.wireOp",EDGE,"E464"),sQuery(id+"F7.wireOp",EDGE,"E465"),sQuery(id+"F7.wireOp",EDGE,"E466"),sQuery(id+"F7.wireOp",EDGE,"E467"),sQuery(id+"F7.wireOp",EDGE,"E468"),sQuery(id+"F7.wireOp",EDGE,"E469"),sQuery(id+"F7.wireOp",EDGE,"E470"),sQuery(id+"F7.wireOp",EDGE,"E471"),sQuery(id+"F7.wireOp",EDGE,"E472"),sQuery(id+"F7.wireOp",EDGE,"E473"),sQuery(id+"F7.wireOp",EDGE,"E474"),sQuery(id+"F7.wireOp",EDGE,"E475"),sQuery(id+"F7.wireOp",EDGE,"E476"),sQuery(id+"F7.wireOp",EDGE,"E477"),sQuery(id+"F7.wireOp",EDGE,"E478"),sQuery(id+"F7.wireOp",EDGE,"E479"),sQuery(id+"F7.wireOp",EDGE,"E480"),sQuery(id+"F7.wireOp",EDGE,"E481"),sQuery(id+"F7.wireOp",EDGE,"E482"),sQuery(id+"F7.wireOp",EDGE,"E483"),sQuery(id+"F7.wireOp",EDGE,"E484"),sQuery(id+"F7.wireOp",EDGE,"E485"),sQuery(id+"F7.wireOp",EDGE,"E486"),sQuery(id+"F7.wireOp",EDGE,"E487"),sQuery(id+"F7.wireOp",EDGE,"E488"),sQuery(id+"F7.wireOp",EDGE,"E489"),sQuery(id+"F7.wireOp",EDGE,"E490"),sQuery(id+"F7.wireOp",EDGE,"E491"),sQuery(id+"F7.wireOp",EDGE,"E492"),sQuery(id+"F7.wireOp",EDGE,"E493"),sQuery(id+"F7.wireOp",EDGE,"E494"),sQuery(id+"F7.wireOp",EDGE,"E495"),sQuery(id+"F7.wireOp",EDGE,"E496"),sQuery(id+"F7.wireOp",EDGE,"E497"),sQuery(id+"F7.wireOp",EDGE,"E498"),sQuery(id+"F7.wireOp",EDGE,"E499"),sQuery(id+"F7.wireOp",EDGE,"E500"),sQuery(id+"F7.wireOp",EDGE,"E501"),sQuery(id+"F7.wireOp",EDGE,"E502"),sQuery(id+"F7.wireOp",EDGE,"E503"),sQuery(id+"F7.wireOp",EDGE,"E504"),sQuery(id+"F7.wireOp",EDGE,"E505"),sQuery(id+"F7.wireOp",EDGE,"E506"),sQuery(id+"F7.wireOp",EDGE,"E507"),sQuery(id+"F7.wireOp",EDGE,"E508"),sQuery(id+"F7.wireOp",EDGE,"E509"),sQuery(id+"F7.wireOp",EDGE,"E510"),sQuery(id+"F7.wireOp",EDGE,"E511"),sQuery(id+"F7.wireOp",EDGE,"E512"),sQuery(id+"F7.wireOp",EDGE,"E513"),sQuery(id+"F7.wireOp",EDGE,"E514"),sQuery(id+"F7.wireOp",EDGE,"E515"),sQuery(id+"F7.wireOp",EDGE,"E516"),sQuery(id+"F7.wireOp",EDGE,"E517"),sQuery(id+"F7.wireOp",EDGE,"E518"),sQuery(id+"F7.wireOp",EDGE,"E519"),sQuery(id+"F7.wireOp",EDGE,"E520"),sQuery(id+"F7.wireOp",EDGE,"E521"),sQuery(id+"F7.wireOp",EDGE,"E522"),sQuery(id+"F7.wireOp",EDGE,"E523"),sQuery(id+"F7.wireOp",EDGE,"E524"),sQuery(id+"F7.wireOp",EDGE,"E525"),sQuery(id+"F7.wireOp",EDGE,"E526"),sQuery(id+"F7.wireOp",EDGE,"E527"),sQuery(id+"F7.wireOp",EDGE,"E528"),sQuery(id+"F7.wireOp",EDGE,"E529"),sQuery(id+"F7.wireOp",EDGE,"E530"),sQuery(id+"F7.wireOp",EDGE,"E531"),sQuery(id+"F7.wireOp",EDGE,"E532"),sQuery(id+"F7.wireOp",EDGE,"E533"),sQuery(id+"F7.wireOp",EDGE,"E534"),sQuery(id+"F7.wireOp",EDGE,"E535"),sQuery(id+"F7.wireOp",EDGE,"E536"),sQuery(id+"F7.wireOp",EDGE,"E537"),sQuery(id+"F7.wireOp",EDGE,"E538"),sQuery(id+"F7.wireOp",EDGE,"E539"),sQuery(id+"F7.wireOp",EDGE,"E540"),sQuery(id+"F7.wireOp",EDGE,"E541"),sQuery(id+"F7.wireOp",EDGE,"E542"),sQuery(id+"F7.wireOp",EDGE,"E543"),sQuery(id+"F7.wireOp",EDGE,"E544"),sQuery(id+"F7.wireOp",EDGE,"E545"),sQuery(id+"F7.wireOp",EDGE,"E546"),sQuery(id+"F7.wireOp",EDGE,"E547"),sQuery(id+"F7.wireOp",EDGE,"E548"),sQuery(id+"F7.wireOp",EDGE,"E549"),sQuery(id+"F7.wireOp",EDGE,"E550"),sQuery(id+"F7.wireOp",EDGE,"E551"),sQuery(id+"F7.wireOp",EDGE,"E552"),sQuery(id+"F7.wireOp",EDGE,"E553"),sQuery(id+"F7.wireOp",EDGE,"E554"),sQuery(id+"F7.wireOp",EDGE,"E555"),sQuery(id+"F7.wireOp",EDGE,"E556"),sQuery(id+"F7.wireOp",EDGE,"E557"),sQuery(id+"F7.wireOp",EDGE,"E558"),sQuery(id+"F7.wireOp",EDGE,"E559"),sQuery(id+"F7.wireOp",EDGE,"E560"),sQuery(id+"F7.wireOp",EDGE,"E561"),sQuery(id+"F7.wireOp",EDGE,"E562"),sQuery(id+"F7.wireOp",EDGE,"E563"),sQuery(id+"F7.wireOp",EDGE,"E564"),sQuery(id+"F7.wireOp",EDGE,"E565"),sQuery(id+"F7.wireOp",EDGE,"E566"),sQuery(id+"F7.wireOp",EDGE,"E567"),sQuery(id+"F7.wireOp",EDGE,"E568"),sQuery(id+"F7.wireOp",EDGE,"E569"),sQuery(id+"F7.wireOp",EDGE,"E570"),sQuery(id+"F7.wireOp",EDGE,"E571"),sQuery(id+"F7.wireOp",EDGE,"E572"),sQuery(id+"F7.wireOp",EDGE,"E573"),sQuery(id+"F7.wireOp",EDGE,"E574"),sQuery(id+"F7.wireOp",EDGE,"E575"),sQuery(id+"F7.wireOp",EDGE,"E576"),sQuery(id+"F7.wireOp",EDGE,"E577"),sQuery(id+"F7.wireOp",EDGE,"E578"),sQuery(id+"F7.wireOp",EDGE,"E579"),sQuery(id+"F7.wireOp",EDGE,"E580"),sQuery(id+"F7.wireOp",EDGE,"E581"),sQuery(id+"F7.wireOp",EDGE,"E582"),sQuery(id+"F7.wireOp",EDGE,"E583"),sQuery(id+"F7.wireOp",EDGE,"E584"),sQuery(id+"F7.wireOp",EDGE,"E585"),sQuery(id+"F7.wireOp",EDGE,"E586"),sQuery(id+"F7.wireOp",EDGE,"E587"),sQuery(id+"F7.wireOp",EDGE,"E588"),sQuery(id+"F7.wireOp",EDGE,"E589"),sQuery(id+"F7.wireOp",EDGE,"E590"),sQuery(id+"F7.wireOp",EDGE,"E591"),sQuery(id+"F7.wireOp",EDGE,"E592"),sQuery(id+"F7.wireOp",EDGE,"E593"),sQuery(id+"F7.wireOp",EDGE,"E594"),sQuery(id+"F7.wireOp",EDGE,"E595"),sQuery(id+"F7.wireOp",EDGE,"E596"),sQuery(id+"F7.wireOp",EDGE,"E597"),sQuery(id+"F7.wireOp",EDGE,"E598"),sQuery(id+"F7.wireOp",EDGE,"E599"),sQuery(id+"F7.wireOp",EDGE,"E600"),sQuery(id+"F7.wireOp",EDGE,"E601"),sQuery(id+"F7.wireOp",EDGE,"E602"),sQuery(id+"F7.wireOp",EDGE,"E603"),sQuery(id+"F7.wireOp",EDGE,"E604"),sQuery(id+"F7.wireOp",EDGE,"E605"),sQuery(id+"F7.wireOp",EDGE,"E606"),sQuery(id+"F7.wireOp",EDGE,"E607"),sQuery(id+"F7.wireOp",EDGE,"E608"),sQuery(id+"F7.wireOp",EDGE,"E609"),sQuery(id+"F7.wireOp",EDGE,"E610"),sQuery(id+"F7.wireOp",EDGE,"E611"),sQuery(id+"F7.wireOp",EDGE,"E612"),sQuery(id+"F7.wireOp",EDGE,"E613"),sQuery(id+"F7.wireOp",EDGE,"E614"),sQuery(id+"F7.wireOp",EDGE,"E615"),sQuery(id+"F7.wireOp",EDGE,"E616"),sQuery(id+"F7.wireOp",EDGE,"E617"),sQuery(id+"F7.wireOp",EDGE,"E618"),sQuery(id+"F7.wireOp",EDGE,"E619"),sQuery(id+"F7.wireOp",EDGE,"E620"),sQuery(id+"F7.wireOp",EDGE,"E621"),sQuery(id+"F7.wireOp",EDGE,"E622"),sQuery(id+"F7.wireOp",EDGE,"E623"),sQuery(id+"F7.wireOp",EDGE,"E624"),sQuery(id+"F7.wireOp",EDGE,"E625"),sQuery(id+"F7.wireOp",EDGE,"E626"),sQuery(id+"F7.wireOp",EDGE,"E627"),sQuery(id+"F7.wireOp",EDGE,"E628"),sQuery(id+"F7.wireOp",EDGE,"E629"),sQuery(id+"F7.wireOp",EDGE,"E630"),sQuery(id+"F7.wireOp",EDGE,"E631"),sQuery(id+"F7.wireOp",EDGE,"E632"),sQuery(id+"F7.wireOp",EDGE,"E633"),sQuery(id+"F7.wireOp",EDGE,"E634"),sQuery(id+"F7.wireOp",EDGE,"E635"),sQuery(id+"F7.wireOp",EDGE,"E636"),sQuery(id+"F7.wireOp",EDGE,"E637"),sQuery(id+"F7.wireOp",EDGE,"E638"),sQuery(id+"F7.wireOp",EDGE,"E639"),sQuery(id+"F7.wireOp",EDGE,"E640"),sQuery(id+"F7.wireOp",EDGE,"E641"),sQuery(id+"F7.wireOp",EDGE,"E642"),sQuery(id+"F7.wireOp",EDGE,"E643"),sQuery(id+"F7.wireOp",EDGE,"E644"),sQuery(id+"F7.wireOp",EDGE,"E645"),sQuery(id+"F7.wireOp",EDGE,"E646"),sQuery(id+"F7.wireOp",EDGE,"E647"),sQuery(id+"F7.wireOp",EDGE,"E648"),sQuery(id+"F7.wireOp",EDGE,"E649"),sQuery(id+"F7.wireOp",EDGE,"E650"),sQuery(id+"F7.wireOp",EDGE,"E651"),sQuery(id+"F7.wireOp",EDGE,"E652"),sQuery(id+"F7.wireOp",EDGE,"E653"),sQuery(id+"F7.wireOp",EDGE,"E654"),sQuery(id+"F7.wireOp",EDGE,"E655"),sQuery(id+"F7.wireOp",EDGE,"E656"),sQuery(id+"F7.wireOp",EDGE,"E657"),sQuery(id+"F7.wireOp",EDGE,"E658"),sQuery(id+"F7.wireOp",EDGE,"E659"),sQuery(id+"F7.wireOp",EDGE,"E660"),sQuery(id+"F7.wireOp",EDGE,"E661"),sQuery(id+"F7.wireOp",EDGE,"E662"),sQuery(id+"F7.wireOp",EDGE,"E663"),sQuery(id+"F7.wireOp",EDGE,"E664"),sQuery(id+"F7.wireOp",EDGE,"E665"),sQuery(id+"F7.wireOp",EDGE,"E666"),sQuery(id+"F7.wireOp",EDGE,"E667"),sQuery(id+"F7.wireOp",EDGE,"E668"),sQuery(id+"F7.wireOp",EDGE,"E669"),sQuery(id+"F7.wireOp",EDGE,"E670"),sQuery(id+"F7.wireOp",EDGE,"E671"),sQuery(id+"F7.wireOp",EDGE,"E672"),sQuery(id+"F7.wireOp",EDGE,"E673"),sQuery(id+"F7.wireOp",EDGE,"E674"),sQuery(id+"F7.wireOp",EDGE,"E675"),sQuery(id+"F7.wireOp",EDGE,"E676"),sQuery(id+"F7.wireOp",EDGE,"E677"),sQuery(id+"F7.wireOp",EDGE,"E678"),sQuery(id+"F7.wireOp",EDGE,"E679"),sQuery(id+"F7.wireOp",EDGE,"E680"),sQuery(id+"F7.wireOp",EDGE,"E681"),sQuery(id+"F7.wireOp",EDGE,"E682"),sQuery(id+"F7.wireOp",EDGE,"E683"),sQuery(id+"F7.wireOp",EDGE,"E684"),sQuery(id+"F7.wireOp",EDGE,"E685"),sQuery(id+"F7.wireOp",EDGE,"E686"),sQuery(id+"F7.wireOp",EDGE,"E687"),sQuery(id+"F7.wireOp",EDGE,"E688"),sQuery(id+"F7.wireOp",EDGE,"E689"),sQuery(id+"F7.wireOp",EDGE,"E690"),sQuery(id+"F7.wireOp",EDGE,"E691"),sQuery(id+"F7.wireOp",EDGE,"E692"),sQuery(id+"F7.wireOp",EDGE,"E693"),sQuery(id+"F7.wireOp",EDGE,"E694"),sQuery(id+"F7.wireOp",EDGE,"E695"),sQuery(id+"F7.wireOp",EDGE,"E696"),sQuery(id+"F7.wireOp",EDGE,"E697"),sQuery(id+"F7.wireOp",EDGE,"E698"),sQuery(id+"F7.wireOp",EDGE,"E699"),sQuery(id+"F7.wireOp",EDGE,"E700"),sQuery(id+"F7.wireOp",EDGE,"E701"),sQuery(id+"F7.wireOp",EDGE,"E702"),sQuery(id+"F7.wireOp",EDGE,"E703"),sQuery(id+"F7.wireOp",EDGE,"E704"),sQuery(id+"F7.wireOp",EDGE,"E705"),sQuery(id+"F7.wireOp",EDGE,"E706"),sQuery(id+"F7.wireOp",EDGE,"E707"),sQuery(id+"F7.wireOp",EDGE,"E708"),sQuery(id+"F7.wireOp",EDGE,"E709"),sQuery(id+"F7.wireOp",EDGE,"E710"),sQuery(id+"F7.wireOp",EDGE,"E711"),sQuery(id+"F7.wireOp",EDGE,"E712"),sQuery(id+"F7.wireOp",EDGE,"E713"),sQuery(id+"F7.wireOp",EDGE,"E714"),sQuery(id+"F7.wireOp",EDGE,"E715"),sQuery(id+"F7.wireOp",EDGE,"E716"),sQuery(id+"F7.wireOp",EDGE,"E717"),sQuery(id+"F7.wireOp",EDGE,"E718"),sQuery(id+"F7.wireOp",EDGE,"E719"),sQuery(id+"F7.wireOp",EDGE,"E720"),sQuery(id+"F7.wireOp",EDGE,"E721"),sQuery(id+"F7.wireOp",EDGE,"E722"),sQuery(id+"F7.wireOp",EDGE,"E723"),sQuery(id+"F7.wireOp",EDGE,"E724"),sQuery(id+"F7.wireOp",EDGE,"E725"),sQuery(id+"F7.wireOp",EDGE,"E726"),sQuery(id+"F7.wireOp",EDGE,"E727"),sQuery(id+"F7.wireOp",EDGE,"E728"),sQuery(id+"F7.wireOp",EDGE,"E729"),sQuery(id+"F7.wireOp",EDGE,"E730"),sQuery(id+"F7.wireOp",EDGE,"E731"),sQuery(id+"F7.wireOp",EDGE,"E732"),sQuery(id+"F7.wireOp",EDGE,"E733"),sQuery(id+"F7.wireOp",EDGE,"E734"),sQuery(id+"F7.wireOp",EDGE,"E735"),sQuery(id+"F7.wireOp",EDGE,"E736"),sQuery(id+"F7.wireOp",EDGE,"E737"),sQuery(id+"F7.wireOp",EDGE,"E738"),sQuery(id+"F7.wireOp",EDGE,"E739"),sQuery(id+"F7.wireOp",EDGE,"E740"),sQuery(id+"F7.wireOp",EDGE,"E741"),sQuery(id+"F7.wireOp",EDGE,"E742"),sQuery(id+"F7.wireOp",EDGE,"E743"),sQuery(id+"F7.wireOp",EDGE,"E744"),sQuery(id+"F7.wireOp",EDGE,"E745"),sQuery(id+"F7.wireOp",EDGE,"E746"),sQuery(id+"F7.wireOp",EDGE,"E747"),sQuery(id+"F7.wireOp",EDGE,"E748"),sQuery(id+"F7.wireOp",EDGE,"E749"),sQuery(id+"F7.wireOp",EDGE,"E750"),sQuery(id+"F7.wireOp",EDGE,"E751"),sQuery(id+"F7.wireOp",EDGE,"E752"),sQuery(id+"F7.wireOp",EDGE,"E753"),sQuery(id+"F7.wireOp",EDGE,"E754"),sQuery(id+"F7.wireOp",EDGE,"E755"),sQuery(id+"F7.wireOp",EDGE,"E756"),sQuery(id+"F7.wireOp",EDGE,"E757"),sQuery(id+"F7.wireOp",EDGE,"E758"),sQuery(id+"F7.wireOp",EDGE,"E759"),sQuery(id+"F7.wireOp",EDGE,"E760"),sQuery(id+"F7.wireOp",EDGE,"E761"),sQuery(id+"F7.wireOp",EDGE,"E762"),sQuery(id+"F7.wireOp",EDGE,"E763"),sQuery(id+"F7.wireOp",EDGE,"E764"),sQuery(id+"F7.wireOp",EDGE,"E765"),sQuery(id+"F7.wireOp",EDGE,"E766"),sQuery(id+"F7.wireOp",EDGE,"E767"),sQuery(id+"F7.wireOp",EDGE,"E768"),sQuery(id+"F7.wireOp",EDGE,"E769"),sQuery(id+"F7.wireOp",EDGE,"E770"),sQuery(id+"F7.wireOp",EDGE,"E771"),sQuery(id+"F7.wireOp",EDGE,"E772"),sQuery(id+"F7.wireOp",EDGE,"E773"),sQuery(id+"F7.wireOp",EDGE,"E774"),sQuery(id+"F7.wireOp",EDGE,"E775"),sQuery(id+"F7.wireOp",EDGE,"E776"),sQuery(id+"F7.wireOp",EDGE,"E777"),sQuery(id+"F7.wireOp",EDGE,"E778"),sQuery(id+"F7.wireOp",EDGE,"E779"),sQuery(id+"F7.wireOp",EDGE,"E780"),sQuery(id+"F7.wireOp",EDGE,"E781"),sQuery(id+"F7.wireOp",EDGE,"E782"),sQuery(id+"F7.wireOp",EDGE,"E783"),sQuery(id+"F7.wireOp",EDGE,"E784"),sQuery(id+"F7.wireOp",EDGE,"E785"),sQuery(id+"F7.wireOp",EDGE,"E786"),sQuery(id+"F7.wireOp",EDGE,"E787"),sQuery(id+"F7.wireOp",EDGE,"E788"),sQuery(id+"F7.wireOp",EDGE,"E789"),sQuery(id+"F7.wireOp",EDGE,"E790"),sQuery(id+"F7.wireOp",EDGE,"E791"),sQuery(id+"F7.wireOp",EDGE,"E792"),sQuery(id+"F7.wireOp",EDGE,"E793"),sQuery(id+"F7.wireOp",EDGE,"E794"),sQuery(id+"F7.wireOp",EDGE,"E795"),sQuery(id+"F7.wireOp",EDGE,"E796"),sQuery(id+"F7.wireOp",EDGE,"E797"),sQuery(id+"F7.wireOp",EDGE,"E798"),sQuery(id+"F7.wireOp",EDGE,"E799"),sQuery(id+"F7.wireOp",EDGE,"E800"),sQuery(id+"F7.wireOp",EDGE,"E801"),sQuery(id+"F7.wireOp",EDGE,"E802"),sQuery(id+"F7.wireOp",EDGE,"E803"),sQuery(id+"F7.wireOp",EDGE,"E804"),sQuery(id+"F7.wireOp",EDGE,"E805"),sQuery(id+"F7.wireOp",EDGE,"E806"),sQuery(id+"F7.wireOp",EDGE,"E807"),sQuery(id+"F7.wireOp",EDGE,"E808"),sQuery(id+"F7.wireOp",EDGE,"E809"),sQuery(id+"F7.wireOp",EDGE,"E810"),sQuery(id+"F7.wireOp",EDGE,"E811"),sQuery(id+"F7.wireOp",EDGE,"E812"),sQuery(id+"F7.wireOp",EDGE,"E813"),sQuery(id+"F7.wireOp",EDGE,"E814"),sQuery(id+"F7.wireOp",EDGE,"E815"),sQuery(id+"F7.wireOp",EDGE,"E816"),sQuery(id+"F7.wireOp",EDGE,"E817"),sQuery(id+"F7.wireOp",EDGE,"E818"),sQuery(id+"F7.wireOp",EDGE,"E819"),sQuery(id+"F7.wireOp",EDGE,"E820"),sQuery(id+"F7.wireOp",EDGE,"E821"),sQuery(id+"F7.wireOp",EDGE,"E822"),sQuery(id+"F7.wireOp",EDGE,"E823"),sQuery(id+"F7.wireOp",EDGE,"E824"),sQuery(id+"F7.wireOp",EDGE,"E825"),sQuery(id+"F7.wireOp",EDGE,"E826"),sQuery(id+"F7.wireOp",EDGE,"E827"),sQuery(id+"F7.wireOp",EDGE,"E828"),sQuery(id+"F7.wireOp",EDGE,"E829"),sQuery(id+"F7.wireOp",EDGE,"E830"),sQuery(id+"F7.wireOp",EDGE,"E831"),sQuery(id+"F7.wireOp",EDGE,"E832"),sQuery(id+"F7.wireOp",EDGE,"E833"),sQuery(id+"F7.wireOp",EDGE,"E834"),sQuery(id+"F7.wireOp",EDGE,"E835"),sQuery(id+"F7.wireOp",EDGE,"E836"),sQuery(id+"F7.wireOp",EDGE,"E837"),sQuery(id+"F7.wireOp",EDGE,"E838"),sQuery(id+"F7.wireOp",EDGE,"E839"),sQuery(id+"F7.wireOp",EDGE,"E840"),sQuery(id+"F7.wireOp",EDGE,"E841"),sQuery(id+"F7.wireOp",EDGE,"E842"),sQuery(id+"F7.wireOp",EDGE,"E843"),sQuery(id+"F7.wireOp",EDGE,"E844"),sQuery(id+"F7.wireOp",EDGE,"E845"),sQuery(id+"F7.wireOp",EDGE,"E846"),sQuery(id+"F7.wireOp",EDGE,"E847"),sQuery(id+"F7.wireOp",EDGE,"E848"),sQuery(id+"F7.wireOp",EDGE,"E849"),sQuery(id+"F7.wireOp",EDGE,"E850"),sQuery(id+"F7.wireOp",EDGE,"E851"),sQuery(id+"F7.wireOp",EDGE,"E852"),sQuery(id+"F7.wireOp",EDGE,"E853"),sQuery(id+"F7.wireOp",EDGE,"E854"),sQuery(id+"F7.wireOp",EDGE,"E855"),sQuery(id+"F7.wireOp",EDGE,"E856"),sQuery(id+"F7.wireOp",EDGE,"E857"),sQuery(id+"F7.wireOp",EDGE,"E858"),sQuery(id+"F7.wireOp",EDGE,"E859"),sQuery(id+"F7.wireOp",EDGE,"E860"),sQuery(id+"F7.wireOp",EDGE,"E861"),sQuery(id+"F7.wireOp",EDGE,"E862"),sQuery(id+"F7.wireOp",EDGE,"E863"),sQuery(id+"F7.wireOp",EDGE,"E864"),sQuery(id+"F7.wireOp",EDGE,"E865"),sQuery(id+"F7.wireOp",EDGE,"E866"),sQuery(id+"F7.wireOp",EDGE,"E867"),sQuery(id+"F7.wireOp",EDGE,"E868"),sQuery(id+"F7.wireOp",EDGE,"E869"),sQuery(id+"F7.wireOp",EDGE,"E870"),sQuery(id+"F7.wireOp",EDGE,"E871"),sQuery(id+"F7.wireOp",EDGE,"E872"),sQuery(id+"F7.wireOp",EDGE,"E873"),sQuery(id+"F7.wireOp",EDGE,"E874"),sQuery(id+"F7.wireOp",EDGE,"E875"),sQuery(id+"F7.wireOp",EDGE,"E876"),sQuery(id+"F7.wireOp",EDGE,"E877"),sQuery(id+"F7.wireOp",EDGE,"E878"),sQuery(id+"F7.wireOp",EDGE,"E879"),sQuery(id+"F7.wireOp",EDGE,"E880"),sQuery(id+"F7.wireOp",EDGE,"E881"),sQuery(id+"F7.wireOp",EDGE,"E882"),sQuery(id+"F7.wireOp",EDGE,"E883"),sQuery(id+"F7.wireOp",EDGE,"E884"),sQuery(id+"F7.wireOp",EDGE,"E885"),sQuery(id+"F7.wireOp",EDGE,"E886"),sQuery(id+"F7.wireOp",EDGE,"E887"),sQuery(id+"F7.wireOp",EDGE,"E888"),sQuery(id+"F7.wireOp",EDGE,"E889"),sQuery(id+"F7.wireOp",EDGE,"E890"),sQuery(id+"F7.wireOp",EDGE,"E891"),sQuery(id+"F7.wireOp",EDGE,"E892"),sQuery(id+"F7.wireOp",EDGE,"E893"),sQuery(id+"F7.wireOp",EDGE,"E894"),sQuery(id+"F7.wireOp",EDGE,"E895"),sQuery(id+"F7.wireOp",EDGE,"E896"),sQuery(id+"F7.wireOp",EDGE,"E897"),sQuery(id+"F7.wireOp",EDGE,"E898"),sQuery(id+"F7.wireOp",EDGE,"E899"),sQuery(id+"F7.wireOp",EDGE,"E900"),sQuery(id+"F7.wireOp",EDGE,"E901"),sQuery(id+"F7.wireOp",EDGE,"E902"),sQuery(id+"F7.wireOp",EDGE,"E903"),sQuery(id+"F7.wireOp",EDGE,"E904"),sQuery(id+"F7.wireOp",EDGE,"E905"),sQuery(id+"F7.wireOp",EDGE,"E906"),sQuery(id+"F7.wireOp",EDGE,"E907"),sQuery(id+"F7.wireOp",EDGE,"E908"),sQuery(id+"F7.wireOp",EDGE,"E909"),sQuery(id+"F7.wireOp",EDGE,"E910"),sQuery(id+"F7.wireOp",EDGE,"E911"),sQuery(id+"F7.wireOp",EDGE,"E912"),sQuery(id+"F7.wireOp",EDGE,"E913"),sQuery(id+"F7.wireOp",EDGE,"E914"),sQuery(id+"F7.wireOp",EDGE,"E915"),sQuery(id+"F7.wireOp",EDGE,"E916"),sQuery(id+"F7.wireOp",EDGE,"E917"),sQuery(id+"F7.wireOp",EDGE,"E918"),sQuery(id+"F7.wireOp",EDGE,"E919"),sQuery(id+"F7.wireOp",EDGE,"E920"),sQuery(id+"F7.wireOp",EDGE,"E921"),sQuery(id+"F7.wireOp",EDGE,"E922"),sQuery(id+"F7.wireOp",EDGE,"E923"),sQuery(id+"F7.wireOp",EDGE,"E924"),sQuery(id+"F7.wireOp",EDGE,"E925"),sQuery(id+"F7.wireOp",EDGE,"E926"),sQuery(id+"F7.wireOp",EDGE,"E927"),sQuery(id+"F7.wireOp",EDGE,"E928"),sQuery(id+"F7.wireOp",EDGE,"E929"),sQuery(id+"F7.wireOp",EDGE,"E930"),sQuery(id+"F7.wireOp",EDGE,"E931"),sQuery(id+"F7.wireOp",EDGE,"E932"),sQuery(id+"F7.wireOp",EDGE,"E933"),sQuery(id+"F7.wireOp",EDGE,"E934"),sQuery(id+"F7.wireOp",EDGE,"E935"),sQuery(id+"F7.wireOp",EDGE,"E936"),sQuery(id+"F7.wireOp",EDGE,"E937"),sQuery(id+"F7.wireOp",EDGE,"E938"),sQuery(id+"F7.wireOp",EDGE,"E939"),sQuery(id+"F7.wireOp",EDGE,"E940"),sQuery(id+"F7.wireOp",EDGE,"E941"),sQuery(id+"F7.wireOp",EDGE,"E942"),sQuery(id+"F7.wireOp",EDGE,"E943"),sQuery(id+"F7.wireOp",EDGE,"E944"),sQuery(id+"F7.wireOp",EDGE,"E945"),sQuery(id+"F7.wireOp",EDGE,"E946"),sQuery(id+"F7.wireOp",EDGE,"E947"),sQuery(id+"F7.wireOp",EDGE,"E948"),sQuery(id+"F7.wireOp",EDGE,"E949"),sQuery(id+"F7.wireOp",EDGE,"E950"),sQuery(id+"F7.wireOp",EDGE,"E951"),sQuery(id+"F7.wireOp",EDGE,"E952"),sQuery(id+"F7.wireOp",EDGE,"E953"),sQuery(id+"F7.wireOp",EDGE,"E954"),sQuery(id+"F7.wireOp",EDGE,"E955"),sQuery(id+"F7.wireOp",EDGE,"E956"),sQuery(id+"F7.wireOp",EDGE,"E957"),sQuery(id+"F7.wireOp",EDGE,"E958"),sQuery(id+"F7.wireOp",EDGE,"E959"),sQuery(id+"F7.wireOp",EDGE,"E960"),sQuery(id+"F7.wireOp",EDGE,"E961"),sQuery(id+"F7.wireOp",EDGE,"E962"),sQuery(id+"F7.wireOp",EDGE,"E963"),sQuery(id+"F7.wireOp",EDGE,"E964"),sQuery(id+"F7.wireOp",EDGE,"E965"),sQuery(id+"F7.wireOp",EDGE,"E966"),sQuery(id+"F7.wireOp",EDGE,"E967"),sQuery(id+"F7.wireOp",EDGE,"E968"),sQuery(id+"F7.wireOp",EDGE,"E969"),sQuery(id+"F7.wireOp",EDGE,"E970"),sQuery(id+"F7.wireOp",EDGE,"E971"),sQuery(id+"F7.wireOp",EDGE,"E972"),sQuery(id+"F7.wireOp",EDGE,"E973"),sQuery(id+"F7.wireOp",EDGE,"E974"),sQuery(id+"F7.wireOp",EDGE,"E975"),sQuery(id+"F7.wireOp",EDGE,"E976"),sQuery(id+"F7.wireOp",EDGE,"E977"),sQuery(id+"F7.wireOp",EDGE,"E978"),sQuery(id+"F7.wireOp",EDGE,"E979"),sQuery(id+"F7.wireOp",EDGE,"E980"),sQuery(id+"F7.wireOp",EDGE,"E981"),sQuery(id+"F7.wireOp",EDGE,"E982"),sQuery(id+"F7.wireOp",EDGE,"E983"),sQuery(id+"F7.wireOp",EDGE,"E984"),sQuery(id+"F7.wireOp",EDGE,"E985"),sQuery(id+"F7.wireOp",EDGE,"E986"),sQuery(id+"F7.wireOp",EDGE,"E987"),sQuery(id+"F7.wireOp",EDGE,"E988"),sQuery(id+"F7.wireOp",EDGE,"E989"),sQuery(id+"F7.wireOp",EDGE,"E990"),sQuery(id+"F7.wireOp",EDGE,"E991"),sQuery(id+"F7.wireOp",EDGE,"E992"),sQuery(id+"F7.wireOp",EDGE,"E993"),sQuery(id+"F7.wireOp",EDGE,"E994"),sQuery(id+"F7.wireOp",EDGE,"E995"),sQuery(id+"F7.wireOp",EDGE,"E996"),sQuery(id+"F7.wireOp",EDGE,"E997"),sQuery(id+"F7.wireOp",EDGE,"E998"),sQuery(id+"F7.wireOp",EDGE,"E999"),sQuery(id+"F7.wireOp",EDGE,"E1000"),sQuery(id+"F7.wireOp",EDGE,"E1001"),sQuery(id+"F7.wireOp",EDGE,"E1002"),sQuery(id+"F7.wireOp",EDGE,"E1003"),sQuery(id+"F7.wireOp",EDGE,"E1004"),sQuery(id+"F7.wireOp",EDGE,"E1005"),sQuery(id+"F7.wireOp",EDGE,"E1006"),sQuery(id+"F7.wireOp",EDGE,"E1007"),sQuery(id+"F7.wireOp",EDGE,"E1008"),sQuery(id+"F7.wireOp",EDGE,"E1009"),sQuery(id+"F7.wireOp",EDGE,"E1010"),sQuery(id+"F7.wireOp",EDGE,"E1011"),sQuery(id+"F7.wireOp",EDGE,"E1012"),sQuery(id+"F7.wireOp",EDGE,"E1013"),sQuery(id+"F7.wireOp",EDGE,"E1014"),sQuery(id+"F7.wireOp",EDGE,"E1015"),sQuery(id+"F7.wireOp",EDGE,"E1016"),sQuery(id+"F7.wireOp",EDGE,"E1017"),sQuery(id+"F7.wireOp",EDGE,"E1018"),sQuery(id+"F7.wireOp",EDGE,"E1019"),sQuery(id+"F7.wireOp",EDGE,"E1020"),sQuery(id+"F7.wireOp",EDGE,"E1021"),sQuery(id+"F7.wireOp",EDGE,"E1022"),sQuery(id+"F7.wireOp",EDGE,"E1023"),sQuery(id+"F7.wireOp",EDGE,"E1024"),sQuery(id+"F7.wireOp",EDGE,"E1025"),sQuery(id+"F7.wireOp",EDGE,"E1026"),sQuery(id+"F7.wireOp",EDGE,"E1027"),sQuery(id+"F7.wireOp",EDGE,"E1028"),sQuery(id+"F7.wireOp",EDGE,"E1029"),sQuery(id+"F7.wireOp",EDGE,"E1030"),sQuery(id+"F7.wireOp",EDGE,"E1031"),sQuery(id+"F7.wireOp",EDGE,"E1032"),sQuery(id+"F7.wireOp",EDGE,"E1033"),sQuery(id+"F7.wireOp",EDGE,"E1034"),sQuery(id+"F7.wireOp",EDGE,"E1035"),sQuery(id+"F7.wireOp",EDGE,"E1036"),sQuery(id+"F7.wireOp",EDGE,"E1037"),sQuery(id+"F7.wireOp",EDGE,"E1038"),sQuery(id+"F7.wireOp",EDGE,"E1039"),sQuery(id+"F7.wireOp",EDGE,"E1040"),sQuery(id+"F7.wireOp",EDGE,"E1041"),sQuery(id+"F7.wireOp",EDGE,"E1042"),sQuery(id+"F7.wireOp",EDGE,"E1043"),sQuery(id+"F7.wireOp",EDGE,"E1044"),sQuery(id+"F7.wireOp",EDGE,"E1045"),sQuery(id+"F7.wireOp",EDGE,"E1046"),sQuery(id+"F7.wireOp",EDGE,"E1047"),sQuery(id+"F7.wireOp",EDGE,"E1048"),sQuery(id+"F7.wireOp",EDGE,"E1049"),sQuery(id+"F7.wireOp",EDGE,"E1050"),sQuery(id+"F7.wireOp",EDGE,"E1051"),sQuery(id+"F7.wireOp",EDGE,"E1052"),sQuery(id+"F7.wireOp",EDGE,"E1053"),sQuery(id+"F7.wireOp",EDGE,"E1054"),sQuery(id+"F7.wireOp",EDGE,"E1055"),sQuery(id+"F7.wireOp",EDGE,"E1056"),sQuery(id+"F7.wireOp",EDGE,"E1057"),sQuery(id+"F7.wireOp",EDGE,"E1058"),sQuery(id+"F7.wireOp",EDGE,"E1059"),sQuery(id+"F7.wireOp",EDGE,"E1060"),sQuery(id+"F7.wireOp",EDGE,"E1061"),sQuery(id+"F7.wireOp",EDGE,"E1062"),sQuery(id+"F7.wireOp",EDGE,"E1063"),sQuery(id+"F7.wireOp",EDGE,"E1064"),sQuery(id+"F7.wireOp",EDGE,"E1065"),sQuery(id+"F7.wireOp",EDGE,"E1066"),sQuery(id+"F7.wireOp",EDGE,"E1067"),sQuery(id+"F7.wireOp",EDGE,"E1068"),sQuery(id+"F7.wireOp",EDGE,"E1069"),sQuery(id+"F7.wireOp",EDGE,"E1070"),sQuery(id+"F7.wireOp",EDGE,"E1071"),sQuery(id+"F7.wireOp",EDGE,"E1072"),sQuery(id+"F7.wireOp",EDGE,"E1073"),sQuery(id+"F7.wireOp",EDGE,"E1074"),sQuery(id+"F7.wireOp",EDGE,"E1075"),sQuery(id+"F7.wireOp",EDGE,"E1076"),sQuery(id+"F7.wireOp",EDGE,"E1077"),sQuery(id+"F7.wireOp",EDGE,"E1078"),sQuery(id+"F7.wireOp",EDGE,"E1079"),sQuery(id+"F7.wireOp",EDGE,"E1080"),sQuery(id+"F7.wireOp",EDGE,"E1081"),sQuery(id+"F7.wireOp",EDGE,"E1082"),sQuery(id+"F7.wireOp",EDGE,"E1083"),sQuery(id+"F7.wireOp",EDGE,"E1084"),sQuery(id+"F7.wireOp",EDGE,"E1085"),sQuery(id+"F7.wireOp",EDGE,"E1086"),sQuery(id+"F7.wireOp",EDGE,"E1087"),sQuery(id+"F7.wireOp",EDGE,"E1088"),sQuery(id+"F7.wireOp",EDGE,"E1089"),sQuery(id+"F7.wireOp",EDGE,"E1090"),sQuery(id+"F7.wireOp",EDGE,"E1091"),sQuery(id+"F7.wireOp",EDGE,"E1092"),sQuery(id+"F7.wireOp",EDGE,"E1093"),sQuery(id+"F7.wireOp",EDGE,"E1094"),sQuery(id+"F7.wireOp",EDGE,"E1095"),sQuery(id+"F7.wireOp",EDGE,"E1096"),sQuery(id+"F7.wireOp",EDGE,"E1097"),sQuery(id+"F7.wireOp",EDGE,"E1098"),sQuery(id+"F7.wireOp",EDGE,"E1099"),sQuery(id+"F7.wireOp",EDGE,"E1100"),sQuery(id+"F7.wireOp",EDGE,"E1101"),sQuery(id+"F7.wireOp",EDGE,"E1102"),sQuery(id+"F7.wireOp",EDGE,"E1103"),sQuery(id+"F7.wireOp",EDGE,"E1104"),sQuery(id+"F7.wireOp",EDGE,"E1105"),sQuery(id+"F7.wireOp",EDGE,"E1106"),sQuery(id+"F7.wireOp",EDGE,"E1107"),sQuery(id+"F7.wireOp",EDGE,"E1108"),sQuery(id+"F7.wireOp",EDGE,"E1109"),sQuery(id+"F7.wireOp",EDGE,"E1110"),sQuery(id+"F7.wireOp",EDGE,"E1111"),sQuery(id+"F7.wireOp",EDGE,"E1112"),sQuery(id+"F7.wireOp",EDGE,"E1113"),sQuery(id+"F7.wireOp",EDGE,"E1114"),sQuery(id+"F7.wireOp",EDGE,"E1115"),sQuery(id+"F7.wireOp",EDGE,"E1116"),sQuery(id+"F7.wireOp",EDGE,"E1117"),sQuery(id+"F7.wireOp",EDGE,"E1118"),sQuery(id+"F7.wireOp",EDGE,"E1119"),sQuery(id+"F7.wireOp",EDGE,"E1120"),sQuery(id+"F7.wireOp",EDGE,"E1121"),sQuery(id+"F7.wireOp",EDGE,"E1122"),sQuery(id+"F7.wireOp",EDGE,"E1123"),sQuery(id+"F7.wireOp",EDGE,"E1124"),sQuery(id+"F7.wireOp",EDGE,"E1125"),sQuery(id+"F7.wireOp",EDGE,"E1126"),sQuery(id+"F7.wireOp",EDGE,"E1127"),sQuery(id+"F7.wireOp",EDGE,"E1128"),sQuery(id+"F7.wireOp",EDGE,"E1129"),sQuery(id+"F7.wireOp",EDGE,"E1130"),sQuery(id+"F7.wireOp",EDGE,"E1131"),sQuery(id+"F7.wireOp",EDGE,"E1132"),sQuery(id+"F7.wireOp",EDGE,"E1133"),sQuery(id+"F7.wireOp",EDGE,"E1134"),sQuery(id+"F7.wireOp",EDGE,"E1135"),sQuery(id+"F7.wireOp",EDGE,"E1136"),sQuery(id+"F7.wireOp",EDGE,"E1137"),sQuery(id+"F7.wireOp",EDGE,"E1138"),sQuery(id+"F7.wireOp",EDGE,"E1139"),sQuery(id+"F7.wireOp",EDGE,"E1140"),sQuery(id+"F7.wireOp",EDGE,"E1141"),sQuery(id+"F7.wireOp",EDGE,"E1142"),sQuery(id+"F7.wireOp",EDGE,"E1143"),sQuery(id+"F7.wireOp",EDGE,"E1144"),sQuery(id+"F7.wireOp",EDGE,"E1145"),sQuery(id+"F7.wireOp",EDGE,"E1146"),sQuery(id+"F7.wireOp",EDGE,"E1147"),sQuery(id+"F7.wireOp",EDGE,"E1148"),sQuery(id+"F7.wireOp",EDGE,"E1149"),sQuery(id+"F7.wireOp",EDGE,"E1150"),sQuery(id+"F7.wireOp",EDGE,"E1151"),sQuery(id+"F7.wireOp",EDGE,"E1152"),sQuery(id+"F7.wireOp",EDGE,"E1153"),sQuery(id+"F7.wireOp",EDGE,"E1154"),sQuery(id+"F7.wireOp",EDGE,"E1155"),sQuery(id+"F7.wireOp",EDGE,"E1156"),sQuery(id+"F7.wireOp",EDGE,"E1157"),sQuery(id+"F7.wireOp",EDGE,"E1158"),sQuery(id+"F7.wireOp",EDGE,"E1159"),sQuery(id+"F7.wireOp",EDGE,"E1160"),sQuery(id+"F7.wireOp",EDGE,"E1161"),sQuery(id+"F7.wireOp",EDGE,"E1162"),sQuery(id+"F7.wireOp",EDGE,"E1163"),sQuery(id+"F7.wireOp",EDGE,"E1164"),sQuery(id+"F7.wireOp",EDGE,"E1165"),sQuery(id+"F7.wireOp",EDGE,"E1166"),sQuery(id+"F7.wireOp",EDGE,"E1167"),sQuery(id+"F7.wireOp",EDGE,"E1168"),sQuery(id+"F7.wireOp",EDGE,"E1169"),sQuery(id+"F7.wireOp",EDGE,"E1170"),sQuery(id+"F7.wireOp",EDGE,"E1171"),sQuery(id+"F7.wireOp",EDGE,"E1172"),sQuery(id+"F7.wireOp",EDGE,"E1173"),sQuery(id+"F7.wireOp",EDGE,"E1174"),sQuery(id+"F7.wireOp",EDGE,"E1175"),sQuery(id+"F7.wireOp",EDGE,"E1176"),sQuery(id+"F7.wireOp",EDGE,"E1177"),sQuery(id+"F7.wireOp",EDGE,"E1178"),sQuery(id+"F7.wireOp",EDGE,"E1179"),sQuery(id+"F7.wireOp",EDGE,"E1180"),sQuery(id+"F7.wireOp",EDGE,"E1181"),sQuery(id+"F7.wireOp",EDGE,"E1182"),sQuery(id+"F7.wireOp",EDGE,"E1183"),sQuery(id+"F7.wireOp",EDGE,"E1184"),sQuery(id+"F7.wireOp",EDGE,"E1185"),sQuery(id+"F7.wireOp",EDGE,"E1186"),sQuery(id+"F7.wireOp",EDGE,"E1187"),sQuery(id+"F7.wireOp",EDGE,"E1188"),sQuery(id+"F7.wireOp",EDGE,"E1189"),sQuery(id+"F7.wireOp",EDGE,"E1190"),sQuery(id+"F7.wireOp",EDGE,"E1191"),sQuery(id+"F7.wireOp",EDGE,"E1192"),sQuery(id+"F7.wireOp",EDGE,"E1193"),sQuery(id+"F7.wireOp",EDGE,"E1194"),sQuery(id+"F7.wireOp",EDGE,"E1195"),sQuery(id+"F7.wireOp",EDGE,"E1196"),sQuery(id+"F7.wireOp",EDGE,"E1197"),sQuery(id+"F7.wireOp",EDGE,"E1198"),sQuery(id+"F7.wireOp",EDGE,"E1199"),sQuery(id+"F7.wireOp",EDGE,"E1200"),sQuery(id+"F7.wireOp",EDGE,"E1201"),sQuery(id+"F7.wireOp",EDGE,"E1202"),sQuery(id+"F7.wireOp",EDGE,"E1203"),sQuery(id+"F7.wireOp",EDGE,"E1204"),sQuery(id+"F7.wireOp",EDGE,"E1205"),sQuery(id+"F7.wireOp",EDGE,"E1206"),sQuery(id+"F7.wireOp",EDGE,"E1207"),sQuery(id+"F7.wireOp",EDGE,"E1208"),sQuery(id+"F7.wireOp",EDGE,"E1209"),sQuery(id+"F7.wireOp",EDGE,"E1210"),sQuery(id+"F7.wireOp",EDGE,"E1211"),sQuery(id+"F7.wireOp",EDGE,"E1212"),sQuery(id+"F7.wireOp",EDGE,"E1213"),sQuery(id+"F7.wireOp",EDGE,"E1214"),sQuery(id+"F7.wireOp",EDGE,"E1215"),sQuery(id+"F7.wireOp",EDGE,"E1216"),sQuery(id+"F7.wireOp",EDGE,"E1217"),sQuery(id+"F7.wireOp",EDGE,"E1218"),sQuery(id+"F7.wireOp",EDGE,"E1219"),sQuery(id+"F7.wireOp",EDGE,"E1220"),sQuery(id+"F7.wireOp",EDGE,"E1221"),sQuery(id+"F7.wireOp",EDGE,"E1222"),sQuery(id+"F7.wireOp",EDGE,"E1223"),sQuery(id+"F7.wireOp",EDGE,"E1224"),sQuery(id+"F7.wireOp",EDGE,"E1225"),sQuery(id+"F7.wireOp",EDGE,"E1226"),sQuery(id+"F7.wireOp",EDGE,"E1227"),sQuery(id+"F7.wireOp",EDGE,"E1228"),sQuery(id+"F7.wireOp",EDGE,"E1229"),sQuery(id+"F7.wireOp",EDGE,"E1230"),sQuery(id+"F7.wireOp",EDGE,"E1231"),sQuery(id+"F7.wireOp",EDGE,"E1232"),sQuery(id+"F7.wireOp",EDGE,"E1233"),sQuery(id+"F7.wireOp",EDGE,"E1234"),sQuery(id+"F7.wireOp",EDGE,"E1235"),sQuery(id+"F7.wireOp",EDGE,"E1236"),sQuery(id+"F7.wireOp",EDGE,"E1237"),sQuery(id+"F7.wireOp",EDGE,"E1238"),sQuery(id+"F7.wireOp",EDGE,"E1239"),sQuery(id+"F7.wireOp",EDGE,"E1240"),sQuery(id+"F7.wireOp",EDGE,"E1241"),sQuery(id+"F7.wireOp",EDGE,"E1242"),sQuery(id+"F7.wireOp",EDGE,"E1243"),sQuery(id+"F7.wireOp",EDGE,"E1244"),sQuery(id+"F7.wireOp",EDGE,"E1245"),sQuery(id+"F7.wireOp",EDGE,"E1246"),sQuery(id+"F7.wireOp",EDGE,"E1247"),sQuery(id+"F7.wireOp",EDGE,"E1248"),sQuery(id+"F7.wireOp",EDGE,"E1249"),sQuery(id+"F7.wireOp",EDGE,"E1250"),sQuery(id+"F7.wireOp",EDGE,"E1251"),sQuery(id+"F7.wireOp",EDGE,"E1252"),sQuery(id+"F7.wireOp",EDGE,"E1253"),sQuery(id+"F7.wireOp",EDGE,"E1254"),sQuery(id+"F7.wireOp",EDGE,"E1255"),sQuery(id+"F7.wireOp",EDGE,"E1256"),sQuery(id+"F7.wireOp",EDGE,"E1257"),sQuery(id+"F7.wireOp",EDGE,"E1258"),sQuery(id+"F7.wireOp",EDGE,"E1259"),sQuery(id+"F7.wireOp",EDGE,"E1260"),sQuery(id+"F7.wireOp",EDGE,"E1261"),sQuery(id+"F7.wireOp",EDGE,"E1262"),sQuery(id+"F7.wireOp",EDGE,"E1263"),sQuery(id+"F7.wireOp",EDGE,"E1264"),sQuery(id+"F7.wireOp",EDGE,"E1265"),sQuery(id+"F7.wireOp",EDGE,"E1266"),sQuery(id+"F7.wireOp",EDGE,"E1267"),sQuery(id+"F7.wireOp",EDGE,"E1268"),sQuery(id+"F7.wireOp",EDGE,"E1269"),sQuery(id+"F7.wireOp",EDGE,"E1270"),sQuery(id+"F7.wireOp",EDGE,"E1271"),sQuery(id+"F7.wireOp",EDGE,"E1272"),sQuery(id+"F7.wireOp",EDGE,"E1273"),sQuery(id+"F7.wireOp",EDGE,"E1274"),sQuery(id+"F7.wireOp",EDGE,"E1275"),sQuery(id+"F7.wireOp",EDGE,"E1276"),sQuery(id+"F7.wireOp",EDGE,"E1277"),sQuery(id+"F7.wireOp",EDGE,"E1278"),sQuery(id+"F7.wireOp",EDGE,"E1279"),sQuery(id+"F7.wireOp",EDGE,"E1280"),sQuery(id+"F7.wireOp",EDGE,"E1281"),sQuery(id+"F7.wireOp",EDGE,"E1282"),sQuery(id+"F7.wireOp",EDGE,"E1283"),sQuery(id+"F7.wireOp",EDGE,"E1284"),sQuery(id+"F7.wireOp",EDGE,"E1285"),sQuery(id+"F7.wireOp",EDGE,"E1286"),sQuery(id+"F7.wireOp",EDGE,"E1287"),sQuery(id+"F7.wireOp",EDGE,"E1288"),sQuery(id+"F7.wireOp",EDGE,"E1289"),sQuery(id+"F7.wireOp",EDGE,"E1290"),sQuery(id+"F7.wireOp",EDGE,"E1291"),sQuery(id+"F7.wireOp",EDGE,"E1292"),sQuery(id+"F7.wireOp",EDGE,"E1293"),sQuery(id+"F7.wireOp",EDGE,"E1294"),sQuery(id+"F7.wireOp",EDGE,"E1295"),sQuery(id+"F7.wireOp",EDGE,"E1296"),sQuery(id+"F7.wireOp",EDGE,"E1297"),sQuery(id+"F7.wireOp",EDGE,"E1298"),sQuery(id+"F7.wireOp",EDGE,"E1299"),sQuery(id+"F7.wireOp",EDGE,"E1300"),sQuery(id+"F7.wireOp",EDGE,"E1301"),sQuery(id+"F7.wireOp",EDGE,"E1302"),sQuery(id+"F7.wireOp",EDGE,"E1303"),sQuery(id+"F7.wireOp",EDGE,"E1304"),sQuery(id+"F7.wireOp",EDGE,"E1305"),sQuery(id+"F7.wireOp",EDGE,"E1306"),sQuery(id+"F7.wireOp",EDGE,"E1307"),sQuery(id+"F7.wireOp",EDGE,"E1308"),sQuery(id+"F7.wireOp",EDGE,"E1309"),sQuery(id+"F7.wireOp",EDGE,"E1310"),sQuery(id+"F7.wireOp",EDGE,"E1311"),sQuery(id+"F7.wireOp",EDGE,"E1312"),sQuery(id+"F7.wireOp",EDGE,"E1313"),sQuery(id+"F7.wireOp",EDGE,"E1314"),sQuery(id+"F7.wireOp",EDGE,"E1315"),sQuery(id+"F7.wireOp",EDGE,"E1316"),sQuery(id+"F7.wireOp",EDGE,"E1317"),sQuery(id+"F7.wireOp",EDGE,"E1318"),sQuery(id+"F7.wireOp",EDGE,"E1319"),sQuery(id+"F7.wireOp",EDGE,"E1320"),sQuery(id+"F7.wireOp",EDGE,"E1321"),sQuery(id+"F7.wireOp",EDGE,"E1322"),sQuery(id+"F7.wireOp",EDGE,"E1323"),sQuery(id+"F7.wireOp",EDGE,"E1324"),sQuery(id+"F7.wireOp",EDGE,"E1325"),sQuery(id+"F7.wireOp",EDGE,"E1326"),sQuery(id+"F7.wireOp",EDGE,"E1327"),sQuery(id+"F7.wireOp",EDGE,"E1328"),sQuery(id+"F7.wireOp",EDGE,"E1329"),sQuery(id+"F7.wireOp",EDGE,"E1330"),sQuery(id+"F7.wireOp",EDGE,"E1331"),sQuery(id+"F7.wireOp",EDGE,"E1332"),sQuery(id+"F7.wireOp",EDGE,"E1333"),sQuery(id+"F7.wireOp",EDGE,"E1334"),sQuery(id+"F7.wireOp",EDGE,"E1335"),sQuery(id+"F7.wireOp",EDGE,"E1336"),sQuery(id+"F7.wireOp",EDGE,"E1337"),sQuery(id+"F7.wireOp",EDGE,"E1338"),sQuery(id+"F7.wireOp",EDGE,"E1339"),sQuery(id+"F7.wireOp",EDGE,"E1340"),sQuery(id+"F7.wireOp",EDGE,"E1341"),sQuery(id+"F7.wireOp",EDGE,"E1342"),sQuery(id+"F7.wireOp",EDGE,"E1343"),sQuery(id+"F7.wireOp",EDGE,"E1344"),sQuery(id+"F7.wireOp",EDGE,"E1345"),sQuery(id+"F7.wireOp",EDGE,"E1346"),sQuery(id+"F7.wireOp",EDGE,"E1347"),sQuery(id+"F7.wireOp",EDGE,"E1348"),sQuery(id+"F7.wireOp",EDGE,"E1349"),sQuery(id+"F7.wireOp",EDGE,"E1350"),sQuery(id+"F7.wireOp",EDGE,"E1351"),sQuery(id+"F7.wireOp",EDGE,"E1352"),sQuery(id+"F7.wireOp",EDGE,"E1353"),sQuery(id+"F7.wireOp",EDGE,"E1354"),sQuery(id+"F7.wireOp",EDGE,"E1355"),sQuery(id+"F7.wireOp",EDGE,"E1356"),sQuery(id+"F7.wireOp",EDGE,"E1357"),sQuery(id+"F7.wireOp",EDGE,"E1358"),sQuery(id+"F7.wireOp",EDGE,"E1359"),sQuery(id+"F7.wireOp",EDGE,"E1360"),sQuery(id+"F7.wireOp",EDGE,"E1361"),sQuery(id+"F7.wireOp",EDGE,"E1362"),sQuery(id+"F7.wireOp",EDGE,"E1363"),sQuery(id+"F7.wireOp",EDGE,"E1364"),sQuery(id+"F7.wireOp",EDGE,"E1365"),sQuery(id+"F7.wireOp",EDGE,"E1366"),sQuery(id+"F7.wireOp",EDGE,"E1367"),sQuery(id+"F7.wireOp",EDGE,"E1368"),sQuery(id+"F7.wireOp",EDGE,"E1369"),sQuery(id+"F7.wireOp",EDGE,"E1370"),sQuery(id+"F7.wireOp",EDGE,"E1371"),sQuery(id+"F7.wireOp",EDGE,"E1372"),sQuery(id+"F7.wireOp",EDGE,"E1373"),sQuery(id+"F7.wireOp",EDGE,"E1374"),sQuery(id+"F7.wireOp",EDGE,"E1375"),sQuery(id+"F7.wireOp",EDGE,"E1376"),sQuery(id+"F7.wireOp",EDGE,"E1377"),sQuery(id+"F7.wireOp",EDGE,"E1378"),sQuery(id+"F7.wireOp",EDGE,"E1379"),sQuery(id+"F7.wireOp",EDGE,"E1380"),sQuery(id+"F7.wireOp",EDGE,"E1381"),sQuery(id+"F7.wireOp",EDGE,"E1382"),sQuery(id+"F7.wireOp",EDGE,"E1383"),sQuery(id+"F7.wireOp",EDGE,"E1384"),sQuery(id+"F7.wireOp",EDGE,"E1385"),sQuery(id+"F7.wireOp",EDGE,"E1386"),sQuery(id+"F7.wireOp",EDGE,"E1387"),sQuery(id+"F7.wireOp",EDGE,"E1388"),sQuery(id+"F7.wireOp",EDGE,"E1389"),sQuery(id+"F7.wireOp",EDGE,"E1390"),sQuery(id+"F7.wireOp",EDGE,"E1391"),sQuery(id+"F7.wireOp",EDGE,"E1392"),sQuery(id+"F7.wireOp",EDGE,"E1393"),sQuery(id+"F7.wireOp",EDGE,"E1394"),sQuery(id+"F7.wireOp",EDGE,"E1395"),sQuery(id+"F7.wireOp",EDGE,"E1396"),sQuery(id+"F7.wireOp",EDGE,"E1397"),sQuery(id+"F7.wireOp",EDGE,"E1398"),sQuery(id+"F7.wireOp",EDGE,"E1399"),sQuery(id+"F7.wireOp",EDGE,"E1400"),sQuery(id+"F7.wireOp",EDGE,"E1401"),sQuery(id+"F7.wireOp",EDGE,"E1402"),sQuery(id+"F7.wireOp",EDGE,"E1403"),sQuery(id+"F7.wireOp",EDGE,"E1404"),sQuery(id+"F7.wireOp",EDGE,"E1405"),sQuery(id+"F7.wireOp",EDGE,"E1406"),sQuery(id+"F7.wireOp",EDGE,"E1407"),sQuery(id+"F7.wireOp",EDGE,"E1408"),sQuery(id+"F7.wireOp",EDGE,"E1409"),sQuery(id+"F7.wireOp",EDGE,"E1410"),sQuery(id+"F7.wireOp",EDGE,"E1411"),sQuery(id+"F7.wireOp",EDGE,"E1412"),sQuery(id+"F7.wireOp",EDGE,"E1413"),sQuery(id+"F7.wireOp",EDGE,"E1414"),sQuery(id+"F7.wireOp",EDGE,"E1415"),sQuery(id+"F7.wireOp",EDGE,"E1416"),sQuery(id+"F7.wireOp",EDGE,"E1417"),sQuery(id+"F7.wireOp",EDGE,"E1418"),sQuery(id+"F7.wireOp",EDGE,"E1419"),sQuery(id+"F7.wireOp",EDGE,"E1420"),sQuery(id+"F7.wireOp",EDGE,"E1421"),sQuery(id+"F7.wireOp",EDGE,"E1422"),sQuery(id+"F7.wireOp",EDGE,"E1423"),sQuery(id+"F7.wireOp",EDGE,"E1424"),sQuery(id+"F7.wireOp",EDGE,"E1425"),sQuery(id+"F7.wireOp",EDGE,"E1426"),sQuery(id+"F7.wireOp",EDGE,"E1427"),sQuery(id+"F7.wireOp",EDGE,"E1428"),sQuery(id+"F7.wireOp",EDGE,"E1429"),sQuery(id+"F7.wireOp",EDGE,"E1430"),sQuery(id+"F7.wireOp",EDGE,"E1431"),sQuery(id+"F7.wireOp",EDGE,"E1432"),sQuery(id+"F7.wireOp",EDGE,"E1433"),sQuery(id+"F7.wireOp",EDGE,"E1434"),sQuery(id+"F7.wireOp",EDGE,"E1435"),sQuery(id+"F7.wireOp",EDGE,"E1436"),sQuery(id+"F7.wireOp",EDGE,"E1437"),sQuery(id+"F7.wireOp",EDGE,"E1438"),sQuery(id+"F7.wireOp",EDGE,"E1439"),sQuery(id+"F7.wireOp",EDGE,"E1440"),sQuery(id+"F7.wireOp",EDGE,"E1441"),sQuery(id+"F7.wireOp",EDGE,"E1442"),sQuery(id+"F7.wireOp",EDGE,"E1443"),sQuery(id+"F7.wireOp",EDGE,"E1444"),sQuery(id+"F7.wireOp",EDGE,"E1445"),sQuery(id+"F7.wireOp",EDGE,"E1446"),sQuery(id+"F7.wireOp",EDGE,"E1447"),sQuery(id+"F7.wireOp",EDGE,"E1448"),sQuery(id+"F7.wireOp",EDGE,"E1449"),sQuery(id+"F7.wireOp",EDGE,"E1450"),sQuery(id+"F7.wireOp",EDGE,"E1451"),sQuery(id+"F7.wireOp",EDGE,"E1452"),sQuery(id+"F7.wireOp",EDGE,"E1453"),sQuery(id+"F7.wireOp",EDGE,"E1454"),sQuery(id+"F7.wireOp",EDGE,"E1455"),sQuery(id+"F7.wireOp",EDGE,"E1456"),sQuery(id+"F7.wireOp",EDGE,"E1457"),sQuery(id+"F7.wireOp",EDGE,"E1458"),sQuery(id+"F7.wireOp",EDGE,"E1459"),sQuery(id+"F7.wireOp",EDGE,"E1460"),sQuery(id+"F7.wireOp",EDGE,"E1461"),sQuery(id+"F7.wireOp",EDGE,"E1462"),sQuery(id+"F7.wireOp",EDGE,"E1463"),sQuery(id+"F7.wireOp",EDGE,"E1464"),sQuery(id+"F7.wireOp",EDGE,"E1465"),sQuery(id+"F7.wireOp",EDGE,"E1466"),sQuery(id+"F7.wireOp",EDGE,"E1467"),sQuery(id+"F7.wireOp",EDGE,"E1468"),sQuery(id+"F7.wireOp",EDGE,"E1469"),sQuery(id+"F7.wireOp",EDGE,"E1470"),sQuery(id+"F7.wireOp",EDGE,"E1471"),sQuery(id+"F7.wireOp",EDGE,"E1472"),sQuery(id+"F7.wireOp",EDGE,"E1473"),sQuery(id+"F7.wireOp",EDGE,"E1474"),sQuery(id+"F7.wireOp",EDGE,"E1475"),sQuery(id+"F7.wireOp",EDGE,"E1476"),sQuery(id+"F7.wireOp",EDGE,"E1477"),sQuery(id+"F7.wireOp",EDGE,"E1478"),sQuery(id+"F7.wireOp",EDGE,"E1479"),sQuery(id+"F7.wireOp",EDGE,"E1480"),sQuery(id+"F7.wireOp",EDGE,"E1481"),sQuery(id+"F7.wireOp",EDGE,"E1482"),sQuery(id+"F7.wireOp",EDGE,"E1483"),sQuery(id+"F7.wireOp",EDGE,"E1484"),sQuery(id+"F7.wireOp",EDGE,"E1485"),sQuery(id+"F7.wireOp",EDGE,"E1486"),sQuery(id+"F7.wireOp",EDGE,"E1487"),sQuery(id+"F7.wireOp",EDGE,"E1488"),sQuery(id+"F7.wireOp",EDGE,"E1489"),sQuery(id+"F7.wireOp",EDGE,"E1490"),sQuery(id+"F7.wireOp",EDGE,"E1491"),sQuery(id+"F7.wireOp",EDGE,"E1492"),sQuery(id+"F7.wireOp",EDGE,"E1493"),sQuery(id+"F7.wireOp",EDGE,"E1494"),sQuery(id+"F7.wireOp",EDGE,"E1495"),sQuery(id+"F7.wireOp",EDGE,"E1496"),sQuery(id+"F7.wireOp",EDGE,"E1497"),sQuery(id+"F7.wireOp",EDGE,"E1498"),sQuery(id+"F7.wireOp",EDGE,"E1499"),sQuery(id+"F7.wireOp",EDGE,"E1500"),sQuery(id+"F7.wireOp",EDGE,"E1501"),sQuery(id+"F7.wireOp",EDGE,"E1502"),sQuery(id+"F7.wireOp",EDGE,"E1503"),sQuery(id+"F7.wireOp",EDGE,"E1504"),sQuery(id+"F7.wireOp",EDGE,"E1505"),sQuery(id+"F7.wireOp",EDGE,"E1506"),sQuery(id+"F7.wireOp",EDGE,"E1507"),sQuery(id+"F7.wireOp",EDGE,"E1508"),sQuery(id+"F7.wireOp",EDGE,"E1509"),sQuery(id+"F7.wireOp",EDGE,"E1510"),sQuery(id+"F7.wireOp",EDGE,"E1511"),sQuery(id+"F7.wireOp",EDGE,"E1512"),sQuery(id+"F7.wireOp",EDGE,"E1513"),sQuery(id+"F7.wireOp",EDGE,"E1514"),sQuery(id+"F7.wireOp",EDGE,"E1515"),sQuery(id+"F7.wireOp",EDGE,"E1516"),sQuery(id+"F7.wireOp",EDGE,"E1517"),sQuery(id+"F7.wireOp",EDGE,"E1518"),sQuery(id+"F7.wireOp",EDGE,"E1519"),sQuery(id+"F7.wireOp",EDGE,"E1520"),sQuery(id+"F7.wireOp",EDGE,"E1521"),sQuery(id+"F7.wireOp",EDGE,"E1522"),sQuery(id+"F7.wireOp",EDGE,"E1523"),sQuery(id+"F7.wireOp",EDGE,"E1524"),sQuery(id+"F7.wireOp",EDGE,"E1525"),sQuery(id+"F7.wireOp",EDGE,"E1526"),sQuery(id+"F7.wireOp",EDGE,"E1527"),sQuery(id+"F7.wireOp",EDGE,"E1528"),sQuery(id+"F7.wireOp",EDGE,"E1529"),sQuery(id+"F7.wireOp",EDGE,"E1530"),sQuery(id+"F7.wireOp",EDGE,"E1531"),sQuery(id+"F7.wireOp",EDGE,"E1532"),sQuery(id+"F7.wireOp",EDGE,"E1533"),sQuery(id+"F7.wireOp",EDGE,"E1534"),sQuery(id+"F7.wireOp",EDGE,"E1535"),sQuery(id+"F7.wireOp",EDGE,"E1536"),sQuery(id+"F7.wireOp",EDGE,"E1537"),sQuery(id+"F7.wireOp",EDGE,"E1538"),sQuery(id+"F7.wireOp",EDGE,"E1539"),sQuery(id+"F7.wireOp",EDGE,"E1540"),sQuery(id+"F7.wireOp",EDGE,"E1541"),sQuery(id+"F7.wireOp",EDGE,"E1542"),sQuery(id+"F7.wireOp",EDGE,"E1543"),sQuery(id+"F7.wireOp",EDGE,"E1544"),sQuery(id+"F7.wireOp",EDGE,"E1545"),sQuery(id+"F7.wireOp",EDGE,"E1546"),sQuery(id+"F7.wireOp",EDGE,"E1547"),sQuery(id+"F7.wireOp",EDGE,"E1548"),sQuery(id+"F7.wireOp",EDGE,"E1549"),sQuery(id+"F7.wireOp",EDGE,"E1550"),sQuery(id+"F7.wireOp",EDGE,"E1551"),sQuery(id+"F7.wireOp",EDGE,"E1552"),sQuery(id+"F7.wireOp",EDGE,"E1553"),sQuery(id+"F7.wireOp",EDGE,"E1554"),sQuery(id+"F7.wireOp",EDGE,"E1555"),sQuery(id+"F7.wireOp",EDGE,"E1556"),sQuery(id+"F7.wireOp",EDGE,"E1557"),sQuery(id+"F7.wireOp",EDGE,"E1558"),sQuery(id+"F7.wireOp",EDGE,"E1559"),sQuery(id+"F7.wireOp",EDGE,"E1560"),sQuery(id+"F7.wireOp",EDGE,"E1561")])],"isStart":false});
            var sketch = newSketch(context, id + "F13", { "sketchPlane" : qUnion([Q0])});
            skCircle(sketch, "E1566", {"center": v(-45.68, 35.61) * mm, "radius": 1.6 * mm});
            skPoint(sketch, "E1566.first.point", {"position": v(-45.7, 34) * mm});
            skPoint(sketch, "E1566.second.point", {"position": v(-45.68, 37.22) * mm});
            skPoint(sketch, "E1566.third.point", {"position": v(-44.08, 35.57) * mm});
            skCircle(sketch, "E1567", {"center": v(36.8, 35.61) * mm, "radius": 1.6 * mm});
            skPoint(sketch, "E1567.first.point", {"position": v(36.78, 34) * mm});
            skPoint(sketch, "E1567.second.point", {"position": v(36.8, 37.22) * mm});
            skPoint(sketch, "E1567.third.point", {"position": v(38.4, 35.57) * mm});
            skCircle(sketch, "E1568", {"center": v(35.53, -12.61) * mm, "radius": 1.6 * mm});
            skPoint(sketch, "E1568.first.point", {"position": v(35.5, -14.22) * mm});
            skPoint(sketch, "E1568.second.point", {"position": v(35.53, -11) * mm});
            skPoint(sketch, "E1568.third.point", {"position": v(37.13, -12.65) * mm});
            skCircle(sketch, "E1569", {"center": v(-39.36, -12.61) * mm, "radius": 1.6 * mm});
            skPoint(sketch, "E1569.first.point", {"position": v(-39.37, -14.22) * mm});
            skPoint(sketch, "E1569.second.point", {"position": v(-39.3, -11) * mm});
            skPoint(sketch, "E1569.third.point", {"position": v(-40.96, -12.61) * mm});
            skCircle(sketch, "E1570", {"center": v(-15.23, 2.62) * mm, "radius": 1.6 * mm});
            skPoint(sketch, "E1570.first.point", {"position": v(-15.25, 1.02) * mm});
            skPoint(sketch, "E1570.second.point", {"position": v(-15.23, 4.23) * mm});
            skPoint(sketch, "E1570.third.point", {"position": v(-13.63, 2.7) * mm});
            skCircle(sketch, "E1571", {"center": v(-15.23, 30.53) * mm, "radius": 1.6 * mm});
            skPoint(sketch, "E1571.first.point", {"position": v(-15.25, 28.92) * mm});
            skPoint(sketch, "E1571.second.point", {"position": v(-15.23, 32.14) * mm});
            skPoint(sketch, "E1571.third.point", {"position": v(-13.63, 30.6) * mm});
            skSolve(sketch);
        }
        {
            var Q0;
            Q0=makeQuery(id+"F13.imprint","IMPRINT",FACE,{"disambiguationData":[TD([[makeQuery(id+"F13.imprint","IMPRINT",EDGE,{"derivedFrom":makeQuery(id+"F8.opExtrude","CAP_EDGE",EDGE,{"disambiguationData":[OSD([sQuery(id+"F7.wireOp",EDGE,"E811")])],"isStart":false})}),1.0]])]});
            var Q1;
            Q1=makeQuery(id+"F13.imprint","IMPRINT",FACE,{"disambiguationData":[TD([[makeQuery(id+"F13.imprint","IMPRINT",EDGE,{"derivedFrom":makeQuery(id+"F8.opExtrude","CAP_EDGE",EDGE,{"disambiguationData":[OSD([sQuery(id+"F7.wireOp",EDGE,"E1381")])],"isStart":false})}),1.0]])]});
            var Q2;
            Q2=makeQuery(id+"F13.imprint","IMPRINT",FACE,{"disambiguationData":[TD([[makeQuery(id+"F13.imprint","IMPRINT",EDGE,{"derivedFrom":makeQuery(id+"F8.opExtrude","CAP_EDGE",EDGE,{"disambiguationData":[OSD([sQuery(id+"F7.wireOp",EDGE,"E449")])],"isStart":false})}),1.0]])]});
            var Q3;
            Q3=makeQuery(id+"F13.imprint","IMPRINT",FACE,{"disambiguationData":[TD([[makeQuery(id+"F13.imprint","IMPRINT",EDGE,{"derivedFrom":makeQuery(id+"F8.opExtrude","CAP_EDGE",EDGE,{"disambiguationData":[OSD([sQuery(id+"F7.wireOp",EDGE,"E992")])],"isStart":false})}),1.0]])]});
            var Q4;
            Q4=makeQuery(id+"F13.imprint","IMPRINT",FACE,{"disambiguationData":[TD([[makeQuery(id+"F13.imprint","IMPRINT",EDGE,{"derivedFrom":makeQuery(id+"F8.opExtrude","CAP_EDGE",EDGE,{"disambiguationData":[OSD([sQuery(id+"F7.wireOp",EDGE,"E1173")])],"isStart":false})}),1.0]])]});
            var Q5;
            Q5=makeQuery(id+"F13.imprint","IMPRINT",FACE,{"disambiguationData":[TD([[makeQuery(id+"F13.imprint","IMPRINT",EDGE,{"derivedFrom":makeQuery(id+"F8.opExtrude","CAP_EDGE",EDGE,{"disambiguationData":[OSD([sQuery(id+"F7.wireOp",EDGE,"E630")])],"isStart":false})}),1.0]])]});
            extrude(context, id + "F14", {"entities" : qUnion([Q0, Q1, Q2, Q3, Q4, Q5]), "operationType" : NewBodyOperationType.REMOVE, "endBound" : BoundingType.SYMMETRIC, "depth" : 25 * mm, "offsetDistance" : 25 * mm});
        }
        {
            var Q0;
            Q0=makeQuery(id+"F13.imprint","IMPRINT",FACE,{"disambiguationData":[TD([[makeQuery(id+"F13.imprint","IMPRINT",EDGE,{"derivedFrom":makeQuery(id+"F8.opExtrude","CAP_EDGE",EDGE,{"disambiguationData":[OSD([sQuery(id+"F7.wireOp",EDGE,"E811")])],"isStart":false})}),1.0]])]});
            var Q1;
            Q1=makeQuery(id+"F13.imprint","IMPRINT",FACE,{"disambiguationData":[TD([[makeQuery(id+"F13.imprint","IMPRINT",EDGE,{"derivedFrom":makeQuery(id+"F8.opExtrude","CAP_EDGE",EDGE,{"disambiguationData":[OSD([sQuery(id+"F7.wireOp",EDGE,"E1381")])],"isStart":false})}),1.0]])]});
            var Q2;
            Q2=makeQuery(id+"F13.imprint","IMPRINT",FACE,{"disambiguationData":[TD([[makeQuery(id+"F13.imprint","IMPRINT",EDGE,{"derivedFrom":makeQuery(id+"F8.opExtrude","CAP_EDGE",EDGE,{"disambiguationData":[OSD([sQuery(id+"F7.wireOp",EDGE,"E449")])],"isStart":false})}),1.0]])]});
            var Q3;
            Q3=makeQuery(id+"F13.imprint","IMPRINT",FACE,{"disambiguationData":[TD([[makeQuery(id+"F13.imprint","IMPRINT",EDGE,{"derivedFrom":makeQuery(id+"F8.opExtrude","CAP_EDGE",EDGE,{"disambiguationData":[OSD([sQuery(id+"F7.wireOp",EDGE,"E630")])],"isStart":false})}),1.0]])]});
            extrude(context, id + "F15", {"entities" : qUnion([Q0, Q1, Q2, Q3]), "operationType" : NewBodyOperationType.REMOVE, "endBound" : BoundingType.SYMMETRIC, "depth" : 25 * mm, "offsetDistance" : 25 * mm});
        }
    });
